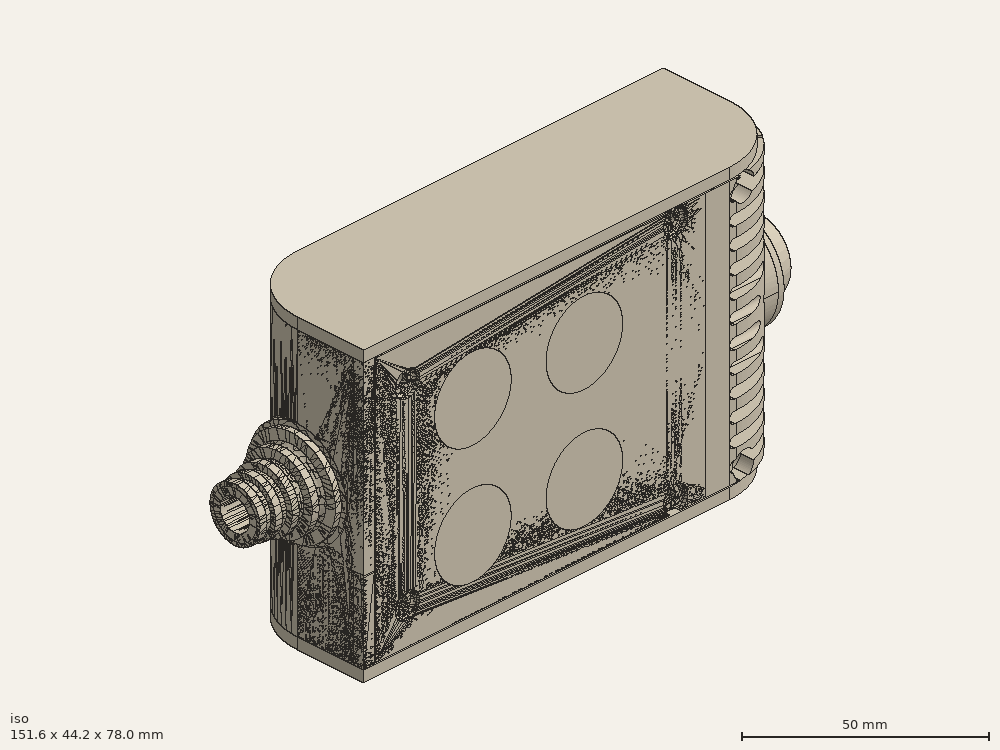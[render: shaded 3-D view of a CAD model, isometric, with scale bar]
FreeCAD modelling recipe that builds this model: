
FCSTD DOCUMENT  (FreeCAD 0.19R0.19.2)
Label: enclosure_172FCStd
License: All rights reserved
LicenseURL: http://en.wikipedia.org/wiki/All_rights_reserved
objects: Part::Revolution×146, Part::MultiFuse×141, Part::Feature×140, Sketcher::SketchObject×78, Part::Cut×66, Part::Cylinder×66, Part::Extrusion×63, Part::Fillet×56, Part::Box×36, App::MeasureDistance×4
note: 792 computed .brp shape members not serialized (recipe doc carries the construction recipe); baked Part::Feature solids carry a one-line shape summary decoded from their .brp

FEATURE [Sketcher::SketchObject] Sketch  label="topSketch"
  FullyConstrained = true
  sketch-geometry (20):
    g0: LineSegment StartX=5.21097e-06 StartY=3 StartZ=0 EndX=5.21097e-06 EndY=19 EndZ=0
    g1: ArcOfCircle CenterX=19 CenterY=19 CenterZ=0 NormalX=0 NormalY=0 NormalZ=1 AngleXU=0 Radius=19 StartAngle=1.5708 EndAngle=3.14159
    g2: ArcOfCircle CenterX=19 CenterY=19 CenterZ=0 NormalX=0 NormalY=0 NormalZ=1 AngleXU=0 Radius=16 StartAngle=1.5708 EndAngle=3.14159
    g3: LineSegment StartX=114 StartY=35 StartZ=0 EndX=19 EndY=35 EndZ=0
    g4: LineSegment StartX=5.21097e-06 StartY=3 StartZ=0 EndX=5.21097e-06 EndY=0 EndZ=0
    g5: LineSegment StartX=3 StartY=0 StartZ=0 EndX=5.21097e-06 EndY=0 EndZ=0
    g6: LineSegment StartX=3 StartY=19 StartZ=0 EndX=3 EndY=0 EndZ=0
    g7: LineSegment StartX=19 StartY=38 StartZ=0 EndX=124 EndY=38 EndZ=0
    g8: Circle CenterX=119 CenterY=35 CenterZ=0 NormalX=0 NormalY=0 NormalZ=1 AngleXU=0 Radius=1
    g9: Circle CenterX=121 CenterY=35 CenterZ=0 NormalX=0 NormalY=0 NormalZ=1 AngleXU=0 Radius=1
    g10: Circle CenterX=121 CenterY=33 CenterZ=0 NormalX=0 NormalY=0 NormalZ=1 AngleXU=0 Radius=1
    g11: BSplineCurve PolesCount=3 KnotsCount=2 Degree=2 IsPeriodic=0
    g12: GeomPoint X=119 Y=35 Z=0
    g13: GeomPoint X=121 Y=33 Z=0
    g14: LineSegment StartX=119 StartY=35 StartZ=0 EndX=114 EndY=35 EndZ=0
    g15: ArcOfCircle CenterX=105 CenterY=19 CenterZ=0 NormalX=0 NormalY=0 NormalZ=1 AngleXU=0 Radius=19 StartAngle=5.7297 EndAngle=6.28319
    g16: ArcOfCircle CenterX=105 CenterY=19 CenterZ=0 NormalX=0 NormalY=0 NormalZ=1 AngleXU=0 Radius=16 StartAngle=5.60905 EndAngle=6.28319
    g17: LineSegment StartX=121 StartY=33 StartZ=0 EndX=121 EndY=19 EndZ=0
    g18: LineSegment StartX=124 StartY=38 StartZ=0 EndX=124 EndY=19 EndZ=0
    g19: LineSegment StartX=117.5 StartY=9.01251 StartZ=0 EndX=121.163 EndY=9.0125 EndZ=0
  constraints (46):
    c: Vertical(g0)
    c: Block(g0)
    c: Coincident(g1,g0)
    c: Block(g1)
    c: Coincident(g2,g1)
    c: Block(g2)
    c: Coincident(g3,g2)
    c: Horizontal(g3)
    c: Tangent(g3,g2)
    c: Coincident(g4,g0)
    c: Distance(g4) = 3
    c: Vertical(g4)
    c: Coincident(g5,g4)
    c: Horizontal(g5)
    c: Coincident(g6,g2)
    c: Coincident(g6,g5)
    c: Vertical(g6)
    c: Horizontal(g7)
    c: Distance(g7) = 105
    c: Coincident(g7,g1)
    c: Block(g3)
    c: Weight(g8) = 1
    c: Equal(g8,g9)
    c: Equal(g8,g10)
    c: InternalAlignment(g8,g11)
    c: InternalAlignment(g9,g11)
    c: InternalAlignment(g10,g11)
    c: InternalAlignment(g12,g11)
    c: InternalAlignment(g13,g11)
    c: Block(g11)
    c: Coincident(g14,g11)
    c: Coincident(g14,g3)
    c: Horizontal(g14)
    c: Block(g15)
    c: Coincident(g16,g15)
    c: Block(g16)
    c: Coincident(g17,g11)
    c: Coincident(g17,g16)
    c: Vertical(g17)
    c: Distance(g17) = 14
    c: Coincident(g18,g7)
    c: Coincident(g18,g15)
    c: Vertical(g18)
    c: Distance(g18) = 19
    c: Coincident(g19,g16)
    c: Coincident(g19,g15)
FEATURE [Sketcher::SketchObject] Sketch001  label="bottomSketch"
  FullyConstrained = true
  sketch-geometry (32):
    g0: LineSegment StartX=3.3 StartY=-6.03275e-07 StartZ=0 EndX=98 EndY=-6.03275e-07 EndZ=0
    g1: ArcOfCircle CenterX=98 CenterY=19 CenterZ=0 NormalX=0 NormalY=0 NormalZ=1 AngleXU=0 Radius=19 StartAngle=4.71239 EndAngle=5.71103
    g2: LineSegment StartX=6.3 StartY=8 StartZ=0 EndX=3.3 EndY=8 EndZ=0
    g3: LineSegment StartX=3.3 StartY=8 StartZ=0 EndX=3.3 EndY=-6.03275e-07 EndZ=0
    g4: ArcOfCircle CenterX=8.3 CenterY=5 CenterZ=0 NormalX=0 NormalY=0 NormalZ=1 AngleXU=0 Radius=2 StartAngle=3.14159 EndAngle=4.71239
    g5: LineSegment StartX=6.3 StartY=8 StartZ=0 EndX=6.3 EndY=5 EndZ=0
    g6: ArcOfCircle CenterX=98 CenterY=19 CenterZ=0 NormalX=0 NormalY=0 NormalZ=1 AngleXU=0 Radius=12.7 StartAngle=4.71239 EndAngle=6.28319
    g7: LineSegment StartX=94.7 StartY=3 StartZ=0 EndX=8.3 EndY=3 EndZ=0
    g8-g12: Circle x5 (B-spline internal-alignment scaffolding for g13; pole/knot coordinates omitted)
    g13: BSplineCurve PolesCount=5 KnotsCount=3 Degree=3 IsPeriodic=0
    g14: GeomPoint X=98 Y=6.3 Z=0
    g15: GeomPoint X=96.3938 Y=4.71946 Z=0
    g16: GeomPoint X=94.7 Y=3 Z=0
    g17-g23: Circle x7 (B-spline internal-alignment scaffolding for g24; pole/knot coordinates omitted)
    g24: BSplineCurve PolesCount=7 KnotsCount=5 Degree=3 IsPeriodic=0
    g25-g29: GeomPoint x5 (B-spline internal-alignment scaffolding for g24; pole/knot coordinates omitted)
    g30: ArcOfCircle CenterX=98 CenterY=19 CenterZ=0 NormalX=0 NormalY=0 NormalZ=1 AngleXU=0 Radius=15.7 StartAngle=5.81226 EndAngle=6.28319
    g31: LineSegment StartX=110.7 StartY=19 StartZ=0 EndX=113.7 EndY=19 EndZ=0
  constraints (41):
    c: Horizontal(g0)
    c: Coincident(g1,g0)
    c: Block(g1)
    c: Horizontal(g2)
    c: Distance(g2) = 3
    c: Coincident(g3,g2)
    c: Vertical(g3)
    c: Coincident(g3,g0)
    c: Block(g4)
    c: Block(g2)
    c: Coincident(g5,g2)
    c: Coincident(g5,g4)
    c: Vertical(g5)
    c: Coincident(g6,g1)
    c: Block(g6)
    c: Coincident(g7,g4)
    c: Horizontal(g7)
    c: Block(g0)
    c: Block(g7)
    c: Block(g3)
    c: Coincident(g13,g6)
    c: Weight(g8) = 1
    c: Equal(g8, g9-g12) x4
    c: Coincident(g13,g7)
    c: InternalAlignment(g8-g12 -> g13) x5
    c: InternalAlignment(g14,g13)
    c: InternalAlignment(g15,g13)
    c: InternalAlignment(g16,g13)
    c: Block(g13)
    c: Weight(g17) = 1
    c: Equal(g17, g18-g23) x6
    c: Coincident(g24,g1)
    c: InternalAlignment(g17-g23 -> g24) x7
    c: InternalAlignment(g25-g29 -> g24) x5
    c: Block(g24)
    c: Coincident(g30,g24)
    c: Coincident(g31,g6)
    c: Coincident(g31,g30)
    c: Horizontal(g31)
    c: Block(g31)
    c: Block(g30)
FEATURE [Part::Extrusion] Extrude  label="top"
  Base = -> Sketch
  Dir = (0,0,1)
  DirMode = 2
  FaceMakerClass = Part::FaceMakerBullseye
  LengthFwd = 72
  LengthRev = 0
  Solid = true
  Symmetric = false
FEATURE [Part::Extrusion] Extrude001  label="bottom"
  Base = -> Sketch001
  Dir = (0,0,1)
  DirMode = 2
  FaceMakerClass = Part::FaceMakerBullseye
  LengthFwd = 71.4
  LengthRev = 0
  Placement = pos=(0,0,0.3) rot=(0,0,1;0rad)
  Solid = true
  Symmetric = false
FEATURE [Sketcher::SketchObject] Sketch002  label="topSketch001"
  FullyConstrained = true
  sketch-geometry (6):
    g0: ArcOfCircle CenterX=19 CenterY=19 CenterZ=0 NormalX=0 NormalY=0 NormalZ=1 AngleXU=0 Radius=19 StartAngle=1.5708 EndAngle=3.14159
    g1: LineSegment StartX=5.22862e-06 StartY=19 StartZ=0 EndX=5.22862e-06 EndY=1.19904e-11 EndZ=0
    g2: LineSegment StartX=19 StartY=38 StartZ=0 EndX=124 EndY=38 EndZ=0
    g3: LineSegment StartX=5.22862e-06 StartY=1.19904e-11 StartZ=0 EndX=105 EndY=1.19904e-11 EndZ=0
    g4: ArcOfCircle CenterX=105 CenterY=19 CenterZ=0 NormalX=0 NormalY=0 NormalZ=1 AngleXU=0 Radius=19 StartAngle=4.71239 EndAngle=6.28319
    g5: LineSegment StartX=124 StartY=38 StartZ=0 EndX=124 EndY=19 EndZ=0
  constraints (16):
    c: Block(g0)
    c: Coincident(g1,g0)
    c: Vertical(g1)
    c: Horizontal(g2)
    c: Distance(g2) = 105
    c: Coincident(g2,g0)
    c: Distance(g1) = 19
    c: Coincident(g3,g1)
    c: Horizontal(g3)
    c: Distance(g3) = 105
    c: Block(g4)
    c: Coincident(g4,g3)
    c: Coincident(g5,g2)
    c: Coincident(g5,g4)
    c: Vertical(g5)
    c: Distance(g5) = 19
FEATURE [Part::Extrusion] Extrude002  label="sideA"
  Base = -> Sketch002
  Dir = (0,0,1)
  DirMode = 2
  FaceMakerClass = Part::FaceMakerBullseye
  LengthFwd = 3
  LengthRev = 0
  Placement = pos=(0,0,-3) rot=(0,0,1;0rad)
  Solid = true
  Symmetric = false
FEATURE [Sketcher::SketchObject] Sketch003  label="topSketch002"
  FullyConstrained = true
  sketch-geometry (6):
    g0: LineSegment StartX=19 StartY=38 StartZ=0 EndX=117 EndY=38 EndZ=0
    g1: ArcOfCircle CenterX=19 CenterY=19 CenterZ=0 NormalX=0 NormalY=0 NormalZ=1 AngleXU=0 Radius=19 StartAngle=1.5708 EndAngle=3.14159
    g2: LineSegment StartX=117 StartY=38 StartZ=0 EndX=117 EndY=19 EndZ=0
    g3: LineSegment StartX=98 StartY=1.0161e-12 StartZ=0 EndX=5.22862e-06 EndY=1.0161e-12 EndZ=0
    g4: LineSegment StartX=5.22862e-06 StartY=19 StartZ=0 EndX=5.22862e-06 EndY=1.0161e-12 EndZ=0
    g5: ArcOfCircle CenterX=98 CenterY=19 CenterZ=0 NormalX=0 NormalY=0 NormalZ=1 AngleXU=0 Radius=19 StartAngle=4.71239 EndAngle=6.28319
  constraints (16):
    c: Horizontal(g0)
    c: Distance(g0) = 98
    c: Coincident(g1,g0)
    c: Block(g1)
    c: Coincident(g2,g0)
    c: Vertical(g2)
    c: Distance(g2) = 19
    c: Horizontal(g3)
    c: Coincident(g4,g1)
    c: Vertical(g4)
    c: Coincident(g3,g4)
    c: Block(g3)
    c: Coincident(g5,g2)
    c: Coincident(g5,g3)
    c: Block(g0)
    c: Block(g5)
FEATURE [Sketcher::SketchObject] Sketch004
  FullyConstrained = true
  MapMode = 3
  Placement = pos=(0,0,0) rot=(1,0,0;1.5708rad)
  Support = -> [Extrude]
  sketch-geometry (8):
    g0: Circle CenterX=80.351 CenterY=-67.6202 CenterZ=0 NormalX=0 NormalY=0 NormalZ=1 AngleXU=0 Radius=2
    g1: Circle CenterX=80.351 CenterY=-67.6202 CenterZ=0 NormalX=0 NormalY=0 NormalZ=1 AngleXU=0 Radius=3
    g2: Circle CenterX=80.351 CenterY=-4.92017 CenterZ=0 NormalX=0 NormalY=0 NormalZ=1 AngleXU=0 Radius=2
    g3: Circle CenterX=80.351 CenterY=-4.92017 CenterZ=0 NormalX=0 NormalY=0 NormalZ=1 AngleXU=0 Radius=3
    g4: Circle CenterX=23.851 CenterY=-4.92017 CenterZ=0 NormalX=0 NormalY=0 NormalZ=1 AngleXU=0 Radius=2
    g5: Circle CenterX=23.851 CenterY=-4.92017 CenterZ=0 NormalX=0 NormalY=0 NormalZ=1 AngleXU=0 Radius=3
    g6: Circle CenterX=23.851 CenterY=-67.6202 CenterZ=0 NormalX=0 NormalY=0 NormalZ=1 AngleXU=0 Radius=2
    g7: Circle CenterX=23.851 CenterY=-67.6202 CenterZ=0 NormalX=0 NormalY=0 NormalZ=1 AngleXU=0 Radius=3
  constraints (8):
    c: Block(g3)
    c: Block(g2)
    c: Block(g1)
    c: Block(g0)
    c: Block(g6)
    c: Block(g7)
    c: Block(g4)
    c: Block(g5)
FEATURE [Part::Extrusion] Extrude004
  Base = -> Sketch004
  Dir = (0,-1,2e-16)
  DirMode = 2
  FaceMakerClass = Part::FaceMakerBullseye
  LengthFwd = 6
  LengthRev = 0
  Placement = pos=(0,9,0) rot=(0,0,1;0rad)
  Solid = true
  Symmetric = false
FEATURE [Sketcher::SketchObject] Sketch005
  FullyConstrained = true
  MapMode = 3
  Placement = pos=(0,0,0) rot=(1,0,0;1.5708rad)
  Support = -> [Extrude]
  sketch-geometry (8):
    g0: Circle CenterX=80.351 CenterY=-67.6202 CenterZ=0 NormalX=0 NormalY=0 NormalZ=1 AngleXU=0 Radius=3
    g1: Circle CenterX=80.351 CenterY=-4.92017 CenterZ=0 NormalX=0 NormalY=0 NormalZ=1 AngleXU=0 Radius=3
    g2: Circle CenterX=23.851 CenterY=-4.92017 CenterZ=0 NormalX=0 NormalY=0 NormalZ=1 AngleXU=0 Radius=3
    g3: Circle CenterX=23.851 CenterY=-67.6202 CenterZ=0 NormalX=0 NormalY=0 NormalZ=1 AngleXU=0 Radius=3
    g4: Circle CenterX=23.851 CenterY=-67.6202 CenterZ=0 NormalX=0 NormalY=0 NormalZ=1 AngleXU=0 Radius=5
    g5: Circle CenterX=80.351 CenterY=-67.6202 CenterZ=0 NormalX=0 NormalY=0 NormalZ=1 AngleXU=0 Radius=5
    g6: Circle CenterX=23.851 CenterY=-4.92017 CenterZ=0 NormalX=0 NormalY=0 NormalZ=1 AngleXU=0 Radius=5
    g7: Circle CenterX=80.351 CenterY=-4.92017 CenterZ=0 NormalX=0 NormalY=0 NormalZ=1 AngleXU=0 Radius=5
  constraints (8):
    c: Block(g1)
    c: Block(g0)
    c: Block(g3)
    c: Block(g2)
    c: Block(g5)
    c: Block(g4)
    c: Block(g6)
    c: Block(g7)
FEATURE [Part::Extrusion] Extrude005
  Base = -> Sketch005
  Dir = (0,-1,2e-16)
  DirMode = 2
  FaceMakerClass = Part::FaceMakerBullseye
  LengthFwd = 2
  LengthRev = 0
  Solid = true
  Symmetric = false
FEATURE [Sketcher::SketchObject] Sketch006
  FullyConstrained = true
  MapMode = 3
  Placement = pos=(0,0,0) rot=(1,0,0;1.5708rad)
  sketch-geometry (8):
    g0: Circle CenterX=80.351 CenterY=-67.6202 CenterZ=0 NormalX=0 NormalY=0 NormalZ=1 AngleXU=0 Radius=3
    g1: Circle CenterX=80.351 CenterY=-4.92017 CenterZ=0 NormalX=0 NormalY=0 NormalZ=1 AngleXU=0 Radius=3
    g2: Circle CenterX=23.851 CenterY=-4.92017 CenterZ=0 NormalX=0 NormalY=0 NormalZ=1 AngleXU=0 Radius=3
    g3: Circle CenterX=23.851 CenterY=-67.6202 CenterZ=0 NormalX=0 NormalY=0 NormalZ=1 AngleXU=0 Radius=3
    g4: Circle CenterX=23.851 CenterY=-67.6202 CenterZ=0 NormalX=0 NormalY=0 NormalZ=1 AngleXU=0 Radius=5
    g5: Circle CenterX=80.351 CenterY=-67.6202 CenterZ=0 NormalX=0 NormalY=0 NormalZ=1 AngleXU=0 Radius=5
    g6: Circle CenterX=23.851 CenterY=-4.92017 CenterZ=0 NormalX=0 NormalY=0 NormalZ=1 AngleXU=0 Radius=5
    g7: Circle CenterX=80.351 CenterY=-4.92017 CenterZ=0 NormalX=0 NormalY=0 NormalZ=1 AngleXU=0 Radius=5
  constraints (8):
    c: Block(g1)
    c: Block(g0)
    c: Block(g3)
    c: Block(g2)
    c: Block(g5)
    c: Block(g4)
    c: Block(g6)
    c: Block(g7)
FEATURE [Part::Extrusion] Extrude007
  Base = -> Sketch006
  Dir = (0,-1,2e-16)
  DirMode = 2
  FaceMakerClass = Part::FaceMakerBullseye
  LengthFwd = 2
  LengthRev = 0
  Solid = true
  Symmetric = false
FEATURE [Part::Fillet] Fillet
  Base = -> Extrude007
  Edges = 4 edges r=1.99: [Edge6,Edge12,Edge18,Edge24]
FEATURE [Part::Cut] Cut
  Base = -> Extrude005
  Placement = pos=(0,5,0) rot=(0,0,1;0rad)
  Tool = -> Fillet
FEATURE [Part::MultiFuse] Fusion  label="pCBScrews"
  Placement = pos=(-2.5,0,72.3) rot=(0,0,1;0rad)
  Shapes = -> [Extrude004,Cut]
FEATURE [App::MeasureDistance] Distance  label="Distance: 0.69 mm"
  Distance = 0.685967
  P1 = (24.0138,2.9647,0.3)
  P2 = (23.8901,3,-0.373787)
FEATURE [App::MeasureDistance] Distance001  label="Distance: 0.53 mm"
  Distance = 0.533607
  P1 = (80.2939,3,72.2334)
  P2 = (80.281,2.99661,71.7)
FEATURE [Part::Fillet] Fillet001
  Base = -> Extrude001
  Edges = 1 edges r=2.4: [Edge17]
FEATURE [Part::Fillet] Fillet002  label="bottom001"
  Base = -> Fillet001
  Edges = 1 edges r=2.4: [Edge36]
FEATURE [Part::Fillet] Fillet003  label="top001"
  Base = -> Extrude
  Edges = 1 edges r=2: [Edge1]
FEATURE [Sketcher::SketchObject] Sketch007
  FullyConstrained = true
  sketch-geometry (16):
    g0: LineSegment StartX=4 StartY=0 StartZ=0 EndX=4 EndY=2.4 EndZ=0
    g1: LineSegment StartX=4 StartY=2.4 StartZ=0 EndX=7 EndY=2.4 EndZ=0
    g2: LineSegment StartX=4 StartY=0 StartZ=0 EndX=5.7 EndY=0 EndZ=0
    g3: LineSegment StartX=5.7 StartY=0 StartZ=0 EndX=5.7 EndY=-5.6 EndZ=0
    g4-g8: Circle x5 (B-spline internal-alignment scaffolding for g9; pole/knot coordinates omitted)
    g9: BSplineCurve PolesCount=5 KnotsCount=3 Degree=3 IsPeriodic=0
    g10: GeomPoint X=7 Y=2.4 Z=0
    g11: GeomPoint X=10.4582 Y=-1.55472 Z=0
    g12: GeomPoint X=14 Y=-5.6 Z=0
    g13: LineSegment StartX=14 StartY=-5.6 StartZ=0 EndX=14 EndY=-14.1 EndZ=0
    g14: LineSegment StartX=14 StartY=-14.1 StartZ=0 EndX=6.5 EndY=-14.1 EndZ=0
    g15: LineSegment StartX=5.7 StartY=-5.6 StartZ=0 EndX=6.5 EndY=-14.1 EndZ=0
  constraints (28):
    c: Distance(g0) = 2.4
    c: Vertical(g0)
    c: Block(g0)
    c: Coincident(g1,g0)
    c: Horizontal(g1)
    c: Distance(g1) = 3
    c: Coincident(g2,g0)
    c: Horizontal(g2)
    c: Distance(g2) = 1.7
    c: Coincident(g3,g2)
    c: Vertical(g3)
    c: Distance(g3) = 5.6
    c: Coincident(g9,g1)
    c: Weight(g4) = 1
    c: Equal(g4, g5-g8) x4
    c: InternalAlignment(g4-g8 -> g9) x5
    c: InternalAlignment(g10,g9)
    c: InternalAlignment(g11,g9)
    c: InternalAlignment(g12,g9)
    c: Block(g9)
    c: Coincident(g13,g9)
    c: Vertical(g13)
    c: Distance(g13) = 8.5
    c: Coincident(g14,g13)
    c: Horizontal(g14)
    c: Distance(g14) = 7.5
    c: Coincident(g15,g3)
    c: Coincident(g15,g14)
FEATURE [Part::Feature] Face
  shape: bbox 10 x 16.5 x 2e-07 mm, 1 faces, 0 solids (baked)
FEATURE [Part::Revolution] Revolve  label="plugHousing"
  Angle = 360
  Axis = (0,1,0)
  Base = (0,0,0)
  FaceMakerClass = Part::FaceMakerBullseye
  Placement = pos=(0,0,36.15) rot=(0,0,1;0rad)
  Solid = false
  Source = -> Face
  Symmetric = false
FEATURE [Part::Feature] Face001
  shape: bbox 10 x 16.5 x 2e-07 mm, 1 faces, 0 solids (baked)
FEATURE [Part::Revolution] Revolve001  label="plugHousing001"
  Angle = 360
  Axis = (0,1,0)
  Base = (0,0,0)
  FaceMakerClass = Part::FaceMakerBullseye
  Placement = pos=(0,0,36.15) rot=(0,0,1;0rad)
  Solid = false
  Source = -> Face001
  Symmetric = false
FEATURE [Part::MultiFuse] Fusion001  label="plugHousing002"
  Placement = pos=(0,0,0) rot=(0,0,1;1.5708rad)
  Shapes = -> [Revolve001,Revolve]
FEATURE [Part::Feature] Face002
  shape: bbox 10 x 16.5 x 2e-07 mm, 1 faces, 0 solids (baked)
FEATURE [Part::Revolution] Revolve003  label="plugHousing005"
  Angle = 360
  Axis = (0,1,0)
  Base = (0,0,0)
  FaceMakerClass = Part::FaceMakerBullseye
  Placement = pos=(0,0,36.15) rot=(0,0,1;0rad)
  Solid = false
  Source = -> Face002
  Symmetric = false
FEATURE [Part::Feature] Face003
  shape: bbox 10 x 16.5 x 2e-07 mm, 1 faces, 0 solids (baked)
FEATURE [Part::Revolution] Revolve002  label="plugHousing003"
  Angle = 360
  Axis = (0,1,0)
  Base = (0,0,0)
  FaceMakerClass = Part::FaceMakerBullseye
  Placement = pos=(0,0,36.15) rot=(0,0,1;0rad)
  Solid = false
  Source = -> Face003
  Symmetric = false
FEATURE [Part::MultiFuse] Fusion002  label="plugHousing004"
  Placement = pos=(0,0,0) rot=(0,0,1;1.5708rad)
  Shapes = -> [Revolve002,Revolve003]
FEATURE [Part::MultiFuse] Fusion003  label="plugHousing006"
  Placement = pos=(0,19,0) rot=(0,0,1;3.14159rad)
  Shapes = -> [Fusion002,Fusion001]
FEATURE [Part::Feature] Face004
  shape: bbox 10 x 16.5 x 2e-07 mm, 1 faces, 0 solids (baked)
FEATURE [Part::Revolution] Revolve006  label="plugHousing010"
  Angle = 360
  Axis = (0,1,0)
  Base = (0,0,0)
  FaceMakerClass = Part::FaceMakerBullseye
  Placement = pos=(0,0,36.15) rot=(0,0,1;0rad)
  Solid = false
  Source = -> Face004
  Symmetric = false
FEATURE [Part::Feature] Face005
  shape: bbox 10 x 16.5 x 2e-07 mm, 1 faces, 0 solids (baked)
FEATURE [Part::Revolution] Revolve007  label="plugHousing011"
  Angle = 360
  Axis = (0,1,0)
  Base = (0,0,0)
  FaceMakerClass = Part::FaceMakerBullseye
  Placement = pos=(0,0,36.15) rot=(0,0,1;0rad)
  Solid = false
  Source = -> Face005
  Symmetric = false
FEATURE [Part::Feature] Face006
  shape: bbox 10 x 16.5 x 2e-07 mm, 1 faces, 0 solids (baked)
FEATURE [Part::Revolution] Revolve004  label="plugHousing007"
  Angle = 360
  Axis = (0,1,0)
  Base = (0,0,0)
  FaceMakerClass = Part::FaceMakerBullseye
  Placement = pos=(0,0,36.15) rot=(0,0,1;0rad)
  Solid = false
  Source = -> Face006
  Symmetric = false
FEATURE [Part::MultiFuse] Fusion004  label="plugHousing009"
  Placement = pos=(0,0,0) rot=(0,0,1;1.5708rad)
  Shapes = -> [Revolve004,Revolve007]
FEATURE [Part::Feature] Face007
  shape: bbox 10 x 16.5 x 2e-07 mm, 1 faces, 0 solids (baked)
FEATURE [Part::Revolution] Revolve005  label="plugHousing008"
  Angle = 360
  Axis = (0,1,0)
  Base = (0,0,0)
  FaceMakerClass = Part::FaceMakerBullseye
  Placement = pos=(0,0,36.15) rot=(0,0,1;0rad)
  Solid = false
  Source = -> Face007
  Symmetric = false
FEATURE [Part::MultiFuse] Fusion005  label="plugHousing012"
  Placement = pos=(0,0,0) rot=(0,0,1;1.5708rad)
  Shapes = -> [Revolve006,Revolve005]
FEATURE [Part::MultiFuse] Fusion006  label="plugHousing013"
  Placement = pos=(0,19,0) rot=(0,0,1;3.14159rad)
  Shapes = -> [Fusion005,Fusion004]
FEATURE [Part::MultiFuse] Fusion007  label="plugHousing014"
  Placement = pos=(122.621,0,-0.15) rot=(0,0,1;0rad)
  Shapes = -> [Fusion003,Fusion006]
FEATURE [Part::Cylinder] Cylinder002
  Angle = 360
  AttacherType = Attacher::AttachEngine3D
  Height = 20
  Placement = pos=(0,0,36.15) rot=(0,0,1;0rad)
  Radius = 4
FEATURE [Part::Cylinder] Cylinder003
  Angle = 360
  AttacherType = Attacher::AttachEngine3D
  Height = 10
  Placement = pos=(0,0,36.15) rot=(0,0,1;0rad)
  Radius = 4
FEATURE [Part::MultiFuse] Fusion009  label="removeToCreateHoleForPlugHousing"
  Placement = pos=(70,19,36.15) rot=(0,1,0;1.5708rad)
  Shapes = -> [Cylinder002,Cylinder003]
FEATURE [Part::Cylinder] Cylinder004
  Angle = 360
  AttacherType = Attacher::AttachEngine3D
  Height = 20
  Placement = pos=(0,0,36.15) rot=(0,0,1;0rad)
  Radius = 4
FEATURE [Part::Cylinder] Cylinder005
  Angle = 360
  AttacherType = Attacher::AttachEngine3D
  Height = 10
  Placement = pos=(0,0,36.15) rot=(0,0,1;0rad)
  Radius = 4
FEATURE [Part::MultiFuse] Fusion010  label="removeToCreateHoleForPlugHousing001"
  Placement = pos=(70,19,36.15) rot=(0,1,0;1.5708rad)
  Shapes = -> [Cylinder004,Cylinder005]
FEATURE [Part::Cut] Cut001
  Base = -> Fillet003
  Tool = -> Fusion010
FEATURE [Part::Cut] Cut002  label="Bottom"
  Base = -> Fillet002
  Tool = -> Fusion009
FEATURE [Part::Feature] Face008
  shape: bbox 10 x 16.5 x 2e-07 mm, 1 faces, 0 solids (baked)
FEATURE [Part::Revolution] Revolve011  label="plugHousing021"
  Angle = 360
  Axis = (0,1,0)
  Base = (0,0,0)
  FaceMakerClass = Part::FaceMakerBullseye
  Placement = pos=(0,0,36.15) rot=(0,0,1;0rad)
  Solid = false
  Source = -> Face008
  Symmetric = false
FEATURE [Part::Feature] Face009
  shape: bbox 10 x 16.5 x 2e-07 mm, 1 faces, 0 solids (baked)
FEATURE [Part::Revolution] Revolve012  label="plugHousing022"
  Angle = 360
  Axis = (0,1,0)
  Base = (0,0,0)
  FaceMakerClass = Part::FaceMakerBullseye
  Placement = pos=(0,0,36.15) rot=(0,0,1;0rad)
  Solid = false
  Source = -> Face009
  Symmetric = false
FEATURE [Part::Feature] Face010 .. Face013  x4 (patterned run collapsed; names and placements below)
  shape: bbox 10 x 16.5 x 2e-07 mm, 1 faces, 0 solids (baked)
FEATURE [Part::Revolution] Revolve015  label="plugHousing027"
  Angle = 360
  Axis = (0,1,0)
  Base = (0,0,0)
  FaceMakerClass = Part::FaceMakerBullseye
  Placement = pos=(0,0,36.15) rot=(0,0,1;0rad)
  Solid = false
  Source = -> Face013
  Symmetric = false
FEATURE [Part::Feature] Face014
  shape: bbox 10 x 16.5 x 2e-07 mm, 1 faces, 0 solids (baked)
FEATURE [Part::Feature] Face015
  shape: bbox 10 x 16.5 x 2e-07 mm, 1 faces, 0 solids (baked)
FEATURE [Part::Feature] Face016
  shape: bbox 10 x 16.5 x 2e-07 mm, 1 faces, 0 solids (baked)
FEATURE [Part::Revolution] Revolve019  label="plugHousing033"
  Angle = 360
  Axis = (0,1,0)
  Base = (0,0,0)
  FaceMakerClass = Part::FaceMakerBullseye
  Placement = pos=(0,0,36.15) rot=(0,0,1;0rad)
  Solid = false
  Source = -> Face016
  Symmetric = false
FEATURE [Part::Feature] Face017
  shape: bbox 10 x 16.5 x 2e-07 mm, 1 faces, 0 solids (baked)
FEATURE [Part::Revolution] Revolve020  label="plugHousing034"
  Angle = 360
  Axis = (0,1,0)
  Base = (0,0,0)
  FaceMakerClass = Part::FaceMakerBullseye
  Placement = pos=(0,0,36.15) rot=(0,0,1;0rad)
  Solid = false
  Source = -> Face017
  Symmetric = false
FEATURE [Part::Feature] Face018
  shape: bbox 10 x 16.5 x 2e-07 mm, 1 faces, 0 solids (baked)
FEATURE [Part::Revolution] Revolve016  label="plugHousing030"
  Angle = 360
  Axis = (0,1,0)
  Base = (0,0,0)
  FaceMakerClass = Part::FaceMakerBullseye
  Placement = pos=(0,0,36.15) rot=(0,0,1;0rad)
  Solid = false
  Source = -> Face018
  Symmetric = false
FEATURE [Part::MultiFuse] Fusion020  label="plugHousing038"
  Placement = pos=(0,0,0) rot=(0,0,1;1.5708rad)
  Shapes = -> [Revolve016,Revolve020]
FEATURE [Part::Feature] Face019
  shape: bbox 10 x 16.5 x 2e-07 mm, 1 faces, 0 solids (baked)
FEATURE [Part::Feature] Face020
  shape: bbox 10 x 16.5 x 2e-07 mm, 1 faces, 0 solids (baked)
FEATURE [Part::Revolution] Revolve017  label="plugHousing031"
  Angle = 360
  Axis = (0,1,0)
  Base = (0,0,0)
  FaceMakerClass = Part::FaceMakerBullseye
  Placement = pos=(0,0,36.15) rot=(0,0,1;0rad)
  Solid = false
  Source = -> Face020
  Symmetric = false
FEATURE [Part::MultiFuse] Fusion021  label="plugHousing039"
  Placement = pos=(0,0,0) rot=(0,0,1;1.5708rad)
  Shapes = -> [Revolve019,Revolve017]
FEATURE [Part::MultiFuse] Fusion023  label="plugHousing041"
  Placement = pos=(0,19,0) rot=(0,0,1;3.14159rad)
  Shapes = -> [Fusion021,Fusion020]
FEATURE [Part::Revolution] Revolve022  label="plugHousing043"
  Angle = 360
  Axis = (0,1,0)
  Base = (0,0,0)
  FaceMakerClass = Part::FaceMakerBullseye
  Placement = pos=(0,0,36.15) rot=(0,0,1;0rad)
  Solid = false
  Source = -> Face019
  Symmetric = false
FEATURE [Part::Feature] Face021
  shape: bbox 10 x 16.5 x 2e-07 mm, 1 faces, 0 solids (baked)
FEATURE [Part::Revolution] Revolve023  label="plugHousing044"
  Angle = 360
  Axis = (0,1,0)
  Base = (0,0,0)
  FaceMakerClass = Part::FaceMakerBullseye
  Placement = pos=(0,0,36.15) rot=(0,0,1;0rad)
  Solid = false
  Source = -> Face021
  Symmetric = false
FEATURE [Part::Feature] Face022
  shape: bbox 10 x 16.5 x 2e-07 mm, 1 faces, 0 solids (baked)
FEATURE [Part::Revolution] Revolve018  label="plugHousing032"
  Angle = 360
  Axis = (0,1,0)
  Base = (0,0,0)
  FaceMakerClass = Part::FaceMakerBullseye
  Placement = pos=(0,0,36.15) rot=(0,0,1;0rad)
  Solid = false
  Source = -> Face022
  Symmetric = false
FEATURE [Part::MultiFuse] Fusion022  label="plugHousing040"
  Placement = pos=(0,0,0) rot=(0,0,1;1.5708rad)
  Shapes = -> [Revolve018,Revolve023]
FEATURE [Part::Feature] Face023
  shape: bbox 10 x 16.5 x 2e-07 mm, 1 faces, 0 solids (baked)
FEATURE [Part::Revolution] Revolve021  label="plugHousing035"
  Angle = 360
  Axis = (0,1,0)
  Base = (0,0,0)
  FaceMakerClass = Part::FaceMakerBullseye
  Placement = pos=(0,0,36.15) rot=(0,0,1;0rad)
  Solid = false
  Source = -> Face023
  Symmetric = false
FEATURE [Part::MultiFuse] Fusion018  label="plugHousing036"
  Placement = pos=(0,0,0) rot=(0,0,1;1.5708rad)
  Shapes = -> [Revolve022,Revolve021]
FEATURE [Part::MultiFuse] Fusion019  label="plugHousing037"
  Placement = pos=(0,19,0) rot=(0,0,1;3.14159rad)
  Shapes = -> [Fusion018,Fusion022]
FEATURE [Part::MultiFuse] Fusion024  label="plugHousing042"
  Placement = pos=(122.621,0,-0.15) rot=(0,0,1;0rad)
  Shapes = -> [Fusion023,Fusion019]
FEATURE [Part::Cylinder] Cylinder006
  Angle = 360
  AttacherType = Attacher::AttachEngine3D
  Height = 20
  Placement = pos=(0,0,36.15) rot=(0,0,1;0rad)
  Radius = 14.3
FEATURE [Part::Cylinder] Cylinder007
  Angle = 360
  AttacherType = Attacher::AttachEngine3D
  Height = 10
  Placement = pos=(0,0,36.15) rot=(0,0,1;0rad)
  Radius = 4
FEATURE [Part::MultiFuse] Fusion026  label="removeToCreteHoleForPlugHousing"
  Placement = pos=(70,19,36) rot=(0,1,0;1.5708rad)
  Shapes = -> [Cylinder006,Cylinder007]
FEATURE [Part::Box] Box001  label="Cube001"
  AttacherType = Attacher::AttachEngine3D
  Height = 28
  Length = 3
  Placement = pos=(110.7,19,22) rot=(0,0,1;0rad)
  Width = 15.7
FEATURE [Part::Cut] Cut003  label="top002"
  Base = -> Cut001
  Tool = -> Fusion007
FEATURE [Part::Revolution] Revolve008  label="plugHousing015"
  Angle = 360
  Axis = (0,1,0)
  Base = (0,0,0)
  FaceMakerClass = Part::FaceMakerBullseye
  Placement = pos=(0,0,36.15) rot=(0,0,1;0rad)
  Solid = false
  Source = -> Face010
  Symmetric = false
FEATURE [Part::MultiFuse] Fusion013  label="plugHousing020"
  Placement = pos=(0,0,0) rot=(0,0,1;1.5708rad)
  Shapes = -> [Revolve008,Revolve012]
FEATURE [Part::Cut] Cut004  label="top003"
  Base = -> Cut003
  Placement = pos=(1,0,0) rot=(0,0,1;0rad)
  Tool = -> Fusion026
FEATURE [Part::Cylinder] Cylinder008
  Angle = 360
  AttacherType = Attacher::AttachEngine3D
  Height = 20
  Placement = pos=(0,0,36.15) rot=(0,0,1;0rad)
  Radius = 10.3
FEATURE [Part::Cylinder] Cylinder009
  Angle = 360
  AttacherType = Attacher::AttachEngine3D
  Height = 10
  Placement = pos=(0,0,36.15) rot=(0,0,1;0rad)
  Radius = 4
FEATURE [Part::MultiFuse] Fusion027  label="removeToCreteHoleForPlugHousing001"
  Placement = pos=(70,19,36) rot=(0,1,0;1.5708rad)
  Shapes = -> [Cylinder008,Cylinder009]
FEATURE [Part::Cut] Cut005  label="plugHousingTab"
  Base = -> Box001
  Tool = -> Fusion027
FEATURE [Part::MultiFuse] Fusion028  label="plugHousing045"
  Shapes = -> [Fusion024,Cut005]
FEATURE [Part::Box] Box002  label="Cube002"
  AttacherType = Attacher::AttachEngine3D
  Height = 28.8
  Length = 3
  Placement = pos=(107.3,28,21.6) rot=(0,0,1;0rad)
  Width = 7
FEATURE [Part::Box] Box003  label="Cube003"
  AttacherType = Attacher::AttachEngine3D
  Height = 3
  Length = 6.4
  Placement = pos=(107.3,28,18.6) rot=(0,0,1;0rad)
  Width = 7
FEATURE [Part::Box] Box004  label="Cube004"
  AttacherType = Attacher::AttachEngine3D
  Height = 3
  Length = 6.4
  Placement = pos=(107.3,28,50.4) rot=(0,0,1;0rad)
  Width = 7
FEATURE [Part::MultiFuse] Fusion029  label="plugHousingBracketHolder"
  Shapes = -> [Box004,Box002,Box003]
FEATURE [Part::Cylinder] Cylinder010
  Angle = 360
  AttacherType = Attacher::AttachEngine3D
  Height = 20
  Placement = pos=(0,0,36.15) rot=(0,0,1;0rad)
  Radius = 14.3
FEATURE [Part::Cylinder] Cylinder011
  Angle = 360
  AttacherType = Attacher::AttachEngine3D
  Height = 10
  Placement = pos=(0,0,36.15) rot=(0,0,1;0rad)
  Radius = 4
FEATURE [Part::MultiFuse] Fusion030  label="removeToCreteHoleForPlugHousing002"
  Placement = pos=(70,19,36) rot=(0,1,0;1.5708rad)
  Shapes = -> [Cylinder010,Cylinder011]
FEATURE [Part::Cut] Cut006  label="plugHousingBracketHolder001"
  Base = -> Fusion029
  Tool = -> Fusion030
FEATURE [Part::Cylinder] Cylinder012
  Angle = 360
  AttacherType = Attacher::AttachEngine3D
  Height = 20
  Placement = pos=(0,0,36.15) rot=(0,0,1;0rad)
  Radius = 7
FEATURE [Part::Cylinder] Cylinder013
  Angle = 360
  AttacherType = Attacher::AttachEngine3D
  Height = 10
  Placement = pos=(0,0,36.15) rot=(0,0,1;0rad)
  Radius = 4
FEATURE [Part::MultiFuse] Fusion032  label="removeToCreteHoleForPlugHousing003"
  Placement = pos=(70,19,36) rot=(0,1,0;1.5708rad)
  Shapes = -> [Cylinder012,Cylinder013]
FEATURE [Part::Cut] Cut007  label="bottom002"
  Base = -> Cut002
  Tool = -> Fusion032
FEATURE [Sketcher::SketchObject] Sketch008
  FullyConstrained = true
  sketch-geometry (54):
    g0: LineSegment StartX=-4.2 StartY=0 StartZ=0 EndX=-6.2 EndY=0 EndZ=0
    g1: LineSegment StartX=-14 StartY=-18 StartZ=0 EndX=-14 EndY=-26.5 EndZ=0
    g2: LineSegment StartX=-4.2 StartY=0 StartZ=0 EndX=-4.2 EndY=-13.4877 EndZ=0
    g3: Circle CenterX=-4.2 CenterY=-13.4877 CenterZ=0 NormalX=0 NormalY=0 NormalZ=1 AngleXU=0 Radius=1
    g4: Circle CenterX=-4.2 CenterY=-26.5 CenterZ=0 NormalX=0 NormalY=0 NormalZ=1 AngleXU=0 Radius=1
    g5: Circle CenterX=-8.2 CenterY=-26.5 CenterZ=0 NormalX=0 NormalY=0 NormalZ=1 AngleXU=0 Radius=1
    g6: BSplineCurve PolesCount=3 KnotsCount=2 Degree=2 IsPeriodic=0
    g7: GeomPoint X=-4.2 Y=-13.4877 Z=0
    g8: GeomPoint X=-8.2 Y=-26.5 Z=0
    g9: LineSegment StartX=-14 StartY=-26.5 StartZ=0 EndX=-8.2 EndY=-26.5 EndZ=0
    g10: LineSegment StartX=-10.15 StartY=-12 StartZ=0 EndX=-10.15 EndY=-14 EndZ=0
    g11: LineSegment StartX=-12.8401 StartY=-16 StartZ=0 EndX=-10.1571 EndY=-16 EndZ=0
    g12: LineSegment StartX=-10.15 StartY=-14 StartZ=0 EndX=-8.70761 EndY=-14 EndZ=0
    g13: LineSegment StartX=-12.8401 StartY=-16 StartZ=0 EndX=-12.8401 EndY=-17.6958 EndZ=0
    g14: LineSegment StartX=-10.15 StartY=-12 StartZ=0 EndX=-7.79258 EndY=-12 EndZ=0
    g15: Circle CenterX=-6.2215 CenterY=-2 CenterZ=0 NormalX=0 NormalY=0 NormalZ=1 AngleXU=0 Radius=1
    g16: Circle CenterX=-6.22762 CenterY=-2.58724 CenterZ=0 NormalX=0 NormalY=0 NormalZ=1 AngleXU=0 Radius=1
    g17: Circle CenterX=-6.32538 CenterY=-4 CenterZ=0 NormalX=0 NormalY=0 NormalZ=1 AngleXU=0 Radius=1
    g18: BSplineCurve PolesCount=3 KnotsCount=2 Degree=2 IsPeriodic=0
    g19: GeomPoint X=-6.2215 Y=-2 Z=0
    g20: GeomPoint X=-6.32538 Y=-4 Z=0
    g21: Circle CenterX=-6.48644 CenterY=-5.99526 CenterZ=0 NormalX=0 NormalY=0 NormalZ=1 AngleXU=0 Radius=1
    g22: Circle CenterX=-6.58486 CenterY=-6.99526 CenterZ=0 NormalX=0 NormalY=0 NormalZ=1 AngleXU=0 Radius=1
    g23: Circle CenterX=-6.77343 CenterY=-8 CenterZ=0 NormalX=0 NormalY=0 NormalZ=1 AngleXU=0 Radius=1
    g24: BSplineCurve PolesCount=3 KnotsCount=2 Degree=2 IsPeriodic=0
    g25: GeomPoint X=-6.48644 Y=-5.99526 Z=0
    g26: GeomPoint X=-6.77343 Y=-8 Z=0
    g27: Circle CenterX=-7.19003 CenterY=-10 CenterZ=0 NormalX=0 NormalY=0 NormalZ=1 AngleXU=0 Radius=1
    g28: Circle CenterX=-7.44407 CenterY=-11.0915 CenterZ=0 NormalX=0 NormalY=0 NormalZ=1 AngleXU=0 Radius=1
    g29: Circle CenterX=-7.79258 CenterY=-12 CenterZ=0 NormalX=0 NormalY=0 NormalZ=1 AngleXU=0 Radius=1
    g30: BSplineCurve PolesCount=3 KnotsCount=2 Degree=2 IsPeriodic=0
    g31: GeomPoint X=-7.19003 Y=-10 Z=0
    g32: GeomPoint X=-7.79258 Y=-12 Z=0
    g33: Circle CenterX=-8.70761 CenterY=-14 CenterZ=0 NormalX=0 NormalY=0 NormalZ=1 AngleXU=0 Radius=1
    g34: Circle CenterX=-9.33087 CenterY=-15.1837 CenterZ=0 NormalX=0 NormalY=0 NormalZ=1 AngleXU=0 Radius=1
    g35: Circle CenterX=-10.1571 CenterY=-16 CenterZ=0 NormalX=0 NormalY=0 NormalZ=1 AngleXU=0 Radius=1
    g36: BSplineCurve PolesCount=3 KnotsCount=2 Degree=2 IsPeriodic=0
    g37: GeomPoint X=-8.70761 Y=-14 Z=0
    g38: GeomPoint X=-10.1571 Y=-16 Z=0
    g39: Circle CenterX=-12.8401 CenterY=-17.6958 CenterZ=0 NormalX=0 NormalY=0 NormalZ=1 AngleXU=0 Radius=1
    g40: Circle CenterX=-13.3521 CenterY=-17.9027 CenterZ=0 NormalX=0 NormalY=0 NormalZ=1 AngleXU=0 Radius=1
    g41: Circle CenterX=-14 CenterY=-18 CenterZ=0 NormalX=0 NormalY=0 NormalZ=1 AngleXU=0 Radius=1
    g42: BSplineCurve PolesCount=3 KnotsCount=2 Degree=2 IsPeriodic=0
    g43: GeomPoint X=-12.8401 Y=-17.6958 Z=0
    g44: GeomPoint X=-14 Y=-18 Z=0
    g45: LineSegment StartX=-6.2 StartY=0 StartZ=0 EndX=-7.2 EndY=0 EndZ=0
    g46: LineSegment StartX=-7.2 StartY=0 StartZ=0 EndX=-7.2 EndY=-2 EndZ=0
    g47: LineSegment StartX=-7.2 StartY=-2 StartZ=0 EndX=-6.2215 EndY=-2 EndZ=0
    g48: LineSegment StartX=-6.32538 StartY=-4 StartZ=0 EndX=-7.65538 EndY=-4 EndZ=0
    g49: LineSegment StartX=-7.65538 StartY=-4 StartZ=0 EndX=-7.65538 EndY=-5.99526 EndZ=0
    g50: LineSegment StartX=-7.65538 StartY=-5.99526 StartZ=0 EndX=-6.48644 EndY=-5.99526 EndZ=0
    g51: LineSegment StartX=-6.77343 StartY=-8 StartZ=0 EndX=-8.43343 EndY=-8 EndZ=0
    g52: LineSegment StartX=-8.43343 StartY=-8 StartZ=0 EndX=-8.43343 EndY=-10 EndZ=0
    g53: LineSegment StartX=-8.43343 StartY=-10 StartZ=0 EndX=-7.19003 EndY=-10 EndZ=0
  constraints (112):
    c: Horizontal(g0)
    c: Distance(g0) = 2
    c: Block(g0)
    c: Vertical(g1)
    c: Coincident(g2,g0)
    c: Vertical(g2)
    c: Block(g2)
    c: Coincident(g6,g2)
    c: Weight(g3) = 1
    c: Equal(g3,g4)
    c: Equal(g3,g5)
    c: InternalAlignment(g3,g6)
    c: InternalAlignment(g4,g6)
    c: InternalAlignment(g5,g6)
    c: InternalAlignment(g7,g6)
    c: InternalAlignment(g8,g6)
    c: Block(g6)
    c: Coincident(g9,g1)
    c: Coincident(g9,g6)
    c: Horizontal(g9)
    c: Vertical(g10)
    c: Block(g10)
    c: Horizontal(g11)
    c: Block(g11)
    c: Coincident(g12,g10)
    c: Horizontal(g12)
    c: Block(g12)
    c: Coincident(g13,g11)
    c: Vertical(g13)
    c: Block(g13)
    c: Coincident(g14,g10)
    c: Horizontal(g14)
    c: Block(g14)
    c: Block(g9)
    c: Block(g1)
    c: Weight(g15) = 1
    c: Equal(g15,g16)
    c: Equal(g15,g17)
    c: InternalAlignment(g15,g18)
    c: InternalAlignment(g16,g18)
    c: InternalAlignment(g17,g18)
    c: InternalAlignment(g19,g18)
    c: InternalAlignment(g20,g18)
    c: Weight(g21) = 1
    c: Equal(g21,g22)
    c: Equal(g21,g23)
    c: InternalAlignment(g21,g24)
    c: InternalAlignment(g22,g24)
    c: InternalAlignment(g23,g24)
    c: InternalAlignment(g25,g24)
    c: InternalAlignment(g26,g24)
    c: Weight(g27) = 1
    c: Equal(g27,g28)
    c: Equal(g27,g29)
    c: Coincident(g30,g14)
    c: InternalAlignment(g27,g30)
    c: InternalAlignment(g28,g30)
    c: InternalAlignment(g29,g30)
    c: InternalAlignment(g31,g30)
    c: InternalAlignment(g32,g30)
    c: Coincident(g36,g12)
    c: Weight(g33) = 1
    c: Equal(g33,g34)
    c: Equal(g33,g35)
    c: Coincident(g36,g11)
    c: InternalAlignment(g33,g36)
    c: InternalAlignment(g34,g36)
    c: InternalAlignment(g35,g36)
    c: InternalAlignment(g37,g36)
    c: InternalAlignment(g38,g36)
    c: Coincident(g42,g13)
    c: Weight(g39) = 1
    c: Equal(g39,g40)
    c: Equal(g39,g41)
    c: Coincident(g42,g1)
    c: InternalAlignment(g39,g42)
    c: InternalAlignment(g40,g42)
    c: InternalAlignment(g41,g42)
    c: InternalAlignment(g43,g42)
    c: InternalAlignment(g44,g42)
    c: Block(g18)
    c: Block(g24)
    c: Block(g30)
    c: Block(g36)
    c: Block(g42)
    c: Horizontal(g45)
    c: Coincident(g45,g0)
    c: Vertical(g46)
    c: Coincident(g46,g45)
    c: Coincident(g47,g46)
    c: Coincident(g47,g18)
    c: Horizontal(g47)
    c: Block(g46)
    c: Coincident(g48,g18)
    c: Horizontal(g48)
    c: Distance(g48) = 1.33
    c: Vertical(g49)
    c: Coincident(g49,g48)
    c: Coincident(g50,g49)
    c: Coincident(g50,g24)
    c: Horizontal(g50)
    c: Tangent(g50,g22)
    c: Horizontal(g51)
    c: Coincident(g51,g24)
    c: Block(g51)
    c: Vertical(g52)
    c: Block(g52)
    c: Coincident(g52,g51)
    c: Coincident(g53,g52)
    c: Coincident(g53,g30)
    c: Horizontal(g53)
    c: Distance(g1) = 8.5
FEATURE [Part::Feature] Face024
  shape: bbox 9.8 x 26.5 x 2e-07 mm, 1 faces, 0 solids (baked)
FEATURE [Part::Revolution] Revolve024
  Angle = 360
  Axis = (0,1,0)
  Base = (0,0,0)
  FaceMakerClass = Part::FaceMakerBullseye
  Placement = pos=(0,0,0) rot=(0,0,1;1.5708rad)
  Solid = false
  Source = -> Face024
  Symmetric = false
FEATURE [Part::Feature] Face025
  shape: bbox 9.8 x 26.5 x 2e-07 mm, 1 faces, 0 solids (baked)
FEATURE [Part::Revolution] Revolve025
  Angle = 360
  Axis = (0,1,0)
  Base = (0,0,0)
  FaceMakerClass = Part::FaceMakerBullseye
  Placement = pos=(0,0,0) rot=(0,0,1;1.5708rad)
  Solid = false
  Source = -> Face025
  Symmetric = false
FEATURE [Part::MultiFuse] Fusion033
  Placement = pos=(-18,19,36) rot=(0,0,1;0rad)
  Shapes = -> [Revolve025,Revolve024]
FEATURE [Part::Cylinder] Cylinder014
  Angle = 360
  AttacherType = Attacher::AttachEngine3D
  Height = 20
  Placement = pos=(0,0,36.15) rot=(0,0,1;0rad)
  Radius = 14.3
FEATURE [Part::Cylinder] Cylinder015
  Angle = 360
  AttacherType = Attacher::AttachEngine3D
  Height = 10
  Placement = pos=(0,0,36.15) rot=(0,0,1;0rad)
  Radius = 4
FEATURE [Part::MultiFuse] Fusion034  label="removeToCreteHoleForPlugHousing004"
  Placement = pos=(-42,19,36) rot=(0,1,0;1.5708rad)
  Shapes = -> [Cylinder014,Cylinder015]
FEATURE [Part::Cut] Cut008  label="top004"
  Base = -> Cut004
  Placement = pos=(-1,0,0) rot=(0,0,1;0rad)
  Tool = -> Fusion034
FEATURE [Part::Box] Box005  label="Cube005"
  AttacherType = Attacher::AttachEngine3D
  Height = 28
  Length = 3
  Placement = pos=(110.7,19,22) rot=(0,0,1;0rad)
  Width = 15.7
FEATURE [Part::Cylinder] Cylinder016
  Angle = 360
  AttacherType = Attacher::AttachEngine3D
  Height = 10
  Placement = pos=(0,0,36.15) rot=(0,0,1;0rad)
  Radius = 4
FEATURE [Part::Cylinder] Cylinder017
  Angle = 360
  AttacherType = Attacher::AttachEngine3D
  Height = 20
  Placement = pos=(0,0,36.15) rot=(0,0,1;0rad)
  Radius = 10.3
FEATURE [Part::MultiFuse] Fusion035  label="removeToCreteHoleForPlugHousing005"
  Placement = pos=(70,19,36) rot=(0,1,0;1.5708rad)
  Shapes = -> [Cylinder017,Cylinder016]
FEATURE [Part::Cut] Cut009  label="plugHousingTab001"
  Base = -> Box005
  Placement = pos=(-107.4,-14,0) rot=(0,0,1;0rad)
  Tool = -> Fusion035
FEATURE [Part::Box] Box006  label="Cube006"
  AttacherType = Attacher::AttachEngine3D
  Height = 28
  Length = 3
  Placement = pos=(110.7,19,22) rot=(0,0,1;0rad)
  Width = 15.7
FEATURE [Part::Cylinder] Cylinder018
  Angle = 360
  AttacherType = Attacher::AttachEngine3D
  Height = 10
  Placement = pos=(0,0,36.15) rot=(0,0,1;0rad)
  Radius = 4
FEATURE [Part::Cylinder] Cylinder019
  Angle = 360
  AttacherType = Attacher::AttachEngine3D
  Height = 20
  Placement = pos=(0,0,36.15) rot=(0,0,1;0rad)
  Radius = 10.3
FEATURE [Part::MultiFuse] Fusion036  label="removeToCreteHoleForPlugHousing006"
  Placement = pos=(70,19,36) rot=(0,1,0;1.5708rad)
  Shapes = -> [Cylinder019,Cylinder018]
FEATURE [Part::Cut] Cut010  label="plugHousingTab002"
  Base = -> Box006
  Placement = pos=(-107.4,-14,0) rot=(0,0,1;0rad)
  Tool = -> Fusion036
FEATURE [Part::MultiFuse] Fusion037
  Placement = pos=(9.6,23,0) rot=(0,0,1;3.14159rad)
  Shapes = -> [Cut009,Cut010]
FEATURE [Part::Box] Box  label="Cube"
  AttacherType = Attacher::AttachEngine3D
  Height = 10
  Length = 3
  Placement = pos=(3.3,4,12) rot=(0,0,1;0rad)
  Width = 10
FEATURE [Part::Fillet] Fillet004
  Base = -> Fusion028
  Edges = 1 edges r=2: [Edge25]
FEATURE [Part::Fillet] Fillet005  label="plugHousing046"
  Base = -> Fillet004
  Edges = 1 edges r=2: [Edge8]
FEATURE [Part::Fillet] Fillet006
  Base = -> Box
  Edges = 1 edges r=2: [Edge11]
FEATURE [Part::Box] Box007  label="Cube007"
  AttacherType = Attacher::AttachEngine3D
  Height = 10
  Length = 3
  Placement = pos=(3.3,4,50) rot=(0,0,1;0rad)
  Width = 10
FEATURE [Part::Fillet] Fillet007
  Base = -> Box007
  Edges = 1 edges r=2: [Edge12]
FEATURE [Part::Box] Box008  label="Cube008"
  AttacherType = Attacher::AttachEngine3D
  Height = 28
  Length = 4
  Placement = pos=(5,0,22) rot=(0,0,1;0rad)
  Width = 10
FEATURE [Part::Fillet] Fillet008
  Base = -> Box008
  Edges = 1 edges r=1: [Edge7]
FEATURE [Part::Fillet] Fillet009
  Base = -> Fillet008
  Edges = 1 edges r=2: [Edge5]
FEATURE [Part::Fillet] Fillet010
  Base = -> Fillet009
  Edges = 1 edges r=2: [Edge2]
FEATURE [Sketcher::SketchObject] Sketch009  label="topSketch003"
  FullyConstrained = true
  sketch-geometry (4):
    g0: LineSegment StartX=16.8446 StartY=31.512 StartZ=0 EndX=16.3251 EndY=34.4666 EndZ=0
    g1: ArcOfCircle CenterX=19 CenterY=19.2524 CenterZ=0 NormalX=0 NormalY=0 NormalZ=1 AngleXU=0 Radius=15.4476 StartAngle=1.74483 EndAngle=2.72717
    g2: ArcOfCircle CenterX=19 CenterY=19.2524 CenterZ=0 NormalX=0 NormalY=0 NormalZ=1 AngleXU=0 Radius=12.4476 StartAngle=1.74483 EndAngle=2.73189
    g3: LineSegment StartX=4.86004 StartY=25.4725 StartZ=0 EndX=7.58253 EndY=24.2107 EndZ=0
  constraints (7):
    c: Block(g0)
    c: Coincident(g1,g0)
    c: Coincident(g2,g0)
    c: Coincident(g3,g1)
    c: Coincident(g3,g2)
    c: Block(g1)
    c: Block(g2)
FEATURE [Part::Extrusion] Extrude008
  Base = -> Sketch009
  Dir = (0,0,1)
  DirMode = 2
  FaceMakerClass = Part::FaceMakerBullseye
  LengthFwd = 10
  LengthRev = 0
  Placement = pos=(0,0,31) rot=(0,0,1;0rad)
  Solid = true
  Symmetric = false
FEATURE [Part::Cylinder] Cylinder020
  Angle = 360
  AttacherType = Attacher::AttachEngine3D
  Height = 20
  Placement = pos=(0,0,36.15) rot=(0,0,1;0rad)
  Radius = 8.2
FEATURE [Part::Cylinder] Cylinder021
  Angle = 360
  AttacherType = Attacher::AttachEngine3D
  Height = 10
  Placement = pos=(0,0,36.15) rot=(0,0,1;0rad)
  Radius = 4
FEATURE [Part::MultiFuse] Fusion038  label="removeToCreteHoleForPlugHousing007"
  Placement = pos=(-42,19,36) rot=(0,1,0;1.5708rad)
  Shapes = -> [Cylinder020,Cylinder021]
FEATURE [Part::Cut] Cut011
  Base = -> Extrude008
  Tool = -> Fusion038
FEATURE [Part::Fillet] Fillet011
  Base = -> Cut011
  Edges = 1 edges r=2: [Edge1]
FEATURE [Part::Fillet] Fillet012
  Base = -> Fillet011
  Edges = 1 edges r=2.5: [Edge1]
FEATURE [Part::Fillet] Fillet013
  Base = -> Fillet012
  Edges = 1 edges r=2.5: [Edge2]
FEATURE [Part::Box] Box010  label="Cube010"
  AttacherType = Attacher::AttachEngine3D
  Height = 16
  Length = 8
  Placement = pos=(12.7,31.52,28) rot=(0,0,1;0rad)
  Width = 4
FEATURE [Sketcher::SketchObject] Sketch010  label="topSketch004"
  FullyConstrained = true
  sketch-geometry (4):
    g0: LineSegment StartX=16.8446 StartY=31.512 StartZ=0 EndX=16.3251 EndY=34.4666 EndZ=0
    g1: ArcOfCircle CenterX=19 CenterY=19.2524 CenterZ=0 NormalX=0 NormalY=0 NormalZ=1 AngleXU=0 Radius=15.4476 StartAngle=1.74483 EndAngle=2.72717
    g2: ArcOfCircle CenterX=19 CenterY=19.2524 CenterZ=0 NormalX=0 NormalY=0 NormalZ=1 AngleXU=0 Radius=12.4476 StartAngle=1.74483 EndAngle=2.73189
    g3: LineSegment StartX=4.86004 StartY=25.4725 StartZ=0 EndX=7.58253 EndY=24.2107 EndZ=0
  constraints (7):
    c: Block(g0)
    c: Coincident(g1,g0)
    c: Coincident(g2,g0)
    c: Coincident(g3,g1)
    c: Coincident(g3,g2)
    c: Block(g1)
    c: Block(g2)
FEATURE [Part::Cylinder] Cylinder022
  Angle = 360
  AttacherType = Attacher::AttachEngine3D
  Height = 10
  Placement = pos=(0,0,36.15) rot=(0,0,1;0rad)
  Radius = 4
FEATURE [Sketcher::SketchObject] Sketch011  label="topSketch005"
  FullyConstrained = true
  sketch-geometry (4):
    g0: LineSegment StartX=16.8446 StartY=31.512 StartZ=0 EndX=16.3251 EndY=34.4666 EndZ=0
    g1: ArcOfCircle CenterX=19 CenterY=19.2524 CenterZ=0 NormalX=0 NormalY=0 NormalZ=1 AngleXU=0 Radius=15.4476 StartAngle=1.74483 EndAngle=2.72717
    g2: ArcOfCircle CenterX=19 CenterY=19.2524 CenterZ=0 NormalX=0 NormalY=0 NormalZ=1 AngleXU=0 Radius=12.4476 StartAngle=1.74483 EndAngle=2.73189
    g3: LineSegment StartX=4.86004 StartY=25.4725 StartZ=0 EndX=7.58253 EndY=24.2107 EndZ=0
  constraints (7):
    c: Block(g0)
    c: Coincident(g1,g0)
    c: Coincident(g2,g0)
    c: Coincident(g3,g1)
    c: Coincident(g3,g2)
    c: Block(g1)
    c: Block(g2)
FEATURE [Part::Extrusion] Extrude010
  Base = -> Sketch011
  Dir = (0,0,1)
  DirMode = 2
  FaceMakerClass = Part::FaceMakerBullseye
  LengthFwd = 10.6
  LengthRev = 0
  Placement = pos=(0,0,31) rot=(0,0,1;0rad)
  Solid = true
  Symmetric = false
FEATURE [Part::Cylinder] Cylinder023
  Angle = 360
  AttacherType = Attacher::AttachEngine3D
  Height = 20
  Placement = pos=(0,0,36.15) rot=(0,0,1;0rad)
  Radius = 8.2
FEATURE [Part::MultiFuse] Fusion039  label="removeToCreteHoleForPlugHousing008"
  Placement = pos=(-42,19,36) rot=(0,1,0;1.5708rad)
  Shapes = -> [Cylinder023,Cylinder022]
FEATURE [Part::Cut] Cut012
  Base = -> Extrude010
  Placement = pos=(0,0,-0.3) rot=(0,0,1;0rad)
  Tool = -> Fusion039
FEATURE [Part::Cut] Cut013
  Base = -> Box010
  Tool = -> Cut012
FEATURE [Part::Fillet] Fillet014
  Base = -> Cut013
  Edges = 1 edges r=0.7: [Edge13]
FEATURE [Part::Fillet] Fillet015
  Base = -> Fillet014
  Edges = 1 edges r=0.7: [Edge13]
FEATURE [Part::Fillet] Fillet016
  Base = -> Fillet015
  Edges = 1 edges r=0.7: [Edge16]
FEATURE [Part::Fillet] Fillet017
  Base = -> Fillet016
  Edges = 1 edges r=0.7: [Edge11]
FEATURE [Part::Fillet] Fillet018
  Base = -> Fillet017
  Edges = 1 edges r=0.7: [Edge10]
FEATURE [Part::Fillet] Fillet019
  Base = -> Fillet018
  Edges = 1 edges r=1.2: [Edge5]
FEATURE [Part::Fillet] Fillet020
  Base = -> Fillet019
  Edges = 1 edges r=1.2: [Edge12]
FEATURE [Part::Fillet] Fillet021
  Base = -> Fillet020
  Edges = 1 edges r=2: [Edge1]
  Placement = pos=(0.3,0,0) rot=(0,0,1;0rad)
FEATURE [Part::MultiFuse] Fusion040  label="top005"
  Shapes = -> [Cut008,Fillet021]
FEATURE [Part::MultiFuse] Fusion041  label="wireHolder"
  Shapes = -> [Fusion033,Fillet013]
FEATURE [Part::MultiFuse] Fusion042
  Shapes = -> [Fillet007,Fusion041]
FEATURE [Part::MultiFuse] Fusion043  label="wireHolder001"
  Shapes = -> [Fusion042,Fillet010]
FEATURE [Part::MultiFuse] Fusion044  label="wireHolder002"
  Shapes = -> [Fillet006,Fusion037,Fusion043]
FEATURE [Part::Feature] Face026
  shape: bbox 11 x 6 x 2e-07 mm, 1 faces, 0 solids (baked)
FEATURE [Part::Revolution] Revolve026
  Angle = 360
  Axis = (0,1,0)
  Base = (0,0,0)
  FaceMakerClass = Part::FaceMakerBullseye
  Placement = pos=(30.3,-1,19.7) rot=(0,0,1;0rad)
  Solid = false
  Source = -> Face026
  Symmetric = false
FEATURE [Sketcher::SketchObject] Sketch013  label="topSketch006"
  FullyConstrained = true
  sketch-geometry (13):
    g0: LineSegment StartX=117 StartY=19 StartZ=0 EndX=117 EndY=38 EndZ=0
    g1: ArcOfCircle CenterX=98 CenterY=19 CenterZ=0 NormalX=0 NormalY=0 NormalZ=1 AngleXU=0 Radius=19 StartAngle=5.7297 EndAngle=6.28319
    g2: LineSegment StartX=0 StartY=3 StartZ=0 EndX=0 EndY=19 EndZ=0
    g3: LineSegment StartX=19 StartY=38 StartZ=0 EndX=117 EndY=38 EndZ=0
    g4: ArcOfCircle CenterX=19 CenterY=19 CenterZ=0 NormalX=0 NormalY=0 NormalZ=1 AngleXU=0 Radius=19 StartAngle=1.5708 EndAngle=3.14159
    g5: ArcOfCircle CenterX=19 CenterY=19 CenterZ=0 NormalX=0 NormalY=0 NormalZ=1 AngleXU=0 Radius=16 StartAngle=1.5708 EndAngle=3.14159
    g6: ArcOfCircle CenterX=98 CenterY=19 CenterZ=0 NormalX=0 NormalY=0 NormalZ=1 AngleXU=0 Radius=16 StartAngle=5.60905 EndAngle=6.28319
    g7: LineSegment StartX=114 StartY=19 StartZ=0 EndX=114 EndY=35 EndZ=0
    g8: LineSegment StartX=110.5 StartY=9.01251 StartZ=0 EndX=114.163 EndY=9.01251 EndZ=0
    g9: LineSegment StartX=114 StartY=35 StartZ=0 EndX=19 EndY=35 EndZ=0
    g10: LineSegment StartX=0 StartY=3 StartZ=0 EndX=0 EndY=0 EndZ=0
    g11: LineSegment StartX=3 StartY=0 StartZ=0 EndX=0 EndY=0 EndZ=0
    g12: LineSegment StartX=3 StartY=19 StartZ=0 EndX=3 EndY=0 EndZ=0
  constraints (33):
    c: Vertical(g0)
    c: Distance(g0) = 19
    c: Block(g0)
    c: Coincident(g1,g0)
    c: Block(g1)
    c: Vertical(g2)
    c: Block(g2)
    c: Coincident(g3,g0)
    c: Horizontal(g3)
    c: Distance(g3) = 98
    c: Coincident(g4,g3)
    c: Coincident(g4,g2)
    c: Block(g4)
    c: Coincident(g5,g4)
    c: Coincident(g6,g1)
    c: Block(g6)
    c: Block(g5)
    c: Coincident(g7,g6)
    c: Vertical(g7)
    c: Coincident(g8,g6)
    c: Coincident(g8,g1)
    c: Coincident(g9,g7)
    c: Coincident(g9,g5)
    c: Horizontal(g9)
    c: Tangent(g9,g5)
    c: Coincident(g10,g2)
    c: Distance(g10) = 3
    c: Vertical(g10)
    c: Coincident(g11,g10)
    c: Horizontal(g11)
    c: Coincident(g12,g5)
    c: Coincident(g12,g11)
    c: Vertical(g12)
FEATURE [Part::Extrusion] Extrude011  label="top006"
  Base = -> Sketch013
  Dir = (0,0,1)
  DirMode = 2
  FaceMakerClass = Part::FaceMakerBullseye
  LengthFwd = 72
  LengthRev = 0
  Solid = true
  Symmetric = false
FEATURE [Sketcher::SketchObject] Sketch014
  FullyConstrained = true
  MapMode = 3
  Placement = pos=(0,0,0) rot=(1,0,0;1.5708rad)
  Support = -> [Extrude011]
  sketch-geometry (8):
    g0: Circle CenterX=80.351 CenterY=-67.6202 CenterZ=0 NormalX=0 NormalY=0 NormalZ=1 AngleXU=0 Radius=2
    g1: Circle CenterX=80.351 CenterY=-67.6202 CenterZ=0 NormalX=0 NormalY=0 NormalZ=1 AngleXU=0 Radius=3
    g2: Circle CenterX=80.351 CenterY=-4.92017 CenterZ=0 NormalX=0 NormalY=0 NormalZ=1 AngleXU=0 Radius=2
    g3: Circle CenterX=80.351 CenterY=-4.92017 CenterZ=0 NormalX=0 NormalY=0 NormalZ=1 AngleXU=0 Radius=3
    g4: Circle CenterX=23.851 CenterY=-4.92017 CenterZ=0 NormalX=0 NormalY=0 NormalZ=1 AngleXU=0 Radius=2
    g5: Circle CenterX=23.851 CenterY=-4.92017 CenterZ=0 NormalX=0 NormalY=0 NormalZ=1 AngleXU=0 Radius=3
    g6: Circle CenterX=23.851 CenterY=-67.6202 CenterZ=0 NormalX=0 NormalY=0 NormalZ=1 AngleXU=0 Radius=2
    g7: Circle CenterX=23.851 CenterY=-67.6202 CenterZ=0 NormalX=0 NormalY=0 NormalZ=1 AngleXU=0 Radius=3
  constraints (8):
    c: Block(g3)
    c: Block(g2)
    c: Block(g1)
    c: Block(g0)
    c: Block(g6)
    c: Block(g7)
    c: Block(g4)
    c: Block(g5)
FEATURE [Part::Feature] Face027
  shape: bbox 11 x 6 x 2e-07 mm, 1 faces, 0 solids (baked)
FEATURE [Part::Revolution] Revolve027
  Angle = 360
  Axis = (0,1,0)
  Base = (0,0,0)
  FaceMakerClass = Part::FaceMakerBullseye
  Placement = pos=(30.3,-1,51.7) rot=(0,0,1;0rad)
  Solid = false
  Source = -> Face027
  Symmetric = false
FEATURE [Part::Feature] Face028
  shape: bbox 11 x 6 x 2e-07 mm, 1 faces, 0 solids (baked)
FEATURE [Part::Revolution] Revolve028
  Angle = 360
  Axis = (0,1,0)
  Base = (0,0,0)
  FaceMakerClass = Part::FaceMakerBullseye
  Placement = pos=(62.3,-1,19.7) rot=(0,0,1;0rad)
  Solid = false
  Source = -> Face028
  Symmetric = false
FEATURE [Part::Feature] Face029
  shape: bbox 11 x 6 x 2e-07 mm, 1 faces, 0 solids (baked)
FEATURE [Part::Revolution] Revolve029
  Angle = 360
  Axis = (0,1,0)
  Base = (0,0,0)
  FaceMakerClass = Part::FaceMakerBullseye
  Placement = pos=(62.3,-1,51.7) rot=(0,0,1;0rad)
  Solid = false
  Source = -> Face029
  Symmetric = false
FEATURE [Part::Feature] Wire
  shape: bbox 11 x 5.2 x 2e-07 mm, 0 faces, 0 solids (baked)
FEATURE [Part::Revolution] Revolve030
  Angle = 360
  Axis = (0,1,0)
  Base = (0,0,0)
  FaceMakerClass = Part::FaceMakerBullseye
  Placement = pos=(30.3,38,19.7) rot=(0,0,1;0rad)
  Solid = true
  Source = -> Wire
  Symmetric = false
FEATURE [Part::Feature] Wire001
  shape: bbox 11 x 5.2 x 2e-07 mm, 0 faces, 0 solids (baked)
FEATURE [Part::Revolution] Revolve031
  Angle = 360
  Axis = (0,1,0)
  Base = (0,0,0)
  FaceMakerClass = Part::FaceMakerBullseye
  Placement = pos=(30.3,38,51.7) rot=(0,0,1;0rad)
  Solid = true
  Source = -> Wire001
  Symmetric = false
FEATURE [Part::Feature] Wire002
  shape: bbox 11 x 5.2 x 2e-07 mm, 0 faces, 0 solids (baked)
FEATURE [Part::Revolution] Revolve032
  Angle = 360
  Axis = (0,1,0)
  Base = (0,0,0)
  FaceMakerClass = Part::FaceMakerBullseye
  Placement = pos=(62.3,38,51.7) rot=(0,0,1;0rad)
  Solid = true
  Source = -> Wire002
  Symmetric = false
FEATURE [Part::Feature] Wire003
  shape: bbox 11 x 5.2 x 2e-07 mm, 0 faces, 0 solids (baked)
FEATURE [Part::Revolution] Revolve033
  Angle = 360
  Axis = (0,1,0)
  Base = (0,0,0)
  FaceMakerClass = Part::FaceMakerBullseye
  Placement = pos=(62.3,38,19.7) rot=(0,0,1;0rad)
  Solid = true
  Source = -> Wire003
  Symmetric = false
FEATURE [Part::MultiFuse] Fusion045  label="altRandScrewHousing"
  Shapes = -> [Revolve029,Revolve027,Revolve028,Revolve026]
FEATURE [Part::MultiFuse] Fusion046  label="fanScrewHousing"
  Shapes = -> [Revolve033,Revolve032,Revolve031,Revolve030]
FEATURE [Sketcher::SketchObject] Sketch015
  FullyConstrained = true
  sketch-geometry (17):
    g0: Circle CenterX=-3.5 CenterY=23.5 CenterZ=0 NormalX=0 NormalY=0 NormalZ=1 AngleXU=0 Radius=1
    g1: Circle CenterX=-1 CenterY=15.25 CenterZ=0 NormalX=0 NormalY=0 NormalZ=1 AngleXU=0 Radius=1
    g2: Circle CenterX=-3.5 CenterY=7 CenterZ=0 NormalX=0 NormalY=0 NormalZ=1 AngleXU=0 Radius=1
    g3: BSplineCurve PolesCount=3 KnotsCount=2 Degree=2 IsPeriodic=0
    g4: GeomPoint X=-3.5 Y=23.5 Z=0
    g5: GeomPoint X=-3.5 Y=7 Z=0
    g6: Circle CenterX=-4.8 CenterY=30.5 CenterZ=0 NormalX=0 NormalY=0 NormalZ=1 AngleXU=0 Radius=1
    g7: Circle CenterX=-3.5 CenterY=30.5 CenterZ=0 NormalX=0 NormalY=0 NormalZ=1 AngleXU=0 Radius=1
    g8: Circle CenterX=-3.5 CenterY=29.2 CenterZ=0 NormalX=0 NormalY=0 NormalZ=1 AngleXU=0 Radius=1
    g9: BSplineCurve PolesCount=3 KnotsCount=2 Degree=2 IsPeriodic=0
    g10: GeomPoint X=-4.8 Y=30.5 Z=0
    g11: GeomPoint X=-3.5 Y=29.2 Z=0
    g12: LineSegment StartX=-3.5 StartY=29.2 StartZ=0 EndX=-3.5 EndY=23.5 EndZ=0
    g13: LineSegment StartX=-4.8 StartY=30.5 StartZ=0 EndX=0 EndY=30.5 EndZ=0
    g14: LineSegment StartX=-3.5 StartY=0.3 StartZ=0 EndX=0 EndY=0.3 EndZ=0
    g15: LineSegment StartX=-3.5 StartY=0.3 StartZ=0 EndX=-3.5 EndY=7 EndZ=0
    g16: LineSegment StartX=0 StartY=0.3 StartZ=0 EndX=0 EndY=30.5 EndZ=0
  constraints (33):
    c: Weight(g0) = 1
    c: Equal(g0,g1)
    c: Equal(g0,g2)
    c: InternalAlignment(g0,g3)
    c: InternalAlignment(g1,g3)
    c: InternalAlignment(g2,g3)
    c: InternalAlignment(g4,g3)
    c: InternalAlignment(g5,g3)
    c: Block(g3)
    c: Weight(g6) = 1
    c: Equal(g6,g7)
    c: Equal(g6,g8)
    c: InternalAlignment(g6,g9)
    c: InternalAlignment(g7,g9)
    c: InternalAlignment(g8,g9)
    c: InternalAlignment(g10,g9)
    c: InternalAlignment(g11,g9)
    c: Block(g9)
    c: Coincident(g12,g9)
    c: Coincident(g12,g3)
    c: Vertical(g12)
    c: Coincident(g13,g9)
    c: Horizontal(g13)
    c: Distance(g13) = 4.8
    c: Horizontal(g14)
    c: Block(g14)
    c: Coincident(g15,g14)
    c: Coincident(g15,g3)
    c: Vertical(g15)
    c: Coincident(g16,g14)
    c: Coincident(g16,g13)
    c: Vertical(g16)
    c: Tangent(g16,g1)
FEATURE [Sketcher::SketchObject] Sketch016
  FullyConstrained = true
  sketch-geometry (16):
    g0: Circle CenterX=-3.5 CenterY=23.5 CenterZ=0 NormalX=0 NormalY=0 NormalZ=1 AngleXU=0 Radius=1
    g1: Circle CenterX=-1 CenterY=15.25 CenterZ=0 NormalX=0 NormalY=0 NormalZ=1 AngleXU=0 Radius=1
    g2: Circle CenterX=-3.5 CenterY=7 CenterZ=0 NormalX=0 NormalY=0 NormalZ=1 AngleXU=0 Radius=1
    g3: BSplineCurve PolesCount=3 KnotsCount=2 Degree=2 IsPeriodic=0
    g4: GeomPoint X=-3.5 Y=23.5 Z=0
    g5: GeomPoint X=-3.5 Y=7 Z=0
    g6: LineSegment StartX=-3.5 StartY=28.2 StartZ=0 EndX=-3.5 EndY=23.5 EndZ=0
    g7: LineSegment StartX=0 StartY=29.5 StartZ=0 EndX=0 EndY=30 EndZ=0
    g8: LineSegment StartX=-3.5 StartY=28.2 StartZ=0 EndX=-3.5 EndY=30 EndZ=0
    g9: LineSegment StartX=0 StartY=30 StartZ=0 EndX=0 EndY=30.5 EndZ=0
    g10: LineSegment StartX=0 StartY=30.5 StartZ=0 EndX=-3.5 EndY=30.5 EndZ=0
    g11: LineSegment StartX=-3.5 StartY=30.5 StartZ=0 EndX=-3.5 EndY=30 EndZ=0
    g12: LineSegment StartX=0 StartY=29.5 StartZ=0 EndX=0 EndY=5 EndZ=0
    g13: LineSegment StartX=-3.5 StartY=0.3 StartZ=0 EndX=-3.5 EndY=7 EndZ=0
    g14: LineSegment StartX=-3.5 StartY=0.3 StartZ=0 EndX=0 EndY=0.3 EndZ=0
    g15: LineSegment StartX=0 StartY=5 StartZ=0 EndX=0 EndY=0.3 EndZ=0
  constraints (39):
    c: Weight(g0) = 1
    c: Equal(g0,g1)
    c: Equal(g0,g2)
    c: InternalAlignment(g0,g3)
    c: InternalAlignment(g1,g3)
    c: InternalAlignment(g2,g3)
    c: InternalAlignment(g4,g3)
    c: InternalAlignment(g5,g3)
    c: Block(g3)
    c: Coincident(g6,g3)
    c: Vertical(g6)
    c: Vertical(g7)
    c: Distance(g7) = 0.5
    c: Coincident(g8,g6)
    c: Vertical(g8)
    c: Block(g6)
    c: Block(g7)
    c: Vertical(g9)
    c: Equal(g7,g9) = 0.5
    c: Block(g9)
    c: Coincident(g9,g7)
    c: Horizontal(g10)
    c: Coincident(g10,g9)
    c: Coincident(g11,g10)
    c: Coincident(g11,g8)
    c: Vertical(g11)
    c: Block(g11)
    c: Coincident(g12,g7)
    c: Vertical(g12)
    c: Coincident(g13,g3)
    c: Vertical(g13)
    c: Distance(g13) = 6.7
    c: Coincident(g14,g13)
    c: Horizontal(g14)
    c: Block(g14)
    c: Coincident(g15,g12)
    c: Coincident(g15,g14)
    c: Vertical(g15)
    c: Block(g15)
FEATURE [Sketcher::SketchObject] Sketch017
  FullyConstrained = true
  sketch-geometry (11):
    g0: LineSegment StartX=-3.5 StartY=1e-16 StartZ=0 EndX=-1.6 EndY=1e-16 EndZ=0
    g1: LineSegment StartX=-1.6 StartY=1e-16 StartZ=0 EndX=-1.6 EndY=1.5 EndZ=0
    g2: LineSegment StartX=-3.5 StartY=1.5 StartZ=0 EndX=-1.6 EndY=1.5 EndZ=0
    g3: LineSegment StartX=-3.5 StartY=1e-16 StartZ=0 EndX=-4.8 EndY=1e-16 EndZ=0
    g4: Circle CenterX=-3.5 CenterY=1.3 CenterZ=0 NormalX=0 NormalY=0 NormalZ=1 AngleXU=0 Radius=1
    g5: Circle CenterX=-3.5 CenterY=1e-16 CenterZ=0 NormalX=0 NormalY=0 NormalZ=1 AngleXU=0 Radius=1
    g6: Circle CenterX=-4.8 CenterY=1e-16 CenterZ=0 NormalX=0 NormalY=0 NormalZ=1 AngleXU=0 Radius=1
    g7: BSplineCurve PolesCount=3 KnotsCount=2 Degree=2 IsPeriodic=0
    g8: GeomPoint X=-3.5 Y=1.3 Z=0
    g9: GeomPoint X=-4.8 Y=1e-16 Z=0
    g10: LineSegment StartX=-3.5 StartY=1.3 StartZ=0 EndX=-3.5 EndY=1.5 EndZ=0
  constraints (24):
    c: Horizontal(g0)
    c: Distance(g0) = 1.9
    c: Block(g0)
    c: Coincident(g1,g0)
    c: Vertical(g1)
    c: Coincident(g2,g1)
    c: Horizontal(g2)
    c: Coincident(g3,g0)
    c: Horizontal(g3)
    c: Distance(g3) = 1.3
    c: Weight(g4) = 1
    c: Equal(g4,g5)
    c: Coincident(g5,g0)
    c: Equal(g4,g6)
    c: Coincident(g7,g3)
    c: InternalAlignment(g4,g7)
    c: InternalAlignment(g5,g7)
    c: InternalAlignment(g6,g7)
    c: InternalAlignment(g8,g7)
    c: InternalAlignment(g9,g7)
    c: Coincident(g10,g7)
    c: Coincident(g10,g2)
    c: Vertical(g10)
    c: Block(g10)
FEATURE [Part::Feature] Face035
  shape: bbox 3.2 x 1.5 x 2e-07 mm, 1 faces, 0 solids (baked)
FEATURE [Part::Revolution] Revolve039  label="backCaseScrewRetainer"
  Angle = 360
  Axis = (0,1,0)
  Base = (0,0,0)
  FaceMakerClass = Part::FaceMakerBullseye
  Placement = pos=(12.5,3,62) rot=(0,0,1;0rad)
  Solid = false
  Source = -> Face035
  Symmetric = false
FEATURE [Part::Feature] Face036
  shape: bbox 3.2 x 1.5 x 2e-07 mm, 1 faces, 0 solids (baked)
FEATURE [Part::Feature] Face039
  shape: bbox 4.8 x 30.2 x 2e-07 mm, 1 faces, 0 solids (baked)
FEATURE [Part::Revolution] Revolve043  label="frontCaseScrewPost002"
  Angle = 360
  Axis = (0,1,0)
  Base = (0,0,0)
  FaceMakerClass = Part::FaceMakerBullseye
  Placement = pos=(89.5,4.5,3.5) rot=(0,0,1;0rad)
  Solid = false
  Source = -> Face039
  Symmetric = false
FEATURE [Part::Feature] Face042
  shape: bbox 4.8 x 30.2 x 2e-07 mm, 1 faces, 0 solids (baked)
FEATURE [Part::Revolution] Revolve046  label="frontCaseScrewPost003"
  Angle = 360
  Axis = (0,1,0)
  Base = (0,0,0)
  FaceMakerClass = Part::FaceMakerBullseye
  Placement = pos=(89.5,4.5,68.5) rot=(0,0,1;0rad)
  Solid = false
  Source = -> Face042
  Symmetric = false
FEATURE [Part::Feature] Face043
  shape: bbox 3.2 x 1.5 x 2e-07 mm, 1 faces, 0 solids (baked)
FEATURE [Part::Revolution] Revolve047  label="frontCaseScrewRetainer002"
  Angle = 360
  Axis = (0,1,0)
  Base = (0,0,0)
  FaceMakerClass = Part::FaceMakerBullseye
  Placement = pos=(89.5,3,68.5) rot=(0,0,1;0rad)
  Solid = false
  Source = -> Face043
  Symmetric = false
FEATURE [Part::Feature] Face044
  shape: bbox 3.2 x 1.5 x 2e-07 mm, 1 faces, 0 solids (baked)
FEATURE [Part::Revolution] Revolve048  label="frontCaseScrewRetainer003"
  Angle = 360
  Axis = (0,1,0)
  Base = (0,0,0)
  FaceMakerClass = Part::FaceMakerBullseye
  Placement = pos=(89.5,3,3.5) rot=(0,0,1;0rad)
  Solid = false
  Source = -> Face044
  Symmetric = false
FEATURE [App::MeasureDistance] Distance002  label="Distance: 1.67 mm"
  Distance = 1.66921
  P1 = (99.2361,4.7524,71.7)
  P2 = (99.2347,6.42161,71.7)
FEATURE [Sketcher::SketchObject] Sketch018
  FullyConstrained = true
  sketch-geometry (7):
    g0: LineSegment StartX=0 StartY=0 StartZ=0 EndX=0 EndY=6 EndZ=0
    g1: Circle CenterX=0 CenterY=0 CenterZ=0 NormalX=0 NormalY=0 NormalZ=1 AngleXU=0 Radius=1
    g2: Circle CenterX=8 CenterY=6 CenterZ=0 NormalX=0 NormalY=0 NormalZ=1 AngleXU=0 Radius=1
    g3: BSplineCurve PolesCount=3 KnotsCount=2 Degree=2 IsPeriodic=0
    g4: GeomPoint X=0 Y=0 Z=0
    g5: GeomPoint X=8 Y=6 Z=0
    g6: LineSegment StartX=0 StartY=6 StartZ=0 EndX=8 EndY=6 EndZ=0
  constraints (14):
    c: Coincident(g0,g-1)
    c: Distance(g0) = 6
    c: Vertical(g0)
    c: Coincident(g3,g0)
    c: Weight(g1) = 1
    c: Equal(g1,g2)
    c: InternalAlignment(g1,g3)
    c: InternalAlignment(g2,g3)
    c: InternalAlignment(g4,g3)
    c: InternalAlignment(g5,g3)
    c: Block(g3)
    c: Coincident(g6,g0)
    c: Coincident(g6,g3)
    c: Horizontal(g6)
FEATURE [Part::Extrusion] Extrude012  label="caseScrewPillarBracket"
  Base = -> Sketch018
  Dir = (0,0,1)
  DirMode = 2
  FaceMakerClass = Part::FaceMakerBullseye
  LengthFwd = 2.4
  LengthRev = 0
  Placement = pos=(15.76,29,8.8) rot=(0,1,0;0rad)
  Solid = true
  Symmetric = false
FEATURE [Sketcher::SketchObject] Sketch019
  FullyConstrained = true
  sketch-geometry (7):
    g0: LineSegment StartX=0 StartY=0 StartZ=0 EndX=0 EndY=6 EndZ=0
    g1: Circle CenterX=0 CenterY=0 CenterZ=0 NormalX=0 NormalY=0 NormalZ=1 AngleXU=0 Radius=1
    g2: Circle CenterX=8 CenterY=6 CenterZ=0 NormalX=0 NormalY=0 NormalZ=1 AngleXU=0 Radius=1
    g3: BSplineCurve PolesCount=3 KnotsCount=2 Degree=2 IsPeriodic=0
    g4: GeomPoint X=0 Y=0 Z=0
    g5: GeomPoint X=8 Y=6 Z=0
    g6: LineSegment StartX=0 StartY=6 StartZ=0 EndX=8 EndY=6 EndZ=0
  constraints (14):
    c: Coincident(g0,g-1)
    c: Distance(g0) = 6
    c: Vertical(g0)
    c: Coincident(g3,g0)
    c: Weight(g1) = 1
    c: Equal(g1,g2)
    c: InternalAlignment(g1,g3)
    c: InternalAlignment(g2,g3)
    c: InternalAlignment(g4,g3)
    c: InternalAlignment(g5,g3)
    c: Block(g3)
    c: Coincident(g6,g0)
    c: Coincident(g6,g3)
    c: Horizontal(g6)
FEATURE [Part::Extrusion] Extrude013  label="caseScrewPillarBracket001"
  Base = -> Sketch019
  Dir = (0,0,1)
  DirMode = 2
  FaceMakerClass = Part::FaceMakerBullseye
  LengthFwd = 2.4
  LengthRev = 0
  Placement = pos=(15.76,29,60.8) rot=(0,0,1;0rad)
  Solid = true
  Symmetric = false
FEATURE [Sketcher::SketchObject] Sketch020
  FullyConstrained = true
  sketch-geometry (7):
    g0: LineSegment StartX=0 StartY=0 StartZ=0 EndX=0 EndY=6 EndZ=0
    g1: Circle CenterX=0 CenterY=0 CenterZ=0 NormalX=0 NormalY=0 NormalZ=1 AngleXU=0 Radius=1
    g2: Circle CenterX=8 CenterY=6 CenterZ=0 NormalX=0 NormalY=0 NormalZ=1 AngleXU=0 Radius=1
    g3: BSplineCurve PolesCount=3 KnotsCount=2 Degree=2 IsPeriodic=0
    g4: GeomPoint X=0 Y=0 Z=0
    g5: GeomPoint X=8 Y=6 Z=0
    g6: LineSegment StartX=0 StartY=6 StartZ=0 EndX=8 EndY=6 EndZ=0
  constraints (14):
    c: Coincident(g0,g-1)
    c: Distance(g0) = 6
    c: Vertical(g0)
    c: Coincident(g3,g0)
    c: Weight(g1) = 1
    c: Equal(g1,g2)
    c: InternalAlignment(g1,g3)
    c: InternalAlignment(g2,g3)
    c: InternalAlignment(g4,g3)
    c: InternalAlignment(g5,g3)
    c: Block(g3)
    c: Coincident(g6,g0)
    c: Coincident(g6,g3)
    c: Horizontal(g6)
FEATURE [Part::Extrusion] Extrude014  label="caseScrewPillarBracket002"
  Base = -> Sketch020
  Dir = (0,0,1)
  DirMode = 2
  FaceMakerClass = Part::FaceMakerBullseye
  LengthFwd = 2.4
  LengthRev = 0
  Placement = pos=(13.7,29,13.26) rot=(0,-1,0;1.5708rad)
  Solid = true
  Symmetric = false
FEATURE [Sketcher::SketchObject] Sketch021
  FullyConstrained = true
  sketch-geometry (7):
    g0: LineSegment StartX=0 StartY=0 StartZ=0 EndX=0 EndY=6 EndZ=0
    g1: Circle CenterX=0 CenterY=0 CenterZ=0 NormalX=0 NormalY=0 NormalZ=1 AngleXU=0 Radius=1
    g2: Circle CenterX=8 CenterY=6 CenterZ=0 NormalX=0 NormalY=0 NormalZ=1 AngleXU=0 Radius=1
    g3: BSplineCurve PolesCount=3 KnotsCount=2 Degree=2 IsPeriodic=0
    g4: GeomPoint X=0 Y=0 Z=0
    g5: GeomPoint X=8 Y=6 Z=0
    g6: LineSegment StartX=0 StartY=6 StartZ=0 EndX=8 EndY=6 EndZ=0
  constraints (14):
    c: Coincident(g0,g-1)
    c: Distance(g0) = 6
    c: Vertical(g0)
    c: Coincident(g3,g0)
    c: Weight(g1) = 1
    c: Equal(g1,g2)
    c: InternalAlignment(g1,g3)
    c: InternalAlignment(g2,g3)
    c: InternalAlignment(g4,g3)
    c: InternalAlignment(g5,g3)
    c: Block(g3)
    c: Coincident(g6,g0)
    c: Coincident(g6,g3)
    c: Horizontal(g6)
FEATURE [Part::Extrusion] Extrude015  label="caseScrewPillarBracket003"
  Base = -> Sketch021
  Dir = (0,0,1)
  DirMode = 2
  FaceMakerClass = Part::FaceMakerBullseye
  LengthFwd = 2.4
  LengthRev = 0
  Placement = pos=(11.3,29,58.74) rot=(0,1,0;1.5708rad)
  Solid = true
  Symmetric = false
FEATURE [Sketcher::SketchObject] Sketch022
  FullyConstrained = true
  sketch-geometry (7):
    g0: LineSegment StartX=0 StartY=0 StartZ=0 EndX=0 EndY=6 EndZ=0
    g1: Circle CenterX=0 CenterY=0 CenterZ=0 NormalX=0 NormalY=0 NormalZ=1 AngleXU=0 Radius=1
    g2: Circle CenterX=8 CenterY=6 CenterZ=0 NormalX=0 NormalY=0 NormalZ=1 AngleXU=0 Radius=1
    g3: BSplineCurve PolesCount=3 KnotsCount=2 Degree=2 IsPeriodic=0
    g4: GeomPoint X=0 Y=0 Z=0
    g5: GeomPoint X=8 Y=6 Z=0
    g6: LineSegment StartX=0 StartY=6 StartZ=0 EndX=8 EndY=6 EndZ=0
  constraints (14):
    c: Coincident(g0,g-1)
    c: Distance(g0) = 6
    c: Vertical(g0)
    c: Coincident(g3,g0)
    c: Weight(g1) = 1
    c: Equal(g1,g2)
    c: InternalAlignment(g1,g3)
    c: InternalAlignment(g2,g3)
    c: InternalAlignment(g4,g3)
    c: InternalAlignment(g5,g3)
    c: Block(g3)
    c: Coincident(g6,g0)
    c: Coincident(g6,g3)
    c: Horizontal(g6)
FEATURE [Part::Extrusion] Extrude016  label="caseScrewPillarBracket004"
  Base = -> Sketch022
  Dir = (0,0,1)
  DirMode = 2
  FaceMakerClass = Part::FaceMakerBullseye
  LengthFwd = 2.4
  LengthRev = 0
  Placement = pos=(88.3,29,65.23) rot=(0,1,0;1.5708rad)
  Solid = true
  Symmetric = false
FEATURE [Sketcher::SketchObject] Sketch023
  FullyConstrained = true
  sketch-geometry (7):
    g0: LineSegment StartX=0 StartY=0 StartZ=0 EndX=0 EndY=6 EndZ=0
    g1: Circle CenterX=0 CenterY=0 CenterZ=0 NormalX=0 NormalY=0 NormalZ=1 AngleXU=0 Radius=1
    g2: Circle CenterX=8 CenterY=6 CenterZ=0 NormalX=0 NormalY=0 NormalZ=1 AngleXU=0 Radius=1
    g3: BSplineCurve PolesCount=3 KnotsCount=2 Degree=2 IsPeriodic=0
    g4: GeomPoint X=0 Y=0 Z=0
    g5: GeomPoint X=8 Y=6 Z=0
    g6: LineSegment StartX=0 StartY=6 StartZ=0 EndX=8 EndY=6 EndZ=0
  constraints (14):
    c: Coincident(g0,g-1)
    c: Distance(g0) = 6
    c: Vertical(g0)
    c: Coincident(g3,g0)
    c: Weight(g1) = 1
    c: Equal(g1,g2)
    c: InternalAlignment(g1,g3)
    c: InternalAlignment(g2,g3)
    c: InternalAlignment(g4,g3)
    c: InternalAlignment(g5,g3)
    c: Block(g3)
    c: Coincident(g6,g0)
    c: Coincident(g6,g3)
    c: Horizontal(g6)
FEATURE [Part::Extrusion] Extrude017  label="caseScrewPillarBracket005"
  Base = -> Sketch023
  Dir = (0,0,1)
  DirMode = 2
  FaceMakerClass = Part::FaceMakerBullseye
  LengthFwd = 2.4
  LengthRev = 0
  Placement = pos=(90.7,29,6.77) rot=(0,-1,0;1.5708rad)
  Solid = true
  Symmetric = false
FEATURE [Sketcher::SketchObject] Sketch024
  FullyConstrained = true
  sketch-geometry (7):
    g0: LineSegment StartX=0 StartY=0 StartZ=0 EndX=0 EndY=6 EndZ=0
    g1: Circle CenterX=0 CenterY=0 CenterZ=0 NormalX=0 NormalY=0 NormalZ=1 AngleXU=0 Radius=1
    g2: Circle CenterX=8 CenterY=6 CenterZ=0 NormalX=0 NormalY=0 NormalZ=1 AngleXU=0 Radius=1
    g3: BSplineCurve PolesCount=3 KnotsCount=2 Degree=2 IsPeriodic=0
    g4: GeomPoint X=0 Y=0 Z=0
    g5: GeomPoint X=8 Y=6 Z=0
    g6: LineSegment StartX=0 StartY=6 StartZ=0 EndX=8 EndY=6 EndZ=0
  constraints (14):
    c: Coincident(g0,g-1)
    c: Distance(g0) = 6
    c: Vertical(g0)
    c: Coincident(g3,g0)
    c: Weight(g1) = 1
    c: Equal(g1,g2)
    c: InternalAlignment(g1,g3)
    c: InternalAlignment(g2,g3)
    c: InternalAlignment(g4,g3)
    c: InternalAlignment(g5,g3)
    c: Block(g3)
    c: Coincident(g6,g0)
    c: Coincident(g6,g3)
    c: Horizontal(g6)
FEATURE [Part::Extrusion] Extrude018  label="caseScrewPillarBracket006"
  Base = -> Sketch024
  Dir = (0,0,1)
  DirMode = 2
  FaceMakerClass = Part::FaceMakerBullseye
  LengthFwd = 2.4
  LengthRev = 0
  Placement = pos=(103.7,29,6.77) rot=(0,-1,0;1.5708rad)
  Solid = true
  Symmetric = false
FEATURE [Sketcher::SketchObject] Sketch025
  FullyConstrained = true
  sketch-geometry (7):
    g0: LineSegment StartX=0 StartY=0 StartZ=0 EndX=0 EndY=6 EndZ=0
    g1: Circle CenterX=0 CenterY=0 CenterZ=0 NormalX=0 NormalY=0 NormalZ=1 AngleXU=0 Radius=1
    g2: Circle CenterX=8 CenterY=6 CenterZ=0 NormalX=0 NormalY=0 NormalZ=1 AngleXU=0 Radius=1
    g3: BSplineCurve PolesCount=3 KnotsCount=2 Degree=2 IsPeriodic=0
    g4: GeomPoint X=0 Y=0 Z=0
    g5: GeomPoint X=8 Y=6 Z=0
    g6: LineSegment StartX=0 StartY=6 StartZ=0 EndX=8 EndY=6 EndZ=0
  constraints (14):
    c: Coincident(g0,g-1)
    c: Distance(g0) = 6
    c: Vertical(g0)
    c: Coincident(g3,g0)
    c: Weight(g1) = 1
    c: Equal(g1,g2)
    c: InternalAlignment(g1,g3)
    c: InternalAlignment(g2,g3)
    c: InternalAlignment(g4,g3)
    c: InternalAlignment(g5,g3)
    c: Block(g3)
    c: Coincident(g6,g0)
    c: Coincident(g6,g3)
    c: Horizontal(g6)
FEATURE [Part::Extrusion] Extrude019  label="caseScrewPillarBracket007"
  Base = -> Sketch025
  Dir = (0,0,1)
  DirMode = 2
  FaceMakerClass = Part::FaceMakerBullseye
  LengthFwd = 2.4
  LengthRev = 0
  Placement = pos=(101.3,29,65.23) rot=(0,1,0;1.5708rad)
  Solid = true
  Symmetric = false
FEATURE [Part::Box] Box011  label="frontCaseScrewPillarBracket"
  AttacherType = Attacher::AttachEngine3D
  Height = 2.4
  Length = 16
  Placement = pos=(87,28,2.3) rot=(0,0,1;0rad)
  Width = 7
FEATURE [Part::Box] Box012  label="frontCaseScrewPillarBracket001"
  AttacherType = Attacher::AttachEngine3D
  Height = 2.4
  Length = 16
  Placement = pos=(87,28,67.3) rot=(0,0,1;0rad)
  Width = 7
FEATURE [Sketcher::SketchObject] Sketch026
  FullyConstrained = true
  sketch-geometry (17):
    g0: Circle CenterX=-3.5 CenterY=23.5 CenterZ=0 NormalX=0 NormalY=0 NormalZ=1 AngleXU=0 Radius=1
    g1: Circle CenterX=-1 CenterY=15.25 CenterZ=0 NormalX=0 NormalY=0 NormalZ=1 AngleXU=0 Radius=1
    g2: Circle CenterX=-3.5 CenterY=7 CenterZ=0 NormalX=0 NormalY=0 NormalZ=1 AngleXU=0 Radius=1
    g3: BSplineCurve PolesCount=3 KnotsCount=2 Degree=2 IsPeriodic=0
    g4: GeomPoint X=-3.5 Y=23.5 Z=0
    g5: GeomPoint X=-3.5 Y=7 Z=0
    g6: Circle CenterX=-4.8 CenterY=30.5 CenterZ=0 NormalX=0 NormalY=0 NormalZ=1 AngleXU=0 Radius=1
    g7: Circle CenterX=-3.5 CenterY=30.5 CenterZ=0 NormalX=0 NormalY=0 NormalZ=1 AngleXU=0 Radius=1
    g8: Circle CenterX=-3.5 CenterY=29.2 CenterZ=0 NormalX=0 NormalY=0 NormalZ=1 AngleXU=0 Radius=1
    g9: BSplineCurve PolesCount=3 KnotsCount=2 Degree=2 IsPeriodic=0
    g10: GeomPoint X=-4.8 Y=30.5 Z=0
    g11: GeomPoint X=-3.5 Y=29.2 Z=0
    g12: LineSegment StartX=-3.5 StartY=29.2 StartZ=0 EndX=-3.5 EndY=23.5 EndZ=0
    g13: LineSegment StartX=-4.8 StartY=30.5 StartZ=0 EndX=0 EndY=30.5 EndZ=0
    g14: LineSegment StartX=-3.5 StartY=5 StartZ=0 EndX=-3.5 EndY=7 EndZ=0
    g15: LineSegment StartX=0 StartY=5 StartZ=0 EndX=0 EndY=30.5 EndZ=0
    g16: LineSegment StartX=-3.5 StartY=5 StartZ=0 EndX=0 EndY=5 EndZ=0
  constraints (33):
    c: Weight(g0) = 1
    c: Equal(g0,g1)
    c: Equal(g0,g2)
    c: InternalAlignment(g0,g3)
    c: InternalAlignment(g1,g3)
    c: InternalAlignment(g2,g3)
    c: InternalAlignment(g4,g3)
    c: InternalAlignment(g5,g3)
    c: Block(g3)
    c: Weight(g6) = 1
    c: Equal(g6,g7)
    c: Equal(g6,g8)
    c: InternalAlignment(g6,g9)
    c: InternalAlignment(g7,g9)
    c: InternalAlignment(g8,g9)
    c: InternalAlignment(g10,g9)
    c: InternalAlignment(g11,g9)
    c: Block(g9)
    c: Coincident(g12,g9)
    c: Coincident(g12,g3)
    c: Vertical(g12)
    c: Coincident(g13,g9)
    c: Horizontal(g13)
    c: Distance(g13) = 4.8
    c: Coincident(g14,g3)
    c: Vertical(g14)
    c: Coincident(g15,g13)
    c: Vertical(g15)
    c: Tangent(g15,g1)
    c: Distance(g14) = 2
    c: Coincident(g16,g14)
    c: Horizontal(g16)
    c: Coincident(g15,g16)
FEATURE [Part::Feature] Face050
  shape: bbox 4.8 x 25.5 x 2e-07 mm, 1 faces, 0 solids (baked)
FEATURE [Part::Revolution] Revolve054  label="moreFrontCaseScrewPost001"
  Angle = 360
  Axis = (0,1,0)
  Base = (0,0,0)
  FaceMakerClass = Part::FaceMakerBullseye
  Placement = pos=(102.5,4.5,3.5) rot=(0,0,1;0rad)
  Solid = false
  Source = -> Face050
  Symmetric = false
FEATURE [Part::Feature] Face051
  shape: bbox 4.8 x 25.5 x 2e-07 mm, 1 faces, 0 solids (baked)
FEATURE [Part::Revolution] Revolve055  label="moreFrontCaseScrewPost002"
  Angle = 360
  Axis = (0,1,0)
  Base = (0,0,0)
  FaceMakerClass = Part::FaceMakerBullseye
  Placement = pos=(102.5,4.5,68.5) rot=(0,0,1;0rad)
  Solid = false
  Source = -> Face051
  Symmetric = false
FEATURE [Sketcher::SketchObject] Sketch027
  FullyConstrained = true
  sketch-geometry (10):
    g0: LineSegment StartX=-1.6 StartY=4.7 StartZ=0 EndX=-1.6 EndY=1.7 EndZ=0
    g1: LineSegment StartX=-3.5 StartY=4.7 StartZ=0 EndX=-1.6 EndY=4.7 EndZ=0
    g2: LineSegment StartX=-1.6 StartY=1.7 StartZ=0 EndX=-1.6 EndY=1.5 EndZ=0
    g3: LineSegment StartX=-1.6 StartY=1.5 StartZ=0 EndX=-5.2 EndY=1.5 EndZ=0
    g4: Circle CenterX=-3.5 CenterY=4.7 CenterZ=0 NormalX=0 NormalY=0 NormalZ=1 AngleXU=0 Radius=1
    g5: Circle CenterX=-3.59627 CenterY=2.99743 CenterZ=0 NormalX=0 NormalY=0 NormalZ=1 AngleXU=0 Radius=1
    g6: Circle CenterX=-5.2 CenterY=1.5 CenterZ=0 NormalX=0 NormalY=0 NormalZ=1 AngleXU=0 Radius=1
    g7: BSplineCurve PolesCount=3 KnotsCount=2 Degree=2 IsPeriodic=0
    g8: GeomPoint X=-3.5 Y=4.7 Z=0
    g9: GeomPoint X=-5.2 Y=1.5 Z=0
  constraints (23):
    c: Vertical(g0)
    c: Distance(g0) = 3
    c: Coincident(g1,g0)
    c: Horizontal(g1)
    c: Block(g0)
    c: Block(g1)
    c: Coincident(g2,g0)
    c: Vertical(g2)
    c: Distance(g2) = 0.2
    c: Coincident(g3,g2)
    c: Horizontal(g3)
    c: Block(g3)
    c: Coincident(g7,g1)
    c: Weight(g4) = 1
    c: Equal(g4,g5)
    c: Equal(g4,g6)
    c: Coincident(g7,g3)
    c: InternalAlignment(g4,g7)
    c: InternalAlignment(g5,g7)
    c: InternalAlignment(g6,g7)
    c: InternalAlignment(g8,g7)
    c: InternalAlignment(g9,g7)
    c: Block(g7)
FEATURE [Sketcher::SketchObject] Sketch028
  FullyConstrained = true
  sketch-geometry (18):
    g0: LineSegment StartX=0 StartY=3e-16 StartZ=0 EndX=0 EndY=1.7 EndZ=0
    g1: LineSegment StartX=-3.5 StartY=0 StartZ=0 EndX=-3.5 EndY=0.9 EndZ=0
    g2: Circle CenterX=-2.7 CenterY=1.7 CenterZ=0 NormalX=0 NormalY=0 NormalZ=1 AngleXU=0 Radius=1
    g3: Circle CenterX=-3.5 CenterY=1.7 CenterZ=0 NormalX=0 NormalY=0 NormalZ=1 AngleXU=0 Radius=1
    g4: Circle CenterX=-3.5 CenterY=0.9 CenterZ=0 NormalX=0 NormalY=0 NormalZ=1 AngleXU=0 Radius=1
    g5: BSplineCurve PolesCount=3 KnotsCount=2 Degree=2 IsPeriodic=0
    g6: GeomPoint X=-2.7 Y=1.7 Z=0
    g7: GeomPoint X=-3.5 Y=0.9 Z=0
    g8: LineSegment StartX=-3.5 StartY=0 StartZ=0 EndX=-3.5 EndY=-7 EndZ=0
    g9: LineSegment StartX=0 StartY=3e-16 StartZ=0 EndX=0 EndY=-7 EndZ=0
    g10: LineSegment StartX=-3.5 StartY=-7 StartZ=0 EndX=0 EndY=-7 EndZ=0
    g11: LineSegment StartX=-2.7 StartY=1.7 StartZ=0 EndX=-1.6 EndY=1.7 EndZ=0
    g12: LineSegment StartX=0 StartY=1.7 StartZ=0 EndX=0 EndY=4.5 EndZ=0
    g13: LineSegment StartX=0 StartY=4.5 StartZ=0 EndX=0 EndY=10.8 EndZ=0
    g14: LineSegment StartX=0 StartY=10.8 StartZ=0 EndX=-2 EndY=10.8 EndZ=0
    g15: LineSegment StartX=-1.6 StartY=4.7 StartZ=0 EndX=-1.6 EndY=1.7 EndZ=0
    g16: LineSegment StartX=-1.6 StartY=4.7 StartZ=0 EndX=-2 EndY=4.7 EndZ=0
    g17: LineSegment StartX=-2 StartY=4.7 StartZ=0 EndX=-2 EndY=10.8 EndZ=0
  constraints (44):
    c: Vertical(g0)
    c: Vertical(g1)
    c: Distance(g1) = 0.9
    c: Block(g0)
    c: Distance(g0) = 1.7
    c: Weight(g2) = 1
    c: Equal(g2,g3)
    c: Equal(g2,g4)
    c: Coincident(g5,g1)
    c: InternalAlignment(g2,g5)
    c: InternalAlignment(g3,g5)
    c: InternalAlignment(g4,g5)
    c: InternalAlignment(g6,g5)
    c: InternalAlignment(g7,g5)
    c: Block(g5)
    c: Coincident(g8,g1)
    c: Vertical(g8)
    c: Distance(g8) = 7
    c: Vertical(g9)
    c: Equal(g8,g9) = 7
    c: Coincident(g9,g0)
    c: Coincident(g10,g8)
    c: Coincident(g10,g9)
    c: Horizontal(g10)
    c: Coincident(g11,g5)
    c: Horizontal(g11)
    c: Coincident(g12,g0)
    c: Vertical(g12)
    c: Distance(g12) = 2.8
    c: Coincident(g13,g12)
    c: Vertical(g13)
    c: Distance(g13) = 6.3
    c: Coincident(g14,g13)
    c: Horizontal(g14)
    c: Distance(g14) = 2
    c: Vertical(g15)
    c: Distance(g15) = 3
    c: Block(g11)
    c: Coincident(g15,g11)
    c: Coincident(g16,g15)
    c: Horizontal(g16)
    c: Coincident(g17,g16)
    c: Coincident(g17,g14)
    c: Vertical(g17)
FEATURE [Part::Revolution] Revolve040  label="backCaseScrewRetainer001"
  Angle = 360
  Axis = (0,1,0)
  Base = (0,0,0)
  FaceMakerClass = Part::FaceMakerBullseye
  Placement = pos=(12.5,3,10) rot=(0,0,1;0rad)
  Solid = false
  Source = -> Face036
  Symmetric = false
FEATURE [Part::Feature] Face055
  shape: bbox 3.5 x 30.2 x 2e-07 mm, 1 faces, 0 solids (baked)
FEATURE [Part::Revolution] Revolve059  label="backCaseScrewPost"
  Angle = 360
  Axis = (0,1,0)
  Base = (0,0,0)
  FaceMakerClass = Part::FaceMakerBullseye
  Placement = pos=(12.5,4.5,10) rot=(0,0,1;0rad)
  Solid = false
  Source = -> Face055
  Symmetric = false
FEATURE [Part::Feature] Face056
  shape: bbox 3.5 x 30.2 x 2e-07 mm, 1 faces, 0 solids (baked)
FEATURE [Part::Revolution] Revolve060  label="backCaseScrewPost001"
  Angle = 360
  Axis = (0,1,0)
  Base = (0,0,0)
  FaceMakerClass = Part::FaceMakerBullseye
  Placement = pos=(12.5,4.5,62) rot=(0,0,1;0rad)
  Solid = false
  Source = -> Face056
  Symmetric = false
FEATURE [Part::Feature] Face057
  shape: bbox 3.5 x 17.8 x 2e-07 mm, 1 faces, 0 solids (baked)
FEATURE [Part::Revolution] Revolve061  label="removeToCreateScrewAndThreadedInsertHole"
  Angle = 360
  Axis = (0,1,0)
  Base = (0,0,0)
  FaceMakerClass = Part::FaceMakerBullseye
  Placement = pos=(12.5,0,10) rot=(0,0,1;0rad)
  Solid = false
  Source = -> Face057
  Symmetric = false
FEATURE [Part::Feature] Face058
  shape: bbox 3.5 x 17.8 x 2e-07 mm, 1 faces, 0 solids (baked)
FEATURE [Part::Revolution] Revolve062  label="removeToCreateScrewAndThreadedInsertHole001"
  Angle = 360
  Axis = (0,1,0)
  Base = (0,0,0)
  FaceMakerClass = Part::FaceMakerBullseye
  Placement = pos=(12.5,0,62) rot=(0,0,1;0rad)
  Solid = false
  Source = -> Face058
  Symmetric = false
FEATURE [Part::Feature] Face059
  shape: bbox 3.5 x 17.8 x 2e-07 mm, 1 faces, 0 solids (baked)
FEATURE [Part::Revolution] Revolve063  label="removeToCreateScrewAndThreadedInsertHole002"
  Angle = 360
  Axis = (0,1,0)
  Base = (0,0,0)
  FaceMakerClass = Part::FaceMakerBullseye
  Placement = pos=(89.5,0,68.5) rot=(0,0,1;0rad)
  Solid = false
  Source = -> Face059
  Symmetric = false
FEATURE [Part::Feature] Face060
  shape: bbox 3.5 x 17.8 x 2e-07 mm, 1 faces, 0 solids (baked)
FEATURE [Part::Revolution] Revolve064  label="removeToCreateScrewAndThreadedInsertHole003"
  Angle = 360
  Axis = (0,1,0)
  Base = (0,0,0)
  FaceMakerClass = Part::FaceMakerBullseye
  Placement = pos=(89.5,0,3.5) rot=(0,0,1;0rad)
  Solid = false
  Source = -> Face060
  Symmetric = false
FEATURE [Part::Feature] Face061
  shape: bbox 3.5 x 17.8 x 2e-07 mm, 1 faces, 0 solids (baked)
FEATURE [Part::Revolution] Revolve065  label="removeToCreateScrewAndThreadedInsertHole004"
  Angle = 360
  Axis = (0,1,0)
  Base = (0,0,0)
  FaceMakerClass = Part::FaceMakerBullseye
  Placement = pos=(102.5,4.7,3.5) rot=(0,0,1;0rad)
  Solid = false
  Source = -> Face061
  Symmetric = false
FEATURE [Part::Feature] Face062
  shape: bbox 3.5 x 17.8 x 2e-07 mm, 1 faces, 0 solids (baked)
FEATURE [Part::Revolution] Revolve066  label="removeToCreateScrewAndThreadedInsertHole005"
  Angle = 360
  Axis = (0,1,0)
  Base = (0,0,0)
  FaceMakerClass = Part::FaceMakerBullseye
  Placement = pos=(102.5,4.7,68.5) rot=(0,0,1;0rad)
  Solid = false
  Source = -> Face062
  Symmetric = false
FEATURE [Part::MultiFuse] Fusion047  label="makeHoles"
  Shapes = -> [Revolve066,Revolve065,Revolve064,Revolve063,Revolve062,Revolve061]
FEATURE [Part::Feature] Face063
  shape: bbox 3.6 x 3.2 x 2e-07 mm, 1 faces, 0 solids (baked)
FEATURE [Part::Revolution] Revolve067  label="moreFrontCaseScrewRetainer002"
  Angle = 360
  Axis = (0,1,0)
  Base = (0,0,0)
  FaceMakerClass = Part::FaceMakerBullseye
  Placement = pos=(102.5,4.5,68.5) rot=(0,0,1;0rad)
  Solid = false
  Source = -> Face063
  Symmetric = false
FEATURE [Part::Feature] Face064
  shape: bbox 3.6 x 3.2 x 2e-07 mm, 1 faces, 0 solids (baked)
FEATURE [Part::Revolution] Revolve068  label="moreFrontCaseScrewRetainer003"
  Angle = 360
  Axis = (0,1,0)
  Base = (0,0,0)
  FaceMakerClass = Part::FaceMakerBullseye
  Placement = pos=(102.5,4.5,3.5) rot=(0,0,1;0rad)
  Solid = false
  Source = -> Face064
  Symmetric = false
FEATURE [Part::Feature] Face065
  shape: bbox 3.5 x 17.8 x 2e-07 mm, 1 faces, 0 solids (baked)
FEATURE [Part::Revolution] Revolve069  label="removeToCreateScrewAndThreadedInsertHole006"
  Angle = 360
  Axis = (0,1,0)
  Base = (0,0,0)
  FaceMakerClass = Part::FaceMakerBullseye
  Placement = pos=(12.5,0,10) rot=(0,0,1;0rad)
  Solid = false
  Source = -> Face065
  Symmetric = false
FEATURE [Part::Feature] Face066
  shape: bbox 3.5 x 17.8 x 2e-07 mm, 1 faces, 0 solids (baked)
FEATURE [Part::Revolution] Revolve070  label="removeToCreateScrewAndThreadedInsertHole007"
  Angle = 360
  Axis = (0,1,0)
  Base = (0,0,0)
  FaceMakerClass = Part::FaceMakerBullseye
  Placement = pos=(12.5,0,62) rot=(0,0,1;0rad)
  Solid = false
  Source = -> Face066
  Symmetric = false
FEATURE [Part::Feature] Face067
  shape: bbox 3.5 x 17.8 x 2e-07 mm, 1 faces, 0 solids (baked)
FEATURE [Part::Revolution] Revolve071  label="removeToCreateScrewAndThreadedInsertHole008"
  Angle = 360
  Axis = (0,1,0)
  Base = (0,0,0)
  FaceMakerClass = Part::FaceMakerBullseye
  Placement = pos=(89.5,0,68.5) rot=(0,0,1;0rad)
  Solid = false
  Source = -> Face067
  Symmetric = false
FEATURE [Part::Feature] Face068
  shape: bbox 3.5 x 17.8 x 2e-07 mm, 1 faces, 0 solids (baked)
FEATURE [Part::Revolution] Revolve072  label="removeToCreateScrewAndThreadedInsertHole009"
  Angle = 360
  Axis = (0,1,0)
  Base = (0,0,0)
  FaceMakerClass = Part::FaceMakerBullseye
  Placement = pos=(89.5,0,3.5) rot=(0,0,1;0rad)
  Solid = false
  Source = -> Face068
  Symmetric = false
FEATURE [Part::Feature] Face069
  shape: bbox 3.5 x 17.8 x 2e-07 mm, 1 faces, 0 solids (baked)
FEATURE [Part::Feature] Face070
  shape: bbox 3.5 x 17.8 x 2e-07 mm, 1 faces, 0 solids (baked)
FEATURE [Part::Revolution] Revolve073  label="removeToCreateScrewAndThreadedInsertHole010"
  Angle = 360
  Axis = (0,1,0)
  Base = (0,0,0)
  FaceMakerClass = Part::FaceMakerBullseye
  Placement = pos=(102.5,4.7,3.5) rot=(0,0,1;0rad)
  Solid = false
  Source = -> Face069
  Symmetric = false
FEATURE [Part::Revolution] Revolve074  label="removeToCreateScrewAndThreadedInsertHole011"
  Angle = 360
  Axis = (0,1,0)
  Base = (0,0,0)
  FaceMakerClass = Part::FaceMakerBullseye
  Placement = pos=(102.5,4.7,68.5) rot=(0,0,1;0rad)
  Solid = false
  Source = -> Face070
  Symmetric = false
FEATURE [Part::MultiFuse] Fusion048  label="makeHoles001"
  Shapes = -> [Revolve074,Revolve073,Revolve072,Revolve071,Revolve070,Revolve069]
FEATURE [Part::MultiFuse] Fusion049  label="caseScrewRetainers"
  Shapes = -> [Revolve067,Revolve068,Revolve048,Revolve047,Revolve039,Revolve040]
FEATURE [Part::Cut] Cut015  label="caseScrewRetainers001"
  Base = -> Fusion049
  Tool = -> Fusion048
FEATURE [Part::MultiFuse] Fusion050  label="casePillars"
  Shapes = -> [Revolve055,Revolve054,Revolve043,Revolve046,Revolve059,Revolve060]
FEATURE [Part::Feature] Face071 .. Face076  x6 (patterned run collapsed; names and placements below)
  shape: bbox 3.5 x 17.8 x 2e-07 mm, 1 faces, 0 solids (baked)
FEATURE [Part::Revolution] Revolve075  label="removeToCreateScrewAndThreadedInsertHole012"
  Angle = 360
  Axis = (0,1,0)
  Base = (0,0,0)
  FaceMakerClass = Part::FaceMakerBullseye
  Placement = pos=(12.5,0,10) rot=(0,0,1;0rad)
  Solid = false
  Source = -> Face071
  Symmetric = false
FEATURE [Part::Revolution] Revolve076  label="removeToCreateScrewAndThreadedInsertHole013"
  Angle = 360
  Axis = (0,1,0)
  Base = (0,0,0)
  FaceMakerClass = Part::FaceMakerBullseye
  Placement = pos=(12.5,0,62) rot=(0,0,1;0rad)
  Solid = false
  Source = -> Face072
  Symmetric = false
FEATURE [Part::Revolution] Revolve077  label="removeToCreateScrewAndThreadedInsertHole014"
  Angle = 360
  Axis = (0,1,0)
  Base = (0,0,0)
  FaceMakerClass = Part::FaceMakerBullseye
  Placement = pos=(89.5,0,68.5) rot=(0,0,1;0rad)
  Solid = false
  Source = -> Face073
  Symmetric = false
FEATURE [Part::Revolution] Revolve078  label="removeToCreateScrewAndThreadedInsertHole015"
  Angle = 360
  Axis = (0,1,0)
  Base = (0,0,0)
  FaceMakerClass = Part::FaceMakerBullseye
  Placement = pos=(89.5,0,3.5) rot=(0,0,1;0rad)
  Solid = false
  Source = -> Face074
  Symmetric = false
FEATURE [Part::Revolution] Revolve079  label="removeToCreateScrewAndThreadedInsertHole016"
  Angle = 360
  Axis = (0,1,0)
  Base = (0,0,0)
  FaceMakerClass = Part::FaceMakerBullseye
  Placement = pos=(102.5,4.7,3.5) rot=(0,0,1;0rad)
  Solid = false
  Source = -> Face075
  Symmetric = false
FEATURE [Part::Revolution] Revolve080  label="removeToCreateScrewAndThreadedInsertHole017"
  Angle = 360
  Axis = (0,1,0)
  Base = (0,0,0)
  FaceMakerClass = Part::FaceMakerBullseye
  Placement = pos=(102.5,4.7,68.5) rot=(0,0,1;0rad)
  Solid = false
  Source = -> Face076
  Symmetric = false
FEATURE [Part::MultiFuse] Fusion051  label="makeHoles002"
  Shapes = -> [Revolve080,Revolve079,Revolve078,Revolve077,Revolve076,Revolve075]
FEATURE [Part::Cut] Cut016  label="caesPillars"
  Base = -> Fusion050
  Tool = -> Fusion051
FEATURE [Part::Revolution] Revolve009  label="plugHousing016"
  Angle = 360
  Axis = (0,1,0)
  Base = (0,0,0)
  FaceMakerClass = Part::FaceMakerBullseye
  Placement = pos=(0,0,36.15) rot=(0,0,1;0rad)
  Solid = false
  Source = -> Face012
  Symmetric = false
FEATURE [Part::MultiFuse] Fusion014  label="plugHousing023"
  Placement = pos=(0,0,0) rot=(0,0,1;1.5708rad)
  Shapes = -> [Revolve011,Revolve009]
FEATURE [Part::Revolution] Revolve010  label="plugHousing017"
  Angle = 360
  Axis = (0,1,0)
  Base = (0,0,0)
  FaceMakerClass = Part::FaceMakerBullseye
  Placement = pos=(0,0,36.15) rot=(0,0,1;0rad)
  Solid = false
  Source = -> Face014
  Symmetric = false
FEATURE [Part::MultiFuse] Fusion015  label="plugHousing024"
  Placement = pos=(0,0,0) rot=(0,0,1;1.5708rad)
  Shapes = -> [Revolve010,Revolve015]
FEATURE [Part::Revolution] Revolve014  label="plugHousing026"
  Angle = 360
  Axis = (0,1,0)
  Base = (0,0,0)
  FaceMakerClass = Part::FaceMakerBullseye
  Placement = pos=(0,0,36.15) rot=(0,0,1;0rad)
  Solid = false
  Source = -> Face011
  Symmetric = false
FEATURE [Part::Revolution] Revolve013  label="plugHousing025"
  Angle = 360
  Axis = (0,1,0)
  Base = (0,0,0)
  FaceMakerClass = Part::FaceMakerBullseye
  Placement = pos=(0,0,36.15) rot=(0,0,1;0rad)
  Solid = false
  Source = -> Face015
  Symmetric = false
FEATURE [Part::MultiFuse] Fusion016  label="plugHousing028"
  Placement = pos=(0,19,0) rot=(0,0,1;3.14159rad)
  Shapes = -> [Fusion014,Fusion013]
FEATURE [Part::MultiFuse] Fusion011  label="plugHousing018"
  Placement = pos=(0,0,0) rot=(0,0,1;1.5708rad)
  Shapes = -> [Revolve014,Revolve013]
FEATURE [Part::MultiFuse] Fusion012  label="plugHousing019"
  Placement = pos=(0,19,0) rot=(0,0,1;3.14159rad)
  Shapes = -> [Fusion011,Fusion015]
FEATURE [Part::MultiFuse] Fusion017  label="plugHousing029"
  Placement = pos=(122.621,0,-0.15) rot=(0,0,1;0rad)
  Shapes = -> [Fusion016,Fusion012]
FEATURE [Part::MultiFuse] Fusion052  label="casePillarRetainers"
  Shapes = -> [Extrude012,Extrude013,Extrude014,Extrude015,Extrude016,Extrude017,Extrude018,Extrude019,Box011,Box012]
FEATURE [Part::Feature] Face077
  shape: bbox 3.5 x 17.8 x 2e-07 mm, 1 faces, 0 solids (baked)
FEATURE [Part::Revolution] Revolve081  label="removeToCreateScrewAndThreadedInsertHole018"
  Angle = 360
  Axis = (0,1,0)
  Base = (0,0,0)
  FaceMakerClass = Part::FaceMakerBullseye
  Placement = pos=(62.3,30.3,19.7) rot=(0,0,1;0rad)
  Solid = false
  Source = -> Face077
  Symmetric = false
FEATURE [Part::Feature] Face078
  shape: bbox 3.5 x 17.8 x 2e-07 mm, 1 faces, 0 solids (baked)
FEATURE [Part::Revolution] Revolve082  label="removeToCreateScrewAndThreadedInsertHole019"
  Angle = 360
  Axis = (0,1,0)
  Base = (0,0,0)
  FaceMakerClass = Part::FaceMakerBullseye
  Placement = pos=(62.3,30.3,51.7) rot=(0,0,1;0rad)
  Solid = false
  Source = -> Face078
  Symmetric = false
FEATURE [Part::Feature] Face079
  shape: bbox 3.5 x 17.8 x 2e-07 mm, 1 faces, 0 solids (baked)
FEATURE [Part::Revolution] Revolve083  label="removeToCreateScrewAndThreadedInsertHole020"
  Angle = 360
  Axis = (0,1,0)
  Base = (0,0,0)
  FaceMakerClass = Part::FaceMakerBullseye
  Placement = pos=(30.3,30.3,19.7) rot=(0,0,1;0rad)
  Solid = false
  Source = -> Face079
  Symmetric = false
FEATURE [Part::Feature] Face080
  shape: bbox 3.5 x 17.8 x 2e-07 mm, 1 faces, 0 solids (baked)
FEATURE [Part::Revolution] Revolve084  label="removeToCreateScrewAndThreadedInsertHole021"
  Angle = 360
  Axis = (0,1,0)
  Base = (0,0,0)
  FaceMakerClass = Part::FaceMakerBullseye
  Placement = pos=(30.3,30.3,51.7) rot=(0,0,1;0rad)
  Solid = false
  Source = -> Face080
  Symmetric = false
FEATURE [Part::MultiFuse] Fusion053  label="createThreadedInsertHolesForFan"
  Shapes = -> [Revolve081,Revolve082,Revolve083,Revolve084]
FEATURE [Part::Cut] Cut017  label="fanScrewHousing001"
  Base = -> Fusion046
  Tool = -> Fusion053
FEATURE [Part::Feature] Face081
  shape: bbox 3.5 x 17.8 x 2e-07 mm, 1 faces, 0 solids (baked)
FEATURE [Part::Revolution] Revolve085  label="removeToCreateScrewAndThreadedInsertHole022"
  Angle = 360
  Axis = (0,1,0)
  Base = (0,0,0)
  FaceMakerClass = Part::FaceMakerBullseye
  Placement = pos=(62.3,30.3,19.7) rot=(0,0,1;0rad)
  Solid = false
  Source = -> Face081
  Symmetric = false
FEATURE [Part::Feature] Face082
  shape: bbox 3.5 x 17.8 x 2e-07 mm, 1 faces, 0 solids (baked)
FEATURE [Part::Revolution] Revolve086  label="removeToCreateScrewAndThreadedInsertHole023"
  Angle = 360
  Axis = (0,1,0)
  Base = (0,0,0)
  FaceMakerClass = Part::FaceMakerBullseye
  Placement = pos=(62.3,30.3,51.7) rot=(0,0,1;0rad)
  Solid = false
  Source = -> Face082
  Symmetric = false
FEATURE [Part::Feature] Face083
  shape: bbox 3.5 x 17.8 x 2e-07 mm, 1 faces, 0 solids (baked)
FEATURE [Part::Revolution] Revolve087  label="removeToCreateScrewAndThreadedInsertHole024"
  Angle = 360
  Axis = (0,1,0)
  Base = (0,0,0)
  FaceMakerClass = Part::FaceMakerBullseye
  Placement = pos=(30.3,30.3,19.7) rot=(0,0,1;0rad)
  Solid = false
  Source = -> Face083
  Symmetric = false
FEATURE [Part::Feature] Face084
  shape: bbox 3.5 x 17.8 x 2e-07 mm, 1 faces, 0 solids (baked)
FEATURE [Part::Revolution] Revolve088  label="removeToCreateScrewAndThreadedInsertHole025"
  Angle = 360
  Axis = (0,1,0)
  Base = (0,0,0)
  FaceMakerClass = Part::FaceMakerBullseye
  Placement = pos=(30.3,30.3,51.7) rot=(0,0,1;0rad)
  Solid = false
  Source = -> Face084
  Symmetric = false
FEATURE [Part::MultiFuse] Fusion054  label="createThreadedInsertHolesForFan001"
  Shapes = -> [Revolve085,Revolve086,Revolve087,Revolve088]
FEATURE [Part::Cut] Cut018  label="top007"
  Base = -> Fusion040
  Tool = -> Fusion054
FEATURE [Sketcher::SketchObject] Sketch029
  FullyConstrained = false
  Placement = pos=(0,0,0) rot=(1,0,0;1.5708rad)
  sketch-geometry (24):
    g0: ArcOfCircle CenterX=-4 CenterY=-10.5 CenterZ=0 NormalX=0 NormalY=0 NormalZ=1 AngleXU=0 Radius=1.5 StartAngle=6e-16 EndAngle=3.14159
    g1: ArcOfCircle CenterX=-34.2 CenterY=-10.5 CenterZ=0 NormalX=0 NormalY=0 NormalZ=1 AngleXU=0 Radius=1.5 StartAngle=0 EndAngle=3.14159
    g2: ArcOfCircle CenterX=-34.2 CenterY=-27.7 CenterZ=0 NormalX=0 NormalY=0 NormalZ=1 AngleXU=0 Radius=1.5 StartAngle=3.14159 EndAngle=6.28319
    g3: ArcOfCircle CenterX=-4 CenterY=-27.7 CenterZ=0 NormalX=0 NormalY=0 NormalZ=1 AngleXU=0 Radius=1.5 StartAngle=3.1416 EndAngle=6.28319
    g4: ArcOfCircle CenterX=-10 CenterY=-4.3 CenterZ=0 NormalX=0 NormalY=0 NormalZ=1 AngleXU=0 Radius=1.5 StartAngle=2e-16 EndAngle=3.14159
    g5: ArcOfCircle CenterX=-16.1 CenterY=-1.8 CenterZ=0 NormalX=0 NormalY=0 NormalZ=1 AngleXU=0 Radius=1.5 StartAngle=5e-16 EndAngle=3.14159
    g6: ArcOfCircle CenterX=-22.1 CenterY=-1.8 CenterZ=0 NormalX=0 NormalY=0 NormalZ=1 AngleXU=0 Radius=1.5 StartAngle=5e-16 EndAngle=3.14159
    g7: ArcOfCircle CenterX=-28.2 CenterY=-4.3 CenterZ=0 NormalX=0 NormalY=0 NormalZ=1 AngleXU=0 Radius=1.5 StartAngle=2e-16 EndAngle=3.14159
    g8: ArcOfCircle CenterX=-10 CenterY=-33.9 CenterZ=0 NormalX=0 NormalY=0 NormalZ=1 AngleXU=0 Radius=1.5 StartAngle=3.14159 EndAngle=6.28319
    g9: ArcOfCircle CenterX=-16.1 CenterY=-36.4 CenterZ=0 NormalX=0 NormalY=0 NormalZ=1 AngleXU=0 Radius=1.5 StartAngle=3.14159 EndAngle=6.28319
    g10: ArcOfCircle CenterX=-22.1 CenterY=-36.4 CenterZ=0 NormalX=0 NormalY=0 NormalZ=1 AngleXU=0 Radius=1.5 StartAngle=3.14159 EndAngle=6.28319
    g11: ArcOfCircle CenterX=-28.2 CenterY=-33.9 CenterZ=0 NormalX=0 NormalY=0 NormalZ=1 AngleXU=0 Radius=1.5 StartAngle=3.14159 EndAngle=6.28319
    g12: LineSegment StartX=-35.7 StartY=-10.5 StartZ=0 EndX=-35.7 EndY=-27.7 EndZ=0
    g13: LineSegment StartX=-32.7 StartY=-10.5 StartZ=0 EndX=-32.7 EndY=-27.7 EndZ=0
    g14: LineSegment StartX=-29.7 StartY=-33.9 StartZ=0 EndX=-29.7 EndY=-4.3 EndZ=0
    g15: LineSegment StartX=-26.7 StartY=-33.9 StartZ=0 EndX=-26.7 EndY=-4.3 EndZ=0
    g16: LineSegment StartX=-2.5 StartY=-10.5 StartZ=0 EndX=-2.5 EndY=-27.7 EndZ=0
    g17: LineSegment StartX=-8.5 StartY=-4.3 StartZ=0 EndX=-8.5 EndY=-33.9 EndZ=0
    g18: LineSegment StartX=-5.5 StartY=-10.5 StartZ=0 EndX=-5.5 EndY=-27.7 EndZ=0
    g19: LineSegment StartX=-11.5 StartY=-4.3 StartZ=0 EndX=-11.5 EndY=-33.9 EndZ=0
    g20: LineSegment StartX=-14.6 StartY=-1.8 StartZ=0 EndX=-14.6 EndY=-36.4 EndZ=0
    g21: LineSegment StartX=-17.6 StartY=-1.8 StartZ=0 EndX=-17.6 EndY=-36.4 EndZ=0
    g22: LineSegment StartX=-20.6 StartY=-36.4 StartZ=0 EndX=-20.6 EndY=-1.8 EndZ=0
    g23: LineSegment StartX=-23.6 StartY=-1.8 StartZ=0 EndX=-23.6 EndY=-36.4 EndZ=0
  constraints (48):
    c: Block(g0)
    c: Block(g1)
    c: Block(g2)
    c: Block(g3)
    c: Block(g4)
    c: Block(g5)
    c: Block(g6)
    c: Block(g7)
    c: Block(g8)
    c: Block(g9)
    c: Block(g10)
    c: Block(g11)
    c: Coincident(g12,g1)
    c: Coincident(g12,g2)
    c: Vertical(g12)
    c: Coincident(g13,g1)
    c: Coincident(g13,g2)
    c: Vertical(g13)
    c: Coincident(g14,g11)
    c: Coincident(g14,g7)
    c: Vertical(g14)
    c: Coincident(g15,g11)
    c: Coincident(g15,g7)
    c: Vertical(g15)
    c: Coincident(g16,g0)
    c: Coincident(g16,g3)
    c: Vertical(g16)
    c: Coincident(g17,g4)
    c: Coincident(g17,g8)
    c: Vertical(g17)
    c: Coincident(g18,g0)
    c: Coincident(g18,g3)
    c: Vertical(g18)
    c: Coincident(g19,g4)
    c: Coincident(g19,g8)
    c: Vertical(g19)
    c: Coincident(g20,g5)
    c: Coincident(g20,g9)
    c: Vertical(g20)
    c: Coincident(g21,g5)
    c: Coincident(g21,g9)
    c: Vertical(g21)
    c: Coincident(g22,g10)
    c: Coincident(g22,g6)
    c: Vertical(g22)
    c: Coincident(g23,g6)
    c: Coincident(g23,g10)
    c: Vertical(g23)
FEATURE [Part::Extrusion] Extrude020  label="removeToCreateFanGrillHoles"
  Base = -> Sketch029
  Dir = (0,-1,6e-16)
  DirMode = 2
  FaceMakerClass = Part::FaceMakerBullseye
  LengthFwd = 10
  LengthRev = 0
  Placement = pos=(65.4,44,54.82) rot=(0,0,1;0rad)
  Solid = true
  Symmetric = false
FEATURE [Part::MultiFuse] Fusion055  label="top008"
  Shapes = -> [Cut017,Cut018]
FEATURE [Part::Cut] Cut019  label="top009"
  Base = -> Fusion055
  Tool = -> Extrude020
FEATURE [App::MeasureDistance] Distance003  label="Distance: 71.95 mm"
  Distance = 71.9513
  P1 = (117,38,72)
  P2 = (117,38,0.0487319)
FEATURE [Sketcher::SketchObject] Sketch030
  FullyConstrained = true
  Placement = pos=(117,19,0) rot=(0.57735,0.57735,0.57735;2.0944rad)
  sketch-geometry (48):
    g0: LineSegment StartX=-49.19 StartY=69.25 StartZ=0 EndX=-49.19 EndY=66.25 EndZ=0
    g1: LineSegment StartX=-49.19 StartY=63.5 StartZ=0 EndX=-49.19 EndY=60.5 EndZ=0
    g2: LineSegment StartX=-49.19 StartY=57.75 StartZ=0 EndX=-49.19 EndY=54.75 EndZ=0
    g3: LineSegment StartX=-49.19 StartY=52 StartZ=0 EndX=-49.19 EndY=49 EndZ=0
    g4: LineSegment StartX=-49.19 StartY=46.25 StartZ=0 EndX=-49.19 EndY=43.25 EndZ=0
    g5: LineSegment StartX=-49.19 StartY=40.5 StartZ=0 EndX=-49.19 EndY=37.5 EndZ=0
    g6: LineSegment StartX=-49.19 StartY=34.5 StartZ=0 EndX=-49.19 EndY=31.5 EndZ=0
    g7: LineSegment StartX=-49.19 StartY=28.75 StartZ=0 EndX=-49.19 EndY=25.75 EndZ=0
    g8: LineSegment StartX=-49.19 StartY=23 StartZ=0 EndX=-49.19 EndY=20 EndZ=0
    g9: LineSegment StartX=-49.19 StartY=17.25 StartZ=0 EndX=-49.19 EndY=14.25 EndZ=0
    g10: LineSegment StartX=-49.19 StartY=11.5 StartZ=0 EndX=-49.19 EndY=8.5 EndZ=0
    g11: LineSegment StartX=-49.19 StartY=5.75 StartZ=0 EndX=-49.19 EndY=2.75 EndZ=0
    g12: ArcOfCircle CenterX=-1.5 CenterY=67.75 CenterZ=0 NormalX=0 NormalY=0 NormalZ=1 AngleXU=0 Radius=1.5 StartAngle=4.71239 EndAngle=7.85398
    g13: ArcOfCircle CenterX=-1.5 CenterY=62 CenterZ=0 NormalX=0 NormalY=0 NormalZ=1 AngleXU=0 Radius=1.5 StartAngle=4.71239 EndAngle=7.85398
    g14: ArcOfCircle CenterX=-1.5 CenterY=56.25 CenterZ=0 NormalX=0 NormalY=0 NormalZ=1 AngleXU=0 Radius=1.5 StartAngle=4.71239 EndAngle=7.85398
    g15: ArcOfCircle CenterX=-11.49 CenterY=50.5 CenterZ=0 NormalX=0 NormalY=0 NormalZ=1 AngleXU=0 Radius=1.5 StartAngle=4.71239 EndAngle=7.85398
    g16: ArcOfCircle CenterX=-16.28 CenterY=44.75 CenterZ=0 NormalX=0 NormalY=0 NormalZ=1 AngleXU=0 Radius=1.5 StartAngle=4.71239 EndAngle=7.85398
    g17: ArcOfCircle CenterX=-18.2337 CenterY=39 CenterZ=0 NormalX=0 NormalY=0 NormalZ=1 AngleXU=0 Radius=1.5 StartAngle=4.71485 EndAngle=7.85398
    g18: ArcOfCircle CenterX=-16.2837 CenterY=27.25 CenterZ=0 NormalX=0 NormalY=0 NormalZ=1 AngleXU=0 Radius=1.5 StartAngle=4.71485 EndAngle=7.85398
    g19: ArcOfCircle CenterX=-18.2337 CenterY=33 CenterZ=0 NormalX=0 NormalY=0 NormalZ=1 AngleXU=0 Radius=1.5 StartAngle=4.71485 EndAngle=7.85398
    g20: ArcOfCircle CenterX=-11.49 CenterY=21.5 CenterZ=0 NormalX=0 NormalY=0 NormalZ=1 AngleXU=0 Radius=1.5 StartAngle=4.71239 EndAngle=7.85398
    g21: ArcOfCircle CenterX=-1.5 CenterY=4.25 CenterZ=0 NormalX=0 NormalY=0 NormalZ=1 AngleXU=0 Radius=1.5 StartAngle=4.71239 EndAngle=7.85398
    g22: ArcOfCircle CenterX=-1.5 CenterY=10 CenterZ=0 NormalX=0 NormalY=0 NormalZ=1 AngleXU=0 Radius=1.5 StartAngle=4.71239 EndAngle=7.85398
    g23: ArcOfCircle CenterX=-1.5 CenterY=15.75 CenterZ=0 NormalX=0 NormalY=0 NormalZ=1 AngleXU=0 Radius=1.5 StartAngle=4.71239 EndAngle=7.85398
    g24: LineSegment StartX=-49.19 StartY=69.25 StartZ=0 EndX=-1.5 EndY=69.25 EndZ=0
    g25: LineSegment StartX=-49.19 StartY=66.25 StartZ=0 EndX=-1.5 EndY=66.25 EndZ=0
    g26: LineSegment StartX=-49.19 StartY=63.5 StartZ=0 EndX=-1.5 EndY=63.5 EndZ=0
    g27: LineSegment StartX=-49.19 StartY=60.5 StartZ=0 EndX=-1.5 EndY=60.5 EndZ=0
    g28: LineSegment StartX=-49.19 StartY=57.75 StartZ=0 EndX=-1.5 EndY=57.75 EndZ=0
    g29: LineSegment StartX=-49.19 StartY=54.75 StartZ=0 EndX=-1.5 EndY=54.75 EndZ=0
    g30: LineSegment StartX=-49.19 StartY=52 StartZ=0 EndX=-11.49 EndY=52 EndZ=0
    g31: LineSegment StartX=-49.19 StartY=49 StartZ=0 EndX=-11.49 EndY=49 EndZ=0
    g32: LineSegment StartX=-49.19 StartY=46.25 StartZ=0 EndX=-16.28 EndY=46.25 EndZ=0
    g33: LineSegment StartX=-49.19 StartY=43.25 StartZ=0 EndX=-16.28 EndY=43.25 EndZ=0
    g34: LineSegment StartX=-49.19 StartY=40.5 StartZ=0 EndX=-18.2337 EndY=40.5 EndZ=0
    g35: LineSegment StartX=-49.19 StartY=37.5 StartZ=0 EndX=-18.23 EndY=37.5 EndZ=0
    g36: LineSegment StartX=-49.19 StartY=34.5 StartZ=0 EndX=-18.2337 EndY=34.5 EndZ=0
    g37: LineSegment StartX=-49.19 StartY=31.5 StartZ=0 EndX=-18.23 EndY=31.5 EndZ=0
    g38: LineSegment StartX=-49.19 StartY=28.75 StartZ=0 EndX=-16.2837 EndY=28.75 EndZ=0
    g39: LineSegment StartX=-49.19 StartY=25.75 StartZ=0 EndX=-16.28 EndY=25.75 EndZ=0
    g40: LineSegment StartX=-49.19 StartY=23 StartZ=0 EndX=-11.49 EndY=23 EndZ=0
    g41: LineSegment StartX=-49.19 StartY=20 StartZ=0 EndX=-11.49 EndY=20 EndZ=0
    g42: LineSegment StartX=-49.19 StartY=17.25 StartZ=0 EndX=-1.5 EndY=17.25 EndZ=0
    g43: LineSegment StartX=-49.19 StartY=14.25 StartZ=0 EndX=-1.5 EndY=14.25 EndZ=0
    g44: LineSegment StartX=-49.19 StartY=11.5 StartZ=0 EndX=-1.5 EndY=11.5 EndZ=0
    g45: LineSegment StartX=-49.19 StartY=8.5 StartZ=0 EndX=-1.5 EndY=8.5 EndZ=0
    g46: LineSegment StartX=-49.19 StartY=5.75 StartZ=0 EndX=-1.5 EndY=5.75 EndZ=0
    g47: LineSegment StartX=-49.19 StartY=2.75 StartZ=0 EndX=-1.5 EndY=2.75 EndZ=0
  constraints (120):
    c: Vertical(g0)
    c: Distance(g0) = 3
    c: Block(g0)
    c: Vertical(g1)
    c: Distance(g1) = 3
    c: Vertical(g2)
    c: Equal(g0,g2) = 3
    c: Block(g2)
    c: Vertical(g3)
    c: Equal(g1,g3) = 3
    c: Vertical(g4)
    c: Equal(g0,g4) = 3
    c: Block(g4)
    c: Vertical(g5)
    c: Equal(g1,g5) = 3
    c: Vertical(g6)
    c: Equal(g0,g6) = 3
    c: Block(g6)
    c: Vertical(g7)
    c: Equal(g1,g7) = 3
    c: Vertical(g8)
    c: Equal(g0,g8) = 3
    c: Block(g8)
    c: Vertical(g9)
    c: Equal(g1,g9) = 3
    c: Vertical(g10)
    c: Equal(g0,g10) = 3
    c: Block(g10)
    c: Vertical(g11)
    c: Equal(g1,g11) = 3
    c: Block(g12)
    c: Block(g13)
    c: Block(g14)
    c: Block(g15)
    c: Block(g16)
    c: Block(g17)
    c: Block(g18)
    c: Block(g19)
    c: Block(g20)
    c: Block(g21)
    c: Block(g22)
    c: Block(g23)
    c: Block(g11)
    c: Block(g9)
    c: Block(g7)
    c: Block(g5)
    c: Block(g3)
    c: Block(g1)
    c: Coincident(g24,g0)
    c: Coincident(g24,g12)
    c: Horizontal(g24)
    c: Coincident(g25,g0)
    c: Coincident(g25,g12)
    c: Horizontal(g25)
    c: Coincident(g26,g1)
    c: Coincident(g26,g13)
    c: Horizontal(g26)
    c: Coincident(g27,g1)
    c: Coincident(g27,g13)
    c: Horizontal(g27)
    c: Coincident(g28,g2)
    c: Coincident(g28,g14)
    c: Horizontal(g28)
    c: Coincident(g29,g2)
    c: Coincident(g29,g14)
    c: Horizontal(g29)
    c: Coincident(g30,g3)
    c: Coincident(g30,g15)
    c: Horizontal(g30)
    c: Coincident(g31,g3)
    c: Coincident(g31,g15)
    c: Horizontal(g31)
    c: Coincident(g32,g4)
    c: Coincident(g32,g16)
    c: Horizontal(g32)
    c: Coincident(g33,g4)
    c: Coincident(g33,g16)
    c: Horizontal(g33)
    c: Coincident(g34,g5)
    c: Coincident(g34,g17)
    c: Horizontal(g34)
    c: Coincident(g35,g5)
    c: Coincident(g35,g17)
    c: Horizontal(g35)
    c: Coincident(g36,g6)
    c: Coincident(g36,g19)
    c: Horizontal(g36)
    c: Coincident(g37,g6)
    c: Coincident(g37,g19)
    c: Horizontal(g37)
    c: Coincident(g38,g7)
    c: Coincident(g38,g18)
    c: Horizontal(g38)
    c: Coincident(g39,g7)
    c: Coincident(g39,g18)
    c: Horizontal(g39)
    c: Coincident(g40,g8)
    c: Coincident(g40,g20)
    c: Horizontal(g40)
    c: Coincident(g41,g8)
    c: Coincident(g41,g20)
    c: Horizontal(g41)
    c: Coincident(g42,g9)
    c: Coincident(g42,g23)
    c: Horizontal(g42)
    c: Coincident(g43,g9)
    c: Coincident(g43,g23)
    c: Horizontal(g43)
    c: Coincident(g44,g10)
    c: Coincident(g44,g22)
    c: Horizontal(g44)
    c: Coincident(g45,g10)
    c: Coincident(g45,g22)
    c: Horizontal(g45)
    c: Coincident(g46,g11)
    c: Coincident(g46,g21)
    c: Horizontal(g46)
    c: Coincident(g47,g11)
    c: Coincident(g47,g21)
    c: Horizontal(g47)
FEATURE [Sketcher::SketchObject] Sketch031
  FullyConstrained = true
  Placement = pos=(117,19,0) rot=(0.57735,0.57735,0.57735;2.0944rad)
  sketch-geometry (24):
    g0: ArcOfCircle CenterX=-49.19 CenterY=67.75 CenterZ=0 NormalX=0 NormalY=0 NormalZ=1 AngleXU=0 Radius=1.5 StartAngle=1.5708 EndAngle=4.71239
    g1: ArcOfCircle CenterX=-49.19 CenterY=62 CenterZ=0 NormalX=0 NormalY=0 NormalZ=1 AngleXU=0 Radius=1.5 StartAngle=1.5708 EndAngle=4.71239
    g2: ArcOfCircle CenterX=-49.19 CenterY=56.25 CenterZ=0 NormalX=0 NormalY=0 NormalZ=1 AngleXU=0 Radius=1.5 StartAngle=1.5708 EndAngle=4.71239
    g3: ArcOfCircle CenterX=-49.19 CenterY=50.5 CenterZ=0 NormalX=0 NormalY=0 NormalZ=1 AngleXU=0 Radius=1.5 StartAngle=1.5708 EndAngle=4.71239
    g4: ArcOfCircle CenterX=-49.19 CenterY=44.75 CenterZ=0 NormalX=0 NormalY=0 NormalZ=1 AngleXU=0 Radius=1.5 StartAngle=1.5708 EndAngle=4.71239
    g5: ArcOfCircle CenterX=-49.19 CenterY=39 CenterZ=0 NormalX=0 NormalY=0 NormalZ=1 AngleXU=0 Radius=1.5 StartAngle=1.5708 EndAngle=4.71239
    g6: ArcOfCircle CenterX=-49.19 CenterY=33 CenterZ=0 NormalX=0 NormalY=0 NormalZ=1 AngleXU=0 Radius=1.5 StartAngle=1.5708 EndAngle=4.71239
    g7: ArcOfCircle CenterX=-49.19 CenterY=27.25 CenterZ=0 NormalX=0 NormalY=0 NormalZ=1 AngleXU=0 Radius=1.5 StartAngle=1.5708 EndAngle=4.71239
    g8: ArcOfCircle CenterX=-49.19 CenterY=21.5 CenterZ=0 NormalX=0 NormalY=0 NormalZ=1 AngleXU=0 Radius=1.5 StartAngle=1.5708 EndAngle=4.71239
    g9: ArcOfCircle CenterX=-49.19 CenterY=15.75 CenterZ=0 NormalX=0 NormalY=0 NormalZ=1 AngleXU=0 Radius=1.5 StartAngle=1.5708 EndAngle=4.71239
    g10: ArcOfCircle CenterX=-49.19 CenterY=10 CenterZ=0 NormalX=0 NormalY=0 NormalZ=1 AngleXU=0 Radius=1.5 StartAngle=1.5708 EndAngle=4.71239
    g11: ArcOfCircle CenterX=-49.19 CenterY=4.25 CenterZ=0 NormalX=0 NormalY=0 NormalZ=1 AngleXU=0 Radius=1.5 StartAngle=1.5708 EndAngle=4.71239
    g12: LineSegment StartX=-49.19 StartY=69.25 StartZ=0 EndX=-49.19 EndY=66.25 EndZ=0
    g13: LineSegment StartX=-49.19 StartY=63.5 StartZ=0 EndX=-49.19 EndY=60.5 EndZ=0
    g14: LineSegment StartX=-49.19 StartY=57.75 StartZ=0 EndX=-49.19 EndY=54.75 EndZ=0
    g15: LineSegment StartX=-49.19 StartY=52 StartZ=0 EndX=-49.19 EndY=49 EndZ=0
    g16: LineSegment StartX=-49.19 StartY=46.25 StartZ=0 EndX=-49.19 EndY=43.25 EndZ=0
    g17: LineSegment StartX=-49.19 StartY=40.5 StartZ=0 EndX=-49.19 EndY=37.5 EndZ=0
    g18: LineSegment StartX=-49.19 StartY=34.5 StartZ=0 EndX=-49.19 EndY=31.5 EndZ=0
    g19: LineSegment StartX=-49.19 StartY=28.75 StartZ=0 EndX=-49.19 EndY=25.75 EndZ=0
    g20: LineSegment StartX=-49.19 StartY=23 StartZ=0 EndX=-49.19 EndY=20 EndZ=0
    g21: LineSegment StartX=-49.19 StartY=17.25 StartZ=0 EndX=-49.19 EndY=14.25 EndZ=0
    g22: LineSegment StartX=-49.19 StartY=11.5 StartZ=0 EndX=-49.19 EndY=8.5 EndZ=0
    g23: LineSegment StartX=-49.19 StartY=5.75 StartZ=0 EndX=-49.19 EndY=2.75 EndZ=0
  constraints (48):
    c: Block(g0)
    c: Block(g1)
    c: Block(g2)
    c: Block(g3)
    c: Block(g4)
    c: Block(g5)
    c: Block(g6)
    c: Block(g7)
    c: Block(g8)
    c: Block(g9)
    c: Block(g10)
    c: Block(g11)
    c: Coincident(g12,g0)
    c: Coincident(g12,g0)
    c: Vertical(g12)
    c: Vertical(g13)
    c: Coincident(g13,g1)
    c: Vertical(g14)
    c: Coincident(g14,g2)
    c: Vertical(g15)
    c: Coincident(g15,g3)
    c: Vertical(g16)
    c: Coincident(g16,g4)
    c: Vertical(g17)
    c: Coincident(g17,g5)
    c: Vertical(g18)
    c: Coincident(g18,g6)
    c: Vertical(g19)
    c: Coincident(g19,g7)
    c: Vertical(g20)
    c: Coincident(g20,g8)
    c: Vertical(g21)
    c: Coincident(g21,g9)
    c: Vertical(g22)
    c: Coincident(g22,g10)
    c: Vertical(g23)
    c: Coincident(g23,g11)
    c: Block(g23)
    c: Block(g22)
    c: Block(g21)
    c: Block(g20)
    c: Block(g13)
    c: Block(g14)
    c: Block(g15)
    c: Block(g16)
    c: Block(g17)
    c: Block(g18)
    c: Block(g19)
FEATURE [Part::Extrusion] Extrude022
  Base = -> Sketch030
  Dir = (1,-2e-16,2e-16)
  DirMode = 2
  FaceMakerClass = Part::FaceMakerBullseye
  LengthFwd = 19
  LengthRev = 0
  Placement = pos=(-19,0,0) rot=(0,0,1;0rad)
  Solid = true
  Symmetric = false
FEATURE [Part::Fillet] Fillet022
  Base = -> Extrude022
  Edges = 24 edges r=1.49: [Edge6,Edge11,Edge18,Edge23,Edge30,Edge35,Edge42,Edge47,Edge54,Edge59,Edge66,Edge71,Edge78,Edge83,Edge90,Edge95,Edge102,Edge107,Edge114,Edge119,Edge126,Edge131,Edge138,Edge143]
FEATURE [Part::Cut] Cut020  label="top010"
  Base = -> Cut019
  Tool = -> Fillet022
FEATURE [Sketcher::SketchObject] Sketch032
  FullyConstrained = true
  Placement = pos=(117,19,0) rot=(0.57735,0.57735,0.57735;2.0944rad)
  sketch-geometry (48):
    g0: LineSegment StartX=-49.19 StartY=69.25 StartZ=0 EndX=-49.19 EndY=66.25 EndZ=0
    g1: LineSegment StartX=-49.19 StartY=63.5 StartZ=0 EndX=-49.19 EndY=60.5 EndZ=0
    g2: LineSegment StartX=-49.19 StartY=57.75 StartZ=0 EndX=-49.19 EndY=54.75 EndZ=0
    g3: LineSegment StartX=-49.19 StartY=52 StartZ=0 EndX=-49.19 EndY=49 EndZ=0
    g4: LineSegment StartX=-49.19 StartY=46.25 StartZ=0 EndX=-49.19 EndY=43.25 EndZ=0
    g5: LineSegment StartX=-49.19 StartY=40.5 StartZ=0 EndX=-49.19 EndY=37.5 EndZ=0
    g6: LineSegment StartX=-49.19 StartY=34.5 StartZ=0 EndX=-49.19 EndY=31.5 EndZ=0
    g7: LineSegment StartX=-49.19 StartY=28.75 StartZ=0 EndX=-49.19 EndY=25.75 EndZ=0
    g8: LineSegment StartX=-49.19 StartY=23 StartZ=0 EndX=-49.19 EndY=20 EndZ=0
    g9: LineSegment StartX=-49.19 StartY=17.25 StartZ=0 EndX=-49.19 EndY=14.25 EndZ=0
    g10: LineSegment StartX=-49.19 StartY=11.5 StartZ=0 EndX=-49.19 EndY=8.5 EndZ=0
    g11: LineSegment StartX=-49.19 StartY=5.75 StartZ=0 EndX=-49.19 EndY=2.75 EndZ=0
    g12: ArcOfCircle CenterX=-1.5 CenterY=67.75 CenterZ=0 NormalX=0 NormalY=0 NormalZ=1 AngleXU=0 Radius=1.5 StartAngle=4.71239 EndAngle=7.85398
    g13: ArcOfCircle CenterX=-1.5 CenterY=62 CenterZ=0 NormalX=0 NormalY=0 NormalZ=1 AngleXU=0 Radius=1.5 StartAngle=4.71239 EndAngle=7.85398
    g14: ArcOfCircle CenterX=-1.5 CenterY=56.25 CenterZ=0 NormalX=0 NormalY=0 NormalZ=1 AngleXU=0 Radius=1.5 StartAngle=4.71239 EndAngle=7.85398
    g15: ArcOfCircle CenterX=-11.49 CenterY=50.5 CenterZ=0 NormalX=0 NormalY=0 NormalZ=1 AngleXU=0 Radius=1.5 StartAngle=4.71239 EndAngle=7.85398
    g16: ArcOfCircle CenterX=-16.28 CenterY=44.75 CenterZ=0 NormalX=0 NormalY=0 NormalZ=1 AngleXU=0 Radius=1.5 StartAngle=4.71239 EndAngle=7.85398
    g17: ArcOfCircle CenterX=-18.2337 CenterY=39 CenterZ=0 NormalX=0 NormalY=0 NormalZ=1 AngleXU=0 Radius=1.5 StartAngle=4.71485 EndAngle=7.85398
    g18: ArcOfCircle CenterX=-16.2837 CenterY=27.25 CenterZ=0 NormalX=0 NormalY=0 NormalZ=1 AngleXU=0 Radius=1.5 StartAngle=4.71485 EndAngle=7.85398
    g19: ArcOfCircle CenterX=-18.2337 CenterY=33 CenterZ=0 NormalX=0 NormalY=0 NormalZ=1 AngleXU=0 Radius=1.5 StartAngle=4.71485 EndAngle=7.85398
    g20: ArcOfCircle CenterX=-11.49 CenterY=21.5 CenterZ=0 NormalX=0 NormalY=0 NormalZ=1 AngleXU=0 Radius=1.5 StartAngle=4.71239 EndAngle=7.85398
    g21: ArcOfCircle CenterX=-1.5 CenterY=4.25 CenterZ=0 NormalX=0 NormalY=0 NormalZ=1 AngleXU=0 Radius=1.5 StartAngle=4.71239 EndAngle=7.85398
    g22: ArcOfCircle CenterX=-1.5 CenterY=10 CenterZ=0 NormalX=0 NormalY=0 NormalZ=1 AngleXU=0 Radius=1.5 StartAngle=4.71239 EndAngle=7.85398
    g23: ArcOfCircle CenterX=-1.5 CenterY=15.75 CenterZ=0 NormalX=0 NormalY=0 NormalZ=1 AngleXU=0 Radius=1.5 StartAngle=4.71239 EndAngle=7.85398
    g24: LineSegment StartX=-49.19 StartY=69.25 StartZ=0 EndX=-1.5 EndY=69.25 EndZ=0
    g25: LineSegment StartX=-49.19 StartY=66.25 StartZ=0 EndX=-1.5 EndY=66.25 EndZ=0
    g26: LineSegment StartX=-49.19 StartY=63.5 StartZ=0 EndX=-1.5 EndY=63.5 EndZ=0
    g27: LineSegment StartX=-49.19 StartY=60.5 StartZ=0 EndX=-1.5 EndY=60.5 EndZ=0
    g28: LineSegment StartX=-49.19 StartY=57.75 StartZ=0 EndX=-1.5 EndY=57.75 EndZ=0
    g29: LineSegment StartX=-49.19 StartY=54.75 StartZ=0 EndX=-1.5 EndY=54.75 EndZ=0
    g30: LineSegment StartX=-49.19 StartY=52 StartZ=0 EndX=-11.49 EndY=52 EndZ=0
    g31: LineSegment StartX=-49.19 StartY=49 StartZ=0 EndX=-11.49 EndY=49 EndZ=0
    g32: LineSegment StartX=-49.19 StartY=46.25 StartZ=0 EndX=-16.28 EndY=46.25 EndZ=0
    g33: LineSegment StartX=-49.19 StartY=43.25 StartZ=0 EndX=-16.28 EndY=43.25 EndZ=0
    g34: LineSegment StartX=-49.19 StartY=40.5 StartZ=0 EndX=-18.2337 EndY=40.5 EndZ=0
    g35: LineSegment StartX=-49.19 StartY=37.5 StartZ=0 EndX=-18.23 EndY=37.5 EndZ=0
    g36: LineSegment StartX=-49.19 StartY=34.5 StartZ=0 EndX=-18.2337 EndY=34.5 EndZ=0
    g37: LineSegment StartX=-49.19 StartY=31.5 StartZ=0 EndX=-18.23 EndY=31.5 EndZ=0
    g38: LineSegment StartX=-49.19 StartY=28.75 StartZ=0 EndX=-16.2837 EndY=28.75 EndZ=0
    g39: LineSegment StartX=-49.19 StartY=25.75 StartZ=0 EndX=-16.28 EndY=25.75 EndZ=0
    g40: LineSegment StartX=-49.19 StartY=23 StartZ=0 EndX=-11.49 EndY=23 EndZ=0
    g41: LineSegment StartX=-49.19 StartY=20 StartZ=0 EndX=-11.49 EndY=20 EndZ=0
    g42: LineSegment StartX=-49.19 StartY=17.25 StartZ=0 EndX=-1.5 EndY=17.25 EndZ=0
    g43: LineSegment StartX=-49.19 StartY=14.25 StartZ=0 EndX=-1.5 EndY=14.25 EndZ=0
    g44: LineSegment StartX=-49.19 StartY=11.5 StartZ=0 EndX=-1.5 EndY=11.5 EndZ=0
    g45: LineSegment StartX=-49.19 StartY=8.5 StartZ=0 EndX=-1.5 EndY=8.5 EndZ=0
    g46: LineSegment StartX=-49.19 StartY=5.75 StartZ=0 EndX=-1.5 EndY=5.75 EndZ=0
    g47: LineSegment StartX=-49.19 StartY=2.75 StartZ=0 EndX=-1.5 EndY=2.75 EndZ=0
  constraints (120):
    c: Vertical(g0)
    c: Distance(g0) = 3
    c: Block(g0)
    c: Vertical(g1)
    c: Distance(g1) = 3
    c: Vertical(g2)
    c: Equal(g0,g2) = 3
    c: Block(g2)
    c: Vertical(g3)
    c: Equal(g1,g3) = 3
    c: Vertical(g4)
    c: Equal(g0,g4) = 3
    c: Block(g4)
    c: Vertical(g5)
    c: Equal(g1,g5) = 3
    c: Vertical(g6)
    c: Equal(g0,g6) = 3
    c: Block(g6)
    c: Vertical(g7)
    c: Equal(g1,g7) = 3
    c: Vertical(g8)
    c: Equal(g0,g8) = 3
    c: Block(g8)
    c: Vertical(g9)
    c: Equal(g1,g9) = 3
    c: Vertical(g10)
    c: Equal(g0,g10) = 3
    c: Block(g10)
    c: Vertical(g11)
    c: Equal(g1,g11) = 3
    c: Block(g12)
    c: Block(g13)
    c: Block(g14)
    c: Block(g15)
    c: Block(g16)
    c: Block(g17)
    c: Block(g18)
    c: Block(g19)
    c: Block(g20)
    c: Block(g21)
    c: Block(g22)
    c: Block(g23)
    c: Block(g11)
    c: Block(g9)
    c: Block(g7)
    c: Block(g5)
    c: Block(g3)
    c: Block(g1)
    c: Coincident(g24,g0)
    c: Coincident(g24,g12)
    c: Horizontal(g24)
    c: Coincident(g25,g0)
    c: Coincident(g25,g12)
    c: Horizontal(g25)
    c: Coincident(g26,g1)
    c: Coincident(g26,g13)
    c: Horizontal(g26)
    c: Coincident(g27,g1)
    c: Coincident(g27,g13)
    c: Horizontal(g27)
    c: Coincident(g28,g2)
    c: Coincident(g28,g14)
    c: Horizontal(g28)
    c: Coincident(g29,g2)
    c: Coincident(g29,g14)
    c: Horizontal(g29)
    c: Coincident(g30,g3)
    c: Coincident(g30,g15)
    c: Horizontal(g30)
    c: Coincident(g31,g3)
    c: Coincident(g31,g15)
    c: Horizontal(g31)
    c: Coincident(g32,g4)
    c: Coincident(g32,g16)
    c: Horizontal(g32)
    c: Coincident(g33,g4)
    c: Coincident(g33,g16)
    c: Horizontal(g33)
    c: Coincident(g34,g5)
    c: Coincident(g34,g17)
    c: Horizontal(g34)
    c: Coincident(g35,g5)
    c: Coincident(g35,g17)
    c: Horizontal(g35)
    c: Coincident(g36,g6)
    c: Coincident(g36,g19)
    c: Horizontal(g36)
    c: Coincident(g37,g6)
    c: Coincident(g37,g19)
    c: Horizontal(g37)
    c: Coincident(g38,g7)
    c: Coincident(g38,g18)
    c: Horizontal(g38)
    c: Coincident(g39,g7)
    c: Coincident(g39,g18)
    c: Horizontal(g39)
    c: Coincident(g40,g8)
    c: Coincident(g40,g20)
    c: Horizontal(g40)
    c: Coincident(g41,g8)
    c: Coincident(g41,g20)
    c: Horizontal(g41)
    c: Coincident(g42,g9)
    c: Coincident(g42,g23)
    c: Horizontal(g42)
    c: Coincident(g43,g9)
    c: Coincident(g43,g23)
    c: Horizontal(g43)
    c: Coincident(g44,g10)
    c: Coincident(g44,g22)
    c: Horizontal(g44)
    c: Coincident(g45,g10)
    c: Coincident(g45,g22)
    c: Horizontal(g45)
    c: Coincident(g46,g11)
    c: Coincident(g46,g21)
    c: Horizontal(g46)
    c: Coincident(g47,g11)
    c: Coincident(g47,g21)
    c: Horizontal(g47)
FEATURE [Part::Extrusion] Extrude023
  Base = -> Sketch032
  Dir = (1,-2e-16,2e-16)
  DirMode = 2
  FaceMakerClass = Part::FaceMakerBullseye
  LengthFwd = 19
  LengthRev = 0
  Placement = pos=(-19,0,0) rot=(0,0,1;0rad)
  Solid = true
  Symmetric = false
FEATURE [Part::Fillet] Fillet023
  Base = -> Extrude023
  Edges = <same value as first occurrence — deduplicated (x6 in doc)>
  Placement = pos=(0,0.05,0) rot=(0,0,1;0rad)
FEATURE [Part::Cut] Cut014  label="bottom003"
  Base = -> Cut007
  Tool = -> Fusion047
FEATURE [Part::Cut] Cut021  label="bottom004"
  Base = -> Cut014
  Tool = -> Fillet023
FEATURE [Sketcher::SketchObject] Sketch033
  FullyConstrained = true
  Placement = pos=(117,19,0) rot=(0.57735,0.57735,0.57735;2.0944rad)
  sketch-geometry (8):
    g0: LineSegment StartX=-49.19 StartY=69.25 StartZ=0 EndX=-49.19 EndY=66.25 EndZ=0
    g1: LineSegment StartX=-49.19 StartY=5.75 StartZ=0 EndX=-49.19 EndY=2.75 EndZ=0
    g2: ArcOfCircle CenterX=-1.5 CenterY=67.75 CenterZ=0 NormalX=0 NormalY=0 NormalZ=1 AngleXU=0 Radius=1.5 StartAngle=4.71239 EndAngle=7.85398
    g3: ArcOfCircle CenterX=-1.5 CenterY=4.25 CenterZ=0 NormalX=0 NormalY=0 NormalZ=1 AngleXU=0 Radius=1.5 StartAngle=4.71239 EndAngle=7.85398
    g4: LineSegment StartX=-49.19 StartY=69.25 StartZ=0 EndX=-1.5 EndY=69.25 EndZ=0
    g5: LineSegment StartX=-49.19 StartY=66.25 StartZ=0 EndX=-1.5 EndY=66.25 EndZ=0
    g6: LineSegment StartX=-49.19 StartY=5.75 StartZ=0 EndX=-1.5 EndY=5.75 EndZ=0
    g7: LineSegment StartX=-49.19 StartY=2.75 StartZ=0 EndX=-1.5 EndY=2.75 EndZ=0
  constraints (19):
    c: Vertical(g0)
    c: Distance(g0) = 3
    c: Block(g0)
    c: Vertical(g1)
    c: Block(g2)
    c: Block(g3)
    c: Block(g1)
    c: Coincident(g4,g0)
    c: Coincident(g4,g2)
    c: Horizontal(g4)
    c: Coincident(g5,g0)
    c: Coincident(g5,g2)
    c: Horizontal(g5)
    c: Coincident(g6,g1)
    c: Coincident(g6,g3)
    c: Horizontal(g6)
    c: Coincident(g7,g1)
    c: Coincident(g7,g3)
    c: Horizontal(g7)
FEATURE [Sketcher::SketchObject] Sketch034
  FullyConstrained = true
  Placement = pos=(117,19,0) rot=(0.57735,0.57735,0.57735;2.0944rad)
  sketch-geometry (8):
    g0: LineSegment StartX=-49.19 StartY=63.5 StartZ=0 EndX=-49.19 EndY=60.5 EndZ=0
    g1: LineSegment StartX=-49.19 StartY=11.5 StartZ=0 EndX=-49.19 EndY=8.5 EndZ=0
    g2: ArcOfCircle CenterX=-1.5 CenterY=62 CenterZ=0 NormalX=0 NormalY=0 NormalZ=1 AngleXU=0 Radius=1.5 StartAngle=4.71239 EndAngle=7.85398
    g3: ArcOfCircle CenterX=-1.5 CenterY=10 CenterZ=0 NormalX=0 NormalY=0 NormalZ=1 AngleXU=0 Radius=1.5 StartAngle=4.71239 EndAngle=7.85398
    g4: LineSegment StartX=-49.19 StartY=63.5 StartZ=0 EndX=-1.5 EndY=63.5 EndZ=0
    g5: LineSegment StartX=-49.19 StartY=60.5 StartZ=0 EndX=-1.5 EndY=60.5 EndZ=0
    g6: LineSegment StartX=-49.19 StartY=11.5 StartZ=0 EndX=-1.5 EndY=11.5 EndZ=0
    g7: LineSegment StartX=-49.19 StartY=8.5 StartZ=0 EndX=-1.5 EndY=8.5 EndZ=0
  constraints (19):
    c: Vertical(g0)
    c: Distance(g0) = 3
    c: Vertical(g1)
    c: Block(g1)
    c: Block(g2)
    c: Block(g3)
    c: Block(g0)
    c: Coincident(g4,g0)
    c: Coincident(g4,g2)
    c: Horizontal(g4)
    c: Coincident(g5,g0)
    c: Coincident(g5,g2)
    c: Horizontal(g5)
    c: Coincident(g6,g1)
    c: Coincident(g6,g3)
    c: Horizontal(g6)
    c: Coincident(g7,g1)
    c: Coincident(g7,g3)
    c: Horizontal(g7)
FEATURE [Part::Extrusion] Extrude024
  Base = -> Sketch033
  Dir = (1,0,0)
  DirMode = 2
  FaceMakerClass = Part::FaceMakerBullseye
  LengthFwd = 10
  LengthRev = 0
  Solid = true
  Symmetric = false
FEATURE [Part::Extrusion] Extrude025
  Base = -> Sketch034
  Dir = (1,0,0)
  DirMode = 2
  FaceMakerClass = Part::FaceMakerBullseye
  LengthFwd = 10
  LengthRev = 0
  Solid = true
  Symmetric = false
FEATURE [Part::Fillet] Fillet024  label="removeFromtMoreFrontCaseScrewRetainers"
  Base = -> Extrude024
  Edges = 4 edges r=1.49: [Edge6,Edge11,Edge18,Edge23]
  Placement = pos=(-11,0,0) rot=(0,0,1;0rad)
FEATURE [Part::Fillet] Fillet025  label="removeFromtMoreFrontCaseScrewRetainers001"
  Base = -> Extrude025
  Edges = 4 edges r=1.49: [Edge6,Edge11,Edge18,Edge23]
  Placement = pos=(-19,0,0) rot=(0,0,1;0rad)
FEATURE [Part::Cut] Cut022
  Base = -> Cut015
  Tool = -> Fillet025
FEATURE [Part::Cut] Cut023  label="screwRetainers"
  Base = -> Cut022
  Tool = -> Fillet024
FEATURE [Part::MultiFuse] Fusion056  label="bottom005"
  Shapes = -> [Fusion044,Cut021]
FEATURE [Part::MultiFuse] Fusion057  label="casePillars001"
  Shapes = -> [Cut016,Fusion052]
FEATURE [Part::MultiFuse] Fusion058  label="bottom006"
  Shapes = -> [Fusion056,Cut023]
FEATURE [Part::MultiFuse] Fusion059  label="bottom007"
  Shapes = -> [Fusion058,Fillet005]
FEATURE [Part::MultiFuse] Fusion060  label="bottom008"
  Shapes = -> [Fusion059,Fusion]
FEATURE [Part::MultiFuse] Fusion061  label="top011"
  Shapes = -> [Cut006,Cut020]
FEATURE [Part::MultiFuse] Fusion062  label="top012"
  Shapes = -> [Fusion057,Fusion061]
FEATURE [Sketcher::SketchObject] Sketch035  label="topSketch007"
  FullyConstrained = true
  sketch-geometry (6):
    g0: LineSegment StartX=19 StartY=38 StartZ=0 EndX=117 EndY=38 EndZ=0
    g1: ArcOfCircle CenterX=19 CenterY=19 CenterZ=0 NormalX=0 NormalY=0 NormalZ=1 AngleXU=0 Radius=19 StartAngle=1.5708 EndAngle=3.14159
    g2: LineSegment StartX=117 StartY=38 StartZ=0 EndX=117 EndY=19 EndZ=0
    g3: LineSegment StartX=98 StartY=1.0161e-12 StartZ=0 EndX=5.22862e-06 EndY=1.0161e-12 EndZ=0
    g4: LineSegment StartX=5.22862e-06 StartY=19 StartZ=0 EndX=5.22862e-06 EndY=1.0161e-12 EndZ=0
    g5: ArcOfCircle CenterX=98 CenterY=19 CenterZ=0 NormalX=0 NormalY=0 NormalZ=1 AngleXU=0 Radius=19 StartAngle=4.71239 EndAngle=6.28319
  constraints (16):
    c: Horizontal(g0)
    c: Distance(g0) = 98
    c: Coincident(g1,g0)
    c: Block(g1)
    c: Coincident(g2,g0)
    c: Vertical(g2)
    c: Distance(g2) = 19
    c: Horizontal(g3)
    c: Coincident(g4,g1)
    c: Vertical(g4)
    c: Coincident(g3,g4)
    c: Block(g3)
    c: Coincident(g5,g2)
    c: Coincident(g5,g3)
    c: Block(g0)
    c: Block(g5)
FEATURE [Part::Extrusion] Extrude026  label="sideA001"
  Base = -> Sketch035
  Dir = (0,0,1)
  DirMode = 2
  FaceMakerClass = Part::FaceMakerBullseye
  LengthFwd = 3
  LengthRev = 0
  Placement = pos=(0,0,-2.7) rot=(0,0,1;0rad)
  Solid = true
  Symmetric = false
FEATURE [Sketcher::SketchObject] Sketch036  label="topSketch008"
  FullyConstrained = true
  sketch-geometry (6):
    g0: LineSegment StartX=19 StartY=38 StartZ=0 EndX=117 EndY=38 EndZ=0
    g1: ArcOfCircle CenterX=19 CenterY=19 CenterZ=0 NormalX=0 NormalY=0 NormalZ=1 AngleXU=0 Radius=19 StartAngle=1.5708 EndAngle=3.14159
    g2: LineSegment StartX=117 StartY=38 StartZ=0 EndX=117 EndY=19 EndZ=0
    g3: LineSegment StartX=98 StartY=1.0161e-12 StartZ=0 EndX=5.22862e-06 EndY=1.0161e-12 EndZ=0
    g4: LineSegment StartX=5.22862e-06 StartY=19 StartZ=0 EndX=5.22862e-06 EndY=1.0161e-12 EndZ=0
    g5: ArcOfCircle CenterX=98 CenterY=19 CenterZ=0 NormalX=0 NormalY=0 NormalZ=1 AngleXU=0 Radius=19 StartAngle=4.71239 EndAngle=6.28319
  constraints (16):
    c: Horizontal(g0)
    c: Distance(g0) = 98
    c: Coincident(g1,g0)
    c: Block(g1)
    c: Coincident(g2,g0)
    c: Vertical(g2)
    c: Distance(g2) = 19
    c: Horizontal(g3)
    c: Coincident(g4,g1)
    c: Vertical(g4)
    c: Coincident(g3,g4)
    c: Block(g3)
    c: Coincident(g5,g2)
    c: Coincident(g5,g3)
    c: Block(g0)
    c: Block(g5)
FEATURE [Part::Extrusion] Extrude027  label="sideB001"
  Base = -> Sketch036
  Dir = (0,0,1)
  DirMode = 2
  FaceMakerClass = Part::FaceMakerBullseye
  LengthFwd = 3
  LengthRev = 0
  Placement = pos=(0,0,71.7) rot=(0,0,1;0rad)
  Solid = true
  Symmetric = false
FEATURE [Part::MultiFuse] Fusion064  label="removeFromBottom"
  Shapes = -> [Extrude026,Extrude027]
FEATURE [Part::Cut] Cut024  label="bottom009"
  Base = -> Fusion060
  Tool = -> Fusion064
FEATURE [Sketcher::SketchObject] Sketch037  label="topSketch009"
  FullyConstrained = true
  sketch-geometry (6):
    g0: ArcOfCircle CenterX=19 CenterY=19 CenterZ=0 NormalX=0 NormalY=0 NormalZ=1 AngleXU=0 Radius=19 StartAngle=1.5708 EndAngle=3.14159
    g1: LineSegment StartX=5.22862e-06 StartY=19 StartZ=0 EndX=5.22862e-06 EndY=1.19904e-11 EndZ=0
    g2: LineSegment StartX=19 StartY=38 StartZ=0 EndX=124 EndY=38 EndZ=0
    g3: LineSegment StartX=5.22862e-06 StartY=1.19904e-11 StartZ=0 EndX=105 EndY=1.19904e-11 EndZ=0
    g4: ArcOfCircle CenterX=105 CenterY=19 CenterZ=0 NormalX=0 NormalY=0 NormalZ=1 AngleXU=0 Radius=19 StartAngle=4.71239 EndAngle=6.28319
    g5: LineSegment StartX=124 StartY=38 StartZ=0 EndX=124 EndY=19 EndZ=0
  constraints (16):
    c: Block(g0)
    c: Coincident(g1,g0)
    c: Vertical(g1)
    c: Horizontal(g2)
    c: Distance(g2) = 105
    c: Coincident(g2,g0)
    c: Distance(g1) = 19
    c: Coincident(g3,g1)
    c: Horizontal(g3)
    c: Distance(g3) = 105
    c: Block(g4)
    c: Coincident(g4,g3)
    c: Coincident(g5,g2)
    c: Coincident(g5,g4)
    c: Vertical(g5)
    c: Distance(g5) = 19
FEATURE [Part::Extrusion] Extrude028  label="sideB"
  Base = -> Sketch037
  Dir = (0,0,1)
  DirMode = 2
  FaceMakerClass = Part::FaceMakerBullseye
  LengthFwd = 3
  LengthRev = 0
  Placement = pos=(0,0,72) rot=(0,0,1;0rad)
  Solid = true
  Symmetric = false
FEATURE [Sketcher::SketchObject] Sketch038  label="topSketch010"
  FullyConstrained = true
  sketch-geometry (22):
    g0: LineSegment StartX=5.21097e-06 StartY=3 StartZ=0 EndX=5.21097e-06 EndY=19 EndZ=0
    g1: ArcOfCircle CenterX=19 CenterY=19 CenterZ=0 NormalX=0 NormalY=0 NormalZ=1 AngleXU=0 Radius=19 StartAngle=1.5708 EndAngle=3.14159
    g2: ArcOfCircle CenterX=19 CenterY=19 CenterZ=0 NormalX=0 NormalY=0 NormalZ=1 AngleXU=0 Radius=16 StartAngle=1.5708 EndAngle=3.14159
    g3: LineSegment StartX=114 StartY=35 StartZ=0 EndX=19 EndY=35 EndZ=0
    g4: LineSegment StartX=5.21097e-06 StartY=3 StartZ=0 EndX=5.21097e-06 EndY=0 EndZ=0
    g5: LineSegment StartX=3 StartY=0 StartZ=0 EndX=5.21097e-06 EndY=0 EndZ=0
    g6: LineSegment StartX=3 StartY=19 StartZ=0 EndX=3 EndY=0 EndZ=0
    g7: LineSegment StartX=19 StartY=38 StartZ=0 EndX=124 EndY=38 EndZ=0
    g8: Circle CenterX=119 CenterY=35 CenterZ=0 NormalX=0 NormalY=0 NormalZ=1 AngleXU=0 Radius=1
    g9: Circle CenterX=121 CenterY=35 CenterZ=0 NormalX=0 NormalY=0 NormalZ=1 AngleXU=0 Radius=1
    g10: Circle CenterX=121 CenterY=33 CenterZ=0 NormalX=0 NormalY=0 NormalZ=1 AngleXU=0 Radius=1
    g11: BSplineCurve PolesCount=3 KnotsCount=2 Degree=2 IsPeriodic=0
    g12: GeomPoint X=119 Y=35 Z=0
    g13: GeomPoint X=121 Y=33 Z=0
    g14: LineSegment StartX=119 StartY=35 StartZ=0 EndX=114 EndY=35 EndZ=0
    g15: ArcOfCircle CenterX=105 CenterY=19 CenterZ=0 NormalX=0 NormalY=0 NormalZ=1 AngleXU=0 Radius=16 StartAngle=5.60905 EndAngle=6.28319
    g16: LineSegment StartX=121 StartY=33 StartZ=0 EndX=121 EndY=19 EndZ=0
    g17: LineSegment StartX=117.5 StartY=9.01251 StartZ=0 EndX=121.163 EndY=9.0125 EndZ=0
    g18: ArcOfCircle CenterX=105 CenterY=19 CenterZ=0 NormalX=0 NormalY=0 NormalZ=1 AngleXU=0 Radius=20.6155 StartAngle=5.7297 EndAngle=6.28319
    g19: LineSegment StartX=121.163 StartY=9.0125 StartZ=0 EndX=122.538 EndY=8.16329 EndZ=0
    g20: LineSegment StartX=124 StartY=38 StartZ=0 EndX=125.616 EndY=38 EndZ=0
    g21: LineSegment StartX=125.616 StartY=19 StartZ=0 EndX=125.616 EndY=38 EndZ=0
  constraints (49):
    c: Vertical(g0)
    c: Block(g0)
    c: Coincident(g1,g0)
    c: Block(g1)
    c: Coincident(g2,g1)
    c: Block(g2)
    c: Coincident(g3,g2)
    c: Horizontal(g3)
    c: Tangent(g3,g2)
    c: Coincident(g4,g0)
    c: Distance(g4) = 3
    c: Vertical(g4)
    c: Coincident(g5,g4)
    c: Horizontal(g5)
    c: Coincident(g6,g2)
    c: Coincident(g6,g5)
    c: Vertical(g6)
    c: Horizontal(g7)
    c: Distance(g7) = 105
    c: Coincident(g7,g1)
    c: Block(g3)
    c: Weight(g8) = 1
    c: Equal(g8,g9)
    c: Equal(g8,g10)
    c: InternalAlignment(g8,g11)
    c: InternalAlignment(g9,g11)
    c: InternalAlignment(g10,g11)
    c: InternalAlignment(g12,g11)
    c: InternalAlignment(g13,g11)
    c: Block(g11)
    c: Coincident(g14,g11)
    c: Coincident(g14,g3)
    c: Horizontal(g14)
    c: Block(g15)
    c: Coincident(g16,g11)
    c: Coincident(g16,g15)
    c: Vertical(g16)
    c: Distance(g16) = 14
    c: Coincident(g17,g15)
    c: Block(g18)
    c: Coincident(g19,g18)
    c: Coincident(g20,g7)
    c: Horizontal(g20)
    c: Vertical(g21)
    c: Coincident(g20,g21)
    c: Block(g20)
    c: Block(g21)
    c: Block(g19)
    c: Block(g17)
FEATURE [Part::Extrusion] Extrude029
  Base = -> Sketch038
  Dir = (0,0,1)
  DirMode = 2
  FaceMakerClass = Part::FaceMakerBullseye
  LengthFwd = 72
  LengthRev = 0
  Solid = true
  Symmetric = false
FEATURE [Part::Feature] Face085
  shape: bbox 4.8 x 25.5 x 2e-07 mm, 1 faces, 0 solids (baked)
FEATURE [Part::Revolution] Revolve089  label="moreFrontCaseScrewPost003"
  Angle = 360
  Axis = (0,1,0)
  Base = (0,0,0)
  FaceMakerClass = Part::FaceMakerBullseye
  Placement = pos=(109.5,4.5,3.5) rot=(0,0,1;0rad)
  Solid = false
  Source = -> Face085
  Symmetric = false
FEATURE [Part::Feature] Face086
  shape: bbox 4.8 x 25.5 x 2e-07 mm, 1 faces, 0 solids (baked)
FEATURE [Part::Revolution] Revolve090  label="moreFrontCaseScrewPost004"
  Angle = 360
  Axis = (0,1,0)
  Base = (0,0,0)
  FaceMakerClass = Part::FaceMakerBullseye
  Placement = pos=(109.5,4.5,68.5) rot=(0,0,1;0rad)
  Solid = false
  Source = -> Face086
  Symmetric = false
FEATURE [Part::Fillet] Fillet026  label="top013"
  Base = -> Extrude029
  Edges = 1 edges r=2: [Edge35]
FEATURE [Sketcher::SketchObject] Sketch039
  FullyConstrained = true
  sketch-geometry (7):
    g0: LineSegment StartX=0 StartY=0 StartZ=0 EndX=0 EndY=6 EndZ=0
    g1: Circle CenterX=0 CenterY=0 CenterZ=0 NormalX=0 NormalY=0 NormalZ=1 AngleXU=0 Radius=1
    g2: Circle CenterX=8 CenterY=6 CenterZ=0 NormalX=0 NormalY=0 NormalZ=1 AngleXU=0 Radius=1
    g3: BSplineCurve PolesCount=3 KnotsCount=2 Degree=2 IsPeriodic=0
    g4: GeomPoint X=0 Y=0 Z=0
    g5: GeomPoint X=8 Y=6 Z=0
    g6: LineSegment StartX=0 StartY=6 StartZ=0 EndX=8 EndY=6 EndZ=0
  constraints (14):
    c: Coincident(g0,g-1)
    c: Distance(g0) = 6
    c: Vertical(g0)
    c: Coincident(g3,g0)
    c: Weight(g1) = 1
    c: Equal(g1,g2)
    c: InternalAlignment(g1,g3)
    c: InternalAlignment(g2,g3)
    c: InternalAlignment(g4,g3)
    c: InternalAlignment(g5,g3)
    c: Block(g3)
    c: Coincident(g6,g0)
    c: Coincident(g6,g3)
    c: Horizontal(g6)
FEATURE [Sketcher::SketchObject] Sketch040
  FullyConstrained = true
  sketch-geometry (7):
    g0: LineSegment StartX=0 StartY=0 StartZ=0 EndX=0 EndY=6 EndZ=0
    g1: Circle CenterX=0 CenterY=0 CenterZ=0 NormalX=0 NormalY=0 NormalZ=1 AngleXU=0 Radius=1
    g2: Circle CenterX=8 CenterY=6 CenterZ=0 NormalX=0 NormalY=0 NormalZ=1 AngleXU=0 Radius=1
    g3: BSplineCurve PolesCount=3 KnotsCount=2 Degree=2 IsPeriodic=0
    g4: GeomPoint X=0 Y=0 Z=0
    g5: GeomPoint X=8 Y=6 Z=0
    g6: LineSegment StartX=0 StartY=6 StartZ=0 EndX=8 EndY=6 EndZ=0
  constraints (14):
    c: Coincident(g0,g-1)
    c: Distance(g0) = 6
    c: Vertical(g0)
    c: Coincident(g3,g0)
    c: Weight(g1) = 1
    c: Equal(g1,g2)
    c: InternalAlignment(g1,g3)
    c: InternalAlignment(g2,g3)
    c: InternalAlignment(g4,g3)
    c: InternalAlignment(g5,g3)
    c: Block(g3)
    c: Coincident(g6,g0)
    c: Coincident(g6,g3)
    c: Horizontal(g6)
FEATURE [Sketcher::SketchObject] Sketch041
  FullyConstrained = true
  sketch-geometry (7):
    g0: LineSegment StartX=0 StartY=0 StartZ=0 EndX=0 EndY=6 EndZ=0
    g1: Circle CenterX=0 CenterY=0 CenterZ=0 NormalX=0 NormalY=0 NormalZ=1 AngleXU=0 Radius=1
    g2: Circle CenterX=8 CenterY=6 CenterZ=0 NormalX=0 NormalY=0 NormalZ=1 AngleXU=0 Radius=1
    g3: BSplineCurve PolesCount=3 KnotsCount=2 Degree=2 IsPeriodic=0
    g4: GeomPoint X=0 Y=0 Z=0
    g5: GeomPoint X=8 Y=6 Z=0
    g6: LineSegment StartX=0 StartY=6 StartZ=0 EndX=8 EndY=6 EndZ=0
  constraints (14):
    c: Coincident(g0,g-1)
    c: Distance(g0) = 6
    c: Vertical(g0)
    c: Coincident(g3,g0)
    c: Weight(g1) = 1
    c: Equal(g1,g2)
    c: InternalAlignment(g1,g3)
    c: InternalAlignment(g2,g3)
    c: InternalAlignment(g4,g3)
    c: InternalAlignment(g5,g3)
    c: Block(g3)
    c: Coincident(g6,g0)
    c: Coincident(g6,g3)
    c: Horizontal(g6)
FEATURE [Sketcher::SketchObject] Sketch042
  FullyConstrained = true
  sketch-geometry (7):
    g0: LineSegment StartX=0 StartY=0 StartZ=0 EndX=0 EndY=6 EndZ=0
    g1: Circle CenterX=0 CenterY=0 CenterZ=0 NormalX=0 NormalY=0 NormalZ=1 AngleXU=0 Radius=1
    g2: Circle CenterX=8 CenterY=6 CenterZ=0 NormalX=0 NormalY=0 NormalZ=1 AngleXU=0 Radius=1
    g3: BSplineCurve PolesCount=3 KnotsCount=2 Degree=2 IsPeriodic=0
    g4: GeomPoint X=0 Y=0 Z=0
    g5: GeomPoint X=8 Y=6 Z=0
    g6: LineSegment StartX=0 StartY=6 StartZ=0 EndX=8 EndY=6 EndZ=0
  constraints (14):
    c: Coincident(g0,g-1)
    c: Distance(g0) = 6
    c: Vertical(g0)
    c: Coincident(g3,g0)
    c: Weight(g1) = 1
    c: Equal(g1,g2)
    c: InternalAlignment(g1,g3)
    c: InternalAlignment(g2,g3)
    c: InternalAlignment(g4,g3)
    c: InternalAlignment(g5,g3)
    c: Block(g3)
    c: Coincident(g6,g0)
    c: Coincident(g6,g3)
    c: Horizontal(g6)
FEATURE [Part::Extrusion] Extrude030  label="caseScrewPillarBracket008"
  Base = -> Sketch039
  Dir = (0,0,1)
  DirMode = 2
  FaceMakerClass = Part::FaceMakerBullseye
  LengthFwd = 2.4
  LengthRev = 0
  Placement = pos=(15.76,29,8.8) rot=(0,1,0;0rad)
  Solid = true
  Symmetric = false
FEATURE [Part::Extrusion] Extrude031  label="caseScrewPillarBracket009"
  Base = -> Sketch040
  Dir = (0,0,1)
  DirMode = 2
  FaceMakerClass = Part::FaceMakerBullseye
  LengthFwd = 2.4
  LengthRev = 0
  Placement = pos=(15.76,29,60.8) rot=(0,0,1;0rad)
  Solid = true
  Symmetric = false
FEATURE [Part::Extrusion] Extrude032  label="caseScrewPillarBracket010"
  Base = -> Sketch041
  Dir = (0,0,1)
  DirMode = 2
  FaceMakerClass = Part::FaceMakerBullseye
  LengthFwd = 2.4
  LengthRev = 0
  Placement = pos=(13.7,29,13.26) rot=(0,-1,0;1.5708rad)
  Solid = true
  Symmetric = false
FEATURE [Part::Extrusion] Extrude033  label="caseScrewPillarBracket011"
  Base = -> Sketch042
  Dir = (0,0,1)
  DirMode = 2
  FaceMakerClass = Part::FaceMakerBullseye
  LengthFwd = 2.4
  LengthRev = 0
  Placement = pos=(11.3,29,58.74) rot=(0,1,0;1.5708rad)
  Solid = true
  Symmetric = false
FEATURE [Sketcher::SketchObject] Sketch043
  FullyConstrained = true
  sketch-geometry (7):
    g0: LineSegment StartX=0 StartY=0 StartZ=0 EndX=0 EndY=6 EndZ=0
    g1: Circle CenterX=0 CenterY=0 CenterZ=0 NormalX=0 NormalY=0 NormalZ=1 AngleXU=0 Radius=1
    g2: Circle CenterX=8 CenterY=6 CenterZ=0 NormalX=0 NormalY=0 NormalZ=1 AngleXU=0 Radius=1
    g3: BSplineCurve PolesCount=3 KnotsCount=2 Degree=2 IsPeriodic=0
    g4: GeomPoint X=0 Y=0 Z=0
    g5: GeomPoint X=8 Y=6 Z=0
    g6: LineSegment StartX=0 StartY=6 StartZ=0 EndX=8 EndY=6 EndZ=0
  constraints (14):
    c: Coincident(g0,g-1)
    c: Distance(g0) = 6
    c: Vertical(g0)
    c: Coincident(g3,g0)
    c: Weight(g1) = 1
    c: Equal(g1,g2)
    c: InternalAlignment(g1,g3)
    c: InternalAlignment(g2,g3)
    c: InternalAlignment(g4,g3)
    c: InternalAlignment(g5,g3)
    c: Block(g3)
    c: Coincident(g6,g0)
    c: Coincident(g6,g3)
    c: Horizontal(g6)
FEATURE [Part::Extrusion] Extrude034  label="caseScrewPillarBracket012"
  Base = -> Sketch043
  Dir = (0,0,1)
  DirMode = 2
  FaceMakerClass = Part::FaceMakerBullseye
  LengthFwd = 2.4
  LengthRev = 0
  Placement = pos=(88.3,29,65.23) rot=(0,1,0;1.5708rad)
  Solid = true
  Symmetric = false
FEATURE [Sketcher::SketchObject] Sketch044
  FullyConstrained = true
  sketch-geometry (7):
    g0: LineSegment StartX=0 StartY=0 StartZ=0 EndX=0 EndY=6 EndZ=0
    g1: Circle CenterX=0 CenterY=0 CenterZ=0 NormalX=0 NormalY=0 NormalZ=1 AngleXU=0 Radius=1
    g2: Circle CenterX=8 CenterY=6 CenterZ=0 NormalX=0 NormalY=0 NormalZ=1 AngleXU=0 Radius=1
    g3: BSplineCurve PolesCount=3 KnotsCount=2 Degree=2 IsPeriodic=0
    g4: GeomPoint X=0 Y=0 Z=0
    g5: GeomPoint X=8 Y=6 Z=0
    g6: LineSegment StartX=0 StartY=6 StartZ=0 EndX=8 EndY=6 EndZ=0
  constraints (14):
    c: Coincident(g0,g-1)
    c: Distance(g0) = 6
    c: Vertical(g0)
    c: Coincident(g3,g0)
    c: Weight(g1) = 1
    c: Equal(g1,g2)
    c: InternalAlignment(g1,g3)
    c: InternalAlignment(g2,g3)
    c: InternalAlignment(g4,g3)
    c: InternalAlignment(g5,g3)
    c: Block(g3)
    c: Coincident(g6,g0)
    c: Coincident(g6,g3)
    c: Horizontal(g6)
FEATURE [Part::Extrusion] Extrude035  label="caseScrewPillarBracket013"
  Base = -> Sketch044
  Dir = (0,0,1)
  DirMode = 2
  FaceMakerClass = Part::FaceMakerBullseye
  LengthFwd = 2.4
  LengthRev = 0
  Placement = pos=(90.7,29,6.77) rot=(0,-1,0;1.5708rad)
  Solid = true
  Symmetric = false
FEATURE [Sketcher::SketchObject] Sketch045
  FullyConstrained = true
  sketch-geometry (7):
    g0: LineSegment StartX=0 StartY=0 StartZ=0 EndX=0 EndY=6 EndZ=0
    g1: Circle CenterX=0 CenterY=0 CenterZ=0 NormalX=0 NormalY=0 NormalZ=1 AngleXU=0 Radius=1
    g2: Circle CenterX=8 CenterY=6 CenterZ=0 NormalX=0 NormalY=0 NormalZ=1 AngleXU=0 Radius=1
    g3: BSplineCurve PolesCount=3 KnotsCount=2 Degree=2 IsPeriodic=0
    g4: GeomPoint X=0 Y=0 Z=0
    g5: GeomPoint X=8 Y=6 Z=0
    g6: LineSegment StartX=0 StartY=6 StartZ=0 EndX=8 EndY=6 EndZ=0
  constraints (14):
    c: Coincident(g0,g-1)
    c: Distance(g0) = 6
    c: Vertical(g0)
    c: Coincident(g3,g0)
    c: Weight(g1) = 1
    c: Equal(g1,g2)
    c: InternalAlignment(g1,g3)
    c: InternalAlignment(g2,g3)
    c: InternalAlignment(g4,g3)
    c: InternalAlignment(g5,g3)
    c: Block(g3)
    c: Coincident(g6,g0)
    c: Coincident(g6,g3)
    c: Horizontal(g6)
FEATURE [Sketcher::SketchObject] Sketch046
  FullyConstrained = true
  sketch-geometry (7):
    g0: LineSegment StartX=0 StartY=0 StartZ=0 EndX=0 EndY=6 EndZ=0
    g1: Circle CenterX=0 CenterY=0 CenterZ=0 NormalX=0 NormalY=0 NormalZ=1 AngleXU=0 Radius=1
    g2: Circle CenterX=8 CenterY=6 CenterZ=0 NormalX=0 NormalY=0 NormalZ=1 AngleXU=0 Radius=1
    g3: BSplineCurve PolesCount=3 KnotsCount=2 Degree=2 IsPeriodic=0
    g4: GeomPoint X=0 Y=0 Z=0
    g5: GeomPoint X=8 Y=6 Z=0
    g6: LineSegment StartX=0 StartY=6 StartZ=0 EndX=8 EndY=6 EndZ=0
  constraints (14):
    c: Coincident(g0,g-1)
    c: Distance(g0) = 6
    c: Vertical(g0)
    c: Coincident(g3,g0)
    c: Weight(g1) = 1
    c: Equal(g1,g2)
    c: InternalAlignment(g1,g3)
    c: InternalAlignment(g2,g3)
    c: InternalAlignment(g4,g3)
    c: InternalAlignment(g5,g3)
    c: Block(g3)
    c: Coincident(g6,g0)
    c: Coincident(g6,g3)
    c: Horizontal(g6)
FEATURE [Part::Extrusion] Extrude036  label="caseScrewPillarBracket014"
  Base = -> Sketch045
  Dir = (0,0,1)
  DirMode = 2
  FaceMakerClass = Part::FaceMakerBullseye
  LengthFwd = 2.4
  LengthRev = 0
  Placement = pos=(110.7,29,6.77) rot=(0,-1,0;1.5708rad)
  Solid = true
  Symmetric = false
FEATURE [Part::Extrusion] Extrude037  label="caseScrewPillarBracket015"
  Base = -> Sketch046
  Dir = (0,0,1)
  DirMode = 2
  FaceMakerClass = Part::FaceMakerBullseye
  LengthFwd = 2.4
  LengthRev = 0
  Placement = pos=(108.3,29,65.23) rot=(0,1,0;1.5708rad)
  Solid = true
  Symmetric = false
FEATURE [Part::Box] Box013  label="frontCaseScrewPillarBracket002"
  AttacherType = Attacher::AttachEngine3D
  Height = 2.4
  Length = 22
  Placement = pos=(87,28,2.3) rot=(0,0,1;0rad)
  Width = 7
FEATURE [Part::Box] Box014  label="frontCaseScrewPillarBracket003"
  AttacherType = Attacher::AttachEngine3D
  Height = 2.4
  Length = 22
  Placement = pos=(87,28,67.3) rot=(0,0,1;0rad)
  Width = 7
FEATURE [Part::Feature] Face087
  shape: bbox 4.8 x 30.2 x 2e-07 mm, 1 faces, 0 solids (baked)
FEATURE [Part::Revolution] Revolve091  label="frontCaseScrewPost004"
  Angle = 360
  Axis = (0,1,0)
  Base = (0,0,0)
  FaceMakerClass = Part::FaceMakerBullseye
  Placement = pos=(89.5,4.5,3.5) rot=(0,0,1;0rad)
  Solid = false
  Source = -> Face087
  Symmetric = false
FEATURE [Part::Feature] Face088
  shape: bbox 4.8 x 30.2 x 2e-07 mm, 1 faces, 0 solids (baked)
FEATURE [Part::Revolution] Revolve092  label="frontCaseScrewPost005"
  Angle = 360
  Axis = (0,1,0)
  Base = (0,0,0)
  FaceMakerClass = Part::FaceMakerBullseye
  Placement = pos=(89.5,4.5,68.5) rot=(0,0,1;0rad)
  Solid = false
  Source = -> Face088
  Symmetric = false
FEATURE [Part::Feature] Face089
  shape: bbox 3.5 x 30.2 x 2e-07 mm, 1 faces, 0 solids (baked)
FEATURE [Part::Revolution] Revolve093  label="backCaseScrewPost002"
  Angle = 360
  Axis = (0,1,0)
  Base = (0,0,0)
  FaceMakerClass = Part::FaceMakerBullseye
  Placement = pos=(12.5,4.5,10) rot=(0,0,1;0rad)
  Solid = false
  Source = -> Face089
  Symmetric = false
FEATURE [Part::Feature] Face090
  shape: bbox 3.5 x 30.2 x 2e-07 mm, 1 faces, 0 solids (baked)
FEATURE [Part::Revolution] Revolve094  label="backCaseScrewPost003"
  Angle = 360
  Axis = (0,1,0)
  Base = (0,0,0)
  FaceMakerClass = Part::FaceMakerBullseye
  Placement = pos=(12.5,4.5,62) rot=(0,0,1;0rad)
  Solid = false
  Source = -> Face090
  Symmetric = false
FEATURE [Part::Box] Box015  label="Cube011"
  AttacherType = Attacher::AttachEngine3D
  Height = 28.8
  Length = 3
  Placement = pos=(107.3,28,21.6) rot=(0,0,1;0rad)
  Width = 7
FEATURE [Part::Box] Box016  label="Cube012"
  AttacherType = Attacher::AttachEngine3D
  Height = 3
  Length = 7.4
  Placement = pos=(107.3,28,18.6) rot=(0,0,1;0rad)
  Width = 7
FEATURE [Part::Box] Box017  label="Cube013"
  AttacherType = Attacher::AttachEngine3D
  Height = 3
  Length = 7.4
  Placement = pos=(107.3,28,50.4) rot=(0,0,1;0rad)
  Width = 7
FEATURE [Part::Cylinder] Cylinder024
  Angle = 360
  AttacherType = Attacher::AttachEngine3D
  Height = 20
  Placement = pos=(0,0,36.15) rot=(0,0,1;0rad)
  Radius = 14.3
FEATURE [Part::Cylinder] Cylinder025
  Angle = 360
  AttacherType = Attacher::AttachEngine3D
  Height = 10
  Placement = pos=(0,0,36.15) rot=(0,0,1;0rad)
  Radius = 4
FEATURE [Part::MultiFuse] Fusion066  label="removeToCreteHoleForPlugHousing009"
  Placement = pos=(70,19,36) rot=(0,1,0;1.5708rad)
  Shapes = -> [Cylinder024,Cylinder025]
FEATURE [Part::MultiFuse] Fusion065  label="plugHousingBracketHolder002"
  Shapes = -> [Box017,Box015,Box016]
FEATURE [Part::Cut] Cut025  label="plugHousingBracketHolder003"
  Base = -> Fusion065
  Placement = pos=(7,0,0) rot=(0,0,1;0rad)
  Tool = -> Fusion066
FEATURE [Sketcher::SketchObject] Sketch047
  FullyConstrained = false
  Placement = pos=(0,0,0) rot=(1,0,0;1.5708rad)
  sketch-geometry (24):
    g0: ArcOfCircle CenterX=-4 CenterY=-10.5 CenterZ=0 NormalX=0 NormalY=0 NormalZ=1 AngleXU=0 Radius=1.5 StartAngle=6e-16 EndAngle=3.14159
    g1: ArcOfCircle CenterX=-34.2 CenterY=-10.5 CenterZ=0 NormalX=0 NormalY=0 NormalZ=1 AngleXU=0 Radius=1.5 StartAngle=0 EndAngle=3.14159
    g2: ArcOfCircle CenterX=-34.2 CenterY=-27.7 CenterZ=0 NormalX=0 NormalY=0 NormalZ=1 AngleXU=0 Radius=1.5 StartAngle=3.14159 EndAngle=6.28319
    g3: ArcOfCircle CenterX=-4 CenterY=-27.7 CenterZ=0 NormalX=0 NormalY=0 NormalZ=1 AngleXU=0 Radius=1.5 StartAngle=3.1416 EndAngle=6.28319
    g4: ArcOfCircle CenterX=-10 CenterY=-4.3 CenterZ=0 NormalX=0 NormalY=0 NormalZ=1 AngleXU=0 Radius=1.5 StartAngle=2e-16 EndAngle=3.14159
    g5: ArcOfCircle CenterX=-16.1 CenterY=-1.8 CenterZ=0 NormalX=0 NormalY=0 NormalZ=1 AngleXU=0 Radius=1.5 StartAngle=5e-16 EndAngle=3.14159
    g6: ArcOfCircle CenterX=-22.1 CenterY=-1.8 CenterZ=0 NormalX=0 NormalY=0 NormalZ=1 AngleXU=0 Radius=1.5 StartAngle=5e-16 EndAngle=3.14159
    g7: ArcOfCircle CenterX=-28.2 CenterY=-4.3 CenterZ=0 NormalX=0 NormalY=0 NormalZ=1 AngleXU=0 Radius=1.5 StartAngle=2e-16 EndAngle=3.14159
    g8: ArcOfCircle CenterX=-10 CenterY=-33.9 CenterZ=0 NormalX=0 NormalY=0 NormalZ=1 AngleXU=0 Radius=1.5 StartAngle=3.14159 EndAngle=6.28319
    g9: ArcOfCircle CenterX=-16.1 CenterY=-36.4 CenterZ=0 NormalX=0 NormalY=0 NormalZ=1 AngleXU=0 Radius=1.5 StartAngle=3.14159 EndAngle=6.28319
    g10: ArcOfCircle CenterX=-22.1 CenterY=-36.4 CenterZ=0 NormalX=0 NormalY=0 NormalZ=1 AngleXU=0 Radius=1.5 StartAngle=3.14159 EndAngle=6.28319
    g11: ArcOfCircle CenterX=-28.2 CenterY=-33.9 CenterZ=0 NormalX=0 NormalY=0 NormalZ=1 AngleXU=0 Radius=1.5 StartAngle=3.14159 EndAngle=6.28319
    g12: LineSegment StartX=-35.7 StartY=-10.5 StartZ=0 EndX=-35.7 EndY=-27.7 EndZ=0
    g13: LineSegment StartX=-32.7 StartY=-10.5 StartZ=0 EndX=-32.7 EndY=-27.7 EndZ=0
    g14: LineSegment StartX=-29.7 StartY=-33.9 StartZ=0 EndX=-29.7 EndY=-4.3 EndZ=0
    g15: LineSegment StartX=-26.7 StartY=-33.9 StartZ=0 EndX=-26.7 EndY=-4.3 EndZ=0
    g16: LineSegment StartX=-2.5 StartY=-10.5 StartZ=0 EndX=-2.5 EndY=-27.7 EndZ=0
    g17: LineSegment StartX=-8.5 StartY=-4.3 StartZ=0 EndX=-8.5 EndY=-33.9 EndZ=0
    g18: LineSegment StartX=-5.5 StartY=-10.5 StartZ=0 EndX=-5.5 EndY=-27.7 EndZ=0
    g19: LineSegment StartX=-11.5 StartY=-4.3 StartZ=0 EndX=-11.5 EndY=-33.9 EndZ=0
    g20: LineSegment StartX=-14.6 StartY=-1.8 StartZ=0 EndX=-14.6 EndY=-36.4 EndZ=0
    g21: LineSegment StartX=-17.6 StartY=-1.8 StartZ=0 EndX=-17.6 EndY=-36.4 EndZ=0
    g22: LineSegment StartX=-20.6 StartY=-36.4 StartZ=0 EndX=-20.6 EndY=-1.8 EndZ=0
    g23: LineSegment StartX=-23.6 StartY=-1.8 StartZ=0 EndX=-23.6 EndY=-36.4 EndZ=0
  constraints (48):
    c: Block(g0)
    c: Block(g1)
    c: Block(g2)
    c: Block(g3)
    c: Block(g4)
    c: Block(g5)
    c: Block(g6)
    c: Block(g7)
    c: Block(g8)
    c: Block(g9)
    c: Block(g10)
    c: Block(g11)
    c: Coincident(g12,g1)
    c: Coincident(g12,g2)
    c: Vertical(g12)
    c: Coincident(g13,g1)
    c: Coincident(g13,g2)
    c: Vertical(g13)
    c: Coincident(g14,g11)
    c: Coincident(g14,g7)
    c: Vertical(g14)
    c: Coincident(g15,g11)
    c: Coincident(g15,g7)
    c: Vertical(g15)
    c: Coincident(g16,g0)
    c: Coincident(g16,g3)
    c: Vertical(g16)
    c: Coincident(g17,g4)
    c: Coincident(g17,g8)
    c: Vertical(g17)
    c: Coincident(g18,g0)
    c: Coincident(g18,g3)
    c: Vertical(g18)
    c: Coincident(g19,g4)
    c: Coincident(g19,g8)
    c: Vertical(g19)
    c: Coincident(g20,g5)
    c: Coincident(g20,g9)
    c: Vertical(g20)
    c: Coincident(g21,g5)
    c: Coincident(g21,g9)
    c: Vertical(g21)
    c: Coincident(g22,g10)
    c: Coincident(g22,g6)
    c: Vertical(g22)
    c: Coincident(g23,g6)
    c: Coincident(g23,g10)
    c: Vertical(g23)
FEATURE [Part::Extrusion] Extrude038  label="removeToCreateFanGrillHoles001"
  Base = -> Sketch047
  Dir = (0,-1,6e-16)
  DirMode = 2
  FaceMakerClass = Part::FaceMakerBullseye
  LengthFwd = 10
  LengthRev = 0
  Placement = pos=(65.4,44,54.82) rot=(0,0,1;0rad)
  Solid = true
  Symmetric = false
FEATURE [Part::Feature] Wire004
  shape: bbox 11 x 5.2 x 2e-07 mm, 0 faces, 0 solids (baked)
FEATURE [Part::Revolution] Revolve095
  Angle = 360
  Axis = (0,1,0)
  Base = (0,0,0)
  FaceMakerClass = Part::FaceMakerBullseye
  Placement = pos=(30.3,38,19.7) rot=(0,0,1;0rad)
  Solid = true
  Source = -> Wire004
  Symmetric = false
FEATURE [Part::Feature] Wire005
  shape: bbox 11 x 5.2 x 2e-07 mm, 0 faces, 0 solids (baked)
FEATURE [Part::Revolution] Revolve096
  Angle = 360
  Axis = (0,1,0)
  Base = (0,0,0)
  FaceMakerClass = Part::FaceMakerBullseye
  Placement = pos=(30.3,38,51.7) rot=(0,0,1;0rad)
  Solid = true
  Source = -> Wire005
  Symmetric = false
FEATURE [Part::Feature] Wire006
  shape: bbox 11 x 5.2 x 2e-07 mm, 0 faces, 0 solids (baked)
FEATURE [Part::Revolution] Revolve097
  Angle = 360
  Axis = (0,1,0)
  Base = (0,0,0)
  FaceMakerClass = Part::FaceMakerBullseye
  Placement = pos=(62.3,38,51.7) rot=(0,0,1;0rad)
  Solid = true
  Source = -> Wire006
  Symmetric = false
FEATURE [Part::Feature] Wire007
  shape: bbox 11 x 5.2 x 2e-07 mm, 0 faces, 0 solids (baked)
FEATURE [Part::Revolution] Revolve098
  Angle = 360
  Axis = (0,1,0)
  Base = (0,0,0)
  FaceMakerClass = Part::FaceMakerBullseye
  Placement = pos=(62.3,38,19.7) rot=(0,0,1;0rad)
  Solid = true
  Source = -> Wire007
  Symmetric = false
FEATURE [Part::MultiFuse] Fusion067  label="fanScrewHousing002"
  Shapes = -> [Revolve098,Revolve097,Revolve096,Revolve095]
FEATURE [Part::Feature] Face091 .. Face094  x4 (patterned run collapsed; names and placements below)
  shape: bbox 3.5 x 17.8 x 2e-07 mm, 1 faces, 0 solids (baked)
FEATURE [Part::Revolution] Revolve099  label="removeToCreateScrewAndThreadedInsertHole026"
  Angle = 360
  Axis = (0,1,0)
  Base = (0,0,0)
  FaceMakerClass = Part::FaceMakerBullseye
  Placement = pos=(62.3,30.3,19.7) rot=(0,0,1;0rad)
  Solid = false
  Source = -> Face091
  Symmetric = false
FEATURE [Part::Revolution] Revolve100  label="removeToCreateScrewAndThreadedInsertHole027"
  Angle = 360
  Axis = (0,1,0)
  Base = (0,0,0)
  FaceMakerClass = Part::FaceMakerBullseye
  Placement = pos=(62.3,30.3,51.7) rot=(0,0,1;0rad)
  Solid = false
  Source = -> Face092
  Symmetric = false
FEATURE [Part::Revolution] Revolve101  label="removeToCreateScrewAndThreadedInsertHole028"
  Angle = 360
  Axis = (0,1,0)
  Base = (0,0,0)
  FaceMakerClass = Part::FaceMakerBullseye
  Placement = pos=(30.3,30.3,19.7) rot=(0,0,1;0rad)
  Solid = false
  Source = -> Face093
  Symmetric = false
FEATURE [Part::Revolution] Revolve102  label="removeToCreateScrewAndThreadedInsertHole029"
  Angle = 360
  Axis = (0,1,0)
  Base = (0,0,0)
  FaceMakerClass = Part::FaceMakerBullseye
  Placement = pos=(30.3,30.3,51.7) rot=(0,0,1;0rad)
  Solid = false
  Source = -> Face094
  Symmetric = false
FEATURE [Part::MultiFuse] Fusion068  label="createThreadedInsertHolesForFan002"
  Shapes = -> [Revolve099,Revolve100,Revolve101,Revolve102]
FEATURE [Part::Cut] Cut026  label="fanScrewHousing003"
  Base = -> Fusion067
  Tool = -> Fusion068
FEATURE [Sketcher::SketchObject] Sketch048
  FullyConstrained = false
  Placement = pos=(0,0,0) rot=(1,0,0;1.5708rad)
  sketch-geometry (24):
    g0: ArcOfCircle CenterX=-4 CenterY=-10.5 CenterZ=0 NormalX=0 NormalY=0 NormalZ=1 AngleXU=0 Radius=1.5 StartAngle=6e-16 EndAngle=3.14159
    g1: ArcOfCircle CenterX=-34.2 CenterY=-10.5 CenterZ=0 NormalX=0 NormalY=0 NormalZ=1 AngleXU=0 Radius=1.5 StartAngle=0 EndAngle=3.14159
    g2: ArcOfCircle CenterX=-34.2 CenterY=-27.7 CenterZ=0 NormalX=0 NormalY=0 NormalZ=1 AngleXU=0 Radius=1.5 StartAngle=3.14159 EndAngle=6.28319
    g3: ArcOfCircle CenterX=-4 CenterY=-27.7 CenterZ=0 NormalX=0 NormalY=0 NormalZ=1 AngleXU=0 Radius=1.5 StartAngle=3.1416 EndAngle=6.28319
    g4: ArcOfCircle CenterX=-10 CenterY=-4.3 CenterZ=0 NormalX=0 NormalY=0 NormalZ=1 AngleXU=0 Radius=1.5 StartAngle=2e-16 EndAngle=3.14159
    g5: ArcOfCircle CenterX=-16.1 CenterY=-1.8 CenterZ=0 NormalX=0 NormalY=0 NormalZ=1 AngleXU=0 Radius=1.5 StartAngle=5e-16 EndAngle=3.14159
    g6: ArcOfCircle CenterX=-22.1 CenterY=-1.8 CenterZ=0 NormalX=0 NormalY=0 NormalZ=1 AngleXU=0 Radius=1.5 StartAngle=5e-16 EndAngle=3.14159
    g7: ArcOfCircle CenterX=-28.2 CenterY=-4.3 CenterZ=0 NormalX=0 NormalY=0 NormalZ=1 AngleXU=0 Radius=1.5 StartAngle=2e-16 EndAngle=3.14159
    g8: ArcOfCircle CenterX=-10 CenterY=-33.9 CenterZ=0 NormalX=0 NormalY=0 NormalZ=1 AngleXU=0 Radius=1.5 StartAngle=3.14159 EndAngle=6.28319
    g9: ArcOfCircle CenterX=-16.1 CenterY=-36.4 CenterZ=0 NormalX=0 NormalY=0 NormalZ=1 AngleXU=0 Radius=1.5 StartAngle=3.14159 EndAngle=6.28319
    g10: ArcOfCircle CenterX=-22.1 CenterY=-36.4 CenterZ=0 NormalX=0 NormalY=0 NormalZ=1 AngleXU=0 Radius=1.5 StartAngle=3.14159 EndAngle=6.28319
    g11: ArcOfCircle CenterX=-28.2 CenterY=-33.9 CenterZ=0 NormalX=0 NormalY=0 NormalZ=1 AngleXU=0 Radius=1.5 StartAngle=3.14159 EndAngle=6.28319
    g12: LineSegment StartX=-35.7 StartY=-10.5 StartZ=0 EndX=-35.7 EndY=-27.7 EndZ=0
    g13: LineSegment StartX=-32.7 StartY=-10.5 StartZ=0 EndX=-32.7 EndY=-27.7 EndZ=0
    g14: LineSegment StartX=-29.7 StartY=-33.9 StartZ=0 EndX=-29.7 EndY=-4.3 EndZ=0
    g15: LineSegment StartX=-26.7 StartY=-33.9 StartZ=0 EndX=-26.7 EndY=-4.3 EndZ=0
    g16: LineSegment StartX=-2.5 StartY=-10.5 StartZ=0 EndX=-2.5 EndY=-27.7 EndZ=0
    g17: LineSegment StartX=-8.5 StartY=-4.3 StartZ=0 EndX=-8.5 EndY=-33.9 EndZ=0
    g18: LineSegment StartX=-5.5 StartY=-10.5 StartZ=0 EndX=-5.5 EndY=-27.7 EndZ=0
    g19: LineSegment StartX=-11.5 StartY=-4.3 StartZ=0 EndX=-11.5 EndY=-33.9 EndZ=0
    g20: LineSegment StartX=-14.6 StartY=-1.8 StartZ=0 EndX=-14.6 EndY=-36.4 EndZ=0
    g21: LineSegment StartX=-17.6 StartY=-1.8 StartZ=0 EndX=-17.6 EndY=-36.4 EndZ=0
    g22: LineSegment StartX=-20.6 StartY=-36.4 StartZ=0 EndX=-20.6 EndY=-1.8 EndZ=0
    g23: LineSegment StartX=-23.6 StartY=-1.8 StartZ=0 EndX=-23.6 EndY=-36.4 EndZ=0
  constraints (48):
    c: Block(g0)
    c: Block(g1)
    c: Block(g2)
    c: Block(g3)
    c: Block(g4)
    c: Block(g5)
    c: Block(g6)
    c: Block(g7)
    c: Block(g8)
    c: Block(g9)
    c: Block(g10)
    c: Block(g11)
    c: Coincident(g12,g1)
    c: Coincident(g12,g2)
    c: Vertical(g12)
    c: Coincident(g13,g1)
    c: Coincident(g13,g2)
    c: Vertical(g13)
    c: Coincident(g14,g11)
    c: Coincident(g14,g7)
    c: Vertical(g14)
    c: Coincident(g15,g11)
    c: Coincident(g15,g7)
    c: Vertical(g15)
    c: Coincident(g16,g0)
    c: Coincident(g16,g3)
    c: Vertical(g16)
    c: Coincident(g17,g4)
    c: Coincident(g17,g8)
    c: Vertical(g17)
    c: Coincident(g18,g0)
    c: Coincident(g18,g3)
    c: Vertical(g18)
    c: Coincident(g19,g4)
    c: Coincident(g19,g8)
    c: Vertical(g19)
    c: Coincident(g20,g5)
    c: Coincident(g20,g9)
    c: Vertical(g20)
    c: Coincident(g21,g5)
    c: Coincident(g21,g9)
    c: Vertical(g21)
    c: Coincident(g22,g10)
    c: Coincident(g22,g6)
    c: Vertical(g22)
    c: Coincident(g23,g6)
    c: Coincident(g23,g10)
    c: Vertical(g23)
FEATURE [Part::Extrusion] Extrude039  label="removeToCreateFanGrillHoles002"
  Base = -> Sketch048
  Dir = (0,-1,6e-16)
  DirMode = 2
  FaceMakerClass = Part::FaceMakerBullseye
  LengthFwd = 10
  LengthRev = 0
  Placement = pos=(65.4,44,54.82) rot=(0,0,1;0rad)
  Solid = true
  Symmetric = false
FEATURE [Part::Cut] Cut027  label="fanScrewHousing004"
  Base = -> Cut026
  Tool = -> Extrude038
FEATURE [Part::Cut] Cut028  label="top014"
  Base = -> Fillet026
  Tool = -> Extrude039
FEATURE [Part::Feature] Face095 .. Face098  x4 (patterned run collapsed; names and placements below)
  shape: bbox 3.5 x 17.8 x 2e-07 mm, 1 faces, 0 solids (baked)
FEATURE [Part::Revolution] Revolve103  label="removeToCreateScrewAndThreadedInsertHole030"
  Angle = 360
  Axis = (0,1,0)
  Base = (0,0,0)
  FaceMakerClass = Part::FaceMakerBullseye
  Placement = pos=(62.3,30.3,19.7) rot=(0,0,1;0rad)
  Solid = false
  Source = -> Face095
  Symmetric = false
FEATURE [Part::Revolution] Revolve104  label="removeToCreateScrewAndThreadedInsertHole031"
  Angle = 360
  Axis = (0,1,0)
  Base = (0,0,0)
  FaceMakerClass = Part::FaceMakerBullseye
  Placement = pos=(62.3,30.3,51.7) rot=(0,0,1;0rad)
  Solid = false
  Source = -> Face096
  Symmetric = false
FEATURE [Part::Revolution] Revolve105  label="removeToCreateScrewAndThreadedInsertHole032"
  Angle = 360
  Axis = (0,1,0)
  Base = (0,0,0)
  FaceMakerClass = Part::FaceMakerBullseye
  Placement = pos=(30.3,30.3,19.7) rot=(0,0,1;0rad)
  Solid = false
  Source = -> Face097
  Symmetric = false
FEATURE [Part::Revolution] Revolve106  label="removeToCreateScrewAndThreadedInsertHole033"
  Angle = 360
  Axis = (0,1,0)
  Base = (0,0,0)
  FaceMakerClass = Part::FaceMakerBullseye
  Placement = pos=(30.3,30.3,51.7) rot=(0,0,1;0rad)
  Solid = false
  Source = -> Face098
  Symmetric = false
FEATURE [Part::MultiFuse] Fusion069  label="createThreadedInsertHolesForFan003"
  Shapes = -> [Revolve103,Revolve104,Revolve105,Revolve106]
FEATURE [Part::Cut] Cut029  label="top015"
  Base = -> Cut028
  Tool = -> Fusion054
FEATURE [Part::Cut] Cut030  label="fanScrewHousing005"
  Base = -> Cut027
  Tool = -> Fusion069
FEATURE [Part::Cylinder] Cylinder026  label="removeToCreteHoleForPlugHousing010"
  Angle = 360
  AttacherType = Attacher::AttachEngine3D
  Height = 20
  Placement = pos=(-2,19,36) rot=(0,1,0;1.5708rad)
  Radius = 14.3
FEATURE [Part::Box] Box018  label="removeToCreteHoleForPlugHousing011"
  AttacherType = Attacher::AttachEngine3D
  Height = 28.6
  Length = 10
  Placement = pos=(-2,0,21.7) rot=(0,0,1;0rad)
  Width = 19
FEATURE [Part::Box] Box019  label="wireHolderBottomCaseBit"
  AttacherType = Attacher::AttachEngine3D
  Height = 28
  Length = 3
  Placement = pos=(0,0,22) rot=(0,0,1;0rad)
  Width = 21
FEATURE [Part::Cylinder] Cylinder027  label="removeToCreteHoleForPlugHousing012"
  Angle = 360
  AttacherType = Attacher::AttachEngine3D
  Height = 20
  Placement = pos=(-2,19,36) rot=(0,1,0;1.5708rad)
  Radius = 14.3
FEATURE [Part::Cut] Cut031  label="wireHolderBottomCaseBit001"
  Base = -> Box019
  Tool = -> Cylinder027
FEATURE [Part::MultiFuse] Fusion070  label="removeToCreteHoleForPlugHousing013"
  Shapes = -> [Box018,Cylinder026]
FEATURE [Part::Cut] Cut032  label="top016"
  Base = -> Cut029
  Tool = -> Fusion070
FEATURE [Part::Cylinder] Cylinder028
  Angle = 360
  AttacherType = Attacher::AttachEngine3D
  Height = 20
  Placement = pos=(0,0,36.15) rot=(0,0,1;0rad)
  Radius = 14.3
FEATURE [Part::Cylinder] Cylinder029
  Angle = 360
  AttacherType = Attacher::AttachEngine3D
  Height = 10
  Placement = pos=(0,0,36.15) rot=(0,0,1;0rad)
  Radius = 4
FEATURE [Part::MultiFuse] Fusion071  label="removeToCreteHoleForPlugHousing014"
  Placement = pos=(70,19,36) rot=(0,1,0;1.5708rad)
  Shapes = -> [Cylinder028,Cylinder029]
FEATURE [Sketcher::SketchObject] Sketch049  label="topSketch011"
  FullyConstrained = true
  sketch-geometry (4):
    g0: ArcOfCircle CenterX=105 CenterY=19 CenterZ=0 NormalX=0 NormalY=0 NormalZ=1 AngleXU=0 Radius=20.6155 StartAngle=5.54125 EndAngle=6.28319
    g1: ArcOfCircle CenterX=105 CenterY=19 CenterZ=0 NormalX=0 NormalY=0 NormalZ=1 AngleXU=0 Radius=13 StartAngle=5.54125 EndAngle=6.28319
    g2: LineSegment StartX=118 StartY=19 StartZ=0 EndX=125.616 EndY=19 EndZ=0
    g3: LineSegment StartX=114.583 StartY=10.2157 StartZ=0 EndX=120.197 EndY=5.06982 EndZ=0
  constraints (7):
    c: Block(g0)
    c: Block(g1)
    c: Coincident(g2,g1)
    c: Coincident(g2,g0)
    c: Horizontal(g2)
    c: Coincident(g3,g1)
    c: Coincident(g3,g0)
FEATURE [Part::Box] Box020  label="removeToCreteHoleForPlugHousing015"
  AttacherType = Attacher::AttachEngine3D
  Height = 28.6
  Length = 20
  Placement = pos=(106.15,0,21.7) rot=(0,0,1;0rad)
  Width = 19
FEATURE [Part::MultiFuse] Fusion072  label="removeToCreteHoleForPlugHousing016"
  Shapes = -> [Box020,Fusion071]
FEATURE [Part::Cut] Cut033  label="removeToCreteHoleForPlugHousing017"
  Base = -> Cut032
  Tool = -> Fusion072
FEATURE [Part::Cylinder] Cylinder030
  Angle = 360
  AttacherType = Attacher::AttachEngine3D
  Height = 20
  Placement = pos=(0,0,36.15) rot=(0,0,1;0rad)
  Radius = 14.3
FEATURE [Part::Cylinder] Cylinder031
  Angle = 360
  AttacherType = Attacher::AttachEngine3D
  Height = 10
  Placement = pos=(0,0,36.15) rot=(0,0,1;0rad)
  Radius = 4
FEATURE [Part::Box] Box021  label="removeToCreteHoleForPlugHousing019"
  AttacherType = Attacher::AttachEngine3D
  Height = 28.6
  Length = 20
  Placement = pos=(106.15,0,21.7) rot=(0,0,1;0rad)
  Width = 19
FEATURE [Part::MultiFuse] Fusion074  label="removeToCreteHoleForPlugHousing020"
  Placement = pos=(70,19,36) rot=(0,1,0;1.5708rad)
  Shapes = -> [Cylinder030,Cylinder031]
FEATURE [Part::MultiFuse] Fusion073  label="removeToCreteHoleForPlugHousing018"
  Placement = pos=(0,0,28.3) rot=(0,0,1;0rad)
  Shapes = -> [Box021,Fusion074]
FEATURE [Part::Cylinder] Cylinder032
  Angle = 360
  AttacherType = Attacher::AttachEngine3D
  Height = 20
  Placement = pos=(0,0,36.15) rot=(0,0,1;0rad)
  Radius = 14.3
FEATURE [Part::Cylinder] Cylinder033
  Angle = 360
  AttacherType = Attacher::AttachEngine3D
  Height = 10
  Placement = pos=(0,0,36.15) rot=(0,0,1;0rad)
  Radius = 4
FEATURE [Part::Box] Box022  label="removeToCreteHoleForPlugHousing021"
  AttacherType = Attacher::AttachEngine3D
  Height = 28.6
  Length = 20
  Placement = pos=(106.15,0,21.7) rot=(0,0,1;0rad)
  Width = 19
FEATURE [Part::MultiFuse] Fusion076  label="removeToCreteHoleForPlugHousing023"
  Placement = pos=(70,19,36) rot=(0,1,0;1.5708rad)
  Shapes = -> [Cylinder032,Cylinder033]
FEATURE [Part::MultiFuse] Fusion075  label="removeToCreteHoleForPlugHousing022"
  Placement = pos=(0,0,-28.3) rot=(0,0,1;0rad)
  Shapes = -> [Box022,Fusion076]
FEATURE [Part::MultiFuse] Fusion077  label="removeToCreatePlugHousingBottomBit"
  Shapes = -> [Fusion075,Fusion073]
FEATURE [Part::Cylinder] Cylinder034
  Angle = 360
  AttacherType = Attacher::AttachEngine3D
  Height = 20
  Placement = pos=(0,0,36.15) rot=(0,0,1;0rad)
  Radius = 14
FEATURE [Part::Cylinder] Cylinder035
  Angle = 360
  AttacherType = Attacher::AttachEngine3D
  Height = 10
  Placement = pos=(0,0,36.15) rot=(0,0,1;0rad)
  Radius = 4
FEATURE [Part::MultiFuse] Fusion078  label="removeToCreteHoleForPlugHousing024"
  Placement = pos=(70,19,36) rot=(0,1,0;1.5708rad)
  Shapes = -> [Cylinder034,Cylinder035]
FEATURE [Part::MultiFuse] Fusion079  label="removeToCreatePlugHousingBottomBit001"
  Shapes = -> [Fusion078,Fusion077]
FEATURE [Part::Extrusion] Extrude040  label="bottomPlugHousingBit"
  Base = -> Sketch049
  Dir = (0,0,1)
  DirMode = 2
  FaceMakerClass = Part::FaceMakerBullseye
  LengthFwd = 72
  LengthRev = 0
  Solid = true
  Symmetric = false
FEATURE [Part::Cut] Cut034  label="bottomPlugHousingBit001"
  Base = -> Extrude040
  Placement = pos=(-0.09,0,0) rot=(0,0,1;0rad)
  Tool = -> Fusion079
FEATURE [Part::Box] Box023  label="Cube014"
  AttacherType = Attacher::AttachEngine3D
  Height = 16
  Length = 8
  Placement = pos=(12.7,31.52,28) rot=(0,0,1;0rad)
  Width = 4
FEATURE [Part::Cylinder] Cylinder036
  Angle = 360
  AttacherType = Attacher::AttachEngine3D
  Height = 10
  Placement = pos=(0,0,36.15) rot=(0,0,1;0rad)
  Radius = 4
FEATURE [Part::Cylinder] Cylinder037
  Angle = 360
  AttacherType = Attacher::AttachEngine3D
  Height = 20
  Placement = pos=(0,0,36.15) rot=(0,0,1;0rad)
  Radius = 8.2
FEATURE [Part::MultiFuse] Fusion080  label="removeToCreteHoleForPlugHousing025"
  Placement = pos=(-42,19,36) rot=(0,1,0;1.5708rad)
  Shapes = -> [Cylinder037,Cylinder036]
FEATURE [Sketcher::SketchObject] Sketch050  label="topSketch012"
  FullyConstrained = true
  sketch-geometry (4):
    g0: LineSegment StartX=16.8446 StartY=31.512 StartZ=0 EndX=16.3251 EndY=34.4666 EndZ=0
    g1: ArcOfCircle CenterX=19 CenterY=19.2524 CenterZ=0 NormalX=0 NormalY=0 NormalZ=1 AngleXU=0 Radius=15.4476 StartAngle=1.74483 EndAngle=2.72717
    g2: ArcOfCircle CenterX=19 CenterY=19.2524 CenterZ=0 NormalX=0 NormalY=0 NormalZ=1 AngleXU=0 Radius=12.4476 StartAngle=1.74483 EndAngle=2.73189
    g3: LineSegment StartX=4.86004 StartY=25.4725 StartZ=0 EndX=7.58253 EndY=24.2107 EndZ=0
  constraints (7):
    c: Block(g0)
    c: Coincident(g1,g0)
    c: Coincident(g2,g0)
    c: Coincident(g3,g1)
    c: Coincident(g3,g2)
    c: Block(g1)
    c: Block(g2)
FEATURE [Part::Extrusion] Extrude041
  Base = -> Sketch050
  Dir = (0,0,1)
  DirMode = 2
  FaceMakerClass = Part::FaceMakerBullseye
  LengthFwd = 10.6
  LengthRev = 0
  Placement = pos=(0,0,31) rot=(0,0,1;0rad)
  Solid = true
  Symmetric = false
FEATURE [Part::Cut] Cut035
  Base = -> Extrude041
  Placement = pos=(0,0,-0.3) rot=(0,0,1;0rad)
  Tool = -> Fusion080
FEATURE [Part::Cut] Cut036
  Base = -> Box023
  Tool = -> Cut035
FEATURE [Part::Fillet] Fillet027
  Base = -> Cut036
  Edges = 1 edges r=0.7: [Edge13]
FEATURE [Part::Fillet] Fillet028
  Base = -> Fillet027
  Edges = 1 edges r=0.7: [Edge13]
FEATURE [Part::Fillet] Fillet029
  Base = -> Fillet028
  Edges = 1 edges r=0.7: [Edge16]
FEATURE [Part::Fillet] Fillet030
  Base = -> Fillet029
  Edges = 1 edges r=0.7: [Edge11]
FEATURE [Part::Fillet] Fillet031
  Base = -> Fillet030
  Edges = 1 edges r=0.7: [Edge10]
FEATURE [Part::Fillet] Fillet032
  Base = -> Fillet031
  Edges = 1 edges r=1.2: [Edge5]
FEATURE [Part::Fillet] Fillet033
  Base = -> Fillet032
  Edges = 1 edges r=1.2: [Edge12]
FEATURE [Part::Fillet] Fillet034  label="wireHousingRetainer"
  Base = -> Fillet033
  Edges = 1 edges r=2: [Edge1]
  Placement = pos=(0.3,0,0) rot=(0,0,1;0rad)
FEATURE [Part::Feature] Face099
  shape: bbox 3.5 x 17.8 x 2e-07 mm, 1 faces, 0 solids (baked)
FEATURE [Part::Revolution] Revolve107  label="removeToCreateScrewAndThreadedInsertHole034"
  Angle = 360
  Axis = (0,1,0)
  Base = (0,0,0)
  FaceMakerClass = Part::FaceMakerBullseye
  Placement = pos=(12.5,0,10) rot=(0,0,1;0rad)
  Solid = false
  Source = -> Face099
  Symmetric = false
FEATURE [Part::Feature] Face100
  shape: bbox 3.5 x 17.8 x 2e-07 mm, 1 faces, 0 solids (baked)
FEATURE [Part::Revolution] Revolve108  label="removeToCreateScrewAndThreadedInsertHole035"
  Angle = 360
  Axis = (0,1,0)
  Base = (0,0,0)
  FaceMakerClass = Part::FaceMakerBullseye
  Placement = pos=(12.5,0,62) rot=(0,0,1;0rad)
  Solid = false
  Source = -> Face100
  Symmetric = false
FEATURE [Part::Feature] Face101
  shape: bbox 3.5 x 17.8 x 2e-07 mm, 1 faces, 0 solids (baked)
FEATURE [Part::Revolution] Revolve109  label="removeToCreateScrewAndThreadedInsertHole036"
  Angle = 360
  Axis = (0,1,0)
  Base = (0,0,0)
  FaceMakerClass = Part::FaceMakerBullseye
  Placement = pos=(89.5,0,68.5) rot=(0,0,1;0rad)
  Solid = false
  Source = -> Face101
  Symmetric = false
FEATURE [Part::Feature] Face102
  shape: bbox 3.5 x 17.8 x 2e-07 mm, 1 faces, 0 solids (baked)
FEATURE [Part::Revolution] Revolve110  label="removeToCreateScrewAndThreadedInsertHole037"
  Angle = 360
  Axis = (0,1,0)
  Base = (0,0,0)
  FaceMakerClass = Part::FaceMakerBullseye
  Placement = pos=(89.5,0,3.5) rot=(0,0,1;0rad)
  Solid = false
  Source = -> Face102
  Symmetric = false
FEATURE [Part::Feature] Face103
  shape: bbox 3.5 x 17.8 x 2e-07 mm, 1 faces, 0 solids (baked)
FEATURE [Part::Revolution] Revolve111  label="removeToCreateScrewAndThreadedInsertHole038"
  Angle = 360
  Axis = (0,1,0)
  Base = (0,0,0)
  FaceMakerClass = Part::FaceMakerBullseye
  Placement = pos=(109.5,4.7,3.5) rot=(0,0,1;0rad)
  Solid = false
  Source = -> Face103
  Symmetric = false
FEATURE [Part::Feature] Face104
  shape: bbox 3.5 x 17.8 x 2e-07 mm, 1 faces, 0 solids (baked)
FEATURE [Part::Revolution] Revolve112  label="removeToCreateScrewAndThreadedInsertHole039"
  Angle = 360
  Axis = (0,1,0)
  Base = (0,0,0)
  FaceMakerClass = Part::FaceMakerBullseye
  Placement = pos=(109.5,4.7,68.5) rot=(0,0,1;0rad)
  Solid = false
  Source = -> Face104
  Symmetric = false
FEATURE [Part::MultiFuse] Fusion081  label="removeToCreateScrewAndThreadedInsertHole040"
  Shapes = -> [Revolve107,Revolve108,Revolve109,Revolve110,Revolve111,Revolve112]
FEATURE [Part::MultiFuse] Fusion082  label="casePillars002"
  Shapes = -> [Revolve094,Revolve092,Revolve090,Revolve089,Revolve091,Revolve093]
FEATURE [Part::Cut] Cut037  label="casePillars003"
  Base = -> Fusion082
  Tool = -> Fusion081
FEATURE [Sketcher::SketchObject] Sketch051
  FullyConstrained = true
  Placement = pos=(117,19,0) rot=(0.57735,0.57735,0.57735;2.0944rad)
  sketch-geometry (48):
    g0: LineSegment StartX=-49.19 StartY=69.25 StartZ=0 EndX=-49.19 EndY=66.25 EndZ=0
    g1: LineSegment StartX=-49.19 StartY=63.5 StartZ=0 EndX=-49.19 EndY=60.5 EndZ=0
    g2: LineSegment StartX=-49.19 StartY=57.75 StartZ=0 EndX=-49.19 EndY=54.75 EndZ=0
    g3: LineSegment StartX=-49.19 StartY=52 StartZ=0 EndX=-49.19 EndY=49 EndZ=0
    g4: LineSegment StartX=-49.19 StartY=46.25 StartZ=0 EndX=-49.19 EndY=43.25 EndZ=0
    g5: LineSegment StartX=-49.19 StartY=40.5 StartZ=0 EndX=-49.19 EndY=37.5 EndZ=0
    g6: LineSegment StartX=-49.19 StartY=34.5 StartZ=0 EndX=-49.19 EndY=31.5 EndZ=0
    g7: LineSegment StartX=-49.19 StartY=28.75 StartZ=0 EndX=-49.19 EndY=25.75 EndZ=0
    g8: LineSegment StartX=-49.19 StartY=23 StartZ=0 EndX=-49.19 EndY=20 EndZ=0
    g9: LineSegment StartX=-49.19 StartY=17.25 StartZ=0 EndX=-49.19 EndY=14.25 EndZ=0
    g10: LineSegment StartX=-49.19 StartY=11.5 StartZ=0 EndX=-49.19 EndY=8.5 EndZ=0
    g11: LineSegment StartX=-49.19 StartY=5.75 StartZ=0 EndX=-49.19 EndY=2.75 EndZ=0
    g12: ArcOfCircle CenterX=-1.5 CenterY=67.75 CenterZ=0 NormalX=0 NormalY=0 NormalZ=1 AngleXU=0 Radius=1.5 StartAngle=4.71239 EndAngle=7.85398
    g13: ArcOfCircle CenterX=-1.5 CenterY=62 CenterZ=0 NormalX=0 NormalY=0 NormalZ=1 AngleXU=0 Radius=1.5 StartAngle=4.71239 EndAngle=7.85398
    g14: ArcOfCircle CenterX=-1.5 CenterY=56.25 CenterZ=0 NormalX=0 NormalY=0 NormalZ=1 AngleXU=0 Radius=1.5 StartAngle=4.71239 EndAngle=7.85398
    g15: ArcOfCircle CenterX=-11.49 CenterY=50.5 CenterZ=0 NormalX=0 NormalY=0 NormalZ=1 AngleXU=0 Radius=1.5 StartAngle=4.71239 EndAngle=7.85398
    g16: ArcOfCircle CenterX=-16.28 CenterY=44.75 CenterZ=0 NormalX=0 NormalY=0 NormalZ=1 AngleXU=0 Radius=1.5 StartAngle=4.71239 EndAngle=7.85398
    g17: ArcOfCircle CenterX=-18.2337 CenterY=39 CenterZ=0 NormalX=0 NormalY=0 NormalZ=1 AngleXU=0 Radius=1.5 StartAngle=4.71485 EndAngle=7.85398
    g18: ArcOfCircle CenterX=-16.2837 CenterY=27.25 CenterZ=0 NormalX=0 NormalY=0 NormalZ=1 AngleXU=0 Radius=1.5 StartAngle=4.71485 EndAngle=7.85398
    g19: ArcOfCircle CenterX=-18.2337 CenterY=33 CenterZ=0 NormalX=0 NormalY=0 NormalZ=1 AngleXU=0 Radius=1.5 StartAngle=4.71485 EndAngle=7.85398
    g20: ArcOfCircle CenterX=-11.49 CenterY=21.5 CenterZ=0 NormalX=0 NormalY=0 NormalZ=1 AngleXU=0 Radius=1.5 StartAngle=4.71239 EndAngle=7.85398
    g21: ArcOfCircle CenterX=-1.5 CenterY=4.25 CenterZ=0 NormalX=0 NormalY=0 NormalZ=1 AngleXU=0 Radius=1.5 StartAngle=4.71239 EndAngle=7.85398
    g22: ArcOfCircle CenterX=-1.5 CenterY=10 CenterZ=0 NormalX=0 NormalY=0 NormalZ=1 AngleXU=0 Radius=1.5 StartAngle=4.71239 EndAngle=7.85398
    g23: ArcOfCircle CenterX=-1.5 CenterY=15.75 CenterZ=0 NormalX=0 NormalY=0 NormalZ=1 AngleXU=0 Radius=1.5 StartAngle=4.71239 EndAngle=7.85398
    g24: LineSegment StartX=-49.19 StartY=69.25 StartZ=0 EndX=-1.5 EndY=69.25 EndZ=0
    g25: LineSegment StartX=-49.19 StartY=66.25 StartZ=0 EndX=-1.5 EndY=66.25 EndZ=0
    g26: LineSegment StartX=-49.19 StartY=63.5 StartZ=0 EndX=-1.5 EndY=63.5 EndZ=0
    g27: LineSegment StartX=-49.19 StartY=60.5 StartZ=0 EndX=-1.5 EndY=60.5 EndZ=0
    g28: LineSegment StartX=-49.19 StartY=57.75 StartZ=0 EndX=-1.5 EndY=57.75 EndZ=0
    g29: LineSegment StartX=-49.19 StartY=54.75 StartZ=0 EndX=-1.5 EndY=54.75 EndZ=0
    g30: LineSegment StartX=-49.19 StartY=52 StartZ=0 EndX=-11.49 EndY=52 EndZ=0
    g31: LineSegment StartX=-49.19 StartY=49 StartZ=0 EndX=-11.49 EndY=49 EndZ=0
    g32: LineSegment StartX=-49.19 StartY=46.25 StartZ=0 EndX=-16.28 EndY=46.25 EndZ=0
    g33: LineSegment StartX=-49.19 StartY=43.25 StartZ=0 EndX=-16.28 EndY=43.25 EndZ=0
    g34: LineSegment StartX=-49.19 StartY=40.5 StartZ=0 EndX=-18.2337 EndY=40.5 EndZ=0
    g35: LineSegment StartX=-49.19 StartY=37.5 StartZ=0 EndX=-18.23 EndY=37.5 EndZ=0
    g36: LineSegment StartX=-49.19 StartY=34.5 StartZ=0 EndX=-18.2337 EndY=34.5 EndZ=0
    g37: LineSegment StartX=-49.19 StartY=31.5 StartZ=0 EndX=-18.23 EndY=31.5 EndZ=0
    g38: LineSegment StartX=-49.19 StartY=28.75 StartZ=0 EndX=-16.2837 EndY=28.75 EndZ=0
    g39: LineSegment StartX=-49.19 StartY=25.75 StartZ=0 EndX=-16.28 EndY=25.75 EndZ=0
    g40: LineSegment StartX=-49.19 StartY=23 StartZ=0 EndX=-11.49 EndY=23 EndZ=0
    g41: LineSegment StartX=-49.19 StartY=20 StartZ=0 EndX=-11.49 EndY=20 EndZ=0
    g42: LineSegment StartX=-49.19 StartY=17.25 StartZ=0 EndX=-1.5 EndY=17.25 EndZ=0
    g43: LineSegment StartX=-49.19 StartY=14.25 StartZ=0 EndX=-1.5 EndY=14.25 EndZ=0
    g44: LineSegment StartX=-49.19 StartY=11.5 StartZ=0 EndX=-1.5 EndY=11.5 EndZ=0
    g45: LineSegment StartX=-49.19 StartY=8.5 StartZ=0 EndX=-1.5 EndY=8.5 EndZ=0
    g46: LineSegment StartX=-49.19 StartY=5.75 StartZ=0 EndX=-1.5 EndY=5.75 EndZ=0
    g47: LineSegment StartX=-49.19 StartY=2.75 StartZ=0 EndX=-1.5 EndY=2.75 EndZ=0
  constraints (120):
    c: Vertical(g0)
    c: Distance(g0) = 3
    c: Block(g0)
    c: Vertical(g1)
    c: Distance(g1) = 3
    c: Vertical(g2)
    c: Equal(g0,g2) = 3
    c: Block(g2)
    c: Vertical(g3)
    c: Equal(g1,g3) = 3
    c: Vertical(g4)
    c: Equal(g0,g4) = 3
    c: Block(g4)
    c: Vertical(g5)
    c: Equal(g1,g5) = 3
    c: Vertical(g6)
    c: Equal(g0,g6) = 3
    c: Block(g6)
    c: Vertical(g7)
    c: Equal(g1,g7) = 3
    c: Vertical(g8)
    c: Equal(g0,g8) = 3
    c: Block(g8)
    c: Vertical(g9)
    c: Equal(g1,g9) = 3
    c: Vertical(g10)
    c: Equal(g0,g10) = 3
    c: Block(g10)
    c: Vertical(g11)
    c: Equal(g1,g11) = 3
    c: Block(g12)
    c: Block(g13)
    c: Block(g14)
    c: Block(g15)
    c: Block(g16)
    c: Block(g17)
    c: Block(g18)
    c: Block(g19)
    c: Block(g20)
    c: Block(g21)
    c: Block(g22)
    c: Block(g23)
    c: Block(g11)
    c: Block(g9)
    c: Block(g7)
    c: Block(g5)
    c: Block(g3)
    c: Block(g1)
    c: Coincident(g24,g0)
    c: Coincident(g24,g12)
    c: Horizontal(g24)
    c: Coincident(g25,g0)
    c: Coincident(g25,g12)
    c: Horizontal(g25)
    c: Coincident(g26,g1)
    c: Coincident(g26,g13)
    c: Horizontal(g26)
    c: Coincident(g27,g1)
    c: Coincident(g27,g13)
    c: Horizontal(g27)
    c: Coincident(g28,g2)
    c: Coincident(g28,g14)
    c: Horizontal(g28)
    c: Coincident(g29,g2)
    c: Coincident(g29,g14)
    c: Horizontal(g29)
    c: Coincident(g30,g3)
    c: Coincident(g30,g15)
    c: Horizontal(g30)
    c: Coincident(g31,g3)
    c: Coincident(g31,g15)
    c: Horizontal(g31)
    c: Coincident(g32,g4)
    c: Coincident(g32,g16)
    c: Horizontal(g32)
    c: Coincident(g33,g4)
    c: Coincident(g33,g16)
    c: Horizontal(g33)
    c: Coincident(g34,g5)
    c: Coincident(g34,g17)
    c: Horizontal(g34)
    c: Coincident(g35,g5)
    c: Coincident(g35,g17)
    c: Horizontal(g35)
    c: Coincident(g36,g6)
    c: Coincident(g36,g19)
    c: Horizontal(g36)
    c: Coincident(g37,g6)
    c: Coincident(g37,g19)
    c: Horizontal(g37)
    c: Coincident(g38,g7)
    c: Coincident(g38,g18)
    c: Horizontal(g38)
    c: Coincident(g39,g7)
    c: Coincident(g39,g18)
    c: Horizontal(g39)
    c: Coincident(g40,g8)
    c: Coincident(g40,g20)
    c: Horizontal(g40)
    c: Coincident(g41,g8)
    c: Coincident(g41,g20)
    c: Horizontal(g41)
    c: Coincident(g42,g9)
    c: Coincident(g42,g23)
    c: Horizontal(g42)
    c: Coincident(g43,g9)
    c: Coincident(g43,g23)
    c: Horizontal(g43)
    c: Coincident(g44,g10)
    c: Coincident(g44,g22)
    c: Horizontal(g44)
    c: Coincident(g45,g10)
    c: Coincident(g45,g22)
    c: Horizontal(g45)
    c: Coincident(g46,g11)
    c: Coincident(g46,g21)
    c: Horizontal(g46)
    c: Coincident(g47,g11)
    c: Coincident(g47,g21)
    c: Horizontal(g47)
FEATURE [Part::Extrusion] Extrude042
  Base = -> Sketch051
  Dir = (1,-2e-16,2e-16)
  DirMode = 2
  FaceMakerClass = Part::FaceMakerBullseye
  LengthFwd = 19
  LengthRev = 0
  Placement = pos=(-19,0,0) rot=(0,0,1;0rad)
  Solid = true
  Symmetric = false
FEATURE [Part::Fillet] Fillet035  label="removeToCreateVentalationHoles"
  Base = -> Extrude042
  Edges = <same value as first occurrence — deduplicated (x6 in doc)>
  Placement = pos=(7,0,0) rot=(0,0,1;0rad)
FEATURE [Part::Cut] Cut038  label="top017"
  Base = -> Cut033
  Tool = -> Fillet035
FEATURE [Sketcher::SketchObject] Sketch052  label="bottomSketch001"
  FullyConstrained = true
  sketch-geometry (45):
    g0: LineSegment StartX=6.29999 StartY=8 StartZ=0 EndX=3.29999 EndY=8 EndZ=0
    g1: LineSegment StartX=3.29999 StartY=8 StartZ=0 EndX=3.29999 EndY=-6.03275e-07 EndZ=0
    g2: ArcOfCircle CenterX=8.29999 CenterY=5 CenterZ=0 NormalX=0 NormalY=0 NormalZ=1 AngleXU=0 Radius=2 StartAngle=3.14159 EndAngle=4.71239
    g3: LineSegment StartX=6.29999 StartY=8 StartZ=0 EndX=6.29999 EndY=5 EndZ=0
    g4: ArcOfCircle CenterX=105 CenterY=19 CenterZ=0 NormalX=0 NormalY=0 NormalZ=1 AngleXU=0 Radius=12.7 StartAngle=4.71239 EndAngle=5.94289
    g5-g11: Circle x7 (B-spline internal-alignment scaffolding for g12; pole/knot coordinates omitted)
    g12: BSplineCurve PolesCount=7 KnotsCount=5 Degree=3 IsPeriodic=0
    g13-g17: GeomPoint x5 (B-spline internal-alignment scaffolding for g12; pole/knot coordinates omitted)
    g18: ArcOfCircle CenterX=105 CenterY=19 CenterZ=0 NormalX=0 NormalY=0 NormalZ=1 AngleXU=0 Radius=15.7 StartAngle=5.81226 EndAngle=6.28319
    g19: BSplineCurve PolesCount=5 KnotsCount=3 Degree=3 IsPeriodic=0
    g20: LineSegment StartX=8.29999 StartY=3 StartZ=0 EndX=101.7 EndY=3 EndZ=0
    g21: LineSegment StartX=3.29999 StartY=-6.03275e-07 StartZ=0 EndX=105 EndY=-6.03275e-07 EndZ=0
    g22: LineSegment StartX=120.974 StartY=8.71251 StartZ=0 EndX=122.332 EndY=7.83778 EndZ=0
    g23: LineSegment StartX=105 StartY=-6.03274e-07 StartZ=0 EndX=113 EndY=-6.03274e-07 EndZ=0
    g24: ArcOfCircle CenterX=105 CenterY=19 CenterZ=0 NormalX=0 NormalY=0 NormalZ=1 AngleXU=0 Radius=20.6155 StartAngle=5.11091 EndAngle=5.71103
    g25: ArcOfCircle CenterX=117.7 CenterY=19 CenterZ=0 NormalX=0 NormalY=0 NormalZ=1 AngleXU=0 Radius=3 StartAngle=1.2e-15 EndAngle=2.10468
    g26: Circle CenterX=116.345 CenterY=16.3232 CenterZ=0 NormalX=0 NormalY=0 NormalZ=1 AngleXU=0 Radius=1
    g27: Circle CenterX=117.24 CenterY=15.7584 CenterZ=0 NormalX=0 NormalY=0 NormalZ=1 AngleXU=0 Radius=1
    g28: Circle CenterX=116.972 CenterY=14.7612 CenterZ=0 NormalX=0 NormalY=0 NormalZ=1 AngleXU=0 Radius=1
    g29: BSplineCurve PolesCount=3 KnotsCount=2 Degree=2 IsPeriodic=0
    g30: GeomPoint X=116.345 Y=16.3232 Z=0
    g31: GeomPoint X=116.972 Y=14.7612 Z=0
    g32: Circle CenterX=115.828 CenterY=17.157 CenterZ=0 NormalX=0 NormalY=0 NormalZ=1 AngleXU=0 Radius=1
    g33: Circle CenterX=115.841 CenterY=16.639 CenterZ=0 NormalX=0 NormalY=0 NormalZ=1 AngleXU=0 Radius=1
    g34: Circle CenterX=116.345 CenterY=16.3232 CenterZ=0 NormalX=0 NormalY=0 NormalZ=1 AngleXU=0 Radius=1
    g35: BSplineCurve PolesCount=3 KnotsCount=2 Degree=2 IsPeriodic=0
    g36: GeomPoint X=115.828 Y=17.157 Z=0
    g37: GeomPoint X=116.345 Y=16.3232 Z=0
    g38: LineSegment StartX=115.828 StartY=17.157 StartZ=0 EndX=115.828 EndY=20.8307 EndZ=0
    g39: Circle CenterX=115.828 CenterY=20.8307 CenterZ=0 NormalX=0 NormalY=0 NormalZ=1 AngleXU=0 Radius=1
    g40: Circle CenterX=115.831 CenterY=21.3396 CenterZ=0 NormalX=0 NormalY=0 NormalZ=1 AngleXU=0 Radius=1
    g41: Circle CenterX=116.173 CenterY=21.5825 CenterZ=0 NormalX=0 NormalY=0 NormalZ=1 AngleXU=0 Radius=1
    g42: BSplineCurve PolesCount=3 KnotsCount=2 Degree=2 IsPeriodic=0
    g43: GeomPoint X=115.828 Y=20.8307 Z=0
    g44: GeomPoint X=116.173 Y=21.5825 Z=0
  constraints (70):
    c: Horizontal(g0)
    c: Distance(g0) = 3
    c: Coincident(g1,g0)
    c: Vertical(g1)
    c: Block(g2)
    c: Block(g0)
    c: Coincident(g3,g0)
    c: Coincident(g3,g2)
    c: Vertical(g3)
    c: Block(g1)
    c: Block(g4)
    c: Coincident(g19,g4)
    c: Block(g19)
    c: Equal(g5, g6-g11) x6
    c: InternalAlignment(g5-g11 -> g12) x7
    c: InternalAlignment(g13-g17 -> g12) x5
    c: Block(g12)
    c: Coincident(g18,g12)
    c: Block(g18)
    c: Coincident(g20,g2)
    c: Coincident(g20,g19)
    c: Horizontal(g20)
    c: Distance(g20) = 93.4
    c: Coincident(g21,g1)
    c: Horizontal(g21)
    c: Distance(g21) = 101.7
    c: Horizontal(g23)
    c: Distance(g23) = 8
    c: Coincident(g24,g23)
    c: Block(g23)
    c: Coincident(g22,g24)
    c: Block(g24)
    c: Block(g22)
    c: Distance(g22) = 1.61553
    c: Coincident(g25,g18)
    c: Block(g25)
    c: Weight(g26) = 1
    c: Equal(g26,g27)
    c: Equal(g26,g28)
    c: Coincident(g29,g4)
    c: InternalAlignment(g26,g29)
    c: InternalAlignment(g27,g29)
    c: InternalAlignment(g28,g29)
    c: InternalAlignment(g30,g29)
    c: InternalAlignment(g31,g29)
    c: Block(g29)
    c: Weight(g32) = 1
    c: Equal(g32,g33)
    c: Equal(g32,g34)
    c: Coincident(g35,g29)
    c: InternalAlignment(g32,g35)
    c: InternalAlignment(g33,g35)
    c: InternalAlignment(g34,g35)
    c: InternalAlignment(g36,g35)
    c: InternalAlignment(g37,g35)
    c: Block(g35)
    c: Coincident(g38,g35)
    c: Vertical(g38)
    c: Block(g38)
    c: Coincident(g42,g38)
    c: Weight(g39) = 1
    c: Equal(g39,g40)
    c: Equal(g39,g41)
    c: Coincident(g42,g25)
    c: InternalAlignment(g39,g42)
    c: InternalAlignment(g40,g42)
    c: InternalAlignment(g41,g42)
    c: InternalAlignment(g43,g42)
    c: InternalAlignment(g44,g42)
    c: Block(g42)
FEATURE [Part::Extrusion] Extrude043  label="bottom010"
  Base = -> Sketch052
  Dir = (0,0,1)
  DirMode = 2
  FaceMakerClass = Part::FaceMakerBullseye
  LengthFwd = 71.4
  LengthRev = 0
  Placement = pos=(0,0,0.3) rot=(0,0,1;0rad)
  Solid = true
  Symmetric = false
FEATURE [Sketcher::SketchObject] Sketch053  label="topSketch013"
  FullyConstrained = true
  sketch-geometry (22):
    g0: LineSegment StartX=5.21097e-06 StartY=3 StartZ=0 EndX=5.21097e-06 EndY=19 EndZ=0
    g1: ArcOfCircle CenterX=19 CenterY=19 CenterZ=0 NormalX=0 NormalY=0 NormalZ=1 AngleXU=0 Radius=19 StartAngle=1.5708 EndAngle=3.14159
    g2: ArcOfCircle CenterX=19 CenterY=19 CenterZ=0 NormalX=0 NormalY=0 NormalZ=1 AngleXU=0 Radius=16 StartAngle=1.5708 EndAngle=3.14159
    g3: LineSegment StartX=114 StartY=35 StartZ=0 EndX=19 EndY=35 EndZ=0
    g4: LineSegment StartX=5.21097e-06 StartY=3 StartZ=0 EndX=5.21097e-06 EndY=0 EndZ=0
    g5: LineSegment StartX=3 StartY=0 StartZ=0 EndX=5.21097e-06 EndY=0 EndZ=0
    g6: LineSegment StartX=3 StartY=19 StartZ=0 EndX=3 EndY=0 EndZ=0
    g7: LineSegment StartX=19 StartY=38 StartZ=0 EndX=124 EndY=38 EndZ=0
    g8: Circle CenterX=119 CenterY=35 CenterZ=0 NormalX=0 NormalY=0 NormalZ=1 AngleXU=0 Radius=1
    g9: Circle CenterX=121 CenterY=35 CenterZ=0 NormalX=0 NormalY=0 NormalZ=1 AngleXU=0 Radius=1
    g10: Circle CenterX=121 CenterY=33 CenterZ=0 NormalX=0 NormalY=0 NormalZ=1 AngleXU=0 Radius=1
    g11: BSplineCurve PolesCount=3 KnotsCount=2 Degree=2 IsPeriodic=0
    g12: GeomPoint X=119 Y=35 Z=0
    g13: GeomPoint X=121 Y=33 Z=0
    g14: LineSegment StartX=119 StartY=35 StartZ=0 EndX=114 EndY=35 EndZ=0
    g15: ArcOfCircle CenterX=105 CenterY=19 CenterZ=0 NormalX=0 NormalY=0 NormalZ=1 AngleXU=0 Radius=16 StartAngle=5.60905 EndAngle=6.28319
    g16: LineSegment StartX=121 StartY=33 StartZ=0 EndX=121 EndY=19 EndZ=0
    g17: LineSegment StartX=117.5 StartY=9.01251 StartZ=0 EndX=121.163 EndY=9.0125 EndZ=0
    g18: ArcOfCircle CenterX=105 CenterY=19 CenterZ=0 NormalX=0 NormalY=0 NormalZ=1 AngleXU=0 Radius=20.6155 StartAngle=5.7297 EndAngle=6.28319
    g19: LineSegment StartX=121.163 StartY=9.0125 StartZ=0 EndX=122.538 EndY=8.16329 EndZ=0
    g20: LineSegment StartX=124 StartY=38 StartZ=0 EndX=125.616 EndY=38 EndZ=0
    g21: LineSegment StartX=125.616 StartY=19 StartZ=0 EndX=125.616 EndY=38 EndZ=0
  constraints (50):
    c: Vertical(g0)
    c: Block(g0)
    c: Coincident(g1,g0)
    c: Block(g1)
    c: Coincident(g2,g1)
    c: Block(g2)
    c: Coincident(g3,g2)
    c: Horizontal(g3)
    c: Tangent(g3,g2)
    c: Coincident(g4,g0)
    c: Distance(g4) = 3
    c: Vertical(g4)
    c: Coincident(g5,g4)
    c: Horizontal(g5)
    c: Coincident(g6,g2)
    c: Coincident(g6,g5)
    c: Vertical(g6)
    c: Horizontal(g7)
    c: Distance(g7) = 105
    c: Coincident(g7,g1)
    c: Block(g3)
    c: Weight(g8) = 1
    c: Equal(g8,g9)
    c: Equal(g8,g10)
    c: InternalAlignment(g8,g11)
    c: InternalAlignment(g9,g11)
    c: InternalAlignment(g10,g11)
    c: InternalAlignment(g12,g11)
    c: InternalAlignment(g13,g11)
    c: Block(g11)
    c: Coincident(g14,g11)
    c: Coincident(g14,g3)
    c: Horizontal(g14)
    c: Block(g15)
    c: Coincident(g16,g11)
    c: Coincident(g16,g15)
    c: Vertical(g16)
    c: Distance(g16) = 14
    c: Coincident(g17,g15)
    c: Block(g18)
    c: Coincident(g19,g18)
    c: Coincident(g20,g7)
    c: Horizontal(g20)
    c: Vertical(g21)
    c: Coincident(g20,g21)
    c: Block(g20)
    c: Block(g21)
    c: Block(g19)
    c: Block(g17)
    c: Distance(g20) = 1.61553
FEATURE [Part::Extrusion] Extrude044
  Base = -> Sketch053
  Dir = (0,0,1)
  DirMode = 2
  FaceMakerClass = Part::FaceMakerBullseye
  LengthFwd = 72
  LengthRev = 0
  Solid = true
  Symmetric = false
FEATURE [Part::Fillet] Fillet036  label="top018"
  Base = -> Extrude044
  Edges = 1 edges r=2: [Edge41]
FEATURE [Sketcher::SketchObject] Sketch054
  FullyConstrained = false
  Placement = pos=(0,0,0) rot=(1,0,0;1.5708rad)
  sketch-geometry (24):
    g0: ArcOfCircle CenterX=-4 CenterY=-10.5 CenterZ=0 NormalX=0 NormalY=0 NormalZ=1 AngleXU=0 Radius=1.5 StartAngle=6e-16 EndAngle=3.14159
    g1: ArcOfCircle CenterX=-34.2 CenterY=-10.5 CenterZ=0 NormalX=0 NormalY=0 NormalZ=1 AngleXU=0 Radius=1.5 StartAngle=0 EndAngle=3.14159
    g2: ArcOfCircle CenterX=-34.2 CenterY=-27.7 CenterZ=0 NormalX=0 NormalY=0 NormalZ=1 AngleXU=0 Radius=1.5 StartAngle=3.14159 EndAngle=6.28319
    g3: ArcOfCircle CenterX=-4 CenterY=-27.7 CenterZ=0 NormalX=0 NormalY=0 NormalZ=1 AngleXU=0 Radius=1.5 StartAngle=3.1416 EndAngle=6.28319
    g4: ArcOfCircle CenterX=-10 CenterY=-4.3 CenterZ=0 NormalX=0 NormalY=0 NormalZ=1 AngleXU=0 Radius=1.5 StartAngle=2e-16 EndAngle=3.14159
    g5: ArcOfCircle CenterX=-16.1 CenterY=-1.8 CenterZ=0 NormalX=0 NormalY=0 NormalZ=1 AngleXU=0 Radius=1.5 StartAngle=5e-16 EndAngle=3.14159
    g6: ArcOfCircle CenterX=-22.1 CenterY=-1.8 CenterZ=0 NormalX=0 NormalY=0 NormalZ=1 AngleXU=0 Radius=1.5 StartAngle=5e-16 EndAngle=3.14159
    g7: ArcOfCircle CenterX=-28.2 CenterY=-4.3 CenterZ=0 NormalX=0 NormalY=0 NormalZ=1 AngleXU=0 Radius=1.5 StartAngle=2e-16 EndAngle=3.14159
    g8: ArcOfCircle CenterX=-10 CenterY=-33.9 CenterZ=0 NormalX=0 NormalY=0 NormalZ=1 AngleXU=0 Radius=1.5 StartAngle=3.14159 EndAngle=6.28319
    g9: ArcOfCircle CenterX=-16.1 CenterY=-36.4 CenterZ=0 NormalX=0 NormalY=0 NormalZ=1 AngleXU=0 Radius=1.5 StartAngle=3.14159 EndAngle=6.28319
    g10: ArcOfCircle CenterX=-22.1 CenterY=-36.4 CenterZ=0 NormalX=0 NormalY=0 NormalZ=1 AngleXU=0 Radius=1.5 StartAngle=3.14159 EndAngle=6.28319
    g11: ArcOfCircle CenterX=-28.2 CenterY=-33.9 CenterZ=0 NormalX=0 NormalY=0 NormalZ=1 AngleXU=0 Radius=1.5 StartAngle=3.14159 EndAngle=6.28319
    g12: LineSegment StartX=-35.7 StartY=-10.5 StartZ=0 EndX=-35.7 EndY=-27.7 EndZ=0
    g13: LineSegment StartX=-32.7 StartY=-10.5 StartZ=0 EndX=-32.7 EndY=-27.7 EndZ=0
    g14: LineSegment StartX=-29.7 StartY=-33.9 StartZ=0 EndX=-29.7 EndY=-4.3 EndZ=0
    g15: LineSegment StartX=-26.7 StartY=-33.9 StartZ=0 EndX=-26.7 EndY=-4.3 EndZ=0
    g16: LineSegment StartX=-2.5 StartY=-10.5 StartZ=0 EndX=-2.5 EndY=-27.7 EndZ=0
    g17: LineSegment StartX=-8.5 StartY=-4.3 StartZ=0 EndX=-8.5 EndY=-33.9 EndZ=0
    g18: LineSegment StartX=-5.5 StartY=-10.5 StartZ=0 EndX=-5.5 EndY=-27.7 EndZ=0
    g19: LineSegment StartX=-11.5 StartY=-4.3 StartZ=0 EndX=-11.5 EndY=-33.9 EndZ=0
    g20: LineSegment StartX=-14.6 StartY=-1.8 StartZ=0 EndX=-14.6 EndY=-36.4 EndZ=0
    g21: LineSegment StartX=-17.6 StartY=-1.8 StartZ=0 EndX=-17.6 EndY=-36.4 EndZ=0
    g22: LineSegment StartX=-20.6 StartY=-36.4 StartZ=0 EndX=-20.6 EndY=-1.8 EndZ=0
    g23: LineSegment StartX=-23.6 StartY=-1.8 StartZ=0 EndX=-23.6 EndY=-36.4 EndZ=0
  constraints (48):
    c: Block(g0)
    c: Block(g1)
    c: Block(g2)
    c: Block(g3)
    c: Block(g4)
    c: Block(g5)
    c: Block(g6)
    c: Block(g7)
    c: Block(g8)
    c: Block(g9)
    c: Block(g10)
    c: Block(g11)
    c: Coincident(g12,g1)
    c: Coincident(g12,g2)
    c: Vertical(g12)
    c: Coincident(g13,g1)
    c: Coincident(g13,g2)
    c: Vertical(g13)
    c: Coincident(g14,g11)
    c: Coincident(g14,g7)
    c: Vertical(g14)
    c: Coincident(g15,g11)
    c: Coincident(g15,g7)
    c: Vertical(g15)
    c: Coincident(g16,g0)
    c: Coincident(g16,g3)
    c: Vertical(g16)
    c: Coincident(g17,g4)
    c: Coincident(g17,g8)
    c: Vertical(g17)
    c: Coincident(g18,g0)
    c: Coincident(g18,g3)
    c: Vertical(g18)
    c: Coincident(g19,g4)
    c: Coincident(g19,g8)
    c: Vertical(g19)
    c: Coincident(g20,g5)
    c: Coincident(g20,g9)
    c: Vertical(g20)
    c: Coincident(g21,g5)
    c: Coincident(g21,g9)
    c: Vertical(g21)
    c: Coincident(g22,g10)
    c: Coincident(g22,g6)
    c: Vertical(g22)
    c: Coincident(g23,g6)
    c: Coincident(g23,g10)
    c: Vertical(g23)
FEATURE [Part::Extrusion] Extrude045  label="removeToCreateFanGrillHoles003"
  Base = -> Sketch054
  Dir = (0,-1,6e-16)
  DirMode = 2
  FaceMakerClass = Part::FaceMakerBullseye
  LengthFwd = 10
  LengthRev = 0
  Placement = pos=(65.4,44,54.82) rot=(0,0,1;0rad)
  Solid = true
  Symmetric = false
FEATURE [Part::Feature] Face105 .. Face108  x4 (patterned run collapsed; names and placements below)
  shape: bbox 3.5 x 17.8 x 2e-07 mm, 1 faces, 0 solids (baked)
FEATURE [Part::Revolution] Revolve113  label="removeToCreateScrewAndThreadedInsertHole041"
  Angle = 360
  Axis = (0,1,0)
  Base = (0,0,0)
  FaceMakerClass = Part::FaceMakerBullseye
  Placement = pos=(62.3,30.3,19.7) rot=(0,0,1;0rad)
  Solid = false
  Source = -> Face105
  Symmetric = false
FEATURE [Part::Revolution] Revolve114  label="removeToCreateScrewAndThreadedInsertHole042"
  Angle = 360
  Axis = (0,1,0)
  Base = (0,0,0)
  FaceMakerClass = Part::FaceMakerBullseye
  Placement = pos=(62.3,30.3,51.7) rot=(0,0,1;0rad)
  Solid = false
  Source = -> Face106
  Symmetric = false
FEATURE [Part::Revolution] Revolve115  label="removeToCreateScrewAndThreadedInsertHole043"
  Angle = 360
  Axis = (0,1,0)
  Base = (0,0,0)
  FaceMakerClass = Part::FaceMakerBullseye
  Placement = pos=(30.3,30.3,19.7) rot=(0,0,1;0rad)
  Solid = false
  Source = -> Face107
  Symmetric = false
FEATURE [Part::Revolution] Revolve116  label="removeToCreateScrewAndThreadedInsertHole044"
  Angle = 360
  Axis = (0,1,0)
  Base = (0,0,0)
  FaceMakerClass = Part::FaceMakerBullseye
  Placement = pos=(30.3,30.3,51.7) rot=(0,0,1;0rad)
  Solid = false
  Source = -> Face108
  Symmetric = false
FEATURE [Part::MultiFuse] Fusion083  label="createThreadedInsertHolesForFan004"
  Shapes = -> [Revolve113,Revolve114,Revolve115,Revolve116]
FEATURE [Part::Box] Box024  label="removeToCreteHoleForPlugHousing026"
  AttacherType = Attacher::AttachEngine3D
  Height = 28.6
  Length = 10
  Placement = pos=(-2,0,21.7) rot=(0,0,1;0rad)
  Width = 19
FEATURE [Part::Cylinder] Cylinder038  label="removeToCreteHoleForPlugHousing027"
  Angle = 360
  AttacherType = Attacher::AttachEngine3D
  Height = 20
  Placement = pos=(-2,19,36) rot=(0,1,0;1.5708rad)
  Radius = 14.3
FEATURE [Part::MultiFuse] Fusion084  label="removeToCreteHoleForPlugHousing028"
  Shapes = -> [Box024,Cylinder038]
FEATURE [Part::Cylinder] Cylinder039
  Angle = 360
  AttacherType = Attacher::AttachEngine3D
  Height = 20
  Placement = pos=(0,0,36.15) rot=(0,0,1;0rad)
  Radius = 14.3
FEATURE [Part::Cylinder] Cylinder040
  Angle = 360
  AttacherType = Attacher::AttachEngine3D
  Height = 10
  Placement = pos=(0,0,36.15) rot=(0,0,1;0rad)
  Radius = 4
FEATURE [Part::Box] Box025  label="removeToCreteHoleForPlugHousing030"
  AttacherType = Attacher::AttachEngine3D
  Height = 28.6
  Length = 20
  Placement = pos=(106.15,0,21.7) rot=(0,0,1;0rad)
  Width = 19
FEATURE [Part::MultiFuse] Fusion086  label="removeToCreteHoleForPlugHousing031"
  Placement = pos=(70,19,36) rot=(0,1,0;1.5708rad)
  Shapes = -> [Cylinder039,Cylinder040]
FEATURE [Part::MultiFuse] Fusion085  label="removeToCreteHoleForPlugHousing029"
  Shapes = -> [Box025,Fusion086]
FEATURE [Sketcher::SketchObject] Sketch055
  FullyConstrained = true
  Placement = pos=(117,19,0) rot=(0.57735,0.57735,0.57735;2.0944rad)
  sketch-geometry (48):
    g0: LineSegment StartX=-49.19 StartY=69.25 StartZ=0 EndX=-49.19 EndY=66.25 EndZ=0
    g1: LineSegment StartX=-49.19 StartY=63.5 StartZ=0 EndX=-49.19 EndY=60.5 EndZ=0
    g2: LineSegment StartX=-49.19 StartY=57.75 StartZ=0 EndX=-49.19 EndY=54.75 EndZ=0
    g3: LineSegment StartX=-49.19 StartY=52 StartZ=0 EndX=-49.19 EndY=49 EndZ=0
    g4: LineSegment StartX=-49.19 StartY=46.25 StartZ=0 EndX=-49.19 EndY=43.25 EndZ=0
    g5: LineSegment StartX=-49.19 StartY=40.5 StartZ=0 EndX=-49.19 EndY=37.5 EndZ=0
    g6: LineSegment StartX=-49.19 StartY=34.5 StartZ=0 EndX=-49.19 EndY=31.5 EndZ=0
    g7: LineSegment StartX=-49.19 StartY=28.75 StartZ=0 EndX=-49.19 EndY=25.75 EndZ=0
    g8: LineSegment StartX=-49.19 StartY=23 StartZ=0 EndX=-49.19 EndY=20 EndZ=0
    g9: LineSegment StartX=-49.19 StartY=17.25 StartZ=0 EndX=-49.19 EndY=14.25 EndZ=0
    g10: LineSegment StartX=-49.19 StartY=11.5 StartZ=0 EndX=-49.19 EndY=8.5 EndZ=0
    g11: LineSegment StartX=-49.19 StartY=5.75 StartZ=0 EndX=-49.19 EndY=2.75 EndZ=0
    g12: ArcOfCircle CenterX=-1.5 CenterY=67.75 CenterZ=0 NormalX=0 NormalY=0 NormalZ=1 AngleXU=0 Radius=1.5 StartAngle=4.71239 EndAngle=7.85398
    g13: ArcOfCircle CenterX=-1.5 CenterY=62 CenterZ=0 NormalX=0 NormalY=0 NormalZ=1 AngleXU=0 Radius=1.5 StartAngle=4.71239 EndAngle=7.85398
    g14: ArcOfCircle CenterX=-1.5 CenterY=56.25 CenterZ=0 NormalX=0 NormalY=0 NormalZ=1 AngleXU=0 Radius=1.5 StartAngle=4.71239 EndAngle=7.85398
    g15: ArcOfCircle CenterX=-11.49 CenterY=50.5 CenterZ=0 NormalX=0 NormalY=0 NormalZ=1 AngleXU=0 Radius=1.5 StartAngle=4.71239 EndAngle=7.85398
    g16: ArcOfCircle CenterX=-16.28 CenterY=44.75 CenterZ=0 NormalX=0 NormalY=0 NormalZ=1 AngleXU=0 Radius=1.5 StartAngle=4.71239 EndAngle=7.85398
    g17: ArcOfCircle CenterX=-18.2337 CenterY=39 CenterZ=0 NormalX=0 NormalY=0 NormalZ=1 AngleXU=0 Radius=1.5 StartAngle=4.71485 EndAngle=7.85398
    g18: ArcOfCircle CenterX=-16.2837 CenterY=27.25 CenterZ=0 NormalX=0 NormalY=0 NormalZ=1 AngleXU=0 Radius=1.5 StartAngle=4.71485 EndAngle=7.85398
    g19: ArcOfCircle CenterX=-18.2337 CenterY=33 CenterZ=0 NormalX=0 NormalY=0 NormalZ=1 AngleXU=0 Radius=1.5 StartAngle=4.71485 EndAngle=7.85398
    g20: ArcOfCircle CenterX=-11.49 CenterY=21.5 CenterZ=0 NormalX=0 NormalY=0 NormalZ=1 AngleXU=0 Radius=1.5 StartAngle=4.71239 EndAngle=7.85398
    g21: ArcOfCircle CenterX=-1.5 CenterY=4.25 CenterZ=0 NormalX=0 NormalY=0 NormalZ=1 AngleXU=0 Radius=1.5 StartAngle=4.71239 EndAngle=7.85398
    g22: ArcOfCircle CenterX=-1.5 CenterY=10 CenterZ=0 NormalX=0 NormalY=0 NormalZ=1 AngleXU=0 Radius=1.5 StartAngle=4.71239 EndAngle=7.85398
    g23: ArcOfCircle CenterX=-1.5 CenterY=15.75 CenterZ=0 NormalX=0 NormalY=0 NormalZ=1 AngleXU=0 Radius=1.5 StartAngle=4.71239 EndAngle=7.85398
    g24: LineSegment StartX=-49.19 StartY=69.25 StartZ=0 EndX=-1.5 EndY=69.25 EndZ=0
    g25: LineSegment StartX=-49.19 StartY=66.25 StartZ=0 EndX=-1.5 EndY=66.25 EndZ=0
    g26: LineSegment StartX=-49.19 StartY=63.5 StartZ=0 EndX=-1.5 EndY=63.5 EndZ=0
    g27: LineSegment StartX=-49.19 StartY=60.5 StartZ=0 EndX=-1.5 EndY=60.5 EndZ=0
    g28: LineSegment StartX=-49.19 StartY=57.75 StartZ=0 EndX=-1.5 EndY=57.75 EndZ=0
    g29: LineSegment StartX=-49.19 StartY=54.75 StartZ=0 EndX=-1.5 EndY=54.75 EndZ=0
    g30: LineSegment StartX=-49.19 StartY=52 StartZ=0 EndX=-11.49 EndY=52 EndZ=0
    g31: LineSegment StartX=-49.19 StartY=49 StartZ=0 EndX=-11.49 EndY=49 EndZ=0
    g32: LineSegment StartX=-49.19 StartY=46.25 StartZ=0 EndX=-16.28 EndY=46.25 EndZ=0
    g33: LineSegment StartX=-49.19 StartY=43.25 StartZ=0 EndX=-16.28 EndY=43.25 EndZ=0
    g34: LineSegment StartX=-49.19 StartY=40.5 StartZ=0 EndX=-18.2337 EndY=40.5 EndZ=0
    g35: LineSegment StartX=-49.19 StartY=37.5 StartZ=0 EndX=-18.23 EndY=37.5 EndZ=0
    g36: LineSegment StartX=-49.19 StartY=34.5 StartZ=0 EndX=-18.2337 EndY=34.5 EndZ=0
    g37: LineSegment StartX=-49.19 StartY=31.5 StartZ=0 EndX=-18.23 EndY=31.5 EndZ=0
    g38: LineSegment StartX=-49.19 StartY=28.75 StartZ=0 EndX=-16.2837 EndY=28.75 EndZ=0
    g39: LineSegment StartX=-49.19 StartY=25.75 StartZ=0 EndX=-16.28 EndY=25.75 EndZ=0
    g40: LineSegment StartX=-49.19 StartY=23 StartZ=0 EndX=-11.49 EndY=23 EndZ=0
    g41: LineSegment StartX=-49.19 StartY=20 StartZ=0 EndX=-11.49 EndY=20 EndZ=0
    g42: LineSegment StartX=-49.19 StartY=17.25 StartZ=0 EndX=-1.5 EndY=17.25 EndZ=0
    g43: LineSegment StartX=-49.19 StartY=14.25 StartZ=0 EndX=-1.5 EndY=14.25 EndZ=0
    g44: LineSegment StartX=-49.19 StartY=11.5 StartZ=0 EndX=-1.5 EndY=11.5 EndZ=0
    g45: LineSegment StartX=-49.19 StartY=8.5 StartZ=0 EndX=-1.5 EndY=8.5 EndZ=0
    g46: LineSegment StartX=-49.19 StartY=5.75 StartZ=0 EndX=-1.5 EndY=5.75 EndZ=0
    g47: LineSegment StartX=-49.19 StartY=2.75 StartZ=0 EndX=-1.5 EndY=2.75 EndZ=0
  constraints (120):
    c: Vertical(g0)
    c: Distance(g0) = 3
    c: Block(g0)
    c: Vertical(g1)
    c: Distance(g1) = 3
    c: Vertical(g2)
    c: Equal(g0,g2) = 3
    c: Block(g2)
    c: Vertical(g3)
    c: Equal(g1,g3) = 3
    c: Vertical(g4)
    c: Equal(g0,g4) = 3
    c: Block(g4)
    c: Vertical(g5)
    c: Equal(g1,g5) = 3
    c: Vertical(g6)
    c: Equal(g0,g6) = 3
    c: Block(g6)
    c: Vertical(g7)
    c: Equal(g1,g7) = 3
    c: Vertical(g8)
    c: Equal(g0,g8) = 3
    c: Block(g8)
    c: Vertical(g9)
    c: Equal(g1,g9) = 3
    c: Vertical(g10)
    c: Equal(g0,g10) = 3
    c: Block(g10)
    c: Vertical(g11)
    c: Equal(g1,g11) = 3
    c: Block(g12)
    c: Block(g13)
    c: Block(g14)
    c: Block(g15)
    c: Block(g16)
    c: Block(g17)
    c: Block(g18)
    c: Block(g19)
    c: Block(g20)
    c: Block(g21)
    c: Block(g22)
    c: Block(g23)
    c: Block(g11)
    c: Block(g9)
    c: Block(g7)
    c: Block(g5)
    c: Block(g3)
    c: Block(g1)
    c: Coincident(g24,g0)
    c: Coincident(g24,g12)
    c: Horizontal(g24)
    c: Coincident(g25,g0)
    c: Coincident(g25,g12)
    c: Horizontal(g25)
    c: Coincident(g26,g1)
    c: Coincident(g26,g13)
    c: Horizontal(g26)
    c: Coincident(g27,g1)
    c: Coincident(g27,g13)
    c: Horizontal(g27)
    c: Coincident(g28,g2)
    c: Coincident(g28,g14)
    c: Horizontal(g28)
    c: Coincident(g29,g2)
    c: Coincident(g29,g14)
    c: Horizontal(g29)
    c: Coincident(g30,g3)
    c: Coincident(g30,g15)
    c: Horizontal(g30)
    c: Coincident(g31,g3)
    c: Coincident(g31,g15)
    c: Horizontal(g31)
    c: Coincident(g32,g4)
    c: Coincident(g32,g16)
    c: Horizontal(g32)
    c: Coincident(g33,g4)
    c: Coincident(g33,g16)
    c: Horizontal(g33)
    c: Coincident(g34,g5)
    c: Coincident(g34,g17)
    c: Horizontal(g34)
    c: Coincident(g35,g5)
    c: Coincident(g35,g17)
    c: Horizontal(g35)
    c: Coincident(g36,g6)
    c: Coincident(g36,g19)
    c: Horizontal(g36)
    c: Coincident(g37,g6)
    c: Coincident(g37,g19)
    c: Horizontal(g37)
    c: Coincident(g38,g7)
    c: Coincident(g38,g18)
    c: Horizontal(g38)
    c: Coincident(g39,g7)
    c: Coincident(g39,g18)
    c: Horizontal(g39)
    c: Coincident(g40,g8)
    c: Coincident(g40,g20)
    c: Horizontal(g40)
    c: Coincident(g41,g8)
    c: Coincident(g41,g20)
    c: Horizontal(g41)
    c: Coincident(g42,g9)
    c: Coincident(g42,g23)
    c: Horizontal(g42)
    c: Coincident(g43,g9)
    c: Coincident(g43,g23)
    c: Horizontal(g43)
    c: Coincident(g44,g10)
    c: Coincident(g44,g22)
    c: Horizontal(g44)
    c: Coincident(g45,g10)
    c: Coincident(g45,g22)
    c: Horizontal(g45)
    c: Coincident(g46,g11)
    c: Coincident(g46,g21)
    c: Horizontal(g46)
    c: Coincident(g47,g11)
    c: Coincident(g47,g21)
    c: Horizontal(g47)
FEATURE [Part::Extrusion] Extrude046
  Base = -> Sketch055
  Dir = (1,0,0)
  DirMode = 2
  FaceMakerClass = Part::FaceMakerBullseye
  LengthFwd = 23
  LengthRev = 0
  Placement = pos=(-19,0,0) rot=(0,0,1;0rad)
  Solid = true
  Symmetric = false
FEATURE [Part::Fillet] Fillet038  label="removeToCreateVentalationHoles001"
  Base = -> Extrude046
  Edges = <same value as first occurrence — deduplicated (x6 in doc)>
  Placement = pos=(7,0,0) rot=(0,0,1;0rad)
FEATURE [Sketcher::SketchObject] Sketch056  label="topSketch014"
  FullyConstrained = true
  sketch-geometry (22):
    g0: LineSegment StartX=5.21097e-06 StartY=3 StartZ=0 EndX=5.21097e-06 EndY=19 EndZ=0
    g1: ArcOfCircle CenterX=19 CenterY=19 CenterZ=0 NormalX=0 NormalY=0 NormalZ=1 AngleXU=0 Radius=19 StartAngle=1.5708 EndAngle=3.14159
    g2: ArcOfCircle CenterX=19 CenterY=19 CenterZ=0 NormalX=0 NormalY=0 NormalZ=1 AngleXU=0 Radius=16 StartAngle=1.5708 EndAngle=3.14159
    g3: LineSegment StartX=114 StartY=35 StartZ=0 EndX=19 EndY=35 EndZ=0
    g4: LineSegment StartX=5.21097e-06 StartY=3 StartZ=0 EndX=5.21097e-06 EndY=0 EndZ=0
    g5: LineSegment StartX=3 StartY=0 StartZ=0 EndX=5.21097e-06 EndY=0 EndZ=0
    g6: LineSegment StartX=3 StartY=19 StartZ=0 EndX=3 EndY=0 EndZ=0
    g7: LineSegment StartX=19 StartY=38 StartZ=0 EndX=124 EndY=38 EndZ=0
    g8: Circle CenterX=119 CenterY=35 CenterZ=0 NormalX=0 NormalY=0 NormalZ=1 AngleXU=0 Radius=1
    g9: Circle CenterX=121 CenterY=35 CenterZ=0 NormalX=0 NormalY=0 NormalZ=1 AngleXU=0 Radius=1
    g10: Circle CenterX=121 CenterY=33 CenterZ=0 NormalX=0 NormalY=0 NormalZ=1 AngleXU=0 Radius=1
    g11: BSplineCurve PolesCount=3 KnotsCount=2 Degree=2 IsPeriodic=0
    g12: GeomPoint X=119 Y=35 Z=0
    g13: GeomPoint X=121 Y=33 Z=0
    g14: LineSegment StartX=119 StartY=35 StartZ=0 EndX=114 EndY=35 EndZ=0
    g15: ArcOfCircle CenterX=105 CenterY=19 CenterZ=0 NormalX=0 NormalY=0 NormalZ=1 AngleXU=0 Radius=16 StartAngle=5.60905 EndAngle=6.28319
    g16: LineSegment StartX=121 StartY=33 StartZ=0 EndX=121 EndY=19 EndZ=0
    g17: LineSegment StartX=117.5 StartY=9.01251 StartZ=0 EndX=121.163 EndY=9.0125 EndZ=0
    g18: ArcOfCircle CenterX=105 CenterY=19 CenterZ=0 NormalX=0 NormalY=0 NormalZ=1 AngleXU=0 Radius=20.6155 StartAngle=5.7297 EndAngle=6.28319
    g19: LineSegment StartX=121.163 StartY=9.0125 StartZ=0 EndX=122.538 EndY=8.16329 EndZ=0
    g20: LineSegment StartX=124 StartY=38 StartZ=0 EndX=125.616 EndY=38 EndZ=0
    g21: LineSegment StartX=125.616 StartY=19 StartZ=0 EndX=125.616 EndY=38 EndZ=0
  constraints (49):
    c: Vertical(g0)
    c: Block(g0)
    c: Coincident(g1,g0)
    c: Block(g1)
    c: Coincident(g2,g1)
    c: Block(g2)
    c: Coincident(g3,g2)
    c: Horizontal(g3)
    c: Tangent(g3,g2)
    c: Coincident(g4,g0)
    c: Distance(g4) = 3
    c: Vertical(g4)
    c: Coincident(g5,g4)
    c: Horizontal(g5)
    c: Coincident(g6,g2)
    c: Coincident(g6,g5)
    c: Vertical(g6)
    c: Horizontal(g7)
    c: Distance(g7) = 105
    c: Coincident(g7,g1)
    c: Block(g3)
    c: Weight(g8) = 1
    c: Equal(g8,g9)
    c: Equal(g8,g10)
    c: InternalAlignment(g8,g11)
    c: InternalAlignment(g9,g11)
    c: InternalAlignment(g10,g11)
    c: InternalAlignment(g12,g11)
    c: InternalAlignment(g13,g11)
    c: Block(g11)
    c: Coincident(g14,g11)
    c: Coincident(g14,g3)
    c: Horizontal(g14)
    c: Block(g15)
    c: Coincident(g16,g11)
    c: Coincident(g16,g15)
    c: Vertical(g16)
    c: Distance(g16) = 14
    c: Coincident(g17,g15)
    c: Block(g18)
    c: Coincident(g19,g18)
    c: Coincident(g20,g7)
    c: Horizontal(g20)
    c: Vertical(g21)
    c: Coincident(g20,g21)
    c: Block(g20)
    c: Block(g21)
    c: Block(g19)
    c: Block(g17)
FEATURE [Part::Box] Box026  label="removeToCreteHoleForPlugHousing032"
  AttacherType = Attacher::AttachEngine3D
  Height = 28.6
  Length = 10
  Placement = pos=(-2,0,21.7) rot=(0,0,1;0rad)
  Width = 19
FEATURE [Part::Feature] Face109 .. Face112  x4 (patterned run collapsed; names and placements below)
  shape: bbox 3.5 x 17.8 x 2e-07 mm, 1 faces, 0 solids (baked)
FEATURE [Part::Revolution] Revolve117  label="removeToCreateScrewAndThreadedInsertHole045"
  Angle = 360
  Axis = (0,1,0)
  Base = (0,0,0)
  FaceMakerClass = Part::FaceMakerBullseye
  Placement = pos=(62.3,30.3,19.7) rot=(0,0,1;0rad)
  Solid = false
  Source = -> Face109
  Symmetric = false
FEATURE [Part::Revolution] Revolve118  label="removeToCreateScrewAndThreadedInsertHole046"
  Angle = 360
  Axis = (0,1,0)
  Base = (0,0,0)
  FaceMakerClass = Part::FaceMakerBullseye
  Placement = pos=(62.3,30.3,51.7) rot=(0,0,1;0rad)
  Solid = false
  Source = -> Face110
  Symmetric = false
FEATURE [Part::Revolution] Revolve119  label="removeToCreateScrewAndThreadedInsertHole047"
  Angle = 360
  Axis = (0,1,0)
  Base = (0,0,0)
  FaceMakerClass = Part::FaceMakerBullseye
  Placement = pos=(30.3,30.3,19.7) rot=(0,0,1;0rad)
  Solid = false
  Source = -> Face111
  Symmetric = false
FEATURE [Part::Revolution] Revolve120  label="removeToCreateScrewAndThreadedInsertHole048"
  Angle = 360
  Axis = (0,1,0)
  Base = (0,0,0)
  FaceMakerClass = Part::FaceMakerBullseye
  Placement = pos=(30.3,30.3,51.7) rot=(0,0,1;0rad)
  Solid = false
  Source = -> Face112
  Symmetric = false
FEATURE [Part::MultiFuse] Fusion087  label="createThreadedInsertHolesForFan005"
  Shapes = -> [Revolve117,Revolve118,Revolve119,Revolve120]
FEATURE [Part::Extrusion] Extrude047
  Base = -> Sketch056
  Dir = (0,0,1)
  DirMode = 2
  FaceMakerClass = Part::FaceMakerBullseye
  LengthFwd = 72
  LengthRev = 0
  Solid = true
  Symmetric = false
FEATURE [Part::Fillet] Fillet039  label="top019"
  Base = -> Extrude047
  Edges = 1 edges r=2: [Edge35]
FEATURE [Sketcher::SketchObject] Sketch057
  FullyConstrained = false
  Placement = pos=(0,0,0) rot=(1,0,0;1.5708rad)
  sketch-geometry (24):
    g0: ArcOfCircle CenterX=-4 CenterY=-10.5 CenterZ=0 NormalX=0 NormalY=0 NormalZ=1 AngleXU=0 Radius=1.5 StartAngle=6e-16 EndAngle=3.14159
    g1: ArcOfCircle CenterX=-34.2 CenterY=-10.5 CenterZ=0 NormalX=0 NormalY=0 NormalZ=1 AngleXU=0 Radius=1.5 StartAngle=0 EndAngle=3.14159
    g2: ArcOfCircle CenterX=-34.2 CenterY=-27.7 CenterZ=0 NormalX=0 NormalY=0 NormalZ=1 AngleXU=0 Radius=1.5 StartAngle=3.14159 EndAngle=6.28319
    g3: ArcOfCircle CenterX=-4 CenterY=-27.7 CenterZ=0 NormalX=0 NormalY=0 NormalZ=1 AngleXU=0 Radius=1.5 StartAngle=3.1416 EndAngle=6.28319
    g4: ArcOfCircle CenterX=-10 CenterY=-4.3 CenterZ=0 NormalX=0 NormalY=0 NormalZ=1 AngleXU=0 Radius=1.5 StartAngle=2e-16 EndAngle=3.14159
    g5: ArcOfCircle CenterX=-16.1 CenterY=-1.8 CenterZ=0 NormalX=0 NormalY=0 NormalZ=1 AngleXU=0 Radius=1.5 StartAngle=5e-16 EndAngle=3.14159
    g6: ArcOfCircle CenterX=-22.1 CenterY=-1.8 CenterZ=0 NormalX=0 NormalY=0 NormalZ=1 AngleXU=0 Radius=1.5 StartAngle=5e-16 EndAngle=3.14159
    g7: ArcOfCircle CenterX=-28.2 CenterY=-4.3 CenterZ=0 NormalX=0 NormalY=0 NormalZ=1 AngleXU=0 Radius=1.5 StartAngle=2e-16 EndAngle=3.14159
    g8: ArcOfCircle CenterX=-10 CenterY=-33.9 CenterZ=0 NormalX=0 NormalY=0 NormalZ=1 AngleXU=0 Radius=1.5 StartAngle=3.14159 EndAngle=6.28319
    g9: ArcOfCircle CenterX=-16.1 CenterY=-36.4 CenterZ=0 NormalX=0 NormalY=0 NormalZ=1 AngleXU=0 Radius=1.5 StartAngle=3.14159 EndAngle=6.28319
    g10: ArcOfCircle CenterX=-22.1 CenterY=-36.4 CenterZ=0 NormalX=0 NormalY=0 NormalZ=1 AngleXU=0 Radius=1.5 StartAngle=3.14159 EndAngle=6.28319
    g11: ArcOfCircle CenterX=-28.2 CenterY=-33.9 CenterZ=0 NormalX=0 NormalY=0 NormalZ=1 AngleXU=0 Radius=1.5 StartAngle=3.14159 EndAngle=6.28319
    g12: LineSegment StartX=-35.7 StartY=-10.5 StartZ=0 EndX=-35.7 EndY=-27.7 EndZ=0
    g13: LineSegment StartX=-32.7 StartY=-10.5 StartZ=0 EndX=-32.7 EndY=-27.7 EndZ=0
    g14: LineSegment StartX=-29.7 StartY=-33.9 StartZ=0 EndX=-29.7 EndY=-4.3 EndZ=0
    g15: LineSegment StartX=-26.7 StartY=-33.9 StartZ=0 EndX=-26.7 EndY=-4.3 EndZ=0
    g16: LineSegment StartX=-2.5 StartY=-10.5 StartZ=0 EndX=-2.5 EndY=-27.7 EndZ=0
    g17: LineSegment StartX=-8.5 StartY=-4.3 StartZ=0 EndX=-8.5 EndY=-33.9 EndZ=0
    g18: LineSegment StartX=-5.5 StartY=-10.5 StartZ=0 EndX=-5.5 EndY=-27.7 EndZ=0
    g19: LineSegment StartX=-11.5 StartY=-4.3 StartZ=0 EndX=-11.5 EndY=-33.9 EndZ=0
    g20: LineSegment StartX=-14.6 StartY=-1.8 StartZ=0 EndX=-14.6 EndY=-36.4 EndZ=0
    g21: LineSegment StartX=-17.6 StartY=-1.8 StartZ=0 EndX=-17.6 EndY=-36.4 EndZ=0
    g22: LineSegment StartX=-20.6 StartY=-36.4 StartZ=0 EndX=-20.6 EndY=-1.8 EndZ=0
    g23: LineSegment StartX=-23.6 StartY=-1.8 StartZ=0 EndX=-23.6 EndY=-36.4 EndZ=0
  constraints (48):
    c: Block(g0)
    c: Block(g1)
    c: Block(g2)
    c: Block(g3)
    c: Block(g4)
    c: Block(g5)
    c: Block(g6)
    c: Block(g7)
    c: Block(g8)
    c: Block(g9)
    c: Block(g10)
    c: Block(g11)
    c: Coincident(g12,g1)
    c: Coincident(g12,g2)
    c: Vertical(g12)
    c: Coincident(g13,g1)
    c: Coincident(g13,g2)
    c: Vertical(g13)
    c: Coincident(g14,g11)
    c: Coincident(g14,g7)
    c: Vertical(g14)
    c: Coincident(g15,g11)
    c: Coincident(g15,g7)
    c: Vertical(g15)
    c: Coincident(g16,g0)
    c: Coincident(g16,g3)
    c: Vertical(g16)
    c: Coincident(g17,g4)
    c: Coincident(g17,g8)
    c: Vertical(g17)
    c: Coincident(g18,g0)
    c: Coincident(g18,g3)
    c: Vertical(g18)
    c: Coincident(g19,g4)
    c: Coincident(g19,g8)
    c: Vertical(g19)
    c: Coincident(g20,g5)
    c: Coincident(g20,g9)
    c: Vertical(g20)
    c: Coincident(g21,g5)
    c: Coincident(g21,g9)
    c: Vertical(g21)
    c: Coincident(g22,g10)
    c: Coincident(g22,g6)
    c: Vertical(g22)
    c: Coincident(g23,g6)
    c: Coincident(g23,g10)
    c: Vertical(g23)
FEATURE [Part::Extrusion] Extrude048  label="removeToCreateFanGrillHoles004"
  Base = -> Sketch057
  Dir = (0,-1,6e-16)
  DirMode = 2
  FaceMakerClass = Part::FaceMakerBullseye
  LengthFwd = 10
  LengthRev = 0
  Placement = pos=(65.4,44,54.82) rot=(0,0,1;0rad)
  Solid = true
  Symmetric = false
FEATURE [Part::Cut] Cut040  label="top021"
  Base = -> Fillet039
  Tool = -> Extrude048
FEATURE [Part::Cylinder] Cylinder041  label="removeToCreteHoleForPlugHousing034"
  Angle = 360
  AttacherType = Attacher::AttachEngine3D
  Height = 20
  Placement = pos=(-2,19,36) rot=(0,1,0;1.5708rad)
  Radius = 14.3
FEATURE [Part::MultiFuse] Fusion089  label="removeToCreteHoleForPlugHousing035"
  Shapes = -> [Box026,Cylinder041]
FEATURE [Part::Cylinder] Cylinder042
  Angle = 360
  AttacherType = Attacher::AttachEngine3D
  Height = 20
  Placement = pos=(0,0,36.15) rot=(0,0,1;0rad)
  Radius = 14.3
FEATURE [Part::Cylinder] Cylinder043
  Angle = 360
  AttacherType = Attacher::AttachEngine3D
  Height = 10
  Placement = pos=(0,0,36.15) rot=(0,0,1;0rad)
  Radius = 4
FEATURE [Part::Box] Box027  label="removeToCreteHoleForPlugHousing036"
  AttacherType = Attacher::AttachEngine3D
  Height = 28.6
  Length = 20
  Placement = pos=(106.15,0,21.7) rot=(0,0,1;0rad)
  Width = 19
FEATURE [Part::Cut] Cut041  label="top022"
  Base = -> Cut040
  Tool = -> Fusion087
FEATURE [Part::Cut] Cut039  label="top020"
  Base = -> Cut041
  Tool = -> Fusion089
FEATURE [Part::MultiFuse] Fusion090  label="removeToCreteHoleForPlugHousing037"
  Placement = pos=(70,19,36) rot=(0,1,0;1.5708rad)
  Shapes = -> [Cylinder042,Cylinder043]
FEATURE [Part::MultiFuse] Fusion088  label="removeToCreteHoleForPlugHousing033"
  Shapes = -> [Box027,Fusion090]
FEATURE [Part::Cut] Cut042  label="removeToCreteHoleForPlugHousing038"
  Base = -> Cut039
  Tool = -> Fusion088
FEATURE [Part::MultiFuse] Fusion091  label="removeFromTop"
  Shapes = -> [Fillet038,Fusion085,Fusion084,Fusion083,Extrude045]
FEATURE [Part::Cut] Cut043  label="REAL TOP ====="
  Base = -> Fillet036
  Tool = -> Fusion091
FEATURE [Part::MultiFuse] Fusion092  label="caseScrewPillarBracket016"
  Shapes = -> [Extrude030,Extrude031,Extrude032,Extrude033,Extrude034,Extrude035,Extrude036,Extrude037,Box013,Box014]
FEATURE [Sketcher::SketchObject] Sketch058  label="topSketch015"
  FullyConstrained = true
  sketch-geometry (20):
    g0: LineSegment StartX=5.21097e-06 StartY=3 StartZ=0 EndX=5.21097e-06 EndY=19 EndZ=0
    g1: ArcOfCircle CenterX=19 CenterY=19 CenterZ=0 NormalX=0 NormalY=0 NormalZ=1 AngleXU=0 Radius=19 StartAngle=1.5708 EndAngle=3.14159
    g2: ArcOfCircle CenterX=19 CenterY=19 CenterZ=0 NormalX=0 NormalY=0 NormalZ=1 AngleXU=0 Radius=16 StartAngle=1.5708 EndAngle=3.14159
    g3: LineSegment StartX=114 StartY=35 StartZ=0 EndX=19 EndY=35 EndZ=0
    g4: LineSegment StartX=5.21097e-06 StartY=3 StartZ=0 EndX=5.21097e-06 EndY=0 EndZ=0
    g5: LineSegment StartX=3 StartY=0 StartZ=0 EndX=5.21097e-06 EndY=0 EndZ=0
    g6: LineSegment StartX=3 StartY=19 StartZ=0 EndX=3 EndY=0 EndZ=0
    g7: LineSegment StartX=19 StartY=38 StartZ=0 EndX=124 EndY=38 EndZ=0
    g8: Circle CenterX=119 CenterY=35 CenterZ=0 NormalX=0 NormalY=0 NormalZ=1 AngleXU=0 Radius=1
    g9: Circle CenterX=121 CenterY=35 CenterZ=0 NormalX=0 NormalY=0 NormalZ=1 AngleXU=0 Radius=1
    g10: Circle CenterX=121 CenterY=33 CenterZ=0 NormalX=0 NormalY=0 NormalZ=1 AngleXU=0 Radius=1
    g11: BSplineCurve PolesCount=3 KnotsCount=2 Degree=2 IsPeriodic=0
    g12: GeomPoint X=119 Y=35 Z=0
    g13: GeomPoint X=121 Y=33 Z=0
    g14: LineSegment StartX=119 StartY=35 StartZ=0 EndX=114 EndY=35 EndZ=0
    g15: ArcOfCircle CenterX=105 CenterY=19 CenterZ=0 NormalX=0 NormalY=0 NormalZ=1 AngleXU=0 Radius=19 StartAngle=5.7297 EndAngle=6.28319
    g16: ArcOfCircle CenterX=105 CenterY=19 CenterZ=0 NormalX=0 NormalY=0 NormalZ=1 AngleXU=0 Radius=16 StartAngle=5.60905 EndAngle=6.28319
    g17: LineSegment StartX=121 StartY=33 StartZ=0 EndX=121 EndY=19 EndZ=0
    g18: LineSegment StartX=124 StartY=38 StartZ=0 EndX=124 EndY=19 EndZ=0
    g19: LineSegment StartX=117.5 StartY=9.01251 StartZ=0 EndX=121.163 EndY=9.0125 EndZ=0
  constraints (46):
    c: Vertical(g0)
    c: Block(g0)
    c: Coincident(g1,g0)
    c: Block(g1)
    c: Coincident(g2,g1)
    c: Block(g2)
    c: Coincident(g3,g2)
    c: Horizontal(g3)
    c: Tangent(g3,g2)
    c: Coincident(g4,g0)
    c: Distance(g4) = 3
    c: Vertical(g4)
    c: Coincident(g5,g4)
    c: Horizontal(g5)
    c: Coincident(g6,g2)
    c: Coincident(g6,g5)
    c: Vertical(g6)
    c: Horizontal(g7)
    c: Distance(g7) = 105
    c: Coincident(g7,g1)
    c: Block(g3)
    c: Weight(g8) = 1
    c: Equal(g8,g9)
    c: Equal(g8,g10)
    c: InternalAlignment(g8,g11)
    c: InternalAlignment(g9,g11)
    c: InternalAlignment(g10,g11)
    c: InternalAlignment(g12,g11)
    c: InternalAlignment(g13,g11)
    c: Block(g11)
    c: Coincident(g14,g11)
    c: Coincident(g14,g3)
    c: Horizontal(g14)
    c: Block(g15)
    c: Coincident(g16,g15)
    c: Block(g16)
    c: Coincident(g17,g11)
    c: Coincident(g17,g16)
    c: Vertical(g17)
    c: Distance(g17) = 14
    c: Coincident(g18,g7)
    c: Coincident(g18,g15)
    c: Vertical(g18)
    c: Distance(g18) = 19
    c: Coincident(g19,g16)
    c: Coincident(g19,g15)
FEATURE [Part::Extrusion] Extrude049  label="top023"
  Base = -> Sketch058
  Dir = (0,0,1)
  DirMode = 2
  FaceMakerClass = Part::FaceMakerBullseye
  LengthFwd = 72
  LengthRev = 0
  Solid = true
  Symmetric = false
FEATURE [Sketcher::SketchObject] Sketch059
  FullyConstrained = true
  MapMode = 3
  Placement = pos=(0,0,0) rot=(1,0,0;1.5708rad)
  Support = -> [Extrude049]
  sketch-geometry (8):
    g0: Circle CenterX=80.351 CenterY=-67.6202 CenterZ=0 NormalX=0 NormalY=0 NormalZ=1 AngleXU=0 Radius=2
    g1: Circle CenterX=80.351 CenterY=-67.6202 CenterZ=0 NormalX=0 NormalY=0 NormalZ=1 AngleXU=0 Radius=3
    g2: Circle CenterX=80.351 CenterY=-4.92017 CenterZ=0 NormalX=0 NormalY=0 NormalZ=1 AngleXU=0 Radius=2
    g3: Circle CenterX=80.351 CenterY=-4.92017 CenterZ=0 NormalX=0 NormalY=0 NormalZ=1 AngleXU=0 Radius=3
    g4: Circle CenterX=23.851 CenterY=-4.92017 CenterZ=0 NormalX=0 NormalY=0 NormalZ=1 AngleXU=0 Radius=2
    g5: Circle CenterX=23.851 CenterY=-4.92017 CenterZ=0 NormalX=0 NormalY=0 NormalZ=1 AngleXU=0 Radius=3
    g6: Circle CenterX=23.851 CenterY=-67.6202 CenterZ=0 NormalX=0 NormalY=0 NormalZ=1 AngleXU=0 Radius=2
    g7: Circle CenterX=23.851 CenterY=-67.6202 CenterZ=0 NormalX=0 NormalY=0 NormalZ=1 AngleXU=0 Radius=3
  constraints (8):
    c: Block(g3)
    c: Block(g2)
    c: Block(g1)
    c: Block(g0)
    c: Block(g6)
    c: Block(g7)
    c: Block(g4)
    c: Block(g5)
FEATURE [Sketcher::SketchObject] Sketch060
  FullyConstrained = true
  MapMode = 3
  Placement = pos=(0,0,0) rot=(1,0,0;1.5708rad)
  Support = -> [Extrude049]
  sketch-geometry (8):
    g0: Circle CenterX=80.351 CenterY=-67.6202 CenterZ=0 NormalX=0 NormalY=0 NormalZ=1 AngleXU=0 Radius=3
    g1: Circle CenterX=80.351 CenterY=-4.92017 CenterZ=0 NormalX=0 NormalY=0 NormalZ=1 AngleXU=0 Radius=3
    g2: Circle CenterX=23.851 CenterY=-4.92017 CenterZ=0 NormalX=0 NormalY=0 NormalZ=1 AngleXU=0 Radius=3
    g3: Circle CenterX=23.851 CenterY=-67.6202 CenterZ=0 NormalX=0 NormalY=0 NormalZ=1 AngleXU=0 Radius=3
    g4: Circle CenterX=23.851 CenterY=-67.6202 CenterZ=0 NormalX=0 NormalY=0 NormalZ=1 AngleXU=0 Radius=5
    g5: Circle CenterX=80.351 CenterY=-67.6202 CenterZ=0 NormalX=0 NormalY=0 NormalZ=1 AngleXU=0 Radius=5
    g6: Circle CenterX=23.851 CenterY=-4.92017 CenterZ=0 NormalX=0 NormalY=0 NormalZ=1 AngleXU=0 Radius=5
    g7: Circle CenterX=80.351 CenterY=-4.92017 CenterZ=0 NormalX=0 NormalY=0 NormalZ=1 AngleXU=0 Radius=5
  constraints (8):
    c: Block(g1)
    c: Block(g0)
    c: Block(g3)
    c: Block(g2)
    c: Block(g5)
    c: Block(g4)
    c: Block(g6)
    c: Block(g7)
FEATURE [Sketcher::SketchObject] Sketch061
  FullyConstrained = true
  MapMode = 3
  Placement = pos=(0,0,0) rot=(1,0,0;1.5708rad)
  sketch-geometry (8):
    g0: Circle CenterX=80.351 CenterY=-67.6202 CenterZ=0 NormalX=0 NormalY=0 NormalZ=1 AngleXU=0 Radius=3
    g1: Circle CenterX=80.351 CenterY=-4.92017 CenterZ=0 NormalX=0 NormalY=0 NormalZ=1 AngleXU=0 Radius=3
    g2: Circle CenterX=23.851 CenterY=-4.92017 CenterZ=0 NormalX=0 NormalY=0 NormalZ=1 AngleXU=0 Radius=3
    g3: Circle CenterX=23.851 CenterY=-67.6202 CenterZ=0 NormalX=0 NormalY=0 NormalZ=1 AngleXU=0 Radius=3
    g4: Circle CenterX=23.851 CenterY=-67.6202 CenterZ=0 NormalX=0 NormalY=0 NormalZ=1 AngleXU=0 Radius=5
    g5: Circle CenterX=80.351 CenterY=-67.6202 CenterZ=0 NormalX=0 NormalY=0 NormalZ=1 AngleXU=0 Radius=5
    g6: Circle CenterX=23.851 CenterY=-4.92017 CenterZ=0 NormalX=0 NormalY=0 NormalZ=1 AngleXU=0 Radius=5
    g7: Circle CenterX=80.351 CenterY=-4.92017 CenterZ=0 NormalX=0 NormalY=0 NormalZ=1 AngleXU=0 Radius=5
  constraints (8):
    c: Block(g1)
    c: Block(g0)
    c: Block(g3)
    c: Block(g2)
    c: Block(g5)
    c: Block(g4)
    c: Block(g6)
    c: Block(g7)
FEATURE [Sketcher::SketchObject] Sketch062  label="topSketch016"
  FullyConstrained = true
  sketch-geometry (20):
    g0: LineSegment StartX=5.21097e-06 StartY=3 StartZ=0 EndX=5.21097e-06 EndY=19 EndZ=0
    g1: ArcOfCircle CenterX=19 CenterY=19 CenterZ=0 NormalX=0 NormalY=0 NormalZ=1 AngleXU=0 Radius=19 StartAngle=1.5708 EndAngle=3.14159
    g2: ArcOfCircle CenterX=19 CenterY=19 CenterZ=0 NormalX=0 NormalY=0 NormalZ=1 AngleXU=0 Radius=16 StartAngle=1.5708 EndAngle=3.14159
    g3: LineSegment StartX=114 StartY=35 StartZ=0 EndX=19 EndY=35 EndZ=0
    g4: LineSegment StartX=5.21097e-06 StartY=3 StartZ=0 EndX=5.21097e-06 EndY=0 EndZ=0
    g5: LineSegment StartX=3 StartY=0 StartZ=0 EndX=5.21097e-06 EndY=0 EndZ=0
    g6: LineSegment StartX=3 StartY=19 StartZ=0 EndX=3 EndY=0 EndZ=0
    g7: LineSegment StartX=19 StartY=38 StartZ=0 EndX=124 EndY=38 EndZ=0
    g8: Circle CenterX=119 CenterY=35 CenterZ=0 NormalX=0 NormalY=0 NormalZ=1 AngleXU=0 Radius=1
    g9: Circle CenterX=121 CenterY=35 CenterZ=0 NormalX=0 NormalY=0 NormalZ=1 AngleXU=0 Radius=1
    g10: Circle CenterX=121 CenterY=33 CenterZ=0 NormalX=0 NormalY=0 NormalZ=1 AngleXU=0 Radius=1
    g11: BSplineCurve PolesCount=3 KnotsCount=2 Degree=2 IsPeriodic=0
    g12: GeomPoint X=119 Y=35 Z=0
    g13: GeomPoint X=121 Y=33 Z=0
    g14: LineSegment StartX=119 StartY=35 StartZ=0 EndX=114 EndY=35 EndZ=0
    g15: ArcOfCircle CenterX=105 CenterY=19 CenterZ=0 NormalX=0 NormalY=0 NormalZ=1 AngleXU=0 Radius=19 StartAngle=5.7297 EndAngle=6.28319
    g16: ArcOfCircle CenterX=105 CenterY=19 CenterZ=0 NormalX=0 NormalY=0 NormalZ=1 AngleXU=0 Radius=16 StartAngle=5.60905 EndAngle=6.28319
    g17: LineSegment StartX=121 StartY=33 StartZ=0 EndX=121 EndY=19 EndZ=0
    g18: LineSegment StartX=124 StartY=38 StartZ=0 EndX=124 EndY=19 EndZ=0
    g19: LineSegment StartX=117.5 StartY=9.01251 StartZ=0 EndX=121.163 EndY=9.0125 EndZ=0
  constraints (46):
    c: Vertical(g0)
    c: Block(g0)
    c: Coincident(g1,g0)
    c: Block(g1)
    c: Coincident(g2,g1)
    c: Block(g2)
    c: Coincident(g3,g2)
    c: Horizontal(g3)
    c: Tangent(g3,g2)
    c: Coincident(g4,g0)
    c: Distance(g4) = 3
    c: Vertical(g4)
    c: Coincident(g5,g4)
    c: Horizontal(g5)
    c: Coincident(g6,g2)
    c: Coincident(g6,g5)
    c: Vertical(g6)
    c: Horizontal(g7)
    c: Distance(g7) = 105
    c: Coincident(g7,g1)
    c: Block(g3)
    c: Weight(g8) = 1
    c: Equal(g8,g9)
    c: Equal(g8,g10)
    c: InternalAlignment(g8,g11)
    c: InternalAlignment(g9,g11)
    c: InternalAlignment(g10,g11)
    c: InternalAlignment(g12,g11)
    c: InternalAlignment(g13,g11)
    c: Block(g11)
    c: Coincident(g14,g11)
    c: Coincident(g14,g3)
    c: Horizontal(g14)
    c: Block(g15)
    c: Coincident(g16,g15)
    c: Block(g16)
    c: Coincident(g17,g11)
    c: Coincident(g17,g16)
    c: Vertical(g17)
    c: Distance(g17) = 14
    c: Coincident(g18,g7)
    c: Coincident(g18,g15)
    c: Vertical(g18)
    c: Distance(g18) = 19
    c: Coincident(g19,g16)
    c: Coincident(g19,g15)
FEATURE [Part::Extrusion] Extrude053  label="top024"
  Base = -> Sketch062
  Dir = (0,0,1)
  DirMode = 2
  FaceMakerClass = Part::FaceMakerBullseye
  LengthFwd = 72
  LengthRev = 0
  Solid = true
  Symmetric = false
FEATURE [Sketcher::SketchObject] Sketch063
  FullyConstrained = true
  MapMode = 3
  Placement = pos=(0,0,0) rot=(1,0,0;1.5708rad)
  Support = -> [Extrude053]
  sketch-geometry (8):
    g0: Circle CenterX=80.351 CenterY=-67.6202 CenterZ=0 NormalX=0 NormalY=0 NormalZ=1 AngleXU=0 Radius=2
    g1: Circle CenterX=80.351 CenterY=-67.6202 CenterZ=0 NormalX=0 NormalY=0 NormalZ=1 AngleXU=0 Radius=3
    g2: Circle CenterX=80.351 CenterY=-4.92017 CenterZ=0 NormalX=0 NormalY=0 NormalZ=1 AngleXU=0 Radius=2
    g3: Circle CenterX=80.351 CenterY=-4.92017 CenterZ=0 NormalX=0 NormalY=0 NormalZ=1 AngleXU=0 Radius=3
    g4: Circle CenterX=23.851 CenterY=-4.92017 CenterZ=0 NormalX=0 NormalY=0 NormalZ=1 AngleXU=0 Radius=2
    g5: Circle CenterX=23.851 CenterY=-4.92017 CenterZ=0 NormalX=0 NormalY=0 NormalZ=1 AngleXU=0 Radius=3
    g6: Circle CenterX=23.851 CenterY=-67.6202 CenterZ=0 NormalX=0 NormalY=0 NormalZ=1 AngleXU=0 Radius=2
    g7: Circle CenterX=23.851 CenterY=-67.6202 CenterZ=0 NormalX=0 NormalY=0 NormalZ=1 AngleXU=0 Radius=3
  constraints (8):
    c: Block(g3)
    c: Block(g2)
    c: Block(g1)
    c: Block(g0)
    c: Block(g6)
    c: Block(g7)
    c: Block(g4)
    c: Block(g5)
FEATURE [Part::Extrusion] Extrude054
  Base = -> Sketch063
  Dir = (0,-1,2e-16)
  DirMode = 2
  FaceMakerClass = Part::FaceMakerBullseye
  LengthFwd = 6
  LengthRev = 0
  Placement = pos=(0,9,0) rot=(0,0,1;0rad)
  Solid = true
  Symmetric = false
FEATURE [Sketcher::SketchObject] Sketch064  label="topSketch017"
  FullyConstrained = true
  sketch-geometry (20):
    g0: LineSegment StartX=5.21097e-06 StartY=3 StartZ=0 EndX=5.21097e-06 EndY=19 EndZ=0
    g1: ArcOfCircle CenterX=19 CenterY=19 CenterZ=0 NormalX=0 NormalY=0 NormalZ=1 AngleXU=0 Radius=19 StartAngle=1.5708 EndAngle=3.14159
    g2: ArcOfCircle CenterX=19 CenterY=19 CenterZ=0 NormalX=0 NormalY=0 NormalZ=1 AngleXU=0 Radius=16 StartAngle=1.5708 EndAngle=3.14159
    g3: LineSegment StartX=114 StartY=35 StartZ=0 EndX=19 EndY=35 EndZ=0
    g4: LineSegment StartX=5.21097e-06 StartY=3 StartZ=0 EndX=5.21097e-06 EndY=0 EndZ=0
    g5: LineSegment StartX=3 StartY=0 StartZ=0 EndX=5.21097e-06 EndY=0 EndZ=0
    g6: LineSegment StartX=3 StartY=19 StartZ=0 EndX=3 EndY=0 EndZ=0
    g7: LineSegment StartX=19 StartY=38 StartZ=0 EndX=124 EndY=38 EndZ=0
    g8: Circle CenterX=119 CenterY=35 CenterZ=0 NormalX=0 NormalY=0 NormalZ=1 AngleXU=0 Radius=1
    g9: Circle CenterX=121 CenterY=35 CenterZ=0 NormalX=0 NormalY=0 NormalZ=1 AngleXU=0 Radius=1
    g10: Circle CenterX=121 CenterY=33 CenterZ=0 NormalX=0 NormalY=0 NormalZ=1 AngleXU=0 Radius=1
    g11: BSplineCurve PolesCount=3 KnotsCount=2 Degree=2 IsPeriodic=0
    g12: GeomPoint X=119 Y=35 Z=0
    g13: GeomPoint X=121 Y=33 Z=0
    g14: LineSegment StartX=119 StartY=35 StartZ=0 EndX=114 EndY=35 EndZ=0
    g15: ArcOfCircle CenterX=105 CenterY=19 CenterZ=0 NormalX=0 NormalY=0 NormalZ=1 AngleXU=0 Radius=19 StartAngle=5.7297 EndAngle=6.28319
    g16: ArcOfCircle CenterX=105 CenterY=19 CenterZ=0 NormalX=0 NormalY=0 NormalZ=1 AngleXU=0 Radius=16 StartAngle=5.60905 EndAngle=6.28319
    g17: LineSegment StartX=121 StartY=33 StartZ=0 EndX=121 EndY=19 EndZ=0
    g18: LineSegment StartX=124 StartY=38 StartZ=0 EndX=124 EndY=19 EndZ=0
    g19: LineSegment StartX=117.5 StartY=9.01251 StartZ=0 EndX=121.163 EndY=9.0125 EndZ=0
  constraints (46):
    c: Vertical(g0)
    c: Block(g0)
    c: Coincident(g1,g0)
    c: Block(g1)
    c: Coincident(g2,g1)
    c: Block(g2)
    c: Coincident(g3,g2)
    c: Horizontal(g3)
    c: Tangent(g3,g2)
    c: Coincident(g4,g0)
    c: Distance(g4) = 3
    c: Vertical(g4)
    c: Coincident(g5,g4)
    c: Horizontal(g5)
    c: Coincident(g6,g2)
    c: Coincident(g6,g5)
    c: Vertical(g6)
    c: Horizontal(g7)
    c: Distance(g7) = 105
    c: Coincident(g7,g1)
    c: Block(g3)
    c: Weight(g8) = 1
    c: Equal(g8,g9)
    c: Equal(g8,g10)
    c: InternalAlignment(g8,g11)
    c: InternalAlignment(g9,g11)
    c: InternalAlignment(g10,g11)
    c: InternalAlignment(g12,g11)
    c: InternalAlignment(g13,g11)
    c: Block(g11)
    c: Coincident(g14,g11)
    c: Coincident(g14,g3)
    c: Horizontal(g14)
    c: Block(g15)
    c: Coincident(g16,g15)
    c: Block(g16)
    c: Coincident(g17,g11)
    c: Coincident(g17,g16)
    c: Vertical(g17)
    c: Distance(g17) = 14
    c: Coincident(g18,g7)
    c: Coincident(g18,g15)
    c: Vertical(g18)
    c: Distance(g18) = 19
    c: Coincident(g19,g16)
    c: Coincident(g19,g15)
FEATURE [Sketcher::SketchObject] Sketch065
  FullyConstrained = true
  MapMode = 3
  Placement = pos=(0,0,0) rot=(1,0,0;1.5708rad)
  sketch-geometry (8):
    g0: Circle CenterX=80.351 CenterY=-67.6202 CenterZ=0 NormalX=0 NormalY=0 NormalZ=1 AngleXU=0 Radius=3
    g1: Circle CenterX=80.351 CenterY=-4.92017 CenterZ=0 NormalX=0 NormalY=0 NormalZ=1 AngleXU=0 Radius=3
    g2: Circle CenterX=23.851 CenterY=-4.92017 CenterZ=0 NormalX=0 NormalY=0 NormalZ=1 AngleXU=0 Radius=3
    g3: Circle CenterX=23.851 CenterY=-67.6202 CenterZ=0 NormalX=0 NormalY=0 NormalZ=1 AngleXU=0 Radius=3
    g4: Circle CenterX=23.851 CenterY=-67.6202 CenterZ=0 NormalX=0 NormalY=0 NormalZ=1 AngleXU=0 Radius=5
    g5: Circle CenterX=80.351 CenterY=-67.6202 CenterZ=0 NormalX=0 NormalY=0 NormalZ=1 AngleXU=0 Radius=5
    g6: Circle CenterX=23.851 CenterY=-4.92017 CenterZ=0 NormalX=0 NormalY=0 NormalZ=1 AngleXU=0 Radius=5
    g7: Circle CenterX=80.351 CenterY=-4.92017 CenterZ=0 NormalX=0 NormalY=0 NormalZ=1 AngleXU=0 Radius=5
  constraints (8):
    c: Block(g1)
    c: Block(g0)
    c: Block(g3)
    c: Block(g2)
    c: Block(g5)
    c: Block(g4)
    c: Block(g6)
    c: Block(g7)
FEATURE [Part::Extrusion] Extrude056
  Base = -> Sketch065
  Dir = (0,-1,2e-16)
  DirMode = 2
  FaceMakerClass = Part::FaceMakerBullseye
  LengthFwd = 2
  LengthRev = 0
  Solid = true
  Symmetric = false
FEATURE [Part::Extrusion] Extrude057  label="top025"
  Base = -> Sketch064
  Dir = (0,0,1)
  DirMode = 2
  FaceMakerClass = Part::FaceMakerBullseye
  LengthFwd = 72
  LengthRev = 0
  Solid = true
  Symmetric = false
FEATURE [Sketcher::SketchObject] Sketch066
  FullyConstrained = true
  MapMode = 3
  Placement = pos=(0,0,0) rot=(1,0,0;1.5708rad)
  Support = -> [Extrude057]
  sketch-geometry (8):
    g0: Circle CenterX=80.351 CenterY=-67.6202 CenterZ=0 NormalX=0 NormalY=0 NormalZ=1 AngleXU=0 Radius=3
    g1: Circle CenterX=80.351 CenterY=-4.92017 CenterZ=0 NormalX=0 NormalY=0 NormalZ=1 AngleXU=0 Radius=3
    g2: Circle CenterX=23.851 CenterY=-4.92017 CenterZ=0 NormalX=0 NormalY=0 NormalZ=1 AngleXU=0 Radius=3
    g3: Circle CenterX=23.851 CenterY=-67.6202 CenterZ=0 NormalX=0 NormalY=0 NormalZ=1 AngleXU=0 Radius=3
    g4: Circle CenterX=23.851 CenterY=-67.6202 CenterZ=0 NormalX=0 NormalY=0 NormalZ=1 AngleXU=0 Radius=5
    g5: Circle CenterX=80.351 CenterY=-67.6202 CenterZ=0 NormalX=0 NormalY=0 NormalZ=1 AngleXU=0 Radius=5
    g6: Circle CenterX=23.851 CenterY=-4.92017 CenterZ=0 NormalX=0 NormalY=0 NormalZ=1 AngleXU=0 Radius=5
    g7: Circle CenterX=80.351 CenterY=-4.92017 CenterZ=0 NormalX=0 NormalY=0 NormalZ=1 AngleXU=0 Radius=5
  constraints (8):
    c: Block(g1)
    c: Block(g0)
    c: Block(g3)
    c: Block(g2)
    c: Block(g5)
    c: Block(g4)
    c: Block(g6)
    c: Block(g7)
FEATURE [Part::Extrusion] Extrude055
  Base = -> Sketch066
  Dir = (0,-1,2e-16)
  DirMode = 2
  FaceMakerClass = Part::FaceMakerBullseye
  LengthFwd = 2
  LengthRev = 0
  Solid = true
  Symmetric = false
FEATURE [Part::Fillet] Fillet041
  Base = -> Extrude056
  Edges = 4 edges r=1.99: [Edge6,Edge12,Edge18,Edge24]
FEATURE [Part::Cut] Cut045
  Base = -> Extrude055
  Placement = pos=(0,6,0) rot=(0,0,1;0rad)
  Tool = -> Fillet041
FEATURE [Part::MultiFuse] Fusion095  label="pcbScrewPillars"
  Placement = pos=(-3.2,-1,72.3) rot=(0,0,1;0rad)
  Shapes = -> [Cut045,Extrude054]
FEATURE [Part::Feature] Face113
  shape: bbox 3.2 x 1.5 x 2e-07 mm, 1 faces, 0 solids (baked)
FEATURE [Part::Revolution] Revolve121  label="backCaseScrewRetainer002"
  Angle = 360
  Axis = (0,1,0)
  Base = (0,0,0)
  FaceMakerClass = Part::FaceMakerBullseye
  Placement = pos=(12.5,3,62) rot=(0,0,1;0rad)
  Solid = false
  Source = -> Face113
  Symmetric = false
FEATURE [Part::Feature] Face114
  shape: bbox 3.2 x 1.5 x 2e-07 mm, 1 faces, 0 solids (baked)
FEATURE [Part::Feature] Face115
  shape: bbox 3.2 x 1.5 x 2e-07 mm, 1 faces, 0 solids (baked)
FEATURE [Part::Feature] Face116
  shape: bbox 3.2 x 1.5 x 2e-07 mm, 1 faces, 0 solids (baked)
FEATURE [Part::Revolution] Revolve122  label="frontCaseScrewRetainer004"
  Angle = 360
  Axis = (0,1,0)
  Base = (0,0,0)
  FaceMakerClass = Part::FaceMakerBullseye
  Placement = pos=(89.5,3,68.5) rot=(0,0,1;0rad)
  Solid = false
  Source = -> Face115
  Symmetric = false
FEATURE [Part::Revolution] Revolve123  label="frontCaseScrewRetainer005"
  Angle = 360
  Axis = (0,1,0)
  Base = (0,0,0)
  FaceMakerClass = Part::FaceMakerBullseye
  Placement = pos=(89.5,3,3.5) rot=(0,0,1;0rad)
  Solid = false
  Source = -> Face116
  Symmetric = false
FEATURE [Part::Revolution] Revolve124  label="backCaseScrewRetainer003"
  Angle = 360
  Axis = (0,1,0)
  Base = (0,0,0)
  FaceMakerClass = Part::FaceMakerBullseye
  Placement = pos=(12.5,3,10) rot=(0,0,1;0rad)
  Solid = false
  Source = -> Face114
  Symmetric = false
FEATURE [Part::Feature] Face117
  shape: bbox 3.6 x 3.2 x 2e-07 mm, 1 faces, 0 solids (baked)
FEATURE [Part::Revolution] Revolve125  label="moreFrontCaseScrewRetainer004"
  Angle = 360
  Axis = (0,1,0)
  Base = (0,0,0)
  FaceMakerClass = Part::FaceMakerBullseye
  Placement = pos=(109.5,4.5,68.5) rot=(0,0,1;0rad)
  Solid = false
  Source = -> Face117
  Symmetric = false
FEATURE [Part::Feature] Face118
  shape: bbox 3.6 x 3.2 x 2e-07 mm, 1 faces, 0 solids (baked)
FEATURE [Part::Revolution] Revolve126  label="moreFrontCaseScrewRetainer005"
  Angle = 360
  Axis = (0,1,0)
  Base = (0,0,0)
  FaceMakerClass = Part::FaceMakerBullseye
  Placement = pos=(109.5,4.5,3.5) rot=(0,0,1;0rad)
  Solid = false
  Source = -> Face118
  Symmetric = false
FEATURE [Part::MultiFuse] Fusion096  label="screwRetainers001"
  Shapes = -> [Revolve126,Revolve125,Revolve124,Revolve123,Revolve122,Revolve121]
FEATURE [Part::Feature] Face119
  shape: bbox 10 x 16.5 x 2e-07 mm, 1 faces, 0 solids (baked)
FEATURE [Part::Revolution] Revolve130  label="plugHousing050"
  Angle = 360
  Axis = (0,1,0)
  Base = (0,0,0)
  FaceMakerClass = Part::FaceMakerBullseye
  Placement = pos=(0,0,36.15) rot=(0,0,1;0rad)
  Solid = false
  Source = -> Face119
  Symmetric = false
FEATURE [Part::Feature] Face120
  shape: bbox 10 x 16.5 x 2e-07 mm, 1 faces, 0 solids (baked)
FEATURE [Part::Feature] Face121
  shape: bbox 10 x 16.5 x 2e-07 mm, 1 faces, 0 solids (baked)
FEATURE [Part::Revolution] Revolve127  label="plugHousing047"
  Angle = 360
  Axis = (0,1,0)
  Base = (0,0,0)
  FaceMakerClass = Part::FaceMakerBullseye
  Placement = pos=(0,0,36.15) rot=(0,0,1;0rad)
  Solid = false
  Source = -> Face121
  Symmetric = false
FEATURE [Part::Feature] Face122
  shape: bbox 10 x 16.5 x 2e-07 mm, 1 faces, 0 solids (baked)
FEATURE [Part::Feature] Face123
  shape: bbox 10 x 16.5 x 2e-07 mm, 1 faces, 0 solids (baked)
FEATURE [Part::Revolution] Revolve128  label="plugHousing048"
  Angle = 360
  Axis = (0,1,0)
  Base = (0,0,0)
  FaceMakerClass = Part::FaceMakerBullseye
  Placement = pos=(0,0,36.15) rot=(0,0,1;0rad)
  Solid = false
  Source = -> Face123
  Symmetric = false
FEATURE [Part::MultiFuse] Fusion100  label="plugHousing054"
  Placement = pos=(0,0,0) rot=(0,0,1;1.5708rad)
  Shapes = -> [Revolve130,Revolve128]
FEATURE [Part::Feature] Face124
  shape: bbox 10 x 16.5 x 2e-07 mm, 1 faces, 0 solids (baked)
FEATURE [Part::Feature] Face125
  shape: bbox 10 x 16.5 x 2e-07 mm, 1 faces, 0 solids (baked)
FEATURE [Part::Revolution] Revolve129  label="plugHousing049"
  Angle = 360
  Axis = (0,1,0)
  Base = (0,0,0)
  FaceMakerClass = Part::FaceMakerBullseye
  Placement = pos=(0,0,36.15) rot=(0,0,1;0rad)
  Solid = false
  Source = -> Face125
  Symmetric = false
FEATURE [Part::Feature] Face126
  shape: bbox 10 x 16.5 x 2e-07 mm, 1 faces, 0 solids (baked)
FEATURE [Part::Revolution] Revolve131  label="plugHousing058"
  Angle = 360
  Axis = (0,1,0)
  Base = (0,0,0)
  FaceMakerClass = Part::FaceMakerBullseye
  Placement = pos=(0,0,36.15) rot=(0,0,1;0rad)
  Solid = false
  Source = -> Face120
  Symmetric = false
FEATURE [Part::MultiFuse] Fusion099  label="plugHousing053"
  Placement = pos=(0,0,0) rot=(0,0,1;1.5708rad)
  Shapes = -> [Revolve127,Revolve131]
FEATURE [Part::MultiFuse] Fusion102  label="plugHousing056"
  Placement = pos=(0,19,0) rot=(0,0,1;3.14159rad)
  Shapes = -> [Fusion100,Fusion099]
FEATURE [Part::Revolution] Revolve132  label="plugHousing059"
  Angle = 360
  Axis = (0,1,0)
  Base = (0,0,0)
  FaceMakerClass = Part::FaceMakerBullseye
  Placement = pos=(0,0,36.15) rot=(0,0,1;0rad)
  Solid = false
  Source = -> Face126
  Symmetric = false
FEATURE [Part::Revolution] Revolve133  label="plugHousing060"
  Angle = 360
  Axis = (0,1,0)
  Base = (0,0,0)
  FaceMakerClass = Part::FaceMakerBullseye
  Placement = pos=(0,0,36.15) rot=(0,0,1;0rad)
  Solid = false
  Source = -> Face122
  Symmetric = false
FEATURE [Part::MultiFuse] Fusion097  label="plugHousing051"
  Placement = pos=(0,0,0) rot=(0,0,1;1.5708rad)
  Shapes = -> [Revolve133,Revolve132]
FEATURE [Part::Revolution] Revolve134  label="plugHousing061"
  Angle = 360
  Axis = (0,1,0)
  Base = (0,0,0)
  FaceMakerClass = Part::FaceMakerBullseye
  Placement = pos=(0,0,36.15) rot=(0,0,1;0rad)
  Solid = false
  Source = -> Face124
  Symmetric = false
FEATURE [Part::MultiFuse] Fusion101  label="plugHousing055"
  Placement = pos=(0,0,0) rot=(0,0,1;1.5708rad)
  Shapes = -> [Revolve129,Revolve134]
FEATURE [Part::MultiFuse] Fusion098  label="plugHousing052"
  Placement = pos=(0,19,0) rot=(0,0,1;3.14159rad)
  Shapes = -> [Fusion097,Fusion101]
FEATURE [Part::MultiFuse] Fusion103  label="plugHousing057"
  Placement = pos=(122.621,0,-0.15) rot=(0,0,1;0rad)
  Shapes = -> [Fusion102,Fusion098]
FEATURE [Part::Box] Box028  label="Cube015"
  AttacherType = Attacher::AttachEngine3D
  Height = 28
  Length = 3
  Placement = pos=(110.7,19,22) rot=(0,0,1;0rad)
  Width = 15.7
FEATURE [Part::Cylinder] Cylinder044
  Angle = 360
  AttacherType = Attacher::AttachEngine3D
  Height = 20
  Placement = pos=(0,0,36.15) rot=(0,0,1;0rad)
  Radius = 10.3
FEATURE [Part::Cylinder] Cylinder045
  Angle = 360
  AttacherType = Attacher::AttachEngine3D
  Height = 10
  Placement = pos=(0,0,36.15) rot=(0,0,1;0rad)
  Radius = 4
FEATURE [Part::MultiFuse] Fusion104  label="removeToCreteHoleForPlugHousing040"
  Placement = pos=(70,19,36) rot=(0,1,0;1.5708rad)
  Shapes = -> [Cylinder044,Cylinder045]
FEATURE [Part::Cut] Cut046  label="plugHousingTab003"
  Base = -> Box028
  Tool = -> Fusion104
FEATURE [Part::MultiFuse] Fusion105  label="plugHousing062"
  Shapes = -> [Fusion103,Cut046]
FEATURE [Part::Fillet] Fillet042
  Base = -> Fusion105
  Edges = 1 edges r=2: [Edge25]
FEATURE [Part::Fillet] Fillet043  label="plugHousing063"
  Base = -> Fillet042
  Edges = 1 edges r=2: [Edge8]
  Placement = pos=(7,0,0) rot=(0,0,1;0rad)
FEATURE [Part::Feature] Face127
  shape: bbox 10 x 16.5 x 2e-07 mm, 1 faces, 0 solids (baked)
FEATURE [Part::Feature] Face128
  shape: bbox 10 x 16.5 x 2e-07 mm, 1 faces, 0 solids (baked)
FEATURE [Part::Revolution] Revolve137  label="plugHousing070"
  Angle = 360
  Axis = (0,1,0)
  Base = (0,0,0)
  FaceMakerClass = Part::FaceMakerBullseye
  Placement = pos=(0,0,36.15) rot=(0,0,1;0rad)
  Solid = false
  Source = -> Face127
  Symmetric = false
FEATURE [Part::Revolution] Revolve140  label="plugHousing073"
  Angle = 360
  Axis = (0,1,0)
  Base = (0,0,0)
  FaceMakerClass = Part::FaceMakerBullseye
  Placement = pos=(0,0,36.15) rot=(0,0,1;0rad)
  Solid = false
  Source = -> Face128
  Symmetric = false
FEATURE [Part::Feature] Face129
  shape: bbox 10 x 16.5 x 2e-07 mm, 1 faces, 0 solids (baked)
FEATURE [Part::Revolution] Revolve138  label="plugHousing071"
  Angle = 360
  Axis = (0,1,0)
  Base = (0,0,0)
  FaceMakerClass = Part::FaceMakerBullseye
  Placement = pos=(0,0,36.15) rot=(0,0,1;0rad)
  Solid = false
  Source = -> Face129
  Symmetric = false
FEATURE [Part::Feature] Face130
  shape: bbox 10 x 16.5 x 2e-07 mm, 1 faces, 0 solids (baked)
FEATURE [Part::Revolution] Revolve139  label="plugHousing072"
  Angle = 360
  Axis = (0,1,0)
  Base = (0,0,0)
  FaceMakerClass = Part::FaceMakerBullseye
  Placement = pos=(0,0,36.15) rot=(0,0,1;0rad)
  Solid = false
  Source = -> Face130
  Symmetric = false
FEATURE [Part::Feature] Face131
  shape: bbox 10 x 16.5 x 2e-07 mm, 1 faces, 0 solids (baked)
FEATURE [Part::Revolution] Revolve135  label="plugHousing068"
  Angle = 360
  Axis = (0,1,0)
  Base = (0,0,0)
  FaceMakerClass = Part::FaceMakerBullseye
  Placement = pos=(0,0,36.15) rot=(0,0,1;0rad)
  Solid = false
  Source = -> Face131
  Symmetric = false
FEATURE [Part::MultiFuse] Fusion112  label="plugHousing078"
  Placement = pos=(0,0,0) rot=(0,0,1;1.5708rad)
  Shapes = -> [Revolve135,Revolve139]
FEATURE [Part::Feature] Face132
  shape: bbox 10 x 16.5 x 2e-07 mm, 1 faces, 0 solids (baked)
FEATURE [Part::Revolution] Revolve141  label="plugHousing074"
  Angle = 360
  Axis = (0,1,0)
  Base = (0,0,0)
  FaceMakerClass = Part::FaceMakerBullseye
  Placement = pos=(0,0,36.15) rot=(0,0,1;0rad)
  Solid = false
  Source = -> Face132
  Symmetric = false
FEATURE [Part::MultiFuse] Fusion110  label="plugHousing076"
  Placement = pos=(0,0,0) rot=(0,0,1;1.5708rad)
  Shapes = -> [Revolve141,Revolve140]
FEATURE [Part::Feature] Face133
  shape: bbox 10 x 16.5 x 2e-07 mm, 1 faces, 0 solids (baked)
FEATURE [Part::Revolution] Revolve136  label="plugHousing069"
  Angle = 360
  Axis = (0,1,0)
  Base = (0,0,0)
  FaceMakerClass = Part::FaceMakerBullseye
  Placement = pos=(0,0,36.15) rot=(0,0,1;0rad)
  Solid = false
  Source = -> Face133
  Symmetric = false
FEATURE [Part::MultiFuse] Fusion106  label="plugHousing064"
  Placement = pos=(0,0,0) rot=(0,0,1;1.5708rad)
  Shapes = -> [Revolve138,Revolve136]
FEATURE [Part::MultiFuse] Fusion108  label="plugHousing066"
  Placement = pos=(0,19,0) rot=(0,0,1;3.14159rad)
  Shapes = -> [Fusion106,Fusion112]
FEATURE [Part::Feature] Face134
  shape: bbox 10 x 16.5 x 2e-07 mm, 1 faces, 0 solids (baked)
FEATURE [Part::Revolution] Revolve142  label="plugHousing075"
  Angle = 360
  Axis = (0,1,0)
  Base = (0,0,0)
  FaceMakerClass = Part::FaceMakerBullseye
  Placement = pos=(0,0,36.15) rot=(0,0,1;0rad)
  Solid = false
  Source = -> Face134
  Symmetric = false
FEATURE [Part::MultiFuse] Fusion107  label="plugHousing065"
  Placement = pos=(0,0,0) rot=(0,0,1;1.5708rad)
  Shapes = -> [Revolve137,Revolve142]
FEATURE [Part::MultiFuse] Fusion111  label="plugHousing077"
  Placement = pos=(0,19,0) rot=(0,0,1;3.14159rad)
  Shapes = -> [Fusion110,Fusion107]
FEATURE [Part::MultiFuse] Fusion109  label="plugHousing067"
  Placement = pos=(131.236,0,-0.15) rot=(0,0,1;0rad)
  Shapes = -> [Fusion108,Fusion111]
FEATURE [Part::MultiFuse] Fusion113  label="plugHousing079"
  Shapes = -> [Fillet043,Fusion109]
FEATURE [Part::Feature] Face135
  shape: bbox 3.5 x 17.8 x 2e-07 mm, 1 faces, 0 solids (baked)
FEATURE [Part::Revolution] Revolve143  label="removeToCreateScrewAndThreadedInsertHole049"
  Angle = 360
  Axis = (0,1,0)
  Base = (0,0,0)
  FaceMakerClass = Part::FaceMakerBullseye
  Placement = pos=(12.5,0,10) rot=(0,0,1;0rad)
  Solid = false
  Source = -> Face135
  Symmetric = false
FEATURE [Part::Feature] Face136
  shape: bbox 3.5 x 17.8 x 2e-07 mm, 1 faces, 0 solids (baked)
FEATURE [Part::Revolution] Revolve144  label="removeToCreateScrewAndThreadedInsertHole050"
  Angle = 360
  Axis = (0,1,0)
  Base = (0,0,0)
  FaceMakerClass = Part::FaceMakerBullseye
  Placement = pos=(12.5,0,62) rot=(0,0,1;0rad)
  Solid = false
  Source = -> Face136
  Symmetric = false
FEATURE [Part::Feature] Face137
  shape: bbox 3.5 x 17.8 x 2e-07 mm, 1 faces, 0 solids (baked)
FEATURE [Part::Revolution] Revolve145  label="removeToCreateScrewAndThreadedInsertHole051"
  Angle = 360
  Axis = (0,1,0)
  Base = (0,0,0)
  FaceMakerClass = Part::FaceMakerBullseye
  Placement = pos=(89.5,0,68.5) rot=(0,0,1;0rad)
  Solid = false
  Source = -> Face137
  Symmetric = false
FEATURE [Part::Feature] Face138
  shape: bbox 3.5 x 17.8 x 2e-07 mm, 1 faces, 0 solids (baked)
FEATURE [Part::Revolution] Revolve146  label="removeToCreateScrewAndThreadedInsertHole052"
  Angle = 360
  Axis = (0,1,0)
  Base = (0,0,0)
  FaceMakerClass = Part::FaceMakerBullseye
  Placement = pos=(89.5,0,3.5) rot=(0,0,1;0rad)
  Solid = false
  Source = -> Face138
  Symmetric = false
FEATURE [Part::Feature] Face139
  shape: bbox 3.5 x 17.8 x 2e-07 mm, 1 faces, 0 solids (baked)
FEATURE [Part::Revolution] Revolve147  label="removeToCreateScrewAndThreadedInsertHole053"
  Angle = 360
  Axis = (0,1,0)
  Base = (0,0,0)
  FaceMakerClass = Part::FaceMakerBullseye
  Placement = pos=(109.5,4.7,3.5) rot=(0,0,1;0rad)
  Solid = false
  Source = -> Face139
  Symmetric = false
FEATURE [Part::Feature] Face140
  shape: bbox 3.5 x 17.8 x 2e-07 mm, 1 faces, 0 solids (baked)
FEATURE [Part::Revolution] Revolve148  label="removeToCreateScrewAndThreadedInsertHole054"
  Angle = 360
  Axis = (0,1,0)
  Base = (0,0,0)
  FaceMakerClass = Part::FaceMakerBullseye
  Placement = pos=(109.5,4.7,68.5) rot=(0,0,1;0rad)
  Solid = false
  Source = -> Face140
  Symmetric = false
FEATURE [Part::MultiFuse] Fusion114  label="removeToCreateScrewAndThreadedInsertHole055"
  Shapes = -> [Revolve148,Revolve147,Revolve146,Revolve145,Revolve144,Revolve143]
FEATURE [Part::Cut] Cut047  label="casePillars004"
  Base = -> Cut037
  Tool = -> Fusion114
FEATURE [Part::Feature] Face141
  shape: bbox 3.5 x 17.8 x 2e-07 mm, 1 faces, 0 solids (baked)
FEATURE [Part::Feature] Face142
  shape: bbox 3.5 x 17.8 x 2e-07 mm, 1 faces, 0 solids (baked)
FEATURE [Part::Feature] Face143
  shape: bbox 3.5 x 17.8 x 2e-07 mm, 1 faces, 0 solids (baked)
FEATURE [Part::Revolution] Revolve149  label="removeToCreateScrewAndThreadedInsertHole057"
  Angle = 360
  Axis = (0,1,0)
  Base = (0,0,0)
  FaceMakerClass = Part::FaceMakerBullseye
  Placement = pos=(12.5,0,10) rot=(0,0,1;0rad)
  Solid = false
  Source = -> Face141
  Symmetric = false
FEATURE [Part::Feature] Face144
  shape: bbox 3.5 x 17.8 x 2e-07 mm, 1 faces, 0 solids (baked)
FEATURE [Part::Feature] Face145
  shape: bbox 3.5 x 17.8 x 2e-07 mm, 1 faces, 0 solids (baked)
FEATURE [Part::Feature] Face146
  shape: bbox 3.5 x 17.8 x 2e-07 mm, 1 faces, 0 solids (baked)
FEATURE [Part::Revolution] Revolve150  label="removeToCreateScrewAndThreadedInsertHole058"
  Angle = 360
  Axis = (0,1,0)
  Base = (0,0,0)
  FaceMakerClass = Part::FaceMakerBullseye
  Placement = pos=(12.5,0,62) rot=(0,0,1;0rad)
  Solid = false
  Source = -> Face146
  Symmetric = false
FEATURE [Part::Revolution] Revolve151  label="removeToCreateScrewAndThreadedInsertHole059"
  Angle = 360
  Axis = (0,1,0)
  Base = (0,0,0)
  FaceMakerClass = Part::FaceMakerBullseye
  Placement = pos=(89.5,0,68.5) rot=(0,0,1;0rad)
  Solid = false
  Source = -> Face143
  Symmetric = false
FEATURE [Part::Revolution] Revolve152  label="removeToCreateScrewAndThreadedInsertHole060"
  Angle = 360
  Axis = (0,1,0)
  Base = (0,0,0)
  FaceMakerClass = Part::FaceMakerBullseye
  Placement = pos=(89.5,0,3.5) rot=(0,0,1;0rad)
  Solid = false
  Source = -> Face142
  Symmetric = false
FEATURE [Part::Revolution] Revolve153  label="removeToCreateScrewAndThreadedInsertHole061"
  Angle = 360
  Axis = (0,1,0)
  Base = (0,0,0)
  FaceMakerClass = Part::FaceMakerBullseye
  Placement = pos=(109.5,4.7,3.5) rot=(0,0,1;0rad)
  Solid = false
  Source = -> Face145
  Symmetric = false
FEATURE [Part::Revolution] Revolve154  label="removeToCreateScrewAndThreadedInsertHole062"
  Angle = 360
  Axis = (0,1,0)
  Base = (0,0,0)
  FaceMakerClass = Part::FaceMakerBullseye
  Placement = pos=(109.5,4.7,68.5) rot=(0,0,1;0rad)
  Solid = false
  Source = -> Face144
  Symmetric = false
FEATURE [Part::MultiFuse] Fusion115  label="removeToCreateScrewAndThreadedInsertHole056"
  Shapes = -> [Revolve154,Revolve153,Revolve152,Revolve151,Revolve150,Revolve149]
FEATURE [Part::Feature] Face147
  shape: bbox 9.8 x 26.5 x 2e-07 mm, 1 faces, 0 solids (baked)
FEATURE [Part::Revolution] Revolve155
  Angle = 360
  Axis = (0,1,0)
  Base = (0,0,0)
  FaceMakerClass = Part::FaceMakerBullseye
  Placement = pos=(0,0,0) rot=(0,0,1;1.5708rad)
  Solid = false
  Source = -> Face147
  Symmetric = false
FEATURE [Part::Feature] Face148
  shape: bbox 9.8 x 26.5 x 2e-07 mm, 1 faces, 0 solids (baked)
FEATURE [Part::Revolution] Revolve156
  Angle = 360
  Axis = (0,1,0)
  Base = (0,0,0)
  FaceMakerClass = Part::FaceMakerBullseye
  Placement = pos=(0,0,0) rot=(0,0,1;1.5708rad)
  Solid = false
  Source = -> Face148
  Symmetric = false
FEATURE [Part::MultiFuse] Fusion116
  Placement = pos=(-18,19,36) rot=(0,0,1;0rad)
  Shapes = -> [Revolve156,Revolve155]
FEATURE [Part::Box] Box029  label="Cube016"
  AttacherType = Attacher::AttachEngine3D
  Height = 28
  Length = 3
  Placement = pos=(110.7,19,22) rot=(0,0,1;0rad)
  Width = 15.7
FEATURE [Part::Cylinder] Cylinder046
  Angle = 360
  AttacherType = Attacher::AttachEngine3D
  Height = 10
  Placement = pos=(0,0,36.15) rot=(0,0,1;0rad)
  Radius = 4
FEATURE [Part::Cylinder] Cylinder047
  Angle = 360
  AttacherType = Attacher::AttachEngine3D
  Height = 20
  Placement = pos=(0,0,36.15) rot=(0,0,1;0rad)
  Radius = 10.3
FEATURE [Part::MultiFuse] Fusion117  label="removeToCreteHoleForPlugHousing041"
  Placement = pos=(70,19,36) rot=(0,1,0;1.5708rad)
  Shapes = -> [Cylinder047,Cylinder046]
FEATURE [Part::Cut] Cut049  label="plugHousingTab004"
  Base = -> Box029
  Placement = pos=(-107.4,-14,0) rot=(0,0,1;0rad)
  Tool = -> Fusion117
FEATURE [Part::Box] Box030  label="Cube017"
  AttacherType = Attacher::AttachEngine3D
  Height = 28
  Length = 3
  Placement = pos=(110.7,19,22) rot=(0,0,1;0rad)
  Width = 15.7
FEATURE [Part::Cylinder] Cylinder048
  Angle = 360
  AttacherType = Attacher::AttachEngine3D
  Height = 10
  Placement = pos=(0,0,36.15) rot=(0,0,1;0rad)
  Radius = 4
FEATURE [Part::Cylinder] Cylinder049
  Angle = 360
  AttacherType = Attacher::AttachEngine3D
  Height = 20
  Placement = pos=(0,0,36.15) rot=(0,0,1;0rad)
  Radius = 10.3
FEATURE [Part::MultiFuse] Fusion118  label="removeToCreteHoleForPlugHousing042"
  Placement = pos=(70,19,36) rot=(0,1,0;1.5708rad)
  Shapes = -> [Cylinder049,Cylinder048]
FEATURE [Part::Cut] Cut050  label="plugHousingTab005"
  Base = -> Box030
  Placement = pos=(-107.4,-14,0) rot=(0,0,1;0rad)
  Tool = -> Fusion118
FEATURE [Part::MultiFuse] Fusion119
  Placement = pos=(9.6,23,0) rot=(0,0,1;3.14159rad)
  Shapes = -> [Cut049,Cut050]
FEATURE [Part::Box] Box031  label="Cube018"
  AttacherType = Attacher::AttachEngine3D
  Height = 10
  Length = 3
  Placement = pos=(3.3,4,12) rot=(0,0,1;0rad)
  Width = 10
FEATURE [Part::Fillet] Fillet044
  Base = -> Box031
  Edges = 1 edges r=2: [Edge11]
FEATURE [Part::Box] Box032  label="Cube019"
  AttacherType = Attacher::AttachEngine3D
  Height = 10
  Length = 3
  Placement = pos=(3.3,4,50) rot=(0,0,1;0rad)
  Width = 10
FEATURE [Part::Fillet] Fillet045
  Base = -> Box032
  Edges = 1 edges r=2: [Edge12]
FEATURE [Part::Box] Box033  label="Cube020"
  AttacherType = Attacher::AttachEngine3D
  Height = 28
  Length = 4
  Placement = pos=(5,0,22) rot=(0,0,1;0rad)
  Width = 10
FEATURE [Part::Fillet] Fillet046
  Base = -> Box033
  Edges = 1 edges r=1: [Edge7]
FEATURE [Part::Fillet] Fillet047
  Base = -> Fillet046
  Edges = 1 edges r=2: [Edge5]
FEATURE [Part::Fillet] Fillet048
  Base = -> Fillet047
  Edges = 1 edges r=2: [Edge2]
FEATURE [Part::Cylinder] Cylinder050
  Angle = 360
  AttacherType = Attacher::AttachEngine3D
  Height = 20
  Placement = pos=(0,0,36.15) rot=(0,0,1;0rad)
  Radius = 8.2
FEATURE [Part::Cylinder] Cylinder051
  Angle = 360
  AttacherType = Attacher::AttachEngine3D
  Height = 10
  Placement = pos=(0,0,36.15) rot=(0,0,1;0rad)
  Radius = 4
FEATURE [Part::MultiFuse] Fusion120  label="removeToCreteHoleForPlugHousing043"
  Placement = pos=(-42,19,36) rot=(0,1,0;1.5708rad)
  Shapes = -> [Cylinder050,Cylinder051]
FEATURE [Sketcher::SketchObject] Sketch067  label="topSketch018"
  FullyConstrained = true
  sketch-geometry (4):
    g0: LineSegment StartX=16.8446 StartY=31.512 StartZ=0 EndX=16.3251 EndY=34.4666 EndZ=0
    g1: ArcOfCircle CenterX=19 CenterY=19.2524 CenterZ=0 NormalX=0 NormalY=0 NormalZ=1 AngleXU=0 Radius=15.4476 StartAngle=1.74483 EndAngle=2.72717
    g2: ArcOfCircle CenterX=19 CenterY=19.2524 CenterZ=0 NormalX=0 NormalY=0 NormalZ=1 AngleXU=0 Radius=12.4476 StartAngle=1.74483 EndAngle=2.73189
    g3: LineSegment StartX=4.86004 StartY=25.4725 StartZ=0 EndX=7.58253 EndY=24.2107 EndZ=0
  constraints (7):
    c: Block(g0)
    c: Coincident(g1,g0)
    c: Coincident(g2,g0)
    c: Coincident(g3,g1)
    c: Coincident(g3,g2)
    c: Block(g1)
    c: Block(g2)
FEATURE [Part::Extrusion] Extrude058
  Base = -> Sketch067
  Dir = (0,0,1)
  DirMode = 2
  FaceMakerClass = Part::FaceMakerBullseye
  LengthFwd = 10
  LengthRev = 0
  Placement = pos=(0,0,31) rot=(0,0,1;0rad)
  Solid = true
  Symmetric = false
FEATURE [Part::Cut] Cut051
  Base = -> Extrude058
  Tool = -> Fusion120
FEATURE [Part::Fillet] Fillet049
  Base = -> Cut051
  Edges = 1 edges r=2: [Edge1]
FEATURE [Part::Fillet] Fillet050
  Base = -> Fillet049
  Edges = 1 edges r=2.5: [Edge1]
FEATURE [Part::Fillet] Fillet051
  Base = -> Fillet050
  Edges = 1 edges r=2.5: [Edge2]
FEATURE [Part::MultiFuse] Fusion121  label="wireHolder003"
  Shapes = -> [Fusion116,Fillet051]
FEATURE [Part::MultiFuse] Fusion122
  Shapes = -> [Fillet045,Fusion121]
FEATURE [Part::MultiFuse] Fusion123  label="wireHolder004"
  Shapes = -> [Fusion122,Fillet048]
FEATURE [Part::MultiFuse] Fusion124  label="wireHolder005"
  Shapes = -> [Fillet044,Fusion119,Fusion123]
FEATURE [Sketcher::SketchObject] Sketch068  label="topSketch019"
  FullyConstrained = true
  sketch-geometry (6):
    g0: LineSegment StartX=19 StartY=38 StartZ=0 EndX=117 EndY=38 EndZ=0
    g1: ArcOfCircle CenterX=19 CenterY=19 CenterZ=0 NormalX=0 NormalY=0 NormalZ=1 AngleXU=0 Radius=19 StartAngle=1.5708 EndAngle=3.14159
    g2: LineSegment StartX=117 StartY=38 StartZ=0 EndX=117 EndY=19 EndZ=0
    g3: LineSegment StartX=98 StartY=1.0161e-12 StartZ=0 EndX=5.22862e-06 EndY=1.0161e-12 EndZ=0
    g4: LineSegment StartX=5.22862e-06 StartY=19 StartZ=0 EndX=5.22862e-06 EndY=1.0161e-12 EndZ=0
    g5: ArcOfCircle CenterX=98 CenterY=19 CenterZ=0 NormalX=0 NormalY=0 NormalZ=1 AngleXU=0 Radius=19 StartAngle=4.71239 EndAngle=6.28319
  constraints (16):
    c: Horizontal(g0)
    c: Distance(g0) = 98
    c: Coincident(g1,g0)
    c: Block(g1)
    c: Coincident(g2,g0)
    c: Vertical(g2)
    c: Distance(g2) = 19
    c: Horizontal(g3)
    c: Coincident(g4,g1)
    c: Vertical(g4)
    c: Coincident(g3,g4)
    c: Block(g3)
    c: Coincident(g5,g2)
    c: Coincident(g5,g3)
    c: Block(g0)
    c: Block(g5)
FEATURE [Part::Extrusion] Extrude059  label="sideA002"
  Base = -> Sketch068
  Dir = (0,0,1)
  DirMode = 2
  FaceMakerClass = Part::FaceMakerBullseye
  LengthFwd = 3
  LengthRev = 0
  Placement = pos=(0,0,-2.7) rot=(0,0,1;0rad)
  Solid = true
  Symmetric = false
FEATURE [Sketcher::SketchObject] Sketch069  label="topSketch020"
  FullyConstrained = true
  sketch-geometry (6):
    g0: LineSegment StartX=19 StartY=38 StartZ=0 EndX=117 EndY=38 EndZ=0
    g1: ArcOfCircle CenterX=19 CenterY=19 CenterZ=0 NormalX=0 NormalY=0 NormalZ=1 AngleXU=0 Radius=19 StartAngle=1.5708 EndAngle=3.14159
    g2: LineSegment StartX=117 StartY=38 StartZ=0 EndX=117 EndY=19 EndZ=0
    g3: LineSegment StartX=98 StartY=1.0161e-12 StartZ=0 EndX=5.22862e-06 EndY=1.0161e-12 EndZ=0
    g4: LineSegment StartX=5.22862e-06 StartY=19 StartZ=0 EndX=5.22862e-06 EndY=1.0161e-12 EndZ=0
    g5: ArcOfCircle CenterX=98 CenterY=19 CenterZ=0 NormalX=0 NormalY=0 NormalZ=1 AngleXU=0 Radius=19 StartAngle=4.71239 EndAngle=6.28319
  constraints (16):
    c: Horizontal(g0)
    c: Distance(g0) = 98
    c: Coincident(g1,g0)
    c: Block(g1)
    c: Coincident(g2,g0)
    c: Vertical(g2)
    c: Distance(g2) = 19
    c: Horizontal(g3)
    c: Coincident(g4,g1)
    c: Vertical(g4)
    c: Coincident(g3,g4)
    c: Block(g3)
    c: Coincident(g5,g2)
    c: Coincident(g5,g3)
    c: Block(g0)
    c: Block(g5)
FEATURE [Part::Extrusion] Extrude060  label="sideB002"
  Base = -> Sketch069
  Dir = (0,0,1)
  DirMode = 2
  FaceMakerClass = Part::FaceMakerBullseye
  LengthFwd = 3
  LengthRev = 0
  Placement = pos=(0,0,71.7) rot=(0,0,1;0rad)
  Solid = true
  Symmetric = false
FEATURE [Part::MultiFuse] Fusion127  label="removeFromBottom001"
  Placement = pos=(2,0,0) rot=(0,0,1;0rad)
  Shapes = -> [Extrude059,Extrude060]
FEATURE [Part::Cylinder] Cylinder052
  Angle = 360
  AttacherType = Attacher::AttachEngine3D
  Height = 20
  Placement = pos=(0,0,36.15) rot=(0,0,1;0rad)
  Radius = 14
FEATURE [Part::Cylinder] Cylinder053
  Angle = 360
  AttacherType = Attacher::AttachEngine3D
  Height = 10
  Placement = pos=(0,0,36.15) rot=(0,0,1;0rad)
  Radius = 4
FEATURE [Part::MultiFuse] Fusion128  label="removeToCreteHoleForPlugHousing044"
  Placement = pos=(70,19,36) rot=(0,1,0;1.5708rad)
  Shapes = -> [Cylinder052,Cylinder053]
FEATURE [Part::Cut] Cut052  label="bottom011"
  Base = -> Extrude043
  Tool = -> Fusion128
FEATURE [Part::Cut] Cut054  label="bottom012"
  Base = -> Cut052
  Tool = -> Fusion115
FEATURE [Sketcher::SketchObject] Sketch070
  FullyConstrained = true
  Placement = pos=(117,19,0) rot=(0.57735,0.57735,0.57735;2.0944rad)
  sketch-geometry (48):
    g0: LineSegment StartX=-49.19 StartY=69.25 StartZ=0 EndX=-49.19 EndY=66.25 EndZ=0
    g1: LineSegment StartX=-49.19 StartY=63.5 StartZ=0 EndX=-49.19 EndY=60.5 EndZ=0
    g2: LineSegment StartX=-49.19 StartY=57.75 StartZ=0 EndX=-49.19 EndY=54.75 EndZ=0
    g3: LineSegment StartX=-49.19 StartY=52 StartZ=0 EndX=-49.19 EndY=49 EndZ=0
    g4: LineSegment StartX=-49.19 StartY=46.25 StartZ=0 EndX=-49.19 EndY=43.25 EndZ=0
    g5: LineSegment StartX=-49.19 StartY=40.5 StartZ=0 EndX=-49.19 EndY=37.5 EndZ=0
    g6: LineSegment StartX=-49.19 StartY=34.5 StartZ=0 EndX=-49.19 EndY=31.5 EndZ=0
    g7: LineSegment StartX=-49.19 StartY=28.75 StartZ=0 EndX=-49.19 EndY=25.75 EndZ=0
    g8: LineSegment StartX=-49.19 StartY=23 StartZ=0 EndX=-49.19 EndY=20 EndZ=0
    g9: LineSegment StartX=-49.19 StartY=17.25 StartZ=0 EndX=-49.19 EndY=14.25 EndZ=0
    g10: LineSegment StartX=-49.19 StartY=11.5 StartZ=0 EndX=-49.19 EndY=8.5 EndZ=0
    g11: LineSegment StartX=-49.19 StartY=5.75 StartZ=0 EndX=-49.19 EndY=2.75 EndZ=0
    g12: ArcOfCircle CenterX=-1.5 CenterY=67.75 CenterZ=0 NormalX=0 NormalY=0 NormalZ=1 AngleXU=0 Radius=1.5 StartAngle=4.71239 EndAngle=7.85398
    g13: ArcOfCircle CenterX=-1.5 CenterY=62 CenterZ=0 NormalX=0 NormalY=0 NormalZ=1 AngleXU=0 Radius=1.5 StartAngle=4.71239 EndAngle=7.85398
    g14: ArcOfCircle CenterX=-1.5 CenterY=56.25 CenterZ=0 NormalX=0 NormalY=0 NormalZ=1 AngleXU=0 Radius=1.5 StartAngle=4.71239 EndAngle=7.85398
    g15: ArcOfCircle CenterX=-11.49 CenterY=50.5 CenterZ=0 NormalX=0 NormalY=0 NormalZ=1 AngleXU=0 Radius=1.5 StartAngle=4.71239 EndAngle=7.85398
    g16: ArcOfCircle CenterX=-16.28 CenterY=44.75 CenterZ=0 NormalX=0 NormalY=0 NormalZ=1 AngleXU=0 Radius=1.5 StartAngle=4.71239 EndAngle=7.85398
    g17: ArcOfCircle CenterX=-18.2337 CenterY=39 CenterZ=0 NormalX=0 NormalY=0 NormalZ=1 AngleXU=0 Radius=1.5 StartAngle=4.71485 EndAngle=7.85398
    g18: ArcOfCircle CenterX=-16.2837 CenterY=27.25 CenterZ=0 NormalX=0 NormalY=0 NormalZ=1 AngleXU=0 Radius=1.5 StartAngle=4.71485 EndAngle=7.85398
    g19: ArcOfCircle CenterX=-18.2337 CenterY=33 CenterZ=0 NormalX=0 NormalY=0 NormalZ=1 AngleXU=0 Radius=1.5 StartAngle=4.71485 EndAngle=7.85398
    g20: ArcOfCircle CenterX=-11.49 CenterY=21.5 CenterZ=0 NormalX=0 NormalY=0 NormalZ=1 AngleXU=0 Radius=1.5 StartAngle=4.71239 EndAngle=7.85398
    g21: ArcOfCircle CenterX=-1.5 CenterY=4.25 CenterZ=0 NormalX=0 NormalY=0 NormalZ=1 AngleXU=0 Radius=1.5 StartAngle=4.71239 EndAngle=7.85398
    g22: ArcOfCircle CenterX=-1.5 CenterY=10 CenterZ=0 NormalX=0 NormalY=0 NormalZ=1 AngleXU=0 Radius=1.5 StartAngle=4.71239 EndAngle=7.85398
    g23: ArcOfCircle CenterX=-1.5 CenterY=15.75 CenterZ=0 NormalX=0 NormalY=0 NormalZ=1 AngleXU=0 Radius=1.5 StartAngle=4.71239 EndAngle=7.85398
    g24: LineSegment StartX=-49.19 StartY=69.25 StartZ=0 EndX=-1.5 EndY=69.25 EndZ=0
    g25: LineSegment StartX=-49.19 StartY=66.25 StartZ=0 EndX=-1.5 EndY=66.25 EndZ=0
    g26: LineSegment StartX=-49.19 StartY=63.5 StartZ=0 EndX=-1.5 EndY=63.5 EndZ=0
    g27: LineSegment StartX=-49.19 StartY=60.5 StartZ=0 EndX=-1.5 EndY=60.5 EndZ=0
    g28: LineSegment StartX=-49.19 StartY=57.75 StartZ=0 EndX=-1.5 EndY=57.75 EndZ=0
    g29: LineSegment StartX=-49.19 StartY=54.75 StartZ=0 EndX=-1.5 EndY=54.75 EndZ=0
    g30: LineSegment StartX=-49.19 StartY=52 StartZ=0 EndX=-11.49 EndY=52 EndZ=0
    g31: LineSegment StartX=-49.19 StartY=49 StartZ=0 EndX=-11.49 EndY=49 EndZ=0
    g32: LineSegment StartX=-49.19 StartY=46.25 StartZ=0 EndX=-16.28 EndY=46.25 EndZ=0
    g33: LineSegment StartX=-49.19 StartY=43.25 StartZ=0 EndX=-16.28 EndY=43.25 EndZ=0
    g34: LineSegment StartX=-49.19 StartY=40.5 StartZ=0 EndX=-18.2337 EndY=40.5 EndZ=0
    g35: LineSegment StartX=-49.19 StartY=37.5 StartZ=0 EndX=-18.23 EndY=37.5 EndZ=0
    g36: LineSegment StartX=-49.19 StartY=34.5 StartZ=0 EndX=-18.2337 EndY=34.5 EndZ=0
    g37: LineSegment StartX=-49.19 StartY=31.5 StartZ=0 EndX=-18.23 EndY=31.5 EndZ=0
    g38: LineSegment StartX=-49.19 StartY=28.75 StartZ=0 EndX=-16.2837 EndY=28.75 EndZ=0
    g39: LineSegment StartX=-49.19 StartY=25.75 StartZ=0 EndX=-16.28 EndY=25.75 EndZ=0
    g40: LineSegment StartX=-49.19 StartY=23 StartZ=0 EndX=-11.49 EndY=23 EndZ=0
    g41: LineSegment StartX=-49.19 StartY=20 StartZ=0 EndX=-11.49 EndY=20 EndZ=0
    g42: LineSegment StartX=-49.19 StartY=17.25 StartZ=0 EndX=-1.5 EndY=17.25 EndZ=0
    g43: LineSegment StartX=-49.19 StartY=14.25 StartZ=0 EndX=-1.5 EndY=14.25 EndZ=0
    g44: LineSegment StartX=-49.19 StartY=11.5 StartZ=0 EndX=-1.5 EndY=11.5 EndZ=0
    g45: LineSegment StartX=-49.19 StartY=8.5 StartZ=0 EndX=-1.5 EndY=8.5 EndZ=0
    g46: LineSegment StartX=-49.19 StartY=5.75 StartZ=0 EndX=-1.5 EndY=5.75 EndZ=0
    g47: LineSegment StartX=-49.19 StartY=2.75 StartZ=0 EndX=-1.5 EndY=2.75 EndZ=0
  constraints (120):
    c: Vertical(g0)
    c: Distance(g0) = 3
    c: Block(g0)
    c: Vertical(g1)
    c: Distance(g1) = 3
    c: Vertical(g2)
    c: Equal(g0,g2) = 3
    c: Block(g2)
    c: Vertical(g3)
    c: Equal(g1,g3) = 3
    c: Vertical(g4)
    c: Equal(g0,g4) = 3
    c: Block(g4)
    c: Vertical(g5)
    c: Equal(g1,g5) = 3
    c: Vertical(g6)
    c: Equal(g0,g6) = 3
    c: Block(g6)
    c: Vertical(g7)
    c: Equal(g1,g7) = 3
    c: Vertical(g8)
    c: Equal(g0,g8) = 3
    c: Block(g8)
    c: Vertical(g9)
    c: Equal(g1,g9) = 3
    c: Vertical(g10)
    c: Equal(g0,g10) = 3
    c: Block(g10)
    c: Vertical(g11)
    c: Equal(g1,g11) = 3
    c: Block(g12)
    c: Block(g13)
    c: Block(g14)
    c: Block(g15)
    c: Block(g16)
    c: Block(g17)
    c: Block(g18)
    c: Block(g19)
    c: Block(g20)
    c: Block(g21)
    c: Block(g22)
    c: Block(g23)
    c: Block(g11)
    c: Block(g9)
    c: Block(g7)
    c: Block(g5)
    c: Block(g3)
    c: Block(g1)
    c: Coincident(g24,g0)
    c: Coincident(g24,g12)
    c: Horizontal(g24)
    c: Coincident(g25,g0)
    c: Coincident(g25,g12)
    c: Horizontal(g25)
    c: Coincident(g26,g1)
    c: Coincident(g26,g13)
    c: Horizontal(g26)
    c: Coincident(g27,g1)
    c: Coincident(g27,g13)
    c: Horizontal(g27)
    c: Coincident(g28,g2)
    c: Coincident(g28,g14)
    c: Horizontal(g28)
    c: Coincident(g29,g2)
    c: Coincident(g29,g14)
    c: Horizontal(g29)
    c: Coincident(g30,g3)
    c: Coincident(g30,g15)
    c: Horizontal(g30)
    c: Coincident(g31,g3)
    c: Coincident(g31,g15)
    c: Horizontal(g31)
    c: Coincident(g32,g4)
    c: Coincident(g32,g16)
    c: Horizontal(g32)
    c: Coincident(g33,g4)
    c: Coincident(g33,g16)
    c: Horizontal(g33)
    c: Coincident(g34,g5)
    c: Coincident(g34,g17)
    c: Horizontal(g34)
    c: Coincident(g35,g5)
    c: Coincident(g35,g17)
    c: Horizontal(g35)
    c: Coincident(g36,g6)
    c: Coincident(g36,g19)
    c: Horizontal(g36)
    c: Coincident(g37,g6)
    c: Coincident(g37,g19)
    c: Horizontal(g37)
    c: Coincident(g38,g7)
    c: Coincident(g38,g18)
    c: Horizontal(g38)
    c: Coincident(g39,g7)
    c: Coincident(g39,g18)
    c: Horizontal(g39)
    c: Coincident(g40,g8)
    c: Coincident(g40,g20)
    c: Horizontal(g40)
    c: Coincident(g41,g8)
    c: Coincident(g41,g20)
    c: Horizontal(g41)
    c: Coincident(g42,g9)
    c: Coincident(g42,g23)
    c: Horizontal(g42)
    c: Coincident(g43,g9)
    c: Coincident(g43,g23)
    c: Horizontal(g43)
    c: Coincident(g44,g10)
    c: Coincident(g44,g22)
    c: Horizontal(g44)
    c: Coincident(g45,g10)
    c: Coincident(g45,g22)
    c: Horizontal(g45)
    c: Coincident(g46,g11)
    c: Coincident(g46,g21)
    c: Horizontal(g46)
    c: Coincident(g47,g11)
    c: Coincident(g47,g21)
    c: Horizontal(g47)
FEATURE [Part::Extrusion] Extrude061
  Base = -> Sketch070
  Dir = (1,0,0)
  DirMode = 2
  FaceMakerClass = Part::FaceMakerBullseye
  LengthFwd = 23
  LengthRev = 0
  Placement = pos=(-19,0,0) rot=(0,0,1;0rad)
  Solid = true
  Symmetric = false
FEATURE [Part::Fillet] Fillet052  label="removeToCreateVentalationHoles002"
  Base = -> Extrude061
  Edges = <same value as first occurrence — deduplicated (x6 in doc)>
  Placement = pos=(7,0.02,0) rot=(0,0,1;0rad)
FEATURE [Part::MultiFuse] Fusion130  label="bottom013"
  Shapes = -> [Cut054,Cut034]
FEATURE [Part::Cut] Cut055
  Base = -> Fusion130
  Tool = -> Fillet052
FEATURE [Part::Cylinder] Cylinder054
  Angle = 360
  AttacherType = Attacher::AttachEngine3D
  Height = 20
  Placement = pos=(0,0,36.15) rot=(0,0,1;0rad)
  Radius = 4
FEATURE [Sketcher::SketchObject] Sketch071  label="bottomSketch002"
  FullyConstrained = true
  sketch-geometry (32):
    g0: LineSegment StartX=3.3 StartY=-6.03275e-07 StartZ=0 EndX=98 EndY=-6.03275e-07 EndZ=0
    g1: ArcOfCircle CenterX=98 CenterY=19 CenterZ=0 NormalX=0 NormalY=0 NormalZ=1 AngleXU=0 Radius=19 StartAngle=4.71239 EndAngle=5.71103
    g2: LineSegment StartX=6.3 StartY=8 StartZ=0 EndX=3.3 EndY=8 EndZ=0
    g3: LineSegment StartX=3.3 StartY=8 StartZ=0 EndX=3.3 EndY=-6.03275e-07 EndZ=0
    g4: ArcOfCircle CenterX=8.3 CenterY=5 CenterZ=0 NormalX=0 NormalY=0 NormalZ=1 AngleXU=0 Radius=2 StartAngle=3.14159 EndAngle=4.71239
    g5: LineSegment StartX=6.3 StartY=8 StartZ=0 EndX=6.3 EndY=5 EndZ=0
    g6: ArcOfCircle CenterX=98 CenterY=19 CenterZ=0 NormalX=0 NormalY=0 NormalZ=1 AngleXU=0 Radius=12.7 StartAngle=4.71239 EndAngle=6.28319
    g7: LineSegment StartX=94.7 StartY=3 StartZ=0 EndX=8.3 EndY=3 EndZ=0
    g8-g12: Circle x5 (B-spline internal-alignment scaffolding for g13; pole/knot coordinates omitted)
    g13: BSplineCurve PolesCount=5 KnotsCount=3 Degree=3 IsPeriodic=0
    g14: GeomPoint X=98 Y=6.3 Z=0
    g15: GeomPoint X=96.3938 Y=4.71946 Z=0
    g16: GeomPoint X=94.7 Y=3 Z=0
    g17-g23: Circle x7 (B-spline internal-alignment scaffolding for g24; pole/knot coordinates omitted)
    g24: BSplineCurve PolesCount=7 KnotsCount=5 Degree=3 IsPeriodic=0
    g25-g29: GeomPoint x5 (B-spline internal-alignment scaffolding for g24; pole/knot coordinates omitted)
    g30: ArcOfCircle CenterX=98 CenterY=19 CenterZ=0 NormalX=0 NormalY=0 NormalZ=1 AngleXU=0 Radius=15.7 StartAngle=5.81226 EndAngle=6.28319
    g31: LineSegment StartX=110.7 StartY=19 StartZ=0 EndX=113.7 EndY=19 EndZ=0
  constraints (41):
    c: Horizontal(g0)
    c: Coincident(g1,g0)
    c: Block(g1)
    c: Horizontal(g2)
    c: Distance(g2) = 3
    c: Coincident(g3,g2)
    c: Vertical(g3)
    c: Coincident(g3,g0)
    c: Block(g4)
    c: Block(g2)
    c: Coincident(g5,g2)
    c: Coincident(g5,g4)
    c: Vertical(g5)
    c: Coincident(g6,g1)
    c: Block(g6)
    c: Coincident(g7,g4)
    c: Horizontal(g7)
    c: Block(g0)
    c: Block(g7)
    c: Block(g3)
    c: Coincident(g13,g6)
    c: Weight(g8) = 1
    c: Equal(g8, g9-g12) x4
    c: Coincident(g13,g7)
    c: InternalAlignment(g8-g12 -> g13) x5
    c: InternalAlignment(g14,g13)
    c: InternalAlignment(g15,g13)
    c: InternalAlignment(g16,g13)
    c: Block(g13)
    c: Weight(g17) = 1
    c: Equal(g17, g18-g23) x6
    c: Coincident(g24,g1)
    c: InternalAlignment(g17-g23 -> g24) x7
    c: InternalAlignment(g25-g29 -> g24) x5
    c: Block(g24)
    c: Coincident(g30,g24)
    c: Coincident(g31,g6)
    c: Coincident(g31,g30)
    c: Horizontal(g31)
    c: Block(g31)
    c: Block(g30)
FEATURE [Part::Extrusion] Extrude062  label="bottom014"
  Base = -> Sketch071
  Dir = (0,0,1)
  DirMode = 2
  FaceMakerClass = Part::FaceMakerBullseye
  LengthFwd = 71.4
  LengthRev = 0
  Placement = pos=(0,0,0.3) rot=(0,0,1;0rad)
  Solid = true
  Symmetric = false
FEATURE [Part::Fillet] Fillet054
  Base = -> Extrude062
  Edges = 1 edges r=2.4: [Edge17]
FEATURE [Part::Fillet] Fillet055  label="bottom015"
  Base = -> Fillet054
  Edges = 1 edges r=2.4: [Edge36]
FEATURE [Part::Cylinder] Cylinder055
  Angle = 360
  AttacherType = Attacher::AttachEngine3D
  Height = 10
  Placement = pos=(0,0,36.15) rot=(0,0,1;0rad)
  Radius = 4
FEATURE [Part::MultiFuse] Fusion131  label="removeToCreateHoleForPlugHousing002"
  Placement = pos=(70,19,36.15) rot=(0,1,0;1.5708rad)
  Shapes = -> [Cylinder054,Cylinder055]
FEATURE [Part::Cut] Cut056  label="Bottom001"
  Base = -> Fillet055
  Placement = pos=(9,0,0) rot=(0,0,1;0rad)
  Tool = -> Fusion131
FEATURE [Part::Cut] Cut057
  Base = -> Cut055
  Tool = -> Cut056
FEATURE [Sketcher::SketchObject] Sketch072  label="topSketch021"
  FullyConstrained = true
  sketch-geometry (4):
    g0: ArcOfCircle CenterX=105 CenterY=19 CenterZ=0 NormalX=0 NormalY=0 NormalZ=1 AngleXU=0 Radius=20.6155 StartAngle=5.54125 EndAngle=6.28319
    g1: ArcOfCircle CenterX=105 CenterY=19 CenterZ=0 NormalX=0 NormalY=0 NormalZ=1 AngleXU=0 Radius=13 StartAngle=5.54125 EndAngle=6.28319
    g2: LineSegment StartX=118 StartY=19 StartZ=0 EndX=125.616 EndY=19 EndZ=0
    g3: LineSegment StartX=114.583 StartY=10.2157 StartZ=0 EndX=120.197 EndY=5.06982 EndZ=0
  constraints (7):
    c: Block(g0)
    c: Block(g1)
    c: Coincident(g2,g1)
    c: Coincident(g2,g0)
    c: Horizontal(g2)
    c: Coincident(g3,g1)
    c: Coincident(g3,g0)
FEATURE [Part::Extrusion] Extrude063  label="bottomPlugHousingBit003"
  Base = -> Sketch072
  Dir = (0,0,1)
  DirMode = 2
  FaceMakerClass = Part::FaceMakerBullseye
  LengthFwd = 72
  LengthRev = 0
  Solid = true
  Symmetric = false
FEATURE [Part::Cylinder] Cylinder056
  Angle = 360
  AttacherType = Attacher::AttachEngine3D
  Height = 20
  Placement = pos=(0,0,36.15) rot=(0,0,1;0rad)
  Radius = 14.3
FEATURE [Part::Cylinder] Cylinder057
  Angle = 360
  AttacherType = Attacher::AttachEngine3D
  Height = 10
  Placement = pos=(0,0,36.15) rot=(0,0,1;0rad)
  Radius = 4
FEATURE [Part::Box] Box034  label="removeToCreteHoleForPlugHousing047"
  AttacherType = Attacher::AttachEngine3D
  Height = 28.6
  Length = 20
  Placement = pos=(106.15,0,21.7) rot=(0,0,1;0rad)
  Width = 19
FEATURE [Part::Cylinder] Cylinder058
  Angle = 360
  AttacherType = Attacher::AttachEngine3D
  Height = 20
  Placement = pos=(0,0,36.15) rot=(0,0,1;0rad)
  Radius = 14.3
FEATURE [Part::Cylinder] Cylinder059
  Angle = 360
  AttacherType = Attacher::AttachEngine3D
  Height = 10
  Placement = pos=(0,0,36.15) rot=(0,0,1;0rad)
  Radius = 4
FEATURE [Part::MultiFuse] Fusion134  label="removeToCreteHoleForPlugHousing046"
  Placement = pos=(70,19,36) rot=(0,1,0;1.5708rad)
  Shapes = -> [Cylinder058,Cylinder059]
FEATURE [Part::Cylinder] Cylinder060
  Angle = 360
  AttacherType = Attacher::AttachEngine3D
  Height = 20
  Placement = pos=(0,0,36.15) rot=(0,0,1;0rad)
  Radius = 14
FEATURE [Part::Cylinder] Cylinder061
  Angle = 360
  AttacherType = Attacher::AttachEngine3D
  Height = 10
  Placement = pos=(0,0,36.15) rot=(0,0,1;0rad)
  Radius = 4
FEATURE [Part::MultiFuse] Fusion135  label="removeToCreteHoleForPlugHousing048"
  Placement = pos=(70,19,36) rot=(0,1,0;1.5708rad)
  Shapes = -> [Cylinder060,Cylinder061]
FEATURE [Part::Box] Box035  label="removeToCreteHoleForPlugHousing049"
  AttacherType = Attacher::AttachEngine3D
  Height = 28.6
  Length = 20
  Placement = pos=(106.15,0,21.7) rot=(0,0,1;0rad)
  Width = 19
FEATURE [Part::MultiFuse] Fusion133  label="removeToCreteHoleForPlugHousing045"
  Placement = pos=(0,0,-28.3) rot=(0,0,1;0rad)
  Shapes = -> [Box035,Fusion134]
FEATURE [Part::MultiFuse] Fusion138  label="removeToCreteHoleForPlugHousing051"
  Placement = pos=(70,19,36) rot=(0,1,0;1.5708rad)
  Shapes = -> [Cylinder056,Cylinder057]
FEATURE [Part::MultiFuse] Fusion137  label="removeToCreteHoleForPlugHousing050"
  Placement = pos=(0,0,28.3) rot=(0,0,1;0rad)
  Shapes = -> [Box034,Fusion138]
FEATURE [Part::MultiFuse] Fusion132  label="removeToCreatePlugHousingBottomBit002"
  Shapes = -> [Fusion133,Fusion137]
FEATURE [Part::MultiFuse] Fusion136  label="removeToCreatePlugHousingBottomBit003"
  Shapes = -> [Fusion135,Fusion132]
FEATURE [Part::Cut] Cut058  label="bottomPlugHousingBit002"
  Base = -> Extrude063
  Placement = pos=(-0.09,0,0) rot=(0,0,1;0rad)
  Tool = -> Fusion136
FEATURE [Sketcher::SketchObject] Sketch073  label="bottomSketch003"
  FullyConstrained = true
  sketch-geometry (45):
    g0: LineSegment StartX=6.29999 StartY=8 StartZ=0 EndX=3.29999 EndY=8 EndZ=0
    g1: LineSegment StartX=3.29999 StartY=8 StartZ=0 EndX=3.29999 EndY=-6.03275e-07 EndZ=0
    g2: ArcOfCircle CenterX=8.29999 CenterY=5 CenterZ=0 NormalX=0 NormalY=0 NormalZ=1 AngleXU=0 Radius=2 StartAngle=3.14159 EndAngle=4.71239
    g3: LineSegment StartX=6.29999 StartY=8 StartZ=0 EndX=6.29999 EndY=5 EndZ=0
    g4: ArcOfCircle CenterX=105 CenterY=19 CenterZ=0 NormalX=0 NormalY=0 NormalZ=1 AngleXU=0 Radius=12.7 StartAngle=4.71239 EndAngle=5.94289
    g5-g11: Circle x7 (B-spline internal-alignment scaffolding for g12; pole/knot coordinates omitted)
    g12: BSplineCurve PolesCount=7 KnotsCount=5 Degree=3 IsPeriodic=0
    g13-g17: GeomPoint x5 (B-spline internal-alignment scaffolding for g12; pole/knot coordinates omitted)
    g18: ArcOfCircle CenterX=105 CenterY=19 CenterZ=0 NormalX=0 NormalY=0 NormalZ=1 AngleXU=0 Radius=15.7 StartAngle=5.81226 EndAngle=6.28319
    g19: BSplineCurve PolesCount=5 KnotsCount=3 Degree=3 IsPeriodic=0
    g20: LineSegment StartX=8.29999 StartY=3 StartZ=0 EndX=101.7 EndY=3 EndZ=0
    g21: LineSegment StartX=3.29999 StartY=-6.03275e-07 StartZ=0 EndX=105 EndY=-6.03275e-07 EndZ=0
    g22: LineSegment StartX=120.974 StartY=8.71251 StartZ=0 EndX=122.332 EndY=7.83778 EndZ=0
    g23: LineSegment StartX=105 StartY=-6.03274e-07 StartZ=0 EndX=113 EndY=-6.03274e-07 EndZ=0
    g24: ArcOfCircle CenterX=105 CenterY=19 CenterZ=0 NormalX=0 NormalY=0 NormalZ=1 AngleXU=0 Radius=20.6155 StartAngle=5.11091 EndAngle=5.71103
    g25: ArcOfCircle CenterX=117.7 CenterY=19 CenterZ=0 NormalX=0 NormalY=0 NormalZ=1 AngleXU=0 Radius=3 StartAngle=1.2e-15 EndAngle=2.10468
    g26: Circle CenterX=116.345 CenterY=16.3232 CenterZ=0 NormalX=0 NormalY=0 NormalZ=1 AngleXU=0 Radius=1
    g27: Circle CenterX=117.24 CenterY=15.7584 CenterZ=0 NormalX=0 NormalY=0 NormalZ=1 AngleXU=0 Radius=1
    g28: Circle CenterX=116.972 CenterY=14.7612 CenterZ=0 NormalX=0 NormalY=0 NormalZ=1 AngleXU=0 Radius=1
    g29: BSplineCurve PolesCount=3 KnotsCount=2 Degree=2 IsPeriodic=0
    g30: GeomPoint X=116.345 Y=16.3232 Z=0
    g31: GeomPoint X=116.972 Y=14.7612 Z=0
    g32: Circle CenterX=115.828 CenterY=17.157 CenterZ=0 NormalX=0 NormalY=0 NormalZ=1 AngleXU=0 Radius=1
    g33: Circle CenterX=115.841 CenterY=16.639 CenterZ=0 NormalX=0 NormalY=0 NormalZ=1 AngleXU=0 Radius=1
    g34: Circle CenterX=116.345 CenterY=16.3232 CenterZ=0 NormalX=0 NormalY=0 NormalZ=1 AngleXU=0 Radius=1
    g35: BSplineCurve PolesCount=3 KnotsCount=2 Degree=2 IsPeriodic=0
    g36: GeomPoint X=115.828 Y=17.157 Z=0
    g37: GeomPoint X=116.345 Y=16.3232 Z=0
    g38: LineSegment StartX=115.828 StartY=17.157 StartZ=0 EndX=115.828 EndY=20.8307 EndZ=0
    g39: Circle CenterX=115.828 CenterY=20.8307 CenterZ=0 NormalX=0 NormalY=0 NormalZ=1 AngleXU=0 Radius=1
    g40: Circle CenterX=115.831 CenterY=21.3396 CenterZ=0 NormalX=0 NormalY=0 NormalZ=1 AngleXU=0 Radius=1
    g41: Circle CenterX=116.173 CenterY=21.5825 CenterZ=0 NormalX=0 NormalY=0 NormalZ=1 AngleXU=0 Radius=1
    g42: BSplineCurve PolesCount=3 KnotsCount=2 Degree=2 IsPeriodic=0
    g43: GeomPoint X=115.828 Y=20.8307 Z=0
    g44: GeomPoint X=116.173 Y=21.5825 Z=0
  constraints (70):
    c: Horizontal(g0)
    c: Distance(g0) = 3
    c: Coincident(g1,g0)
    c: Vertical(g1)
    c: Block(g2)
    c: Block(g0)
    c: Coincident(g3,g0)
    c: Coincident(g3,g2)
    c: Vertical(g3)
    c: Block(g1)
    c: Block(g4)
    c: Coincident(g19,g4)
    c: Block(g19)
    c: Equal(g5, g6-g11) x6
    c: InternalAlignment(g5-g11 -> g12) x7
    c: InternalAlignment(g13-g17 -> g12) x5
    c: Block(g12)
    c: Coincident(g18,g12)
    c: Block(g18)
    c: Coincident(g20,g2)
    c: Coincident(g20,g19)
    c: Horizontal(g20)
    c: Distance(g20) = 93.4
    c: Coincident(g21,g1)
    c: Horizontal(g21)
    c: Distance(g21) = 101.7
    c: Horizontal(g23)
    c: Distance(g23) = 8
    c: Coincident(g24,g23)
    c: Block(g23)
    c: Coincident(g22,g24)
    c: Block(g24)
    c: Block(g22)
    c: Distance(g22) = 1.61553
    c: Coincident(g25,g18)
    c: Block(g25)
    c: Weight(g26) = 1
    c: Equal(g26,g27)
    c: Equal(g26,g28)
    c: Coincident(g29,g4)
    c: InternalAlignment(g26,g29)
    c: InternalAlignment(g27,g29)
    c: InternalAlignment(g28,g29)
    c: InternalAlignment(g30,g29)
    c: InternalAlignment(g31,g29)
    c: Block(g29)
    c: Weight(g32) = 1
    c: Equal(g32,g33)
    c: Equal(g32,g34)
    c: Coincident(g35,g29)
    c: InternalAlignment(g32,g35)
    c: InternalAlignment(g33,g35)
    c: InternalAlignment(g34,g35)
    c: InternalAlignment(g36,g35)
    c: InternalAlignment(g37,g35)
    c: Block(g35)
    c: Coincident(g38,g35)
    c: Vertical(g38)
    c: Block(g38)
    c: Coincident(g42,g38)
    c: Weight(g39) = 1
    c: Equal(g39,g40)
    c: Equal(g39,g41)
    c: Coincident(g42,g25)
    c: InternalAlignment(g39,g42)
    c: InternalAlignment(g40,g42)
    c: InternalAlignment(g41,g42)
    c: InternalAlignment(g43,g42)
    c: InternalAlignment(g44,g42)
    c: Block(g42)
FEATURE [Part::Extrusion] Extrude064  label="bottom016"
  Base = -> Sketch073
  Dir = (0,0,1)
  DirMode = 2
  FaceMakerClass = Part::FaceMakerBullseye
  LengthFwd = 71.4
  LengthRev = 0
  Placement = pos=(0,0,0.3) rot=(0,0,1;0rad)
  Solid = true
  Symmetric = false
FEATURE [Part::Revolution] Revolve157  label="removeToCreateScrewAndThreadedInsertHole063"
  Angle = 360
  Axis = (0,1,0)
  Base = (0,0,0)
  FaceMakerClass = Part::FaceMakerBullseye
  Placement = pos=(12.5,0,10) rot=(0,0,1;0rad)
  Solid = false
  Source = -> Face141
  Symmetric = false
FEATURE [Sketcher::SketchObject] Sketch074
  FullyConstrained = true
  Placement = pos=(117,19,0) rot=(0.57735,0.57735,0.57735;2.0944rad)
  sketch-geometry (48):
    g0: LineSegment StartX=-49.19 StartY=69.25 StartZ=0 EndX=-49.19 EndY=66.25 EndZ=0
    g1: LineSegment StartX=-49.19 StartY=63.5 StartZ=0 EndX=-49.19 EndY=60.5 EndZ=0
    g2: LineSegment StartX=-49.19 StartY=57.75 StartZ=0 EndX=-49.19 EndY=54.75 EndZ=0
    g3: LineSegment StartX=-49.19 StartY=52 StartZ=0 EndX=-49.19 EndY=49 EndZ=0
    g4: LineSegment StartX=-49.19 StartY=46.25 StartZ=0 EndX=-49.19 EndY=43.25 EndZ=0
    g5: LineSegment StartX=-49.19 StartY=40.5 StartZ=0 EndX=-49.19 EndY=37.5 EndZ=0
    g6: LineSegment StartX=-49.19 StartY=34.5 StartZ=0 EndX=-49.19 EndY=31.5 EndZ=0
    g7: LineSegment StartX=-49.19 StartY=28.75 StartZ=0 EndX=-49.19 EndY=25.75 EndZ=0
    g8: LineSegment StartX=-49.19 StartY=23 StartZ=0 EndX=-49.19 EndY=20 EndZ=0
    g9: LineSegment StartX=-49.19 StartY=17.25 StartZ=0 EndX=-49.19 EndY=14.25 EndZ=0
    g10: LineSegment StartX=-49.19 StartY=11.5 StartZ=0 EndX=-49.19 EndY=8.5 EndZ=0
    g11: LineSegment StartX=-49.19 StartY=5.75 StartZ=0 EndX=-49.19 EndY=2.75 EndZ=0
    g12: ArcOfCircle CenterX=-1.5 CenterY=67.75 CenterZ=0 NormalX=0 NormalY=0 NormalZ=1 AngleXU=0 Radius=1.5 StartAngle=4.71239 EndAngle=7.85398
    g13: ArcOfCircle CenterX=-1.5 CenterY=62 CenterZ=0 NormalX=0 NormalY=0 NormalZ=1 AngleXU=0 Radius=1.5 StartAngle=4.71239 EndAngle=7.85398
    g14: ArcOfCircle CenterX=-1.5 CenterY=56.25 CenterZ=0 NormalX=0 NormalY=0 NormalZ=1 AngleXU=0 Radius=1.5 StartAngle=4.71239 EndAngle=7.85398
    g15: ArcOfCircle CenterX=-11.49 CenterY=50.5 CenterZ=0 NormalX=0 NormalY=0 NormalZ=1 AngleXU=0 Radius=1.5 StartAngle=4.71239 EndAngle=7.85398
    g16: ArcOfCircle CenterX=-16.28 CenterY=44.75 CenterZ=0 NormalX=0 NormalY=0 NormalZ=1 AngleXU=0 Radius=1.5 StartAngle=4.71239 EndAngle=7.85398
    g17: ArcOfCircle CenterX=-18.2337 CenterY=39 CenterZ=0 NormalX=0 NormalY=0 NormalZ=1 AngleXU=0 Radius=1.5 StartAngle=4.71485 EndAngle=7.85398
    g18: ArcOfCircle CenterX=-16.2837 CenterY=27.25 CenterZ=0 NormalX=0 NormalY=0 NormalZ=1 AngleXU=0 Radius=1.5 StartAngle=4.71485 EndAngle=7.85398
    g19: ArcOfCircle CenterX=-18.2337 CenterY=33 CenterZ=0 NormalX=0 NormalY=0 NormalZ=1 AngleXU=0 Radius=1.5 StartAngle=4.71485 EndAngle=7.85398
    g20: ArcOfCircle CenterX=-11.49 CenterY=21.5 CenterZ=0 NormalX=0 NormalY=0 NormalZ=1 AngleXU=0 Radius=1.5 StartAngle=4.71239 EndAngle=7.85398
    g21: ArcOfCircle CenterX=-1.5 CenterY=4.25 CenterZ=0 NormalX=0 NormalY=0 NormalZ=1 AngleXU=0 Radius=1.5 StartAngle=4.71239 EndAngle=7.85398
    g22: ArcOfCircle CenterX=-1.5 CenterY=10 CenterZ=0 NormalX=0 NormalY=0 NormalZ=1 AngleXU=0 Radius=1.5 StartAngle=4.71239 EndAngle=7.85398
    g23: ArcOfCircle CenterX=-1.5 CenterY=15.75 CenterZ=0 NormalX=0 NormalY=0 NormalZ=1 AngleXU=0 Radius=1.5 StartAngle=4.71239 EndAngle=7.85398
    g24: LineSegment StartX=-49.19 StartY=69.25 StartZ=0 EndX=-1.5 EndY=69.25 EndZ=0
    g25: LineSegment StartX=-49.19 StartY=66.25 StartZ=0 EndX=-1.5 EndY=66.25 EndZ=0
    g26: LineSegment StartX=-49.19 StartY=63.5 StartZ=0 EndX=-1.5 EndY=63.5 EndZ=0
    g27: LineSegment StartX=-49.19 StartY=60.5 StartZ=0 EndX=-1.5 EndY=60.5 EndZ=0
    g28: LineSegment StartX=-49.19 StartY=57.75 StartZ=0 EndX=-1.5 EndY=57.75 EndZ=0
    g29: LineSegment StartX=-49.19 StartY=54.75 StartZ=0 EndX=-1.5 EndY=54.75 EndZ=0
    g30: LineSegment StartX=-49.19 StartY=52 StartZ=0 EndX=-11.49 EndY=52 EndZ=0
    g31: LineSegment StartX=-49.19 StartY=49 StartZ=0 EndX=-11.49 EndY=49 EndZ=0
    g32: LineSegment StartX=-49.19 StartY=46.25 StartZ=0 EndX=-16.28 EndY=46.25 EndZ=0
    g33: LineSegment StartX=-49.19 StartY=43.25 StartZ=0 EndX=-16.28 EndY=43.25 EndZ=0
    g34: LineSegment StartX=-49.19 StartY=40.5 StartZ=0 EndX=-18.2337 EndY=40.5 EndZ=0
    g35: LineSegment StartX=-49.19 StartY=37.5 StartZ=0 EndX=-18.23 EndY=37.5 EndZ=0
    g36: LineSegment StartX=-49.19 StartY=34.5 StartZ=0 EndX=-18.2337 EndY=34.5 EndZ=0
    g37: LineSegment StartX=-49.19 StartY=31.5 StartZ=0 EndX=-18.23 EndY=31.5 EndZ=0
    g38: LineSegment StartX=-49.19 StartY=28.75 StartZ=0 EndX=-16.2837 EndY=28.75 EndZ=0
    g39: LineSegment StartX=-49.19 StartY=25.75 StartZ=0 EndX=-16.28 EndY=25.75 EndZ=0
    g40: LineSegment StartX=-49.19 StartY=23 StartZ=0 EndX=-11.49 EndY=23 EndZ=0
    g41: LineSegment StartX=-49.19 StartY=20 StartZ=0 EndX=-11.49 EndY=20 EndZ=0
    g42: LineSegment StartX=-49.19 StartY=17.25 StartZ=0 EndX=-1.5 EndY=17.25 EndZ=0
    g43: LineSegment StartX=-49.19 StartY=14.25 StartZ=0 EndX=-1.5 EndY=14.25 EndZ=0
    g44: LineSegment StartX=-49.19 StartY=11.5 StartZ=0 EndX=-1.5 EndY=11.5 EndZ=0
    g45: LineSegment StartX=-49.19 StartY=8.5 StartZ=0 EndX=-1.5 EndY=8.5 EndZ=0
    g46: LineSegment StartX=-49.19 StartY=5.75 StartZ=0 EndX=-1.5 EndY=5.75 EndZ=0
    g47: LineSegment StartX=-49.19 StartY=2.75 StartZ=0 EndX=-1.5 EndY=2.75 EndZ=0
  constraints (120):
    c: Vertical(g0)
    c: Distance(g0) = 3
    c: Block(g0)
    c: Vertical(g1)
    c: Distance(g1) = 3
    c: Vertical(g2)
    c: Equal(g0,g2) = 3
    c: Block(g2)
    c: Vertical(g3)
    c: Equal(g1,g3) = 3
    c: Vertical(g4)
    c: Equal(g0,g4) = 3
    c: Block(g4)
    c: Vertical(g5)
    c: Equal(g1,g5) = 3
    c: Vertical(g6)
    c: Equal(g0,g6) = 3
    c: Block(g6)
    c: Vertical(g7)
    c: Equal(g1,g7) = 3
    c: Vertical(g8)
    c: Equal(g0,g8) = 3
    c: Block(g8)
    c: Vertical(g9)
    c: Equal(g1,g9) = 3
    c: Vertical(g10)
    c: Equal(g0,g10) = 3
    c: Block(g10)
    c: Vertical(g11)
    c: Equal(g1,g11) = 3
    c: Block(g12)
    c: Block(g13)
    c: Block(g14)
    c: Block(g15)
    c: Block(g16)
    c: Block(g17)
    c: Block(g18)
    c: Block(g19)
    c: Block(g20)
    c: Block(g21)
    c: Block(g22)
    c: Block(g23)
    c: Block(g11)
    c: Block(g9)
    c: Block(g7)
    c: Block(g5)
    c: Block(g3)
    c: Block(g1)
    c: Coincident(g24,g0)
    c: Coincident(g24,g12)
    c: Horizontal(g24)
    c: Coincident(g25,g0)
    c: Coincident(g25,g12)
    c: Horizontal(g25)
    c: Coincident(g26,g1)
    c: Coincident(g26,g13)
    c: Horizontal(g26)
    c: Coincident(g27,g1)
    c: Coincident(g27,g13)
    c: Horizontal(g27)
    c: Coincident(g28,g2)
    c: Coincident(g28,g14)
    c: Horizontal(g28)
    c: Coincident(g29,g2)
    c: Coincident(g29,g14)
    c: Horizontal(g29)
    c: Coincident(g30,g3)
    c: Coincident(g30,g15)
    c: Horizontal(g30)
    c: Coincident(g31,g3)
    c: Coincident(g31,g15)
    c: Horizontal(g31)
    c: Coincident(g32,g4)
    c: Coincident(g32,g16)
    c: Horizontal(g32)
    c: Coincident(g33,g4)
    c: Coincident(g33,g16)
    c: Horizontal(g33)
    c: Coincident(g34,g5)
    c: Coincident(g34,g17)
    c: Horizontal(g34)
    c: Coincident(g35,g5)
    c: Coincident(g35,g17)
    c: Horizontal(g35)
    c: Coincident(g36,g6)
    c: Coincident(g36,g19)
    c: Horizontal(g36)
    c: Coincident(g37,g6)
    c: Coincident(g37,g19)
    c: Horizontal(g37)
    c: Coincident(g38,g7)
    c: Coincident(g38,g18)
    c: Horizontal(g38)
    c: Coincident(g39,g7)
    c: Coincident(g39,g18)
    c: Horizontal(g39)
    c: Coincident(g40,g8)
    c: Coincident(g40,g20)
    c: Horizontal(g40)
    c: Coincident(g41,g8)
    c: Coincident(g41,g20)
    c: Horizontal(g41)
    c: Coincident(g42,g9)
    c: Coincident(g42,g23)
    c: Horizontal(g42)
    c: Coincident(g43,g9)
    c: Coincident(g43,g23)
    c: Horizontal(g43)
    c: Coincident(g44,g10)
    c: Coincident(g44,g22)
    c: Horizontal(g44)
    c: Coincident(g45,g10)
    c: Coincident(g45,g22)
    c: Horizontal(g45)
    c: Coincident(g46,g11)
    c: Coincident(g46,g21)
    c: Horizontal(g46)
    c: Coincident(g47,g11)
    c: Coincident(g47,g21)
    c: Horizontal(g47)
FEATURE [Part::Extrusion] Extrude065
  Base = -> Sketch074
  Dir = (1,0,0)
  DirMode = 2
  FaceMakerClass = Part::FaceMakerBullseye
  LengthFwd = 23
  LengthRev = 0
  Placement = pos=(-19,0,0) rot=(0,0,1;0rad)
  Solid = true
  Symmetric = false
FEATURE [Part::Fillet] Fillet056  label="removeToCreateVentalationHoles003"
  Base = -> Extrude065
  Edges = <same value as first occurrence — deduplicated (x6 in doc)>
  Placement = pos=(7,0.02,0) rot=(0,0,1;0rad)
FEATURE [Part::Revolution] Revolve158  label="removeToCreateScrewAndThreadedInsertHole065"
  Angle = 360
  Axis = (0,1,0)
  Base = (0,0,0)
  FaceMakerClass = Part::FaceMakerBullseye
  Placement = pos=(12.5,0,62) rot=(0,0,1;0rad)
  Solid = false
  Source = -> Face146
  Symmetric = false
FEATURE [Part::Revolution] Revolve159  label="removeToCreateScrewAndThreadedInsertHole066"
  Angle = 360
  Axis = (0,1,0)
  Base = (0,0,0)
  FaceMakerClass = Part::FaceMakerBullseye
  Placement = pos=(89.5,0,68.5) rot=(0,0,1;0rad)
  Solid = false
  Source = -> Face143
  Symmetric = false
FEATURE [Part::Revolution] Revolve160  label="removeToCreateScrewAndThreadedInsertHole067"
  Angle = 360
  Axis = (0,1,0)
  Base = (0,0,0)
  FaceMakerClass = Part::FaceMakerBullseye
  Placement = pos=(89.5,0,3.5) rot=(0,0,1;0rad)
  Solid = false
  Source = -> Face142
  Symmetric = false
FEATURE [Part::Revolution] Revolve161  label="removeToCreateScrewAndThreadedInsertHole068"
  Angle = 360
  Axis = (0,1,0)
  Base = (0,0,0)
  FaceMakerClass = Part::FaceMakerBullseye
  Placement = pos=(109.5,4.7,3.5) rot=(0,0,1;0rad)
  Solid = false
  Source = -> Face145
  Symmetric = false
FEATURE [Part::Revolution] Revolve162  label="removeToCreateScrewAndThreadedInsertHole069"
  Angle = 360
  Axis = (0,1,0)
  Base = (0,0,0)
  FaceMakerClass = Part::FaceMakerBullseye
  Placement = pos=(109.5,4.7,68.5) rot=(0,0,1;0rad)
  Solid = false
  Source = -> Face144
  Symmetric = false
FEATURE [Part::MultiFuse] Fusion141  label="removeToCreateScrewAndThreadedInsertHole064"
  Shapes = -> [Revolve162,Revolve161,Revolve160,Revolve159,Revolve158,Revolve157]
FEATURE [Part::Cylinder] Cylinder062
  Angle = 360
  AttacherType = Attacher::AttachEngine3D
  Height = 20
  Placement = pos=(0,0,36.15) rot=(0,0,1;0rad)
  Radius = 14
FEATURE [Part::Cylinder] Cylinder063
  Angle = 360
  AttacherType = Attacher::AttachEngine3D
  Height = 10
  Placement = pos=(0,0,36.15) rot=(0,0,1;0rad)
  Radius = 4
FEATURE [Part::MultiFuse] Fusion139  label="removeToCreteHoleForPlugHousing052"
  Placement = pos=(70,19,36) rot=(0,1,0;1.5708rad)
  Shapes = -> [Cylinder062,Cylinder063]
FEATURE [Part::Cut] Cut060  label="bottom017"
  Base = -> Extrude064
  Tool = -> Fusion139
FEATURE [Part::Cut] Cut061  label="bottom019"
  Base = -> Cut060
  Tool = -> Fusion141
FEATURE [Part::MultiFuse] Fusion140  label="bottom018"
  Shapes = -> [Cut061,Cut058]
FEATURE [Part::Cut] Cut059  label="bottom020"
  Base = -> Fusion140
  Tool = -> Fillet056
FEATURE [Part::Box] Box036  label="Cube021"
  AttacherType = Attacher::AttachEngine3D
  Height = 80
  Length = 26
  Placement = pos=(0,-1,-5) rot=(0,0,1;0rad)
  Width = 11
FEATURE [Part::Cut] Cut062  label="removeFromBottom002"
  Base = -> Cut057
  Tool = -> Box036
FEATURE [Part::Cut] Cut063
  Base = -> Cut059
  Tool = -> Cut062
FEATURE [Part::Cut] Cut064  label="pcbStands"
  Base = -> Fusion095
  Tool = -> Fusion127
FEATURE [Sketcher::SketchObject] Sketch075  label="topSketch022"
  FullyConstrained = true
  sketch-geometry (6):
    g0: LineSegment StartX=19 StartY=38 StartZ=0 EndX=117 EndY=38 EndZ=0
    g1: ArcOfCircle CenterX=19 CenterY=19 CenterZ=0 NormalX=0 NormalY=0 NormalZ=1 AngleXU=0 Radius=19 StartAngle=1.5708 EndAngle=3.14159
    g2: LineSegment StartX=117 StartY=38 StartZ=0 EndX=117 EndY=19 EndZ=0
    g3: LineSegment StartX=98 StartY=1.0161e-12 StartZ=0 EndX=5.22862e-06 EndY=1.0161e-12 EndZ=0
    g4: LineSegment StartX=5.22862e-06 StartY=19 StartZ=0 EndX=5.22862e-06 EndY=1.0161e-12 EndZ=0
    g5: ArcOfCircle CenterX=98 CenterY=19 CenterZ=0 NormalX=0 NormalY=0 NormalZ=1 AngleXU=0 Radius=19 StartAngle=4.71239 EndAngle=6.28319
  constraints (16):
    c: Horizontal(g0)
    c: Distance(g0) = 98
    c: Coincident(g1,g0)
    c: Block(g1)
    c: Coincident(g2,g0)
    c: Vertical(g2)
    c: Distance(g2) = 19
    c: Horizontal(g3)
    c: Coincident(g4,g1)
    c: Vertical(g4)
    c: Coincident(g3,g4)
    c: Block(g3)
    c: Coincident(g5,g2)
    c: Coincident(g5,g3)
    c: Block(g0)
    c: Block(g5)
FEATURE [Part::Extrusion] Extrude067  label="sideB003"
  Base = -> Sketch075
  Dir = (0,0,1)
  DirMode = 2
  FaceMakerClass = Part::FaceMakerBullseye
  LengthFwd = 3
  LengthRev = 0
  Placement = pos=(0,0,71.7) rot=(0,0,1;0rad)
  Solid = true
  Symmetric = false
FEATURE [Sketcher::SketchObject] Sketch076  label="topSketch023"
  FullyConstrained = true
  sketch-geometry (6):
    g0: LineSegment StartX=19 StartY=38 StartZ=0 EndX=117 EndY=38 EndZ=0
    g1: ArcOfCircle CenterX=19 CenterY=19 CenterZ=0 NormalX=0 NormalY=0 NormalZ=1 AngleXU=0 Radius=19 StartAngle=1.5708 EndAngle=3.14159
    g2: LineSegment StartX=117 StartY=38 StartZ=0 EndX=117 EndY=19 EndZ=0
    g3: LineSegment StartX=98 StartY=1.0161e-12 StartZ=0 EndX=5.22862e-06 EndY=1.0161e-12 EndZ=0
    g4: LineSegment StartX=5.22862e-06 StartY=19 StartZ=0 EndX=5.22862e-06 EndY=1.0161e-12 EndZ=0
    g5: ArcOfCircle CenterX=98 CenterY=19 CenterZ=0 NormalX=0 NormalY=0 NormalZ=1 AngleXU=0 Radius=19 StartAngle=4.71239 EndAngle=6.28319
  constraints (16):
    c: Horizontal(g0)
    c: Distance(g0) = 98
    c: Coincident(g1,g0)
    c: Block(g1)
    c: Coincident(g2,g0)
    c: Vertical(g2)
    c: Distance(g2) = 19
    c: Horizontal(g3)
    c: Coincident(g4,g1)
    c: Vertical(g4)
    c: Coincident(g3,g4)
    c: Block(g3)
    c: Coincident(g5,g2)
    c: Coincident(g5,g3)
    c: Block(g0)
    c: Block(g5)
FEATURE [Part::Extrusion] Extrude066  label="sideA003"
  Base = -> Sketch076
  Dir = (0,0,1)
  DirMode = 2
  FaceMakerClass = Part::FaceMakerBullseye
  LengthFwd = 3
  LengthRev = 0
  Placement = pos=(0,0,-2.7) rot=(0,0,1;0rad)
  Solid = true
  Symmetric = false
FEATURE [Part::MultiFuse] Fusion142  label="removeFromBottom003"
  Placement = pos=(2,0,0) rot=(0,0,1;0rad)
  Shapes = -> [Extrude066,Extrude067]
FEATURE [Part::Cut] Cut065  label="screwRetainers002"
  Base = -> Fusion096
  Tool = -> Fusion142
FEATURE [Sketcher::SketchObject] Sketch077
  FullyConstrained = true
  Placement = pos=(117,19,0) rot=(0.57735,0.57735,0.57735;2.0944rad)
  sketch-geometry (8):
    g0: LineSegment StartX=-49.19 StartY=63.5 StartZ=0 EndX=-49.19 EndY=60.5 EndZ=0
    g1: LineSegment StartX=-49.19 StartY=11.5 StartZ=0 EndX=-49.19 EndY=8.5 EndZ=0
    g2: ArcOfCircle CenterX=-1.5 CenterY=62 CenterZ=0 NormalX=0 NormalY=0 NormalZ=1 AngleXU=0 Radius=1.5 StartAngle=4.71239 EndAngle=7.85398
    g3: ArcOfCircle CenterX=-1.5 CenterY=10 CenterZ=0 NormalX=0 NormalY=0 NormalZ=1 AngleXU=0 Radius=1.5 StartAngle=4.71239 EndAngle=7.85398
    g4: LineSegment StartX=-49.19 StartY=63.5 StartZ=0 EndX=-1.5 EndY=63.5 EndZ=0
    g5: LineSegment StartX=-49.19 StartY=60.5 StartZ=0 EndX=-1.5 EndY=60.5 EndZ=0
    g6: LineSegment StartX=-49.19 StartY=11.5 StartZ=0 EndX=-1.5 EndY=11.5 EndZ=0
    g7: LineSegment StartX=-49.19 StartY=8.5 StartZ=0 EndX=-1.5 EndY=8.5 EndZ=0
  constraints (19):
    c: Vertical(g0)
    c: Distance(g0) = 3
    c: Vertical(g1)
    c: Block(g1)
    c: Block(g2)
    c: Block(g3)
    c: Block(g0)
    c: Coincident(g4,g0)
    c: Coincident(g4,g2)
    c: Horizontal(g4)
    c: Coincident(g5,g0)
    c: Coincident(g5,g2)
    c: Horizontal(g5)
    c: Coincident(g6,g1)
    c: Coincident(g6,g3)
    c: Horizontal(g6)
    c: Coincident(g7,g1)
    c: Coincident(g7,g3)
    c: Horizontal(g7)
FEATURE [Part::Extrusion] Extrude068
  Base = -> Sketch077
  Dir = (1,0,0)
  DirMode = 2
  FaceMakerClass = Part::FaceMakerBullseye
  LengthFwd = 10
  LengthRev = 0
  Solid = true
  Symmetric = false
FEATURE [Part::Fillet] Fillet057  label="removeFromtMoreFrontCaseScrewRetainers002"
  Base = -> Extrude068
  Edges = 4 edges r=1.49: [Edge6,Edge11,Edge18,Edge23]
  Placement = pos=(-12,0,0) rot=(0,0,1;0rad)
FEATURE [Sketcher::SketchObject] Sketch078
  FullyConstrained = true
  Placement = pos=(117,19,0) rot=(0.57735,0.57735,0.57735;2.0944rad)
  sketch-geometry (8):
    g0: LineSegment StartX=-49.19 StartY=69.25 StartZ=0 EndX=-49.19 EndY=66.25 EndZ=0
    g1: LineSegment StartX=-49.19 StartY=5.75 StartZ=0 EndX=-49.19 EndY=2.75 EndZ=0
    g2: ArcOfCircle CenterX=-1.5 CenterY=67.75 CenterZ=0 NormalX=0 NormalY=0 NormalZ=1 AngleXU=0 Radius=1.5 StartAngle=4.71239 EndAngle=7.85398
    g3: ArcOfCircle CenterX=-1.5 CenterY=4.25 CenterZ=0 NormalX=0 NormalY=0 NormalZ=1 AngleXU=0 Radius=1.5 StartAngle=4.71239 EndAngle=7.85398
    g4: LineSegment StartX=-49.19 StartY=69.25 StartZ=0 EndX=-1.5 EndY=69.25 EndZ=0
    g5: LineSegment StartX=-49.19 StartY=66.25 StartZ=0 EndX=-1.5 EndY=66.25 EndZ=0
    g6: LineSegment StartX=-49.19 StartY=5.75 StartZ=0 EndX=-1.5 EndY=5.75 EndZ=0
    g7: LineSegment StartX=-49.19 StartY=2.75 StartZ=0 EndX=-1.5 EndY=2.75 EndZ=0
  constraints (19):
    c: Vertical(g0)
    c: Distance(g0) = 3
    c: Block(g0)
    c: Vertical(g1)
    c: Block(g2)
    c: Block(g3)
    c: Block(g1)
    c: Coincident(g4,g0)
    c: Coincident(g4,g2)
    c: Horizontal(g4)
    c: Coincident(g5,g0)
    c: Coincident(g5,g2)
    c: Horizontal(g5)
    c: Coincident(g6,g1)
    c: Coincident(g6,g3)
    c: Horizontal(g6)
    c: Coincident(g7,g1)
    c: Coincident(g7,g3)
    c: Horizontal(g7)
FEATURE [Part::Extrusion] Extrude069
  Base = -> Sketch078
  Dir = (1,0,0)
  DirMode = 2
  FaceMakerClass = Part::FaceMakerBullseye
  LengthFwd = 10
  LengthRev = 0
  Solid = true
  Symmetric = false
FEATURE [Part::Fillet] Fillet058  label="removeFromtMoreFrontCaseScrewRetainers003"
  Base = -> Extrude069
  Edges = 4 edges r=1.49: [Edge6,Edge11,Edge18,Edge23]
  Placement = pos=(-4,0,0) rot=(0,0,1;0rad)
FEATURE [Part::Cut] Cut066
  Base = -> Cut065
  Tool = -> Fillet058
FEATURE [Part::Cut] Cut067  label="screwPillars"
  Base = -> Cut066
  Tool = -> Fillet057
FEATURE [Part::MultiFuse] Fusion143  label="bottom021"
  Shapes = -> [Cut031,Cut063]
FEATURE [Part::Cylinder] Cylinder
  Angle = 360
  AttacherType = Attacher::AttachEngine3D
  Height = 10
  Placement = pos=(20.65,12,4.68) rot=(1,0,0;1.5708rad)
  Radius = 2
FEATURE [Part::Cylinder] Cylinder064
  Angle = 360
  AttacherType = Attacher::AttachEngine3D
  Height = 10
  Placement = pos=(20.65,12,67.38) rot=(1,0,0;1.5708rad)
  Radius = 2
FEATURE [Part::Cylinder] Cylinder065
  Angle = 360
  AttacherType = Attacher::AttachEngine3D
  Height = 10
  Placement = pos=(77.15,12,67.38) rot=(1,0,0;1.5708rad)
  Radius = 2
FEATURE [Part::Cylinder] Cylinder066
  Angle = 360
  AttacherType = Attacher::AttachEngine3D
  Height = 10
  Placement = pos=(77.15,12,4.68) rot=(1,0,0;1.5708rad)
  Radius = 2
FEATURE [Part::MultiFuse] Fusion144  label="removeFromThreadedInsertHousing"
  Shapes = -> [Cylinder065,Cylinder064,Cylinder,Cylinder066]
FEATURE [Part::Cut] Cut068  label="pcbStands001"
  Base = -> Cut064
  Tool = -> Fusion144
FEATURE [Part::MultiFuse] Fusion145
  Shapes = -> [Cut068,Fusion143]
FEATURE [Part::MultiFuse] Fusion146
  Shapes = -> [Fusion145]
FEATURE [Part::MultiFuse] Fusion147  label="bottom022"
  Shapes = -> [Cut067,Fusion146]
FEATURE [Part::MultiFuse] Fusion148  label="casePillars005"
  Shapes = -> [Cut047,Fusion092]
FEATURE [Part::MultiFuse] Fusion149  label="bottom023"
  Shapes = -> [Fusion124,Fusion113,Fusion147]
